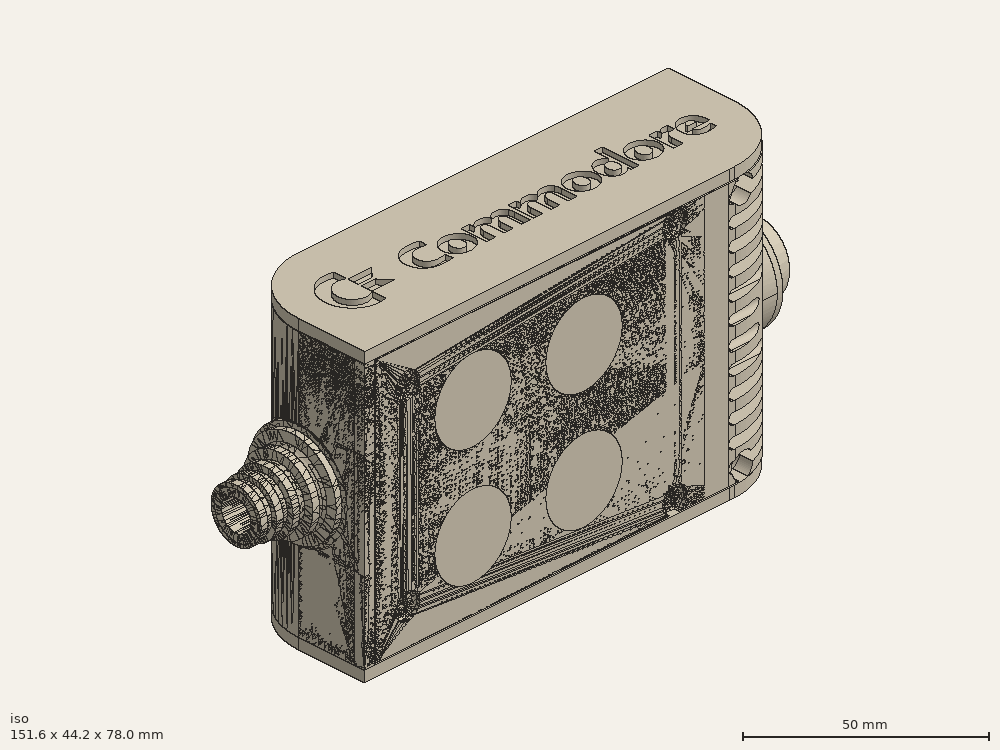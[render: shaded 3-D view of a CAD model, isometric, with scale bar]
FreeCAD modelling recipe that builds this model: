
FCSTD DOCUMENT  (FreeCAD 0.19R0.19.2)
Label: enclosure_221FCStd
License: All rights reserved
LicenseURL: http://en.wikipedia.org/wiki/All_rights_reserved
objects: Part::Revolution×152, Part::MultiFuse×146, Part::Feature×146, Sketcher::SketchObject×89, Part::Extrusion×74, Part::Cut×72, Part::Cylinder×70, Part::Fillet×58, Part::Box×38, App::MeasureDistance×4, Part::Chamfer×4, Part::FeaturePython×2, Image::ImagePlane×1, PartDesign::Body×1, Part::Mirroring×1
note: 853 computed .brp shape members not serialized (recipe doc carries the construction recipe); baked Part::Feature solids carry a one-line shape summary decoded from their .brp

FEATURE [Sketcher::SketchObject] Sketch  label="topSketch"
  FullyConstrained = true
  sketch-geometry (20):
    g0: LineSegment StartX=5.21097e-06 StartY=3 StartZ=0 EndX=5.21097e-06 EndY=19 EndZ=0
    g1: ArcOfCircle CenterX=19 CenterY=19 CenterZ=0 NormalX=0 NormalY=0 NormalZ=1 AngleXU=0 Radius=19 StartAngle=1.5708 EndAngle=3.14159
    g2: ArcOfCircle CenterX=19 CenterY=19 CenterZ=0 NormalX=0 NormalY=0 NormalZ=1 AngleXU=0 Radius=16 StartAngle=1.5708 EndAngle=3.14159
    g3: LineSegment StartX=114 StartY=35 StartZ=0 EndX=19 EndY=35 EndZ=0
    g4: LineSegment StartX=5.21097e-06 StartY=3 StartZ=0 EndX=5.21097e-06 EndY=0 EndZ=0
    g5: LineSegment StartX=3 StartY=0 StartZ=0 EndX=5.21097e-06 EndY=0 EndZ=0
    g6: LineSegment StartX=3 StartY=19 StartZ=0 EndX=3 EndY=0 EndZ=0
    g7: LineSegment StartX=19 StartY=38 StartZ=0 EndX=124 EndY=38 EndZ=0
    g8: Circle CenterX=119 CenterY=35 CenterZ=0 NormalX=0 NormalY=0 NormalZ=1 AngleXU=0 Radius=1
    g9: Circle CenterX=121 CenterY=35 CenterZ=0 NormalX=0 NormalY=0 NormalZ=1 AngleXU=0 Radius=1
    g10: Circle CenterX=121 CenterY=33 CenterZ=0 NormalX=0 NormalY=0 NormalZ=1 AngleXU=0 Radius=1
    g11: BSplineCurve PolesCount=3 KnotsCount=2 Degree=2 IsPeriodic=0
    g12: GeomPoint X=119 Y=35 Z=0
    g13: GeomPoint X=121 Y=33 Z=0
    g14: LineSegment StartX=119 StartY=35 StartZ=0 EndX=114 EndY=35 EndZ=0
    g15: ArcOfCircle CenterX=105 CenterY=19 CenterZ=0 NormalX=0 NormalY=0 NormalZ=1 AngleXU=0 Radius=19 StartAngle=5.7297 EndAngle=6.28319
    g16: ArcOfCircle CenterX=105 CenterY=19 CenterZ=0 NormalX=0 NormalY=0 NormalZ=1 AngleXU=0 Radius=16 StartAngle=5.60905 EndAngle=6.28319
    g17: LineSegment StartX=121 StartY=33 StartZ=0 EndX=121 EndY=19 EndZ=0
    g18: LineSegment StartX=124 StartY=38 StartZ=0 EndX=124 EndY=19 EndZ=0
    g19: LineSegment StartX=117.5 StartY=9.01251 StartZ=0 EndX=121.163 EndY=9.0125 EndZ=0
  constraints (46):
    c: Vertical(g0)
    c: Block(g0)
    c: Coincident(g1,g0)
    c: Block(g1)
    c: Coincident(g2,g1)
    c: Block(g2)
    c: Coincident(g3,g2)
    c: Horizontal(g3)
    c: Tangent(g3,g2)
    c: Coincident(g4,g0)
    c: Distance(g4) = 3
    c: Vertical(g4)
    c: Coincident(g5,g4)
    c: Horizontal(g5)
    c: Coincident(g6,g2)
    c: Coincident(g6,g5)
    c: Vertical(g6)
    c: Horizontal(g7)
    c: Distance(g7) = 105
    c: Coincident(g7,g1)
    c: Block(g3)
    c: Weight(g8) = 1
    c: Equal(g8,g9)
    c: Equal(g8,g10)
    c: InternalAlignment(g8,g11)
    c: InternalAlignment(g9,g11)
    c: InternalAlignment(g10,g11)
    c: InternalAlignment(g12,g11)
    c: InternalAlignment(g13,g11)
    c: Block(g11)
    c: Coincident(g14,g11)
    c: Coincident(g14,g3)
    c: Horizontal(g14)
    c: Block(g15)
    c: Coincident(g16,g15)
    c: Block(g16)
    c: Coincident(g17,g11)
    c: Coincident(g17,g16)
    c: Vertical(g17)
    c: Distance(g17) = 14
    c: Coincident(g18,g7)
    c: Coincident(g18,g15)
    c: Vertical(g18)
    c: Distance(g18) = 19
    c: Coincident(g19,g16)
    c: Coincident(g19,g15)
FEATURE [Sketcher::SketchObject] Sketch001  label="bottomSketch"
  FullyConstrained = true
  sketch-geometry (32):
    g0: LineSegment StartX=3.3 StartY=-6.03275e-07 StartZ=0 EndX=98 EndY=-6.03275e-07 EndZ=0
    g1: ArcOfCircle CenterX=98 CenterY=19 CenterZ=0 NormalX=0 NormalY=0 NormalZ=1 AngleXU=0 Radius=19 StartAngle=4.71239 EndAngle=5.71103
    g2: LineSegment StartX=6.3 StartY=8 StartZ=0 EndX=3.3 EndY=8 EndZ=0
    g3: LineSegment StartX=3.3 StartY=8 StartZ=0 EndX=3.3 EndY=-6.03275e-07 EndZ=0
    g4: ArcOfCircle CenterX=8.3 CenterY=5 CenterZ=0 NormalX=0 NormalY=0 NormalZ=1 AngleXU=0 Radius=2 StartAngle=3.14159 EndAngle=4.71239
    g5: LineSegment StartX=6.3 StartY=8 StartZ=0 EndX=6.3 EndY=5 EndZ=0
    g6: ArcOfCircle CenterX=98 CenterY=19 CenterZ=0 NormalX=0 NormalY=0 NormalZ=1 AngleXU=0 Radius=12.7 StartAngle=4.71239 EndAngle=6.28319
    g7: LineSegment StartX=94.7 StartY=3 StartZ=0 EndX=8.3 EndY=3 EndZ=0
    g8-g12: Circle x5 (B-spline internal-alignment scaffolding for g13; pole/knot coordinates omitted)
    g13: BSplineCurve PolesCount=5 KnotsCount=3 Degree=3 IsPeriodic=0
    g14: GeomPoint X=98 Y=6.3 Z=0
    g15: GeomPoint X=96.3938 Y=4.71946 Z=0
    g16: GeomPoint X=94.7 Y=3 Z=0
    g17-g23: Circle x7 (B-spline internal-alignment scaffolding for g24; pole/knot coordinates omitted)
    g24: BSplineCurve PolesCount=7 KnotsCount=5 Degree=3 IsPeriodic=0
    g25-g29: GeomPoint x5 (B-spline internal-alignment scaffolding for g24; pole/knot coordinates omitted)
    g30: ArcOfCircle CenterX=98 CenterY=19 CenterZ=0 NormalX=0 NormalY=0 NormalZ=1 AngleXU=0 Radius=15.7 StartAngle=5.81226 EndAngle=6.28319
    g31: LineSegment StartX=110.7 StartY=19 StartZ=0 EndX=113.7 EndY=19 EndZ=0
  constraints (41):
    c: Horizontal(g0)
    c: Coincident(g1,g0)
    c: Block(g1)
    c: Horizontal(g2)
    c: Distance(g2) = 3
    c: Coincident(g3,g2)
    c: Vertical(g3)
    c: Coincident(g3,g0)
    c: Block(g4)
    c: Block(g2)
    c: Coincident(g5,g2)
    c: Coincident(g5,g4)
    c: Vertical(g5)
    c: Coincident(g6,g1)
    c: Block(g6)
    c: Coincident(g7,g4)
    c: Horizontal(g7)
    c: Block(g0)
    c: Block(g7)
    c: Block(g3)
    c: Coincident(g13,g6)
    c: Weight(g8) = 1
    c: Equal(g8, g9-g12) x4
    c: Coincident(g13,g7)
    c: InternalAlignment(g8-g12 -> g13) x5
    c: InternalAlignment(g14,g13)
    c: InternalAlignment(g15,g13)
    c: InternalAlignment(g16,g13)
    c: Block(g13)
    c: Weight(g17) = 1
    c: Equal(g17, g18-g23) x6
    c: Coincident(g24,g1)
    c: InternalAlignment(g17-g23 -> g24) x7
    c: InternalAlignment(g25-g29 -> g24) x5
    c: Block(g24)
    c: Coincident(g30,g24)
    c: Coincident(g31,g6)
    c: Coincident(g31,g30)
    c: Horizontal(g31)
    c: Block(g31)
    c: Block(g30)
FEATURE [Part::Extrusion] Extrude  label="top"
  Base = -> Sketch
  Dir = (0,0,1)
  DirMode = 2
  FaceMakerClass = Part::FaceMakerBullseye
  LengthFwd = 72
  LengthRev = 0
  Solid = true
  Symmetric = false
FEATURE [Part::Extrusion] Extrude001  label="bottom"
  Base = -> Sketch001
  Dir = (0,0,1)
  DirMode = 2
  FaceMakerClass = Part::FaceMakerBullseye
  LengthFwd = 71.4
  LengthRev = 0
  Placement = pos=(0,0,0.3) rot=(0,0,1;0rad)
  Solid = true
  Symmetric = false
FEATURE [Sketcher::SketchObject] Sketch002  label="topSketch001"
  FullyConstrained = true
  sketch-geometry (8):
    g0: ArcOfCircle CenterX=19 CenterY=19.0975 CenterZ=0 NormalX=0 NormalY=0 NormalZ=1 AngleXU=0 Radius=18.9025 StartAngle=1.5708 EndAngle=3.14674
    g1: LineSegment StartX=0.0977805 StartY=19.0003 StartZ=0 EndX=0.0977805 EndY=0.000251602 EndZ=0
    g2: LineSegment StartX=19 StartY=38 StartZ=0 EndX=124 EndY=38 EndZ=0
    g3: LineSegment StartX=0.0977805 StartY=0.000251602 StartZ=0 EndX=105.098 EndY=0.000251602 EndZ=0
    g4: LineSegment StartX=124 StartY=38 StartZ=0 EndX=125.616 EndY=38 EndZ=0
    g5: LineSegment StartX=105.098 StartY=0.000251602 StartZ=0 EndX=106.713 EndY=0.000251602 EndZ=0
    g6: ArcOfCircle CenterX=106.616 CenterY=19 CenterZ=0 NormalX=0 NormalY=0 NormalZ=1 AngleXU=0 Radius=19 StartAngle=4.71754 EndAngle=6.28319
    g7: LineSegment StartX=125.616 StartY=38 StartZ=0 EndX=125.616 EndY=19 EndZ=0
  constraints (21):
    c: Block(g0)
    c: Coincident(g1,g0)
    c: Vertical(g1)
    c: Horizontal(g2)
    c: Distance(g2) = 105
    c: Coincident(g2,g0)
    c: Distance(g1) = 19
    c: Coincident(g3,g1)
    c: Horizontal(g3)
    c: Distance(g3) = 105
    c: Coincident(g4,g2)
    c: Horizontal(g4)
    c: Distance(g4) = 1.61553
    c: Horizontal(g5)
    c: Equal(g4,g5) = 1.61553
    c: Coincident(g5,g3)
    c: Block(g6)
    c: Coincident(g6,g5)
    c: Coincident(g7,g4)
    c: Coincident(g7,g6)
    c: Vertical(g7)
FEATURE [Part::Extrusion] Extrude002  label="sideA"
  Base = -> Sketch002
  Dir = (0,0,1)
  DirMode = 2
  FaceMakerClass = Part::FaceMakerBullseye
  LengthFwd = 3
  LengthRev = 0
  Placement = pos=(0,0,-3) rot=(0,0,1;0rad)
  Solid = true
  Symmetric = false
FEATURE [Sketcher::SketchObject] Sketch003  label="topSketch002"
  FullyConstrained = true
  sketch-geometry (6):
    g0: LineSegment StartX=19 StartY=38 StartZ=0 EndX=117 EndY=38 EndZ=0
    g1: ArcOfCircle CenterX=19 CenterY=19 CenterZ=0 NormalX=0 NormalY=0 NormalZ=1 AngleXU=0 Radius=19 StartAngle=1.5708 EndAngle=3.14159
    g2: LineSegment StartX=117 StartY=38 StartZ=0 EndX=117 EndY=19 EndZ=0
    g3: LineSegment StartX=98 StartY=1.0161e-12 StartZ=0 EndX=5.22862e-06 EndY=1.0161e-12 EndZ=0
    g4: LineSegment StartX=5.22862e-06 StartY=19 StartZ=0 EndX=5.22862e-06 EndY=1.0161e-12 EndZ=0
    g5: ArcOfCircle CenterX=98 CenterY=19 CenterZ=0 NormalX=0 NormalY=0 NormalZ=1 AngleXU=0 Radius=19 StartAngle=4.71239 EndAngle=6.28319
  constraints (16):
    c: Horizontal(g0)
    c: Distance(g0) = 98
    c: Coincident(g1,g0)
    c: Block(g1)
    c: Coincident(g2,g0)
    c: Vertical(g2)
    c: Distance(g2) = 19
    c: Horizontal(g3)
    c: Coincident(g4,g1)
    c: Vertical(g4)
    c: Coincident(g3,g4)
    c: Block(g3)
    c: Coincident(g5,g2)
    c: Coincident(g5,g3)
    c: Block(g0)
    c: Block(g5)
FEATURE [Sketcher::SketchObject] Sketch004
  FullyConstrained = true
  MapMode = 3
  Placement = pos=(0,0,0) rot=(1,0,0;1.5708rad)
  Support = -> [Extrude]
  sketch-geometry (8):
    g0: Circle CenterX=80.351 CenterY=-67.6202 CenterZ=0 NormalX=0 NormalY=0 NormalZ=1 AngleXU=0 Radius=2
    g1: Circle CenterX=80.351 CenterY=-67.6202 CenterZ=0 NormalX=0 NormalY=0 NormalZ=1 AngleXU=0 Radius=3
    g2: Circle CenterX=80.351 CenterY=-4.92017 CenterZ=0 NormalX=0 NormalY=0 NormalZ=1 AngleXU=0 Radius=2
    g3: Circle CenterX=80.351 CenterY=-4.92017 CenterZ=0 NormalX=0 NormalY=0 NormalZ=1 AngleXU=0 Radius=3
    g4: Circle CenterX=23.851 CenterY=-4.92017 CenterZ=0 NormalX=0 NormalY=0 NormalZ=1 AngleXU=0 Radius=2
    g5: Circle CenterX=23.851 CenterY=-4.92017 CenterZ=0 NormalX=0 NormalY=0 NormalZ=1 AngleXU=0 Radius=3
    g6: Circle CenterX=23.851 CenterY=-67.6202 CenterZ=0 NormalX=0 NormalY=0 NormalZ=1 AngleXU=0 Radius=2
    g7: Circle CenterX=23.851 CenterY=-67.6202 CenterZ=0 NormalX=0 NormalY=0 NormalZ=1 AngleXU=0 Radius=3
  constraints (8):
    c: Block(g3)
    c: Block(g2)
    c: Block(g1)
    c: Block(g0)
    c: Block(g6)
    c: Block(g7)
    c: Block(g4)
    c: Block(g5)
FEATURE [Part::Extrusion] Extrude004
  Base = -> Sketch004
  Dir = (0,-1,2e-16)
  DirMode = 2
  FaceMakerClass = Part::FaceMakerBullseye
  LengthFwd = 6
  LengthRev = 0
  Placement = pos=(0,9,0) rot=(0,0,1;0rad)
  Solid = true
  Symmetric = false
FEATURE [Sketcher::SketchObject] Sketch005
  FullyConstrained = true
  MapMode = 3
  Placement = pos=(0,0,0) rot=(1,0,0;1.5708rad)
  Support = -> [Extrude]
  sketch-geometry (8):
    g0: Circle CenterX=80.351 CenterY=-67.6202 CenterZ=0 NormalX=0 NormalY=0 NormalZ=1 AngleXU=0 Radius=3
    g1: Circle CenterX=80.351 CenterY=-4.92017 CenterZ=0 NormalX=0 NormalY=0 NormalZ=1 AngleXU=0 Radius=3
    g2: Circle CenterX=23.851 CenterY=-4.92017 CenterZ=0 NormalX=0 NormalY=0 NormalZ=1 AngleXU=0 Radius=3
    g3: Circle CenterX=23.851 CenterY=-67.6202 CenterZ=0 NormalX=0 NormalY=0 NormalZ=1 AngleXU=0 Radius=3
    g4: Circle CenterX=23.851 CenterY=-67.6202 CenterZ=0 NormalX=0 NormalY=0 NormalZ=1 AngleXU=0 Radius=5
    g5: Circle CenterX=80.351 CenterY=-67.6202 CenterZ=0 NormalX=0 NormalY=0 NormalZ=1 AngleXU=0 Radius=5
    g6: Circle CenterX=23.851 CenterY=-4.92017 CenterZ=0 NormalX=0 NormalY=0 NormalZ=1 AngleXU=0 Radius=5
    g7: Circle CenterX=80.351 CenterY=-4.92017 CenterZ=0 NormalX=0 NormalY=0 NormalZ=1 AngleXU=0 Radius=5
  constraints (8):
    c: Block(g1)
    c: Block(g0)
    c: Block(g3)
    c: Block(g2)
    c: Block(g5)
    c: Block(g4)
    c: Block(g6)
    c: Block(g7)
FEATURE [Part::Extrusion] Extrude005
  Base = -> Sketch005
  Dir = (0,-1,2e-16)
  DirMode = 2
  FaceMakerClass = Part::FaceMakerBullseye
  LengthFwd = 2
  LengthRev = 0
  Solid = true
  Symmetric = false
FEATURE [Sketcher::SketchObject] Sketch006
  FullyConstrained = true
  MapMode = 3
  Placement = pos=(0,0,0) rot=(1,0,0;1.5708rad)
  sketch-geometry (8):
    g0: Circle CenterX=80.351 CenterY=-67.6202 CenterZ=0 NormalX=0 NormalY=0 NormalZ=1 AngleXU=0 Radius=3
    g1: Circle CenterX=80.351 CenterY=-4.92017 CenterZ=0 NormalX=0 NormalY=0 NormalZ=1 AngleXU=0 Radius=3
    g2: Circle CenterX=23.851 CenterY=-4.92017 CenterZ=0 NormalX=0 NormalY=0 NormalZ=1 AngleXU=0 Radius=3
    g3: Circle CenterX=23.851 CenterY=-67.6202 CenterZ=0 NormalX=0 NormalY=0 NormalZ=1 AngleXU=0 Radius=3
    g4: Circle CenterX=23.851 CenterY=-67.6202 CenterZ=0 NormalX=0 NormalY=0 NormalZ=1 AngleXU=0 Radius=5
    g5: Circle CenterX=80.351 CenterY=-67.6202 CenterZ=0 NormalX=0 NormalY=0 NormalZ=1 AngleXU=0 Radius=5
    g6: Circle CenterX=23.851 CenterY=-4.92017 CenterZ=0 NormalX=0 NormalY=0 NormalZ=1 AngleXU=0 Radius=5
    g7: Circle CenterX=80.351 CenterY=-4.92017 CenterZ=0 NormalX=0 NormalY=0 NormalZ=1 AngleXU=0 Radius=5
  constraints (8):
    c: Block(g1)
    c: Block(g0)
    c: Block(g3)
    c: Block(g2)
    c: Block(g5)
    c: Block(g4)
    c: Block(g6)
    c: Block(g7)
FEATURE [Part::Extrusion] Extrude007
  Base = -> Sketch006
  Dir = (0,-1,2e-16)
  DirMode = 2
  FaceMakerClass = Part::FaceMakerBullseye
  LengthFwd = 2
  LengthRev = 0
  Solid = true
  Symmetric = false
FEATURE [Part::Fillet] Fillet
  Base = -> Extrude007
  Edges = 4 edges r=1.99: [Edge6,Edge12,Edge18,Edge24]
FEATURE [Part::Cut] Cut
  Base = -> Extrude005
  Placement = pos=(0,5,0) rot=(0,0,1;0rad)
  Tool = -> Fillet
FEATURE [Part::MultiFuse] Fusion  label="pCBScrews"
  Placement = pos=(-2.5,0,72.3) rot=(0,0,1;0rad)
  Shapes = -> [Extrude004,Cut]
FEATURE [App::MeasureDistance] Distance  label="Distance: 0.69 mm"
  Distance = 0.685967
  P1 = (24.0138,2.9647,0.3)
  P2 = (23.8901,3,-0.373787)
FEATURE [App::MeasureDistance] Distance001  label="Distance: 0.53 mm"
  Distance = 0.533607
  P1 = (80.2939,3,72.2334)
  P2 = (80.281,2.99661,71.7)
FEATURE [Part::Fillet] Fillet001
  Base = -> Extrude001
  Edges = 1 edges r=2.4: [Edge17]
FEATURE [Part::Fillet] Fillet002  label="bottom001"
  Base = -> Fillet001
  Edges = 1 edges r=2.4: [Edge36]
FEATURE [Part::Fillet] Fillet003  label="top001"
  Base = -> Extrude
  Edges = 1 edges r=2: [Edge1]
FEATURE [Sketcher::SketchObject] Sketch007
  FullyConstrained = true
  sketch-geometry (16):
    g0: LineSegment StartX=4 StartY=0 StartZ=0 EndX=4 EndY=2.4 EndZ=0
    g1: LineSegment StartX=4 StartY=2.4 StartZ=0 EndX=7 EndY=2.4 EndZ=0
    g2: LineSegment StartX=4 StartY=0 StartZ=0 EndX=5.7 EndY=0 EndZ=0
    g3: LineSegment StartX=5.7 StartY=0 StartZ=0 EndX=5.7 EndY=-5.6 EndZ=0
    g4-g8: Circle x5 (B-spline internal-alignment scaffolding for g9; pole/knot coordinates omitted)
    g9: BSplineCurve PolesCount=5 KnotsCount=3 Degree=3 IsPeriodic=0
    g10: GeomPoint X=7 Y=2.4 Z=0
    g11: GeomPoint X=10.4582 Y=-1.55472 Z=0
    g12: GeomPoint X=14 Y=-5.6 Z=0
    g13: LineSegment StartX=14 StartY=-5.6 StartZ=0 EndX=14 EndY=-14.1 EndZ=0
    g14: LineSegment StartX=14 StartY=-14.1 StartZ=0 EndX=6.5 EndY=-14.1 EndZ=0
    g15: LineSegment StartX=5.7 StartY=-5.6 StartZ=0 EndX=6.5 EndY=-14.1 EndZ=0
  constraints (28):
    c: Distance(g0) = 2.4
    c: Vertical(g0)
    c: Block(g0)
    c: Coincident(g1,g0)
    c: Horizontal(g1)
    c: Distance(g1) = 3
    c: Coincident(g2,g0)
    c: Horizontal(g2)
    c: Distance(g2) = 1.7
    c: Coincident(g3,g2)
    c: Vertical(g3)
    c: Distance(g3) = 5.6
    c: Coincident(g9,g1)
    c: Weight(g4) = 1
    c: Equal(g4, g5-g8) x4
    c: InternalAlignment(g4-g8 -> g9) x5
    c: InternalAlignment(g10,g9)
    c: InternalAlignment(g11,g9)
    c: InternalAlignment(g12,g9)
    c: Block(g9)
    c: Coincident(g13,g9)
    c: Vertical(g13)
    c: Distance(g13) = 8.5
    c: Coincident(g14,g13)
    c: Horizontal(g14)
    c: Distance(g14) = 7.5
    c: Coincident(g15,g3)
    c: Coincident(g15,g14)
FEATURE [Part::Feature] Face
  shape: bbox 10 x 16.5 x 2e-07 mm, 1 faces, 0 solids (baked)
FEATURE [Part::Revolution] Revolve  label="plugHousing"
  Angle = 360
  Axis = (0,1,0)
  Base = (0,0,0)
  FaceMakerClass = Part::FaceMakerBullseye
  Placement = pos=(0,0,36.15) rot=(0,0,1;0rad)
  Solid = false
  Source = -> Face
  Symmetric = false
FEATURE [Part::Feature] Face001
  shape: bbox 10 x 16.5 x 2e-07 mm, 1 faces, 0 solids (baked)
FEATURE [Part::Revolution] Revolve001  label="plugHousing001"
  Angle = 360
  Axis = (0,1,0)
  Base = (0,0,0)
  FaceMakerClass = Part::FaceMakerBullseye
  Placement = pos=(0,0,36.15) rot=(0,0,1;0rad)
  Solid = false
  Source = -> Face001
  Symmetric = false
FEATURE [Part::MultiFuse] Fusion001  label="plugHousing002"
  Placement = pos=(0,0,0) rot=(0,0,1;1.5708rad)
  Shapes = -> [Revolve001,Revolve]
FEATURE [Part::Feature] Face002
  shape: bbox 10 x 16.5 x 2e-07 mm, 1 faces, 0 solids (baked)
FEATURE [Part::Revolution] Revolve003  label="plugHousing005"
  Angle = 360
  Axis = (0,1,0)
  Base = (0,0,0)
  FaceMakerClass = Part::FaceMakerBullseye
  Placement = pos=(0,0,36.15) rot=(0,0,1;0rad)
  Solid = false
  Source = -> Face002
  Symmetric = false
FEATURE [Part::Feature] Face003
  shape: bbox 10 x 16.5 x 2e-07 mm, 1 faces, 0 solids (baked)
FEATURE [Part::Revolution] Revolve002  label="plugHousing003"
  Angle = 360
  Axis = (0,1,0)
  Base = (0,0,0)
  FaceMakerClass = Part::FaceMakerBullseye
  Placement = pos=(0,0,36.15) rot=(0,0,1;0rad)
  Solid = false
  Source = -> Face003
  Symmetric = false
FEATURE [Part::MultiFuse] Fusion002  label="plugHousing004"
  Placement = pos=(0,0,0) rot=(0,0,1;1.5708rad)
  Shapes = -> [Revolve002,Revolve003]
FEATURE [Part::MultiFuse] Fusion003  label="plugHousing006"
  Placement = pos=(0,19,0) rot=(0,0,1;3.14159rad)
  Shapes = -> [Fusion002,Fusion001]
FEATURE [Part::Feature] Face004
  shape: bbox 10 x 16.5 x 2e-07 mm, 1 faces, 0 solids (baked)
FEATURE [Part::Revolution] Revolve006  label="plugHousing010"
  Angle = 360
  Axis = (0,1,0)
  Base = (0,0,0)
  FaceMakerClass = Part::FaceMakerBullseye
  Placement = pos=(0,0,36.15) rot=(0,0,1;0rad)
  Solid = false
  Source = -> Face004
  Symmetric = false
FEATURE [Part::Feature] Face005
  shape: bbox 10 x 16.5 x 2e-07 mm, 1 faces, 0 solids (baked)
FEATURE [Part::Revolution] Revolve007  label="plugHousing011"
  Angle = 360
  Axis = (0,1,0)
  Base = (0,0,0)
  FaceMakerClass = Part::FaceMakerBullseye
  Placement = pos=(0,0,36.15) rot=(0,0,1;0rad)
  Solid = false
  Source = -> Face005
  Symmetric = false
FEATURE [Part::Feature] Face006
  shape: bbox 10 x 16.5 x 2e-07 mm, 1 faces, 0 solids (baked)
FEATURE [Part::Revolution] Revolve004  label="plugHousing007"
  Angle = 360
  Axis = (0,1,0)
  Base = (0,0,0)
  FaceMakerClass = Part::FaceMakerBullseye
  Placement = pos=(0,0,36.15) rot=(0,0,1;0rad)
  Solid = false
  Source = -> Face006
  Symmetric = false
FEATURE [Part::MultiFuse] Fusion004  label="plugHousing009"
  Placement = pos=(0,0,0) rot=(0,0,1;1.5708rad)
  Shapes = -> [Revolve004,Revolve007]
FEATURE [Part::Feature] Face007
  shape: bbox 10 x 16.5 x 2e-07 mm, 1 faces, 0 solids (baked)
FEATURE [Part::Revolution] Revolve005  label="plugHousing008"
  Angle = 360
  Axis = (0,1,0)
  Base = (0,0,0)
  FaceMakerClass = Part::FaceMakerBullseye
  Placement = pos=(0,0,36.15) rot=(0,0,1;0rad)
  Solid = false
  Source = -> Face007
  Symmetric = false
FEATURE [Part::MultiFuse] Fusion005  label="plugHousing012"
  Placement = pos=(0,0,0) rot=(0,0,1;1.5708rad)
  Shapes = -> [Revolve006,Revolve005]
FEATURE [Part::MultiFuse] Fusion006  label="plugHousing013"
  Placement = pos=(0,19,0) rot=(0,0,1;3.14159rad)
  Shapes = -> [Fusion005,Fusion004]
FEATURE [Part::MultiFuse] Fusion007  label="plugHousing014"
  Placement = pos=(122.621,0,-0.15) rot=(0,0,1;0rad)
  Shapes = -> [Fusion003,Fusion006]
FEATURE [Part::Cylinder] Cylinder002
  Angle = 360
  AttacherType = Attacher::AttachEngine3D
  Height = 20
  Placement = pos=(0,0,36.15) rot=(0,0,1;0rad)
  Radius = 4
FEATURE [Part::Cylinder] Cylinder003
  Angle = 360
  AttacherType = Attacher::AttachEngine3D
  Height = 10
  Placement = pos=(0,0,36.15) rot=(0,0,1;0rad)
  Radius = 4
FEATURE [Part::MultiFuse] Fusion009  label="removeToCreateHoleForPlugHousing"
  Placement = pos=(70,19,36.15) rot=(0,1,0;1.5708rad)
  Shapes = -> [Cylinder002,Cylinder003]
FEATURE [Part::Cylinder] Cylinder004
  Angle = 360
  AttacherType = Attacher::AttachEngine3D
  Height = 20
  Placement = pos=(0,0,36.15) rot=(0,0,1;0rad)
  Radius = 4
FEATURE [Part::Cylinder] Cylinder005
  Angle = 360
  AttacherType = Attacher::AttachEngine3D
  Height = 10
  Placement = pos=(0,0,36.15) rot=(0,0,1;0rad)
  Radius = 4
FEATURE [Part::MultiFuse] Fusion010  label="removeToCreateHoleForPlugHousing001"
  Placement = pos=(70,19,36.15) rot=(0,1,0;1.5708rad)
  Shapes = -> [Cylinder004,Cylinder005]
FEATURE [Part::Cut] Cut001
  Base = -> Fillet003
  Tool = -> Fusion010
FEATURE [Part::Cut] Cut002  label="Bottom"
  Base = -> Fillet002
  Tool = -> Fusion009
FEATURE [Part::Feature] Face008
  shape: bbox 10 x 16.5 x 2e-07 mm, 1 faces, 0 solids (baked)
FEATURE [Part::Revolution] Revolve011  label="plugHousing021"
  Angle = 360
  Axis = (0,1,0)
  Base = (0,0,0)
  FaceMakerClass = Part::FaceMakerBullseye
  Placement = pos=(0,0,36.15) rot=(0,0,1;0rad)
  Solid = false
  Source = -> Face008
  Symmetric = false
FEATURE [Part::Feature] Face009
  shape: bbox 10 x 16.5 x 2e-07 mm, 1 faces, 0 solids (baked)
FEATURE [Part::Revolution] Revolve012  label="plugHousing022"
  Angle = 360
  Axis = (0,1,0)
  Base = (0,0,0)
  FaceMakerClass = Part::FaceMakerBullseye
  Placement = pos=(0,0,36.15) rot=(0,0,1;0rad)
  Solid = false
  Source = -> Face009
  Symmetric = false
FEATURE [Part::Feature] Face010 .. Face013  x4 (patterned run collapsed; names and placements below)
  shape: bbox 10 x 16.5 x 2e-07 mm, 1 faces, 0 solids (baked)
FEATURE [Part::Revolution] Revolve015  label="plugHousing027"
  Angle = 360
  Axis = (0,1,0)
  Base = (0,0,0)
  FaceMakerClass = Part::FaceMakerBullseye
  Placement = pos=(0,0,36.15) rot=(0,0,1;0rad)
  Solid = false
  Source = -> Face013
  Symmetric = false
FEATURE [Part::Feature] Face014
  shape: bbox 10 x 16.5 x 2e-07 mm, 1 faces, 0 solids (baked)
FEATURE [Part::Feature] Face015
  shape: bbox 10 x 16.5 x 2e-07 mm, 1 faces, 0 solids (baked)
FEATURE [Part::Feature] Face016
  shape: bbox 10 x 16.5 x 2e-07 mm, 1 faces, 0 solids (baked)
FEATURE [Part::Revolution] Revolve019  label="plugHousing033"
  Angle = 360
  Axis = (0,1,0)
  Base = (0,0,0)
  FaceMakerClass = Part::FaceMakerBullseye
  Placement = pos=(0,0,36.15) rot=(0,0,1;0rad)
  Solid = false
  Source = -> Face016
  Symmetric = false
FEATURE [Part::Feature] Face017
  shape: bbox 10 x 16.5 x 2e-07 mm, 1 faces, 0 solids (baked)
FEATURE [Part::Revolution] Revolve020  label="plugHousing034"
  Angle = 360
  Axis = (0,1,0)
  Base = (0,0,0)
  FaceMakerClass = Part::FaceMakerBullseye
  Placement = pos=(0,0,36.15) rot=(0,0,1;0rad)
  Solid = false
  Source = -> Face017
  Symmetric = false
FEATURE [Part::Feature] Face018
  shape: bbox 10 x 16.5 x 2e-07 mm, 1 faces, 0 solids (baked)
FEATURE [Part::Revolution] Revolve016  label="plugHousing030"
  Angle = 360
  Axis = (0,1,0)
  Base = (0,0,0)
  FaceMakerClass = Part::FaceMakerBullseye
  Placement = pos=(0,0,36.15) rot=(0,0,1;0rad)
  Solid = false
  Source = -> Face018
  Symmetric = false
FEATURE [Part::MultiFuse] Fusion020  label="plugHousing038"
  Placement = pos=(0,0,0) rot=(0,0,1;1.5708rad)
  Shapes = -> [Revolve016,Revolve020]
FEATURE [Part::Feature] Face019
  shape: bbox 10 x 16.5 x 2e-07 mm, 1 faces, 0 solids (baked)
FEATURE [Part::Feature] Face020
  shape: bbox 10 x 16.5 x 2e-07 mm, 1 faces, 0 solids (baked)
FEATURE [Part::Revolution] Revolve017  label="plugHousing031"
  Angle = 360
  Axis = (0,1,0)
  Base = (0,0,0)
  FaceMakerClass = Part::FaceMakerBullseye
  Placement = pos=(0,0,36.15) rot=(0,0,1;0rad)
  Solid = false
  Source = -> Face020
  Symmetric = false
FEATURE [Part::MultiFuse] Fusion021  label="plugHousing039"
  Placement = pos=(0,0,0) rot=(0,0,1;1.5708rad)
  Shapes = -> [Revolve019,Revolve017]
FEATURE [Part::MultiFuse] Fusion023  label="plugHousing041"
  Placement = pos=(0,19,0) rot=(0,0,1;3.14159rad)
  Shapes = -> [Fusion021,Fusion020]
FEATURE [Part::Revolution] Revolve022  label="plugHousing043"
  Angle = 360
  Axis = (0,1,0)
  Base = (0,0,0)
  FaceMakerClass = Part::FaceMakerBullseye
  Placement = pos=(0,0,36.15) rot=(0,0,1;0rad)
  Solid = false
  Source = -> Face019
  Symmetric = false
FEATURE [Part::Feature] Face021
  shape: bbox 10 x 16.5 x 2e-07 mm, 1 faces, 0 solids (baked)
FEATURE [Part::Revolution] Revolve023  label="plugHousing044"
  Angle = 360
  Axis = (0,1,0)
  Base = (0,0,0)
  FaceMakerClass = Part::FaceMakerBullseye
  Placement = pos=(0,0,36.15) rot=(0,0,1;0rad)
  Solid = false
  Source = -> Face021
  Symmetric = false
FEATURE [Part::Feature] Face022
  shape: bbox 10 x 16.5 x 2e-07 mm, 1 faces, 0 solids (baked)
FEATURE [Part::Revolution] Revolve018  label="plugHousing032"
  Angle = 360
  Axis = (0,1,0)
  Base = (0,0,0)
  FaceMakerClass = Part::FaceMakerBullseye
  Placement = pos=(0,0,36.15) rot=(0,0,1;0rad)
  Solid = false
  Source = -> Face022
  Symmetric = false
FEATURE [Part::MultiFuse] Fusion022  label="plugHousing040"
  Placement = pos=(0,0,0) rot=(0,0,1;1.5708rad)
  Shapes = -> [Revolve018,Revolve023]
FEATURE [Part::Feature] Face023
  shape: bbox 10 x 16.5 x 2e-07 mm, 1 faces, 0 solids (baked)
FEATURE [Part::Revolution] Revolve021  label="plugHousing035"
  Angle = 360
  Axis = (0,1,0)
  Base = (0,0,0)
  FaceMakerClass = Part::FaceMakerBullseye
  Placement = pos=(0,0,36.15) rot=(0,0,1;0rad)
  Solid = false
  Source = -> Face023
  Symmetric = false
FEATURE [Part::MultiFuse] Fusion018  label="plugHousing036"
  Placement = pos=(0,0,0) rot=(0,0,1;1.5708rad)
  Shapes = -> [Revolve022,Revolve021]
FEATURE [Part::MultiFuse] Fusion019  label="plugHousing037"
  Placement = pos=(0,19,0) rot=(0,0,1;3.14159rad)
  Shapes = -> [Fusion018,Fusion022]
FEATURE [Part::MultiFuse] Fusion024  label="plugHousing042"
  Placement = pos=(122.621,0,-0.15) rot=(0,0,1;0rad)
  Shapes = -> [Fusion023,Fusion019]
FEATURE [Part::Cylinder] Cylinder006
  Angle = 360
  AttacherType = Attacher::AttachEngine3D
  Height = 20
  Placement = pos=(0,0,36.15) rot=(0,0,1;0rad)
  Radius = 14.3
FEATURE [Part::Cylinder] Cylinder007
  Angle = 360
  AttacherType = Attacher::AttachEngine3D
  Height = 10
  Placement = pos=(0,0,36.15) rot=(0,0,1;0rad)
  Radius = 4
FEATURE [Part::MultiFuse] Fusion026  label="removeToCreteHoleForPlugHousing"
  Placement = pos=(70,19,36) rot=(0,1,0;1.5708rad)
  Shapes = -> [Cylinder006,Cylinder007]
FEATURE [Part::Box] Box001  label="Cube001"
  AttacherType = Attacher::AttachEngine3D
  Height = 28
  Length = 3
  Placement = pos=(110.7,19,22) rot=(0,0,1;0rad)
  Width = 15.7
FEATURE [Part::Cut] Cut003  label="top002"
  Base = -> Cut001
  Tool = -> Fusion007
FEATURE [Part::Revolution] Revolve008  label="plugHousing015"
  Angle = 360
  Axis = (0,1,0)
  Base = (0,0,0)
  FaceMakerClass = Part::FaceMakerBullseye
  Placement = pos=(0,0,36.15) rot=(0,0,1;0rad)
  Solid = false
  Source = -> Face010
  Symmetric = false
FEATURE [Part::MultiFuse] Fusion013  label="plugHousing020"
  Placement = pos=(0,0,0) rot=(0,0,1;1.5708rad)
  Shapes = -> [Revolve008,Revolve012]
FEATURE [Part::Cut] Cut004  label="top003"
  Base = -> Cut003
  Placement = pos=(1,0,0) rot=(0,0,1;0rad)
  Tool = -> Fusion026
FEATURE [Part::Cylinder] Cylinder008
  Angle = 360
  AttacherType = Attacher::AttachEngine3D
  Height = 20
  Placement = pos=(0,0,36.15) rot=(0,0,1;0rad)
  Radius = 10.3
FEATURE [Part::Cylinder] Cylinder009
  Angle = 360
  AttacherType = Attacher::AttachEngine3D
  Height = 10
  Placement = pos=(0,0,36.15) rot=(0,0,1;0rad)
  Radius = 4
FEATURE [Part::MultiFuse] Fusion027  label="removeToCreteHoleForPlugHousing001"
  Placement = pos=(70,19,36) rot=(0,1,0;1.5708rad)
  Shapes = -> [Cylinder008,Cylinder009]
FEATURE [Part::Cut] Cut005  label="plugHousingTab"
  Base = -> Box001
  Tool = -> Fusion027
FEATURE [Part::MultiFuse] Fusion028  label="plugHousing045"
  Shapes = -> [Fusion024,Cut005]
FEATURE [Part::Box] Box002  label="Cube002"
  AttacherType = Attacher::AttachEngine3D
  Height = 28.8
  Length = 3
  Placement = pos=(107.3,28,21.6) rot=(0,0,1;0rad)
  Width = 7
FEATURE [Part::Box] Box003  label="Cube003"
  AttacherType = Attacher::AttachEngine3D
  Height = 3
  Length = 6.4
  Placement = pos=(107.3,28,18.6) rot=(0,0,1;0rad)
  Width = 7
FEATURE [Part::Box] Box004  label="Cube004"
  AttacherType = Attacher::AttachEngine3D
  Height = 3
  Length = 6.4
  Placement = pos=(107.3,28,50.4) rot=(0,0,1;0rad)
  Width = 7
FEATURE [Part::MultiFuse] Fusion029  label="plugHousingBracketHolder"
  Shapes = -> [Box004,Box002,Box003]
FEATURE [Part::Cylinder] Cylinder010
  Angle = 360
  AttacherType = Attacher::AttachEngine3D
  Height = 20
  Placement = pos=(0,0,36.15) rot=(0,0,1;0rad)
  Radius = 14.3
FEATURE [Part::Cylinder] Cylinder011
  Angle = 360
  AttacherType = Attacher::AttachEngine3D
  Height = 10
  Placement = pos=(0,0,36.15) rot=(0,0,1;0rad)
  Radius = 4
FEATURE [Part::MultiFuse] Fusion030  label="removeToCreteHoleForPlugHousing002"
  Placement = pos=(70,19,36) rot=(0,1,0;1.5708rad)
  Shapes = -> [Cylinder010,Cylinder011]
FEATURE [Part::Cut] Cut006  label="plugHousingBracketHolder001"
  Base = -> Fusion029
  Tool = -> Fusion030
FEATURE [Part::Cylinder] Cylinder012
  Angle = 360
  AttacherType = Attacher::AttachEngine3D
  Height = 20
  Placement = pos=(0,0,36.15) rot=(0,0,1;0rad)
  Radius = 7
FEATURE [Part::Cylinder] Cylinder013
  Angle = 360
  AttacherType = Attacher::AttachEngine3D
  Height = 10
  Placement = pos=(0,0,36.15) rot=(0,0,1;0rad)
  Radius = 4
FEATURE [Part::MultiFuse] Fusion032  label="removeToCreteHoleForPlugHousing003"
  Placement = pos=(70,19,36) rot=(0,1,0;1.5708rad)
  Shapes = -> [Cylinder012,Cylinder013]
FEATURE [Part::Cut] Cut007  label="bottom002"
  Base = -> Cut002
  Tool = -> Fusion032
FEATURE [Sketcher::SketchObject] Sketch008
  FullyConstrained = true
  sketch-geometry (54):
    g0: LineSegment StartX=-4.2 StartY=0 StartZ=0 EndX=-6.2 EndY=0 EndZ=0
    g1: LineSegment StartX=-14 StartY=-18 StartZ=0 EndX=-14 EndY=-26.5 EndZ=0
    g2: LineSegment StartX=-4.2 StartY=0 StartZ=0 EndX=-4.2 EndY=-13.4877 EndZ=0
    g3: Circle CenterX=-4.2 CenterY=-13.4877 CenterZ=0 NormalX=0 NormalY=0 NormalZ=1 AngleXU=0 Radius=1
    g4: Circle CenterX=-4.2 CenterY=-26.5 CenterZ=0 NormalX=0 NormalY=0 NormalZ=1 AngleXU=0 Radius=1
    g5: Circle CenterX=-8.2 CenterY=-26.5 CenterZ=0 NormalX=0 NormalY=0 NormalZ=1 AngleXU=0 Radius=1
    g6: BSplineCurve PolesCount=3 KnotsCount=2 Degree=2 IsPeriodic=0
    g7: GeomPoint X=-4.2 Y=-13.4877 Z=0
    g8: GeomPoint X=-8.2 Y=-26.5 Z=0
    g9: LineSegment StartX=-14 StartY=-26.5 StartZ=0 EndX=-8.2 EndY=-26.5 EndZ=0
    g10: LineSegment StartX=-10.15 StartY=-12 StartZ=0 EndX=-10.15 EndY=-14 EndZ=0
    g11: LineSegment StartX=-12.8401 StartY=-16 StartZ=0 EndX=-10.1571 EndY=-16 EndZ=0
    g12: LineSegment StartX=-10.15 StartY=-14 StartZ=0 EndX=-8.70761 EndY=-14 EndZ=0
    g13: LineSegment StartX=-12.8401 StartY=-16 StartZ=0 EndX=-12.8401 EndY=-17.6958 EndZ=0
    g14: LineSegment StartX=-10.15 StartY=-12 StartZ=0 EndX=-7.79258 EndY=-12 EndZ=0
    g15: Circle CenterX=-6.2215 CenterY=-2 CenterZ=0 NormalX=0 NormalY=0 NormalZ=1 AngleXU=0 Radius=1
    g16: Circle CenterX=-6.22762 CenterY=-2.58724 CenterZ=0 NormalX=0 NormalY=0 NormalZ=1 AngleXU=0 Radius=1
    g17: Circle CenterX=-6.32538 CenterY=-4 CenterZ=0 NormalX=0 NormalY=0 NormalZ=1 AngleXU=0 Radius=1
    g18: BSplineCurve PolesCount=3 KnotsCount=2 Degree=2 IsPeriodic=0
    g19: GeomPoint X=-6.2215 Y=-2 Z=0
    g20: GeomPoint X=-6.32538 Y=-4 Z=0
    g21: Circle CenterX=-6.48644 CenterY=-5.99526 CenterZ=0 NormalX=0 NormalY=0 NormalZ=1 AngleXU=0 Radius=1
    g22: Circle CenterX=-6.58486 CenterY=-6.99526 CenterZ=0 NormalX=0 NormalY=0 NormalZ=1 AngleXU=0 Radius=1
    g23: Circle CenterX=-6.77343 CenterY=-8 CenterZ=0 NormalX=0 NormalY=0 NormalZ=1 AngleXU=0 Radius=1
    g24: BSplineCurve PolesCount=3 KnotsCount=2 Degree=2 IsPeriodic=0
    g25: GeomPoint X=-6.48644 Y=-5.99526 Z=0
    g26: GeomPoint X=-6.77343 Y=-8 Z=0
    g27: Circle CenterX=-7.19003 CenterY=-10 CenterZ=0 NormalX=0 NormalY=0 NormalZ=1 AngleXU=0 Radius=1
    g28: Circle CenterX=-7.44407 CenterY=-11.0915 CenterZ=0 NormalX=0 NormalY=0 NormalZ=1 AngleXU=0 Radius=1
    g29: Circle CenterX=-7.79258 CenterY=-12 CenterZ=0 NormalX=0 NormalY=0 NormalZ=1 AngleXU=0 Radius=1
    g30: BSplineCurve PolesCount=3 KnotsCount=2 Degree=2 IsPeriodic=0
    g31: GeomPoint X=-7.19003 Y=-10 Z=0
    g32: GeomPoint X=-7.79258 Y=-12 Z=0
    g33: Circle CenterX=-8.70761 CenterY=-14 CenterZ=0 NormalX=0 NormalY=0 NormalZ=1 AngleXU=0 Radius=1
    g34: Circle CenterX=-9.33087 CenterY=-15.1837 CenterZ=0 NormalX=0 NormalY=0 NormalZ=1 AngleXU=0 Radius=1
    g35: Circle CenterX=-10.1571 CenterY=-16 CenterZ=0 NormalX=0 NormalY=0 NormalZ=1 AngleXU=0 Radius=1
    g36: BSplineCurve PolesCount=3 KnotsCount=2 Degree=2 IsPeriodic=0
    g37: GeomPoint X=-8.70761 Y=-14 Z=0
    g38: GeomPoint X=-10.1571 Y=-16 Z=0
    g39: Circle CenterX=-12.8401 CenterY=-17.6958 CenterZ=0 NormalX=0 NormalY=0 NormalZ=1 AngleXU=0 Radius=1
    g40: Circle CenterX=-13.3521 CenterY=-17.9027 CenterZ=0 NormalX=0 NormalY=0 NormalZ=1 AngleXU=0 Radius=1
    g41: Circle CenterX=-14 CenterY=-18 CenterZ=0 NormalX=0 NormalY=0 NormalZ=1 AngleXU=0 Radius=1
    g42: BSplineCurve PolesCount=3 KnotsCount=2 Degree=2 IsPeriodic=0
    g43: GeomPoint X=-12.8401 Y=-17.6958 Z=0
    g44: GeomPoint X=-14 Y=-18 Z=0
    g45: LineSegment StartX=-6.2 StartY=0 StartZ=0 EndX=-7.2 EndY=0 EndZ=0
    g46: LineSegment StartX=-7.2 StartY=0 StartZ=0 EndX=-7.2 EndY=-2 EndZ=0
    g47: LineSegment StartX=-7.2 StartY=-2 StartZ=0 EndX=-6.2215 EndY=-2 EndZ=0
    g48: LineSegment StartX=-6.32538 StartY=-4 StartZ=0 EndX=-7.65538 EndY=-4 EndZ=0
    g49: LineSegment StartX=-7.65538 StartY=-4 StartZ=0 EndX=-7.65538 EndY=-5.99526 EndZ=0
    g50: LineSegment StartX=-7.65538 StartY=-5.99526 StartZ=0 EndX=-6.48644 EndY=-5.99526 EndZ=0
    g51: LineSegment StartX=-6.77343 StartY=-8 StartZ=0 EndX=-8.43343 EndY=-8 EndZ=0
    g52: LineSegment StartX=-8.43343 StartY=-8 StartZ=0 EndX=-8.43343 EndY=-10 EndZ=0
    g53: LineSegment StartX=-8.43343 StartY=-10 StartZ=0 EndX=-7.19003 EndY=-10 EndZ=0
  constraints (112):
    c: Horizontal(g0)
    c: Distance(g0) = 2
    c: Block(g0)
    c: Vertical(g1)
    c: Coincident(g2,g0)
    c: Vertical(g2)
    c: Block(g2)
    c: Coincident(g6,g2)
    c: Weight(g3) = 1
    c: Equal(g3,g4)
    c: Equal(g3,g5)
    c: InternalAlignment(g3,g6)
    c: InternalAlignment(g4,g6)
    c: InternalAlignment(g5,g6)
    c: InternalAlignment(g7,g6)
    c: InternalAlignment(g8,g6)
    c: Block(g6)
    c: Coincident(g9,g1)
    c: Coincident(g9,g6)
    c: Horizontal(g9)
    c: Vertical(g10)
    c: Block(g10)
    c: Horizontal(g11)
    c: Block(g11)
    c: Coincident(g12,g10)
    c: Horizontal(g12)
    c: Block(g12)
    c: Coincident(g13,g11)
    c: Vertical(g13)
    c: Block(g13)
    c: Coincident(g14,g10)
    c: Horizontal(g14)
    c: Block(g14)
    c: Block(g9)
    c: Block(g1)
    c: Weight(g15) = 1
    c: Equal(g15,g16)
    c: Equal(g15,g17)
    c: InternalAlignment(g15,g18)
    c: InternalAlignment(g16,g18)
    c: InternalAlignment(g17,g18)
    c: InternalAlignment(g19,g18)
    c: InternalAlignment(g20,g18)
    c: Weight(g21) = 1
    c: Equal(g21,g22)
    c: Equal(g21,g23)
    c: InternalAlignment(g21,g24)
    c: InternalAlignment(g22,g24)
    c: InternalAlignment(g23,g24)
    c: InternalAlignment(g25,g24)
    c: InternalAlignment(g26,g24)
    c: Weight(g27) = 1
    c: Equal(g27,g28)
    c: Equal(g27,g29)
    c: Coincident(g30,g14)
    c: InternalAlignment(g27,g30)
    c: InternalAlignment(g28,g30)
    c: InternalAlignment(g29,g30)
    c: InternalAlignment(g31,g30)
    c: InternalAlignment(g32,g30)
    c: Coincident(g36,g12)
    c: Weight(g33) = 1
    c: Equal(g33,g34)
    c: Equal(g33,g35)
    c: Coincident(g36,g11)
    c: InternalAlignment(g33,g36)
    c: InternalAlignment(g34,g36)
    c: InternalAlignment(g35,g36)
    c: InternalAlignment(g37,g36)
    c: InternalAlignment(g38,g36)
    c: Coincident(g42,g13)
    c: Weight(g39) = 1
    c: Equal(g39,g40)
    c: Equal(g39,g41)
    c: Coincident(g42,g1)
    c: InternalAlignment(g39,g42)
    c: InternalAlignment(g40,g42)
    c: InternalAlignment(g41,g42)
    c: InternalAlignment(g43,g42)
    c: InternalAlignment(g44,g42)
    c: Block(g18)
    c: Block(g24)
    c: Block(g30)
    c: Block(g36)
    c: Block(g42)
    c: Horizontal(g45)
    c: Coincident(g45,g0)
    c: Vertical(g46)
    c: Coincident(g46,g45)
    c: Coincident(g47,g46)
    c: Coincident(g47,g18)
    c: Horizontal(g47)
    c: Block(g46)
    c: Coincident(g48,g18)
    c: Horizontal(g48)
    c: Distance(g48) = 1.33
    c: Vertical(g49)
    c: Coincident(g49,g48)
    c: Coincident(g50,g49)
    c: Coincident(g50,g24)
    c: Horizontal(g50)
    c: Tangent(g50,g22)
    c: Horizontal(g51)
    c: Coincident(g51,g24)
    c: Block(g51)
    c: Vertical(g52)
    c: Block(g52)
    c: Coincident(g52,g51)
    c: Coincident(g53,g52)
    c: Coincident(g53,g30)
    c: Horizontal(g53)
    c: Distance(g1) = 8.5
FEATURE [Part::Feature] Face024
  shape: bbox 9.8 x 26.5 x 2e-07 mm, 1 faces, 0 solids (baked)
FEATURE [Part::Revolution] Revolve024
  Angle = 360
  Axis = (0,1,0)
  Base = (0,0,0)
  FaceMakerClass = Part::FaceMakerBullseye
  Placement = pos=(0,0,0) rot=(0,0,1;1.5708rad)
  Solid = false
  Source = -> Face024
  Symmetric = false
FEATURE [Part::Feature] Face025
  shape: bbox 9.8 x 26.5 x 2e-07 mm, 1 faces, 0 solids (baked)
FEATURE [Part::Revolution] Revolve025
  Angle = 360
  Axis = (0,1,0)
  Base = (0,0,0)
  FaceMakerClass = Part::FaceMakerBullseye
  Placement = pos=(0,0,0) rot=(0,0,1;1.5708rad)
  Solid = false
  Source = -> Face025
  Symmetric = false
FEATURE [Part::MultiFuse] Fusion033
  Placement = pos=(-18,19,36) rot=(0,0,1;0rad)
  Shapes = -> [Revolve025,Revolve024]
FEATURE [Part::Cylinder] Cylinder014
  Angle = 360
  AttacherType = Attacher::AttachEngine3D
  Height = 20
  Placement = pos=(0,0,36.15) rot=(0,0,1;0rad)
  Radius = 14.3
FEATURE [Part::Cylinder] Cylinder015
  Angle = 360
  AttacherType = Attacher::AttachEngine3D
  Height = 10
  Placement = pos=(0,0,36.15) rot=(0,0,1;0rad)
  Radius = 4
FEATURE [Part::MultiFuse] Fusion034  label="removeToCreteHoleForPlugHousing004"
  Placement = pos=(-42,19,36) rot=(0,1,0;1.5708rad)
  Shapes = -> [Cylinder014,Cylinder015]
FEATURE [Part::Cut] Cut008  label="top004"
  Base = -> Cut004
  Placement = pos=(-1,0,0) rot=(0,0,1;0rad)
  Tool = -> Fusion034
FEATURE [Part::Box] Box005  label="Cube005"
  AttacherType = Attacher::AttachEngine3D
  Height = 28
  Length = 3
  Placement = pos=(110.7,19,22) rot=(0,0,1;0rad)
  Width = 15.7
FEATURE [Part::Cylinder] Cylinder016
  Angle = 360
  AttacherType = Attacher::AttachEngine3D
  Height = 10
  Placement = pos=(0,0,36.15) rot=(0,0,1;0rad)
  Radius = 4
FEATURE [Part::Cylinder] Cylinder017
  Angle = 360
  AttacherType = Attacher::AttachEngine3D
  Height = 20
  Placement = pos=(0,0,36.15) rot=(0,0,1;0rad)
  Radius = 10.3
FEATURE [Part::MultiFuse] Fusion035  label="removeToCreteHoleForPlugHousing005"
  Placement = pos=(70,19,36) rot=(0,1,0;1.5708rad)
  Shapes = -> [Cylinder017,Cylinder016]
FEATURE [Part::Cut] Cut009  label="plugHousingTab001"
  Base = -> Box005
  Placement = pos=(-107.4,-14,0) rot=(0,0,1;0rad)
  Tool = -> Fusion035
FEATURE [Part::Box] Box006  label="Cube006"
  AttacherType = Attacher::AttachEngine3D
  Height = 28
  Length = 3
  Placement = pos=(110.7,19,22) rot=(0,0,1;0rad)
  Width = 15.7
FEATURE [Part::Cylinder] Cylinder018
  Angle = 360
  AttacherType = Attacher::AttachEngine3D
  Height = 10
  Placement = pos=(0,0,36.15) rot=(0,0,1;0rad)
  Radius = 4
FEATURE [Part::Cylinder] Cylinder019
  Angle = 360
  AttacherType = Attacher::AttachEngine3D
  Height = 20
  Placement = pos=(0,0,36.15) rot=(0,0,1;0rad)
  Radius = 10.3
FEATURE [Part::MultiFuse] Fusion036  label="removeToCreteHoleForPlugHousing006"
  Placement = pos=(70,19,36) rot=(0,1,0;1.5708rad)
  Shapes = -> [Cylinder019,Cylinder018]
FEATURE [Part::Cut] Cut010  label="plugHousingTab002"
  Base = -> Box006
  Placement = pos=(-107.4,-14,0) rot=(0,0,1;0rad)
  Tool = -> Fusion036
FEATURE [Part::MultiFuse] Fusion037
  Placement = pos=(9.6,23,0) rot=(0,0,1;3.14159rad)
  Shapes = -> [Cut009,Cut010]
FEATURE [Part::Box] Box  label="Cube"
  AttacherType = Attacher::AttachEngine3D
  Height = 10
  Length = 3
  Placement = pos=(3.3,4,12) rot=(0,0,1;0rad)
  Width = 10
FEATURE [Part::Fillet] Fillet004
  Base = -> Fusion028
  Edges = 1 edges r=2: [Edge25]
FEATURE [Part::Fillet] Fillet005  label="plugHousing046"
  Base = -> Fillet004
  Edges = 1 edges r=2: [Edge8]
FEATURE [Part::Fillet] Fillet006
  Base = -> Box
  Edges = 1 edges r=2: [Edge11]
FEATURE [Part::Box] Box007  label="Cube007"
  AttacherType = Attacher::AttachEngine3D
  Height = 10
  Length = 3
  Placement = pos=(3.3,4,50) rot=(0,0,1;0rad)
  Width = 10
FEATURE [Part::Fillet] Fillet007
  Base = -> Box007
  Edges = 1 edges r=2: [Edge12]
FEATURE [Part::Box] Box008  label="Cube008"
  AttacherType = Attacher::AttachEngine3D
  Height = 28
  Length = 4
  Placement = pos=(5,0,22) rot=(0,0,1;0rad)
  Width = 10
FEATURE [Part::Fillet] Fillet008
  Base = -> Box008
  Edges = 1 edges r=1: [Edge7]
FEATURE [Part::Fillet] Fillet009
  Base = -> Fillet008
  Edges = 1 edges r=2: [Edge5]
FEATURE [Part::Fillet] Fillet010
  Base = -> Fillet009
  Edges = 1 edges r=2: [Edge2]
FEATURE [Sketcher::SketchObject] Sketch009  label="topSketch003"
  FullyConstrained = true
  sketch-geometry (4):
    g0: LineSegment StartX=16.8446 StartY=31.512 StartZ=0 EndX=16.3251 EndY=34.4666 EndZ=0
    g1: ArcOfCircle CenterX=19 CenterY=19.2524 CenterZ=0 NormalX=0 NormalY=0 NormalZ=1 AngleXU=0 Radius=15.4476 StartAngle=1.74483 EndAngle=2.72717
    g2: ArcOfCircle CenterX=19 CenterY=19.2524 CenterZ=0 NormalX=0 NormalY=0 NormalZ=1 AngleXU=0 Radius=12.4476 StartAngle=1.74483 EndAngle=2.73189
    g3: LineSegment StartX=4.86004 StartY=25.4725 StartZ=0 EndX=7.58253 EndY=24.2107 EndZ=0
  constraints (7):
    c: Block(g0)
    c: Coincident(g1,g0)
    c: Coincident(g2,g0)
    c: Coincident(g3,g1)
    c: Coincident(g3,g2)
    c: Block(g1)
    c: Block(g2)
FEATURE [Part::Extrusion] Extrude008
  Base = -> Sketch009
  Dir = (0,0,1)
  DirMode = 2
  FaceMakerClass = Part::FaceMakerBullseye
  LengthFwd = 10
  LengthRev = 0
  Placement = pos=(0,0,31) rot=(0,0,1;0rad)
  Solid = true
  Symmetric = false
FEATURE [Part::Cylinder] Cylinder020
  Angle = 360
  AttacherType = Attacher::AttachEngine3D
  Height = 20
  Placement = pos=(0,0,36.15) rot=(0,0,1;0rad)
  Radius = 8.2
FEATURE [Part::Cylinder] Cylinder021
  Angle = 360
  AttacherType = Attacher::AttachEngine3D
  Height = 10
  Placement = pos=(0,0,36.15) rot=(0,0,1;0rad)
  Radius = 4
FEATURE [Part::MultiFuse] Fusion038  label="removeToCreteHoleForPlugHousing007"
  Placement = pos=(-42,19,36) rot=(0,1,0;1.5708rad)
  Shapes = -> [Cylinder020,Cylinder021]
FEATURE [Part::Cut] Cut011
  Base = -> Extrude008
  Tool = -> Fusion038
FEATURE [Part::Fillet] Fillet011
  Base = -> Cut011
  Edges = 1 edges r=2: [Edge1]
FEATURE [Part::Fillet] Fillet012
  Base = -> Fillet011
  Edges = 1 edges r=2.5: [Edge1]
FEATURE [Part::Fillet] Fillet013
  Base = -> Fillet012
  Edges = 1 edges r=2.5: [Edge2]
FEATURE [Part::Box] Box010  label="Cube010"
  AttacherType = Attacher::AttachEngine3D
  Height = 16
  Length = 8
  Placement = pos=(12.7,31.52,28) rot=(0,0,1;0rad)
  Width = 4
FEATURE [Sketcher::SketchObject] Sketch010  label="topSketch004"
  FullyConstrained = true
  sketch-geometry (4):
    g0: LineSegment StartX=16.8446 StartY=31.512 StartZ=0 EndX=16.3251 EndY=34.4666 EndZ=0
    g1: ArcOfCircle CenterX=19 CenterY=19.2524 CenterZ=0 NormalX=0 NormalY=0 NormalZ=1 AngleXU=0 Radius=15.4476 StartAngle=1.74483 EndAngle=2.72717
    g2: ArcOfCircle CenterX=19 CenterY=19.2524 CenterZ=0 NormalX=0 NormalY=0 NormalZ=1 AngleXU=0 Radius=12.4476 StartAngle=1.74483 EndAngle=2.73189
    g3: LineSegment StartX=4.86004 StartY=25.4725 StartZ=0 EndX=7.58253 EndY=24.2107 EndZ=0
  constraints (7):
    c: Block(g0)
    c: Coincident(g1,g0)
    c: Coincident(g2,g0)
    c: Coincident(g3,g1)
    c: Coincident(g3,g2)
    c: Block(g1)
    c: Block(g2)
FEATURE [Part::Cylinder] Cylinder022
  Angle = 360
  AttacherType = Attacher::AttachEngine3D
  Height = 10
  Placement = pos=(0,0,36.15) rot=(0,0,1;0rad)
  Radius = 4
FEATURE [Sketcher::SketchObject] Sketch011  label="topSketch005"
  FullyConstrained = true
  sketch-geometry (4):
    g0: LineSegment StartX=16.8446 StartY=31.512 StartZ=0 EndX=16.3251 EndY=34.4666 EndZ=0
    g1: ArcOfCircle CenterX=19 CenterY=19.2524 CenterZ=0 NormalX=0 NormalY=0 NormalZ=1 AngleXU=0 Radius=15.4476 StartAngle=1.74483 EndAngle=2.72717
    g2: ArcOfCircle CenterX=19 CenterY=19.2524 CenterZ=0 NormalX=0 NormalY=0 NormalZ=1 AngleXU=0 Radius=12.4476 StartAngle=1.74483 EndAngle=2.73189
    g3: LineSegment StartX=4.86004 StartY=25.4725 StartZ=0 EndX=7.58253 EndY=24.2107 EndZ=0
  constraints (7):
    c: Block(g0)
    c: Coincident(g1,g0)
    c: Coincident(g2,g0)
    c: Coincident(g3,g1)
    c: Coincident(g3,g2)
    c: Block(g1)
    c: Block(g2)
FEATURE [Part::Extrusion] Extrude010
  Base = -> Sketch011
  Dir = (0,0,1)
  DirMode = 2
  FaceMakerClass = Part::FaceMakerBullseye
  LengthFwd = 10.6
  LengthRev = 0
  Placement = pos=(0,0,31) rot=(0,0,1;0rad)
  Solid = true
  Symmetric = false
FEATURE [Part::Cylinder] Cylinder023
  Angle = 360
  AttacherType = Attacher::AttachEngine3D
  Height = 20
  Placement = pos=(0,0,36.15) rot=(0,0,1;0rad)
  Radius = 8.2
FEATURE [Part::MultiFuse] Fusion039  label="removeToCreteHoleForPlugHousing008"
  Placement = pos=(-42,19,36) rot=(0,1,0;1.5708rad)
  Shapes = -> [Cylinder023,Cylinder022]
FEATURE [Part::Cut] Cut012
  Base = -> Extrude010
  Placement = pos=(0,0,-0.3) rot=(0,0,1;0rad)
  Tool = -> Fusion039
FEATURE [Part::Cut] Cut013
  Base = -> Box010
  Tool = -> Cut012
FEATURE [Part::Fillet] Fillet014
  Base = -> Cut013
  Edges = 1 edges r=0.7: [Edge13]
FEATURE [Part::Fillet] Fillet015
  Base = -> Fillet014
  Edges = 1 edges r=0.7: [Edge13]
FEATURE [Part::Fillet] Fillet016
  Base = -> Fillet015
  Edges = 1 edges r=0.7: [Edge16]
FEATURE [Part::Fillet] Fillet017
  Base = -> Fillet016
  Edges = 1 edges r=0.7: [Edge11]
FEATURE [Part::Fillet] Fillet018
  Base = -> Fillet017
  Edges = 1 edges r=0.7: [Edge10]
FEATURE [Part::Fillet] Fillet019
  Base = -> Fillet018
  Edges = 1 edges r=1.2: [Edge5]
FEATURE [Part::Fillet] Fillet020
  Base = -> Fillet019
  Edges = 1 edges r=1.2: [Edge12]
FEATURE [Part::Fillet] Fillet021
  Base = -> Fillet020
  Edges = 1 edges r=2: [Edge1]
  Placement = pos=(0.3,0,0) rot=(0,0,1;0rad)
FEATURE [Part::MultiFuse] Fusion040  label="top005"
  Shapes = -> [Cut008,Fillet021]
FEATURE [Part::MultiFuse] Fusion041  label="wireHolder"
  Shapes = -> [Fusion033,Fillet013]
FEATURE [Part::MultiFuse] Fusion042
  Shapes = -> [Fillet007,Fusion041]
FEATURE [Part::MultiFuse] Fusion043  label="wireHolder001"
  Shapes = -> [Fusion042,Fillet010]
FEATURE [Part::MultiFuse] Fusion044  label="wireHolder002"
  Shapes = -> [Fillet006,Fusion037,Fusion043]
FEATURE [Part::Feature] Face026
  shape: bbox 11 x 6 x 2e-07 mm, 1 faces, 0 solids (baked)
FEATURE [Part::Revolution] Revolve026
  Angle = 360
  Axis = (0,1,0)
  Base = (0,0,0)
  FaceMakerClass = Part::FaceMakerBullseye
  Placement = pos=(30.3,-1,19.7) rot=(0,0,1;0rad)
  Solid = false
  Source = -> Face026
  Symmetric = false
FEATURE [Sketcher::SketchObject] Sketch013  label="topSketch006"
  FullyConstrained = true
  sketch-geometry (13):
    g0: LineSegment StartX=117 StartY=19 StartZ=0 EndX=117 EndY=38 EndZ=0
    g1: ArcOfCircle CenterX=98 CenterY=19 CenterZ=0 NormalX=0 NormalY=0 NormalZ=1 AngleXU=0 Radius=19 StartAngle=5.7297 EndAngle=6.28319
    g2: LineSegment StartX=0 StartY=3 StartZ=0 EndX=0 EndY=19 EndZ=0
    g3: LineSegment StartX=19 StartY=38 StartZ=0 EndX=117 EndY=38 EndZ=0
    g4: ArcOfCircle CenterX=19 CenterY=19 CenterZ=0 NormalX=0 NormalY=0 NormalZ=1 AngleXU=0 Radius=19 StartAngle=1.5708 EndAngle=3.14159
    g5: ArcOfCircle CenterX=19 CenterY=19 CenterZ=0 NormalX=0 NormalY=0 NormalZ=1 AngleXU=0 Radius=16 StartAngle=1.5708 EndAngle=3.14159
    g6: ArcOfCircle CenterX=98 CenterY=19 CenterZ=0 NormalX=0 NormalY=0 NormalZ=1 AngleXU=0 Radius=16 StartAngle=5.60905 EndAngle=6.28319
    g7: LineSegment StartX=114 StartY=19 StartZ=0 EndX=114 EndY=35 EndZ=0
    g8: LineSegment StartX=110.5 StartY=9.01251 StartZ=0 EndX=114.163 EndY=9.01251 EndZ=0
    g9: LineSegment StartX=114 StartY=35 StartZ=0 EndX=19 EndY=35 EndZ=0
    g10: LineSegment StartX=0 StartY=3 StartZ=0 EndX=0 EndY=0 EndZ=0
    g11: LineSegment StartX=3 StartY=0 StartZ=0 EndX=0 EndY=0 EndZ=0
    g12: LineSegment StartX=3 StartY=19 StartZ=0 EndX=3 EndY=0 EndZ=0
  constraints (33):
    c: Vertical(g0)
    c: Distance(g0) = 19
    c: Block(g0)
    c: Coincident(g1,g0)
    c: Block(g1)
    c: Vertical(g2)
    c: Block(g2)
    c: Coincident(g3,g0)
    c: Horizontal(g3)
    c: Distance(g3) = 98
    c: Coincident(g4,g3)
    c: Coincident(g4,g2)
    c: Block(g4)
    c: Coincident(g5,g4)
    c: Coincident(g6,g1)
    c: Block(g6)
    c: Block(g5)
    c: Coincident(g7,g6)
    c: Vertical(g7)
    c: Coincident(g8,g6)
    c: Coincident(g8,g1)
    c: Coincident(g9,g7)
    c: Coincident(g9,g5)
    c: Horizontal(g9)
    c: Tangent(g9,g5)
    c: Coincident(g10,g2)
    c: Distance(g10) = 3
    c: Vertical(g10)
    c: Coincident(g11,g10)
    c: Horizontal(g11)
    c: Coincident(g12,g5)
    c: Coincident(g12,g11)
    c: Vertical(g12)
FEATURE [Part::Extrusion] Extrude011  label="top006"
  Base = -> Sketch013
  Dir = (0,0,1)
  DirMode = 2
  FaceMakerClass = Part::FaceMakerBullseye
  LengthFwd = 72
  LengthRev = 0
  Solid = true
  Symmetric = false
FEATURE [Sketcher::SketchObject] Sketch014
  FullyConstrained = true
  MapMode = 3
  Placement = pos=(0,0,0) rot=(1,0,0;1.5708rad)
  Support = -> [Extrude011]
  sketch-geometry (8):
    g0: Circle CenterX=80.351 CenterY=-67.6202 CenterZ=0 NormalX=0 NormalY=0 NormalZ=1 AngleXU=0 Radius=2
    g1: Circle CenterX=80.351 CenterY=-67.6202 CenterZ=0 NormalX=0 NormalY=0 NormalZ=1 AngleXU=0 Radius=3
    g2: Circle CenterX=80.351 CenterY=-4.92017 CenterZ=0 NormalX=0 NormalY=0 NormalZ=1 AngleXU=0 Radius=2
    g3: Circle CenterX=80.351 CenterY=-4.92017 CenterZ=0 NormalX=0 NormalY=0 NormalZ=1 AngleXU=0 Radius=3
    g4: Circle CenterX=23.851 CenterY=-4.92017 CenterZ=0 NormalX=0 NormalY=0 NormalZ=1 AngleXU=0 Radius=2
    g5: Circle CenterX=23.851 CenterY=-4.92017 CenterZ=0 NormalX=0 NormalY=0 NormalZ=1 AngleXU=0 Radius=3
    g6: Circle CenterX=23.851 CenterY=-67.6202 CenterZ=0 NormalX=0 NormalY=0 NormalZ=1 AngleXU=0 Radius=2
    g7: Circle CenterX=23.851 CenterY=-67.6202 CenterZ=0 NormalX=0 NormalY=0 NormalZ=1 AngleXU=0 Radius=3
  constraints (8):
    c: Block(g3)
    c: Block(g2)
    c: Block(g1)
    c: Block(g0)
    c: Block(g6)
    c: Block(g7)
    c: Block(g4)
    c: Block(g5)
FEATURE [Part::Feature] Face027
  shape: bbox 11 x 6 x 2e-07 mm, 1 faces, 0 solids (baked)
FEATURE [Part::Revolution] Revolve027
  Angle = 360
  Axis = (0,1,0)
  Base = (0,0,0)
  FaceMakerClass = Part::FaceMakerBullseye
  Placement = pos=(30.3,-1,51.7) rot=(0,0,1;0rad)
  Solid = false
  Source = -> Face027
  Symmetric = false
FEATURE [Part::Feature] Face028
  shape: bbox 11 x 6 x 2e-07 mm, 1 faces, 0 solids (baked)
FEATURE [Part::Revolution] Revolve028
  Angle = 360
  Axis = (0,1,0)
  Base = (0,0,0)
  FaceMakerClass = Part::FaceMakerBullseye
  Placement = pos=(62.3,-1,19.7) rot=(0,0,1;0rad)
  Solid = false
  Source = -> Face028
  Symmetric = false
FEATURE [Part::Feature] Face029
  shape: bbox 11 x 6 x 2e-07 mm, 1 faces, 0 solids (baked)
FEATURE [Part::Revolution] Revolve029
  Angle = 360
  Axis = (0,1,0)
  Base = (0,0,0)
  FaceMakerClass = Part::FaceMakerBullseye
  Placement = pos=(62.3,-1,51.7) rot=(0,0,1;0rad)
  Solid = false
  Source = -> Face029
  Symmetric = false
FEATURE [Part::Feature] Wire
  shape: bbox 11 x 5.2 x 2e-07 mm, 0 faces, 0 solids (baked)
FEATURE [Part::Revolution] Revolve030
  Angle = 360
  Axis = (0,1,0)
  Base = (0,0,0)
  FaceMakerClass = Part::FaceMakerBullseye
  Placement = pos=(30.3,38,19.7) rot=(0,0,1;0rad)
  Solid = true
  Source = -> Wire
  Symmetric = false
FEATURE [Part::Feature] Wire001
  shape: bbox 11 x 5.2 x 2e-07 mm, 0 faces, 0 solids (baked)
FEATURE [Part::Revolution] Revolve031
  Angle = 360
  Axis = (0,1,0)
  Base = (0,0,0)
  FaceMakerClass = Part::FaceMakerBullseye
  Placement = pos=(30.3,38,51.7) rot=(0,0,1;0rad)
  Solid = true
  Source = -> Wire001
  Symmetric = false
FEATURE [Part::Feature] Wire002
  shape: bbox 11 x 5.2 x 2e-07 mm, 0 faces, 0 solids (baked)
FEATURE [Part::Revolution] Revolve032
  Angle = 360
  Axis = (0,1,0)
  Base = (0,0,0)
  FaceMakerClass = Part::FaceMakerBullseye
  Placement = pos=(62.3,38,51.7) rot=(0,0,1;0rad)
  Solid = true
  Source = -> Wire002
  Symmetric = false
FEATURE [Part::Feature] Wire003
  shape: bbox 11 x 5.2 x 2e-07 mm, 0 faces, 0 solids (baked)
FEATURE [Part::Revolution] Revolve033
  Angle = 360
  Axis = (0,1,0)
  Base = (0,0,0)
  FaceMakerClass = Part::FaceMakerBullseye
  Placement = pos=(62.3,38,19.7) rot=(0,0,1;0rad)
  Solid = true
  Source = -> Wire003
  Symmetric = false
FEATURE [Part::MultiFuse] Fusion045  label="altRandScrewHousing"
  Shapes = -> [Revolve029,Revolve027,Revolve028,Revolve026]
FEATURE [Part::MultiFuse] Fusion046  label="fanScrewHousing"
  Shapes = -> [Revolve033,Revolve032,Revolve031,Revolve030]
FEATURE [Sketcher::SketchObject] Sketch015
  FullyConstrained = true
  sketch-geometry (17):
    g0: Circle CenterX=-3.5 CenterY=23.5 CenterZ=0 NormalX=0 NormalY=0 NormalZ=1 AngleXU=0 Radius=1
    g1: Circle CenterX=-1 CenterY=15.25 CenterZ=0 NormalX=0 NormalY=0 NormalZ=1 AngleXU=0 Radius=1
    g2: Circle CenterX=-3.5 CenterY=7 CenterZ=0 NormalX=0 NormalY=0 NormalZ=1 AngleXU=0 Radius=1
    g3: BSplineCurve PolesCount=3 KnotsCount=2 Degree=2 IsPeriodic=0
    g4: GeomPoint X=-3.5 Y=23.5 Z=0
    g5: GeomPoint X=-3.5 Y=7 Z=0
    g6: Circle CenterX=-4.8 CenterY=30.5 CenterZ=0 NormalX=0 NormalY=0 NormalZ=1 AngleXU=0 Radius=1
    g7: Circle CenterX=-3.5 CenterY=30.5 CenterZ=0 NormalX=0 NormalY=0 NormalZ=1 AngleXU=0 Radius=1
    g8: Circle CenterX=-3.5 CenterY=29.2 CenterZ=0 NormalX=0 NormalY=0 NormalZ=1 AngleXU=0 Radius=1
    g9: BSplineCurve PolesCount=3 KnotsCount=2 Degree=2 IsPeriodic=0
    g10: GeomPoint X=-4.8 Y=30.5 Z=0
    g11: GeomPoint X=-3.5 Y=29.2 Z=0
    g12: LineSegment StartX=-3.5 StartY=29.2 StartZ=0 EndX=-3.5 EndY=23.5 EndZ=0
    g13: LineSegment StartX=-4.8 StartY=30.5 StartZ=0 EndX=0 EndY=30.5 EndZ=0
    g14: LineSegment StartX=-3.5 StartY=0.3 StartZ=0 EndX=0 EndY=0.3 EndZ=0
    g15: LineSegment StartX=-3.5 StartY=0.3 StartZ=0 EndX=-3.5 EndY=7 EndZ=0
    g16: LineSegment StartX=0 StartY=0.3 StartZ=0 EndX=0 EndY=30.5 EndZ=0
  constraints (34):
    c: Weight(g0) = 1
    c: Equal(g0,g1)
    c: Equal(g0,g2)
    c: InternalAlignment(g0,g3)
    c: InternalAlignment(g1,g3)
    c: InternalAlignment(g2,g3)
    c: InternalAlignment(g4,g3)
    c: InternalAlignment(g5,g3)
    c: Block(g3)
    c: Weight(g6) = 1
    c: Equal(g6,g7)
    c: Equal(g6,g8)
    c: InternalAlignment(g6,g9)
    c: InternalAlignment(g7,g9)
    c: InternalAlignment(g8,g9)
    c: InternalAlignment(g10,g9)
    c: InternalAlignment(g11,g9)
    c: Block(g9)
    c: Coincident(g12,g9)
    c: Coincident(g12,g3)
    c: Vertical(g12)
    c: Coincident(g13,g9)
    c: Horizontal(g13)
    c: Distance(g13) = 4.8
    c: Horizontal(g14)
    c: Block(g14)
    c: Coincident(g15,g14)
    c: Coincident(g15,g3)
    c: Vertical(g15)
    c: Coincident(g16,g14)
    c: Coincident(g16,g13)
    c: Vertical(g16)
    c: Tangent(g16,g1)
    c: Distance(g14) = 3.5
FEATURE [Sketcher::SketchObject] Sketch016
  FullyConstrained = true
  sketch-geometry (16):
    g0: Circle CenterX=-3.5 CenterY=23.5 CenterZ=0 NormalX=0 NormalY=0 NormalZ=1 AngleXU=0 Radius=1
    g1: Circle CenterX=-1 CenterY=15.25 CenterZ=0 NormalX=0 NormalY=0 NormalZ=1 AngleXU=0 Radius=1
    g2: Circle CenterX=-3.5 CenterY=7 CenterZ=0 NormalX=0 NormalY=0 NormalZ=1 AngleXU=0 Radius=1
    g3: BSplineCurve PolesCount=3 KnotsCount=2 Degree=2 IsPeriodic=0
    g4: GeomPoint X=-3.5 Y=23.5 Z=0
    g5: GeomPoint X=-3.5 Y=7 Z=0
    g6: LineSegment StartX=-3.5 StartY=28.2 StartZ=0 EndX=-3.5 EndY=23.5 EndZ=0
    g7: LineSegment StartX=0 StartY=29.5 StartZ=0 EndX=0 EndY=30 EndZ=0
    g8: LineSegment StartX=-3.5 StartY=28.2 StartZ=0 EndX=-3.5 EndY=30 EndZ=0
    g9: LineSegment StartX=0 StartY=30 StartZ=0 EndX=0 EndY=30.5 EndZ=0
    g10: LineSegment StartX=0 StartY=30.5 StartZ=0 EndX=-3.5 EndY=30.5 EndZ=0
    g11: LineSegment StartX=-3.5 StartY=30.5 StartZ=0 EndX=-3.5 EndY=30 EndZ=0
    g12: LineSegment StartX=0 StartY=29.5 StartZ=0 EndX=0 EndY=5 EndZ=0
    g13: LineSegment StartX=-3.5 StartY=0.3 StartZ=0 EndX=-3.5 EndY=7 EndZ=0
    g14: LineSegment StartX=-3.5 StartY=0.3 StartZ=0 EndX=0 EndY=0.3 EndZ=0
    g15: LineSegment StartX=0 StartY=5 StartZ=0 EndX=0 EndY=0.3 EndZ=0
  constraints (39):
    c: Weight(g0) = 1
    c: Equal(g0,g1)
    c: Equal(g0,g2)
    c: InternalAlignment(g0,g3)
    c: InternalAlignment(g1,g3)
    c: InternalAlignment(g2,g3)
    c: InternalAlignment(g4,g3)
    c: InternalAlignment(g5,g3)
    c: Block(g3)
    c: Coincident(g6,g3)
    c: Vertical(g6)
    c: Vertical(g7)
    c: Distance(g7) = 0.5
    c: Coincident(g8,g6)
    c: Vertical(g8)
    c: Block(g6)
    c: Block(g7)
    c: Vertical(g9)
    c: Equal(g7,g9) = 0.5
    c: Block(g9)
    c: Coincident(g9,g7)
    c: Horizontal(g10)
    c: Coincident(g10,g9)
    c: Coincident(g11,g10)
    c: Coincident(g11,g8)
    c: Vertical(g11)
    c: Block(g11)
    c: Coincident(g12,g7)
    c: Vertical(g12)
    c: Coincident(g13,g3)
    c: Vertical(g13)
    c: Distance(g13) = 6.7
    c: Coincident(g14,g13)
    c: Horizontal(g14)
    c: Block(g14)
    c: Coincident(g15,g12)
    c: Coincident(g15,g14)
    c: Vertical(g15)
    c: Block(g15)
FEATURE [Sketcher::SketchObject] Sketch017
  FullyConstrained = true
  sketch-geometry (11):
    g0: LineSegment StartX=-3.5 StartY=1e-16 StartZ=0 EndX=-1.6 EndY=1e-16 EndZ=0
    g1: LineSegment StartX=-1.6 StartY=1e-16 StartZ=0 EndX=-1.6 EndY=1.5 EndZ=0
    g2: LineSegment StartX=-3.5 StartY=1.5 StartZ=0 EndX=-1.6 EndY=1.5 EndZ=0
    g3: LineSegment StartX=-3.5 StartY=1e-16 StartZ=0 EndX=-4.8 EndY=1e-16 EndZ=0
    g4: Circle CenterX=-3.5 CenterY=1.3 CenterZ=0 NormalX=0 NormalY=0 NormalZ=1 AngleXU=0 Radius=1
    g5: Circle CenterX=-3.5 CenterY=1e-16 CenterZ=0 NormalX=0 NormalY=0 NormalZ=1 AngleXU=0 Radius=1
    g6: Circle CenterX=-4.8 CenterY=1e-16 CenterZ=0 NormalX=0 NormalY=0 NormalZ=1 AngleXU=0 Radius=1
    g7: BSplineCurve PolesCount=3 KnotsCount=2 Degree=2 IsPeriodic=0
    g8: GeomPoint X=-3.5 Y=1.3 Z=0
    g9: GeomPoint X=-4.8 Y=1e-16 Z=0
    g10: LineSegment StartX=-3.5 StartY=1.3 StartZ=0 EndX=-3.5 EndY=1.5 EndZ=0
  constraints (24):
    c: Horizontal(g0)
    c: Distance(g0) = 1.9
    c: Block(g0)
    c: Coincident(g1,g0)
    c: Vertical(g1)
    c: Coincident(g2,g1)
    c: Horizontal(g2)
    c: Coincident(g3,g0)
    c: Horizontal(g3)
    c: Distance(g3) = 1.3
    c: Weight(g4) = 1
    c: Equal(g4,g5)
    c: Coincident(g5,g0)
    c: Equal(g4,g6)
    c: Coincident(g7,g3)
    c: InternalAlignment(g4,g7)
    c: InternalAlignment(g5,g7)
    c: InternalAlignment(g6,g7)
    c: InternalAlignment(g8,g7)
    c: InternalAlignment(g9,g7)
    c: Coincident(g10,g7)
    c: Coincident(g10,g2)
    c: Vertical(g10)
    c: Block(g10)
FEATURE [Part::Feature] Face035
  shape: bbox 3.2 x 1.5 x 2e-07 mm, 1 faces, 0 solids (baked)
FEATURE [Part::Revolution] Revolve039  label="backCaseScrewRetainer"
  Angle = 360
  Axis = (0,1,0)
  Base = (0,0,0)
  FaceMakerClass = Part::FaceMakerBullseye
  Placement = pos=(12.5,3,62) rot=(0,0,1;0rad)
  Solid = false
  Source = -> Face035
  Symmetric = false
FEATURE [Part::Feature] Face036
  shape: bbox 3.2 x 1.5 x 2e-07 mm, 1 faces, 0 solids (baked)
FEATURE [Part::Feature] Face039
  shape: bbox 4.8 x 30.2 x 2e-07 mm, 1 faces, 0 solids (baked)
FEATURE [Part::Revolution] Revolve043  label="frontCaseScrewPost002"
  Angle = 360
  Axis = (0,1,0)
  Base = (0,0,0)
  FaceMakerClass = Part::FaceMakerBullseye
  Placement = pos=(89.5,4.5,3.5) rot=(0,0,1;0rad)
  Solid = false
  Source = -> Face039
  Symmetric = false
FEATURE [Part::Feature] Face042
  shape: bbox 4.8 x 30.2 x 2e-07 mm, 1 faces, 0 solids (baked)
FEATURE [Part::Revolution] Revolve046  label="frontCaseScrewPost003"
  Angle = 360
  Axis = (0,1,0)
  Base = (0,0,0)
  FaceMakerClass = Part::FaceMakerBullseye
  Placement = pos=(89.5,4.5,68.5) rot=(0,0,1;0rad)
  Solid = false
  Source = -> Face042
  Symmetric = false
FEATURE [Part::Feature] Face043
  shape: bbox 3.2 x 1.5 x 2e-07 mm, 1 faces, 0 solids (baked)
FEATURE [Part::Revolution] Revolve047  label="frontCaseScrewRetainer002"
  Angle = 360
  Axis = (0,1,0)
  Base = (0,0,0)
  FaceMakerClass = Part::FaceMakerBullseye
  Placement = pos=(89.5,3,68.5) rot=(0,0,1;0rad)
  Solid = false
  Source = -> Face043
  Symmetric = false
FEATURE [Part::Feature] Face044
  shape: bbox 3.2 x 1.5 x 2e-07 mm, 1 faces, 0 solids (baked)
FEATURE [Part::Revolution] Revolve048  label="frontCaseScrewRetainer003"
  Angle = 360
  Axis = (0,1,0)
  Base = (0,0,0)
  FaceMakerClass = Part::FaceMakerBullseye
  Placement = pos=(89.5,3,3.5) rot=(0,0,1;0rad)
  Solid = false
  Source = -> Face044
  Symmetric = false
FEATURE [App::MeasureDistance] Distance002  label="Distance: 1.67 mm"
  Distance = 1.66921
  P1 = (99.2361,4.7524,71.7)
  P2 = (99.2347,6.42161,71.7)
FEATURE [Sketcher::SketchObject] Sketch018
  FullyConstrained = true
  sketch-geometry (7):
    g0: LineSegment StartX=0 StartY=0 StartZ=0 EndX=0 EndY=6 EndZ=0
    g1: Circle CenterX=0 CenterY=0 CenterZ=0 NormalX=0 NormalY=0 NormalZ=1 AngleXU=0 Radius=1
    g2: Circle CenterX=8 CenterY=6 CenterZ=0 NormalX=0 NormalY=0 NormalZ=1 AngleXU=0 Radius=1
    g3: BSplineCurve PolesCount=3 KnotsCount=2 Degree=2 IsPeriodic=0
    g4: GeomPoint X=0 Y=0 Z=0
    g5: GeomPoint X=8 Y=6 Z=0
    g6: LineSegment StartX=0 StartY=6 StartZ=0 EndX=8 EndY=6 EndZ=0
  constraints (14):
    c: Coincident(g0,g-1)
    c: Distance(g0) = 6
    c: Vertical(g0)
    c: Coincident(g3,g0)
    c: Weight(g1) = 1
    c: Equal(g1,g2)
    c: InternalAlignment(g1,g3)
    c: InternalAlignment(g2,g3)
    c: InternalAlignment(g4,g3)
    c: InternalAlignment(g5,g3)
    c: Block(g3)
    c: Coincident(g6,g0)
    c: Coincident(g6,g3)
    c: Horizontal(g6)
FEATURE [Part::Extrusion] Extrude012  label="caseScrewPillarBracket"
  Base = -> Sketch018
  Dir = (0,0,1)
  DirMode = 2
  FaceMakerClass = Part::FaceMakerBullseye
  LengthFwd = 2.4
  LengthRev = 0
  Placement = pos=(15.76,29,8.8) rot=(0,1,0;0rad)
  Solid = true
  Symmetric = false
FEATURE [Sketcher::SketchObject] Sketch019
  FullyConstrained = true
  sketch-geometry (7):
    g0: LineSegment StartX=0 StartY=0 StartZ=0 EndX=0 EndY=6 EndZ=0
    g1: Circle CenterX=0 CenterY=0 CenterZ=0 NormalX=0 NormalY=0 NormalZ=1 AngleXU=0 Radius=1
    g2: Circle CenterX=8 CenterY=6 CenterZ=0 NormalX=0 NormalY=0 NormalZ=1 AngleXU=0 Radius=1
    g3: BSplineCurve PolesCount=3 KnotsCount=2 Degree=2 IsPeriodic=0
    g4: GeomPoint X=0 Y=0 Z=0
    g5: GeomPoint X=8 Y=6 Z=0
    g6: LineSegment StartX=0 StartY=6 StartZ=0 EndX=8 EndY=6 EndZ=0
  constraints (14):
    c: Coincident(g0,g-1)
    c: Distance(g0) = 6
    c: Vertical(g0)
    c: Coincident(g3,g0)
    c: Weight(g1) = 1
    c: Equal(g1,g2)
    c: InternalAlignment(g1,g3)
    c: InternalAlignment(g2,g3)
    c: InternalAlignment(g4,g3)
    c: InternalAlignment(g5,g3)
    c: Block(g3)
    c: Coincident(g6,g0)
    c: Coincident(g6,g3)
    c: Horizontal(g6)
FEATURE [Part::Extrusion] Extrude013  label="caseScrewPillarBracket001"
  Base = -> Sketch019
  Dir = (0,0,1)
  DirMode = 2
  FaceMakerClass = Part::FaceMakerBullseye
  LengthFwd = 2.4
  LengthRev = 0
  Placement = pos=(15.76,29,60.8) rot=(0,0,1;0rad)
  Solid = true
  Symmetric = false
FEATURE [Sketcher::SketchObject] Sketch020
  FullyConstrained = true
  sketch-geometry (7):
    g0: LineSegment StartX=0 StartY=0 StartZ=0 EndX=0 EndY=6 EndZ=0
    g1: Circle CenterX=0 CenterY=0 CenterZ=0 NormalX=0 NormalY=0 NormalZ=1 AngleXU=0 Radius=1
    g2: Circle CenterX=8 CenterY=6 CenterZ=0 NormalX=0 NormalY=0 NormalZ=1 AngleXU=0 Radius=1
    g3: BSplineCurve PolesCount=3 KnotsCount=2 Degree=2 IsPeriodic=0
    g4: GeomPoint X=0 Y=0 Z=0
    g5: GeomPoint X=8 Y=6 Z=0
    g6: LineSegment StartX=0 StartY=6 StartZ=0 EndX=8 EndY=6 EndZ=0
  constraints (14):
    c: Coincident(g0,g-1)
    c: Distance(g0) = 6
    c: Vertical(g0)
    c: Coincident(g3,g0)
    c: Weight(g1) = 1
    c: Equal(g1,g2)
    c: InternalAlignment(g1,g3)
    c: InternalAlignment(g2,g3)
    c: InternalAlignment(g4,g3)
    c: InternalAlignment(g5,g3)
    c: Block(g3)
    c: Coincident(g6,g0)
    c: Coincident(g6,g3)
    c: Horizontal(g6)
FEATURE [Part::Extrusion] Extrude014  label="caseScrewPillarBracket002"
  Base = -> Sketch020
  Dir = (0,0,1)
  DirMode = 2
  FaceMakerClass = Part::FaceMakerBullseye
  LengthFwd = 2.4
  LengthRev = 0
  Placement = pos=(13.7,29,13.26) rot=(0,-1,0;1.5708rad)
  Solid = true
  Symmetric = false
FEATURE [Sketcher::SketchObject] Sketch021
  FullyConstrained = true
  sketch-geometry (7):
    g0: LineSegment StartX=0 StartY=0 StartZ=0 EndX=0 EndY=6 EndZ=0
    g1: Circle CenterX=0 CenterY=0 CenterZ=0 NormalX=0 NormalY=0 NormalZ=1 AngleXU=0 Radius=1
    g2: Circle CenterX=8 CenterY=6 CenterZ=0 NormalX=0 NormalY=0 NormalZ=1 AngleXU=0 Radius=1
    g3: BSplineCurve PolesCount=3 KnotsCount=2 Degree=2 IsPeriodic=0
    g4: GeomPoint X=0 Y=0 Z=0
    g5: GeomPoint X=8 Y=6 Z=0
    g6: LineSegment StartX=0 StartY=6 StartZ=0 EndX=8 EndY=6 EndZ=0
  constraints (14):
    c: Coincident(g0,g-1)
    c: Distance(g0) = 6
    c: Vertical(g0)
    c: Coincident(g3,g0)
    c: Weight(g1) = 1
    c: Equal(g1,g2)
    c: InternalAlignment(g1,g3)
    c: InternalAlignment(g2,g3)
    c: InternalAlignment(g4,g3)
    c: InternalAlignment(g5,g3)
    c: Block(g3)
    c: Coincident(g6,g0)
    c: Coincident(g6,g3)
    c: Horizontal(g6)
FEATURE [Part::Extrusion] Extrude015  label="caseScrewPillarBracket003"
  Base = -> Sketch021
  Dir = (0,0,1)
  DirMode = 2
  FaceMakerClass = Part::FaceMakerBullseye
  LengthFwd = 2.4
  LengthRev = 0
  Placement = pos=(11.3,29,58.74) rot=(0,1,0;1.5708rad)
  Solid = true
  Symmetric = false
FEATURE [Sketcher::SketchObject] Sketch022
  FullyConstrained = true
  sketch-geometry (7):
    g0: LineSegment StartX=0 StartY=0 StartZ=0 EndX=0 EndY=6 EndZ=0
    g1: Circle CenterX=0 CenterY=0 CenterZ=0 NormalX=0 NormalY=0 NormalZ=1 AngleXU=0 Radius=1
    g2: Circle CenterX=8 CenterY=6 CenterZ=0 NormalX=0 NormalY=0 NormalZ=1 AngleXU=0 Radius=1
    g3: BSplineCurve PolesCount=3 KnotsCount=2 Degree=2 IsPeriodic=0
    g4: GeomPoint X=0 Y=0 Z=0
    g5: GeomPoint X=8 Y=6 Z=0
    g6: LineSegment StartX=0 StartY=6 StartZ=0 EndX=8 EndY=6 EndZ=0
  constraints (14):
    c: Coincident(g0,g-1)
    c: Distance(g0) = 6
    c: Vertical(g0)
    c: Coincident(g3,g0)
    c: Weight(g1) = 1
    c: Equal(g1,g2)
    c: InternalAlignment(g1,g3)
    c: InternalAlignment(g2,g3)
    c: InternalAlignment(g4,g3)
    c: InternalAlignment(g5,g3)
    c: Block(g3)
    c: Coincident(g6,g0)
    c: Coincident(g6,g3)
    c: Horizontal(g6)
FEATURE [Part::Extrusion] Extrude016  label="caseScrewPillarBracket004"
  Base = -> Sketch022
  Dir = (0,0,1)
  DirMode = 2
  FaceMakerClass = Part::FaceMakerBullseye
  LengthFwd = 2.4
  LengthRev = 0
  Placement = pos=(88.3,29,65.23) rot=(0,1,0;1.5708rad)
  Solid = true
  Symmetric = false
FEATURE [Sketcher::SketchObject] Sketch023
  FullyConstrained = true
  sketch-geometry (7):
    g0: LineSegment StartX=0 StartY=0 StartZ=0 EndX=0 EndY=6 EndZ=0
    g1: Circle CenterX=0 CenterY=0 CenterZ=0 NormalX=0 NormalY=0 NormalZ=1 AngleXU=0 Radius=1
    g2: Circle CenterX=8 CenterY=6 CenterZ=0 NormalX=0 NormalY=0 NormalZ=1 AngleXU=0 Radius=1
    g3: BSplineCurve PolesCount=3 KnotsCount=2 Degree=2 IsPeriodic=0
    g4: GeomPoint X=0 Y=0 Z=0
    g5: GeomPoint X=8 Y=6 Z=0
    g6: LineSegment StartX=0 StartY=6 StartZ=0 EndX=8 EndY=6 EndZ=0
  constraints (14):
    c: Coincident(g0,g-1)
    c: Distance(g0) = 6
    c: Vertical(g0)
    c: Coincident(g3,g0)
    c: Weight(g1) = 1
    c: Equal(g1,g2)
    c: InternalAlignment(g1,g3)
    c: InternalAlignment(g2,g3)
    c: InternalAlignment(g4,g3)
    c: InternalAlignment(g5,g3)
    c: Block(g3)
    c: Coincident(g6,g0)
    c: Coincident(g6,g3)
    c: Horizontal(g6)
FEATURE [Part::Extrusion] Extrude017  label="caseScrewPillarBracket005"
  Base = -> Sketch023
  Dir = (0,0,1)
  DirMode = 2
  FaceMakerClass = Part::FaceMakerBullseye
  LengthFwd = 2.4
  LengthRev = 0
  Placement = pos=(90.7,29,6.77) rot=(0,-1,0;1.5708rad)
  Solid = true
  Symmetric = false
FEATURE [Sketcher::SketchObject] Sketch024
  FullyConstrained = true
  sketch-geometry (7):
    g0: LineSegment StartX=0 StartY=0 StartZ=0 EndX=0 EndY=6 EndZ=0
    g1: Circle CenterX=0 CenterY=0 CenterZ=0 NormalX=0 NormalY=0 NormalZ=1 AngleXU=0 Radius=1
    g2: Circle CenterX=8 CenterY=6 CenterZ=0 NormalX=0 NormalY=0 NormalZ=1 AngleXU=0 Radius=1
    g3: BSplineCurve PolesCount=3 KnotsCount=2 Degree=2 IsPeriodic=0
    g4: GeomPoint X=0 Y=0 Z=0
    g5: GeomPoint X=8 Y=6 Z=0
    g6: LineSegment StartX=0 StartY=6 StartZ=0 EndX=8 EndY=6 EndZ=0
  constraints (14):
    c: Coincident(g0,g-1)
    c: Distance(g0) = 6
    c: Vertical(g0)
    c: Coincident(g3,g0)
    c: Weight(g1) = 1
    c: Equal(g1,g2)
    c: InternalAlignment(g1,g3)
    c: InternalAlignment(g2,g3)
    c: InternalAlignment(g4,g3)
    c: InternalAlignment(g5,g3)
    c: Block(g3)
    c: Coincident(g6,g0)
    c: Coincident(g6,g3)
    c: Horizontal(g6)
FEATURE [Part::Extrusion] Extrude018  label="caseScrewPillarBracket006"
  Base = -> Sketch024
  Dir = (0,0,1)
  DirMode = 2
  FaceMakerClass = Part::FaceMakerBullseye
  LengthFwd = 2.4
  LengthRev = 0
  Placement = pos=(103.7,29,6.77) rot=(0,-1,0;1.5708rad)
  Solid = true
  Symmetric = false
FEATURE [Sketcher::SketchObject] Sketch025
  FullyConstrained = true
  sketch-geometry (7):
    g0: LineSegment StartX=0 StartY=0 StartZ=0 EndX=0 EndY=6 EndZ=0
    g1: Circle CenterX=0 CenterY=0 CenterZ=0 NormalX=0 NormalY=0 NormalZ=1 AngleXU=0 Radius=1
    g2: Circle CenterX=8 CenterY=6 CenterZ=0 NormalX=0 NormalY=0 NormalZ=1 AngleXU=0 Radius=1
    g3: BSplineCurve PolesCount=3 KnotsCount=2 Degree=2 IsPeriodic=0
    g4: GeomPoint X=0 Y=0 Z=0
    g5: GeomPoint X=8 Y=6 Z=0
    g6: LineSegment StartX=0 StartY=6 StartZ=0 EndX=8 EndY=6 EndZ=0
  constraints (14):
    c: Coincident(g0,g-1)
    c: Distance(g0) = 6
    c: Vertical(g0)
    c: Coincident(g3,g0)
    c: Weight(g1) = 1
    c: Equal(g1,g2)
    c: InternalAlignment(g1,g3)
    c: InternalAlignment(g2,g3)
    c: InternalAlignment(g4,g3)
    c: InternalAlignment(g5,g3)
    c: Block(g3)
    c: Coincident(g6,g0)
    c: Coincident(g6,g3)
    c: Horizontal(g6)
FEATURE [Part::Extrusion] Extrude019  label="caseScrewPillarBracket007"
  Base = -> Sketch025
  Dir = (0,0,1)
  DirMode = 2
  FaceMakerClass = Part::FaceMakerBullseye
  LengthFwd = 2.4
  LengthRev = 0
  Placement = pos=(101.3,29,65.23) rot=(0,1,0;1.5708rad)
  Solid = true
  Symmetric = false
FEATURE [Part::Box] Box011  label="frontCaseScrewPillarBracket"
  AttacherType = Attacher::AttachEngine3D
  Height = 2.4
  Length = 16
  Placement = pos=(87,28,2.3) rot=(0,0,1;0rad)
  Width = 7
FEATURE [Part::Box] Box012  label="frontCaseScrewPillarBracket001"
  AttacherType = Attacher::AttachEngine3D
  Height = 2.4
  Length = 16
  Placement = pos=(87,28,67.3) rot=(0,0,1;0rad)
  Width = 7
FEATURE [Sketcher::SketchObject] Sketch026
  FullyConstrained = true
  sketch-geometry (17):
    g0: Circle CenterX=-3.5 CenterY=23.5 CenterZ=0 NormalX=0 NormalY=0 NormalZ=1 AngleXU=0 Radius=1
    g1: Circle CenterX=-1 CenterY=15.25 CenterZ=0 NormalX=0 NormalY=0 NormalZ=1 AngleXU=0 Radius=1
    g2: Circle CenterX=-3.5 CenterY=7 CenterZ=0 NormalX=0 NormalY=0 NormalZ=1 AngleXU=0 Radius=1
    g3: BSplineCurve PolesCount=3 KnotsCount=2 Degree=2 IsPeriodic=0
    g4: GeomPoint X=-3.5 Y=23.5 Z=0
    g5: GeomPoint X=-3.5 Y=7 Z=0
    g6: Circle CenterX=-4.8 CenterY=30.5 CenterZ=0 NormalX=0 NormalY=0 NormalZ=1 AngleXU=0 Radius=1
    g7: Circle CenterX=-3.5 CenterY=30.5 CenterZ=0 NormalX=0 NormalY=0 NormalZ=1 AngleXU=0 Radius=1
    g8: Circle CenterX=-3.5 CenterY=29.2 CenterZ=0 NormalX=0 NormalY=0 NormalZ=1 AngleXU=0 Radius=1
    g9: BSplineCurve PolesCount=3 KnotsCount=2 Degree=2 IsPeriodic=0
    g10: GeomPoint X=-4.8 Y=30.5 Z=0
    g11: GeomPoint X=-3.5 Y=29.2 Z=0
    g12: LineSegment StartX=-3.5 StartY=29.2 StartZ=0 EndX=-3.5 EndY=23.5 EndZ=0
    g13: LineSegment StartX=-4.8 StartY=30.5 StartZ=0 EndX=0 EndY=30.5 EndZ=0
    g14: LineSegment StartX=-3.5 StartY=5 StartZ=0 EndX=-3.5 EndY=7 EndZ=0
    g15: LineSegment StartX=0 StartY=5 StartZ=0 EndX=0 EndY=30.5 EndZ=0
    g16: LineSegment StartX=-3.5 StartY=5 StartZ=0 EndX=0 EndY=5 EndZ=0
  constraints (33):
    c: Weight(g0) = 1
    c: Equal(g0,g1)
    c: Equal(g0,g2)
    c: InternalAlignment(g0,g3)
    c: InternalAlignment(g1,g3)
    c: InternalAlignment(g2,g3)
    c: InternalAlignment(g4,g3)
    c: InternalAlignment(g5,g3)
    c: Block(g3)
    c: Weight(g6) = 1
    c: Equal(g6,g7)
    c: Equal(g6,g8)
    c: InternalAlignment(g6,g9)
    c: InternalAlignment(g7,g9)
    c: InternalAlignment(g8,g9)
    c: InternalAlignment(g10,g9)
    c: InternalAlignment(g11,g9)
    c: Block(g9)
    c: Coincident(g12,g9)
    c: Coincident(g12,g3)
    c: Vertical(g12)
    c: Coincident(g13,g9)
    c: Horizontal(g13)
    c: Distance(g13) = 4.8
    c: Coincident(g14,g3)
    c: Vertical(g14)
    c: Coincident(g15,g13)
    c: Vertical(g15)
    c: Tangent(g15,g1)
    c: Distance(g14) = 2
    c: Coincident(g16,g14)
    c: Horizontal(g16)
    c: Coincident(g15,g16)
FEATURE [Part::Feature] Face050
  shape: bbox 4.8 x 25.5 x 2e-07 mm, 1 faces, 0 solids (baked)
FEATURE [Part::Revolution] Revolve054  label="moreFrontCaseScrewPost001"
  Angle = 360
  Axis = (0,1,0)
  Base = (0,0,0)
  FaceMakerClass = Part::FaceMakerBullseye
  Placement = pos=(102.5,4.5,3.5) rot=(0,0,1;0rad)
  Solid = false
  Source = -> Face050
  Symmetric = false
FEATURE [Part::Feature] Face051
  shape: bbox 4.8 x 25.5 x 2e-07 mm, 1 faces, 0 solids (baked)
FEATURE [Part::Revolution] Revolve055  label="moreFrontCaseScrewPost002"
  Angle = 360
  Axis = (0,1,0)
  Base = (0,0,0)
  FaceMakerClass = Part::FaceMakerBullseye
  Placement = pos=(102.5,4.5,68.5) rot=(0,0,1;0rad)
  Solid = false
  Source = -> Face051
  Symmetric = false
FEATURE [Sketcher::SketchObject] Sketch027
  FullyConstrained = true
  sketch-geometry (10):
    g0: LineSegment StartX=-1.6 StartY=4.7 StartZ=0 EndX=-1.6 EndY=1.7 EndZ=0
    g1: LineSegment StartX=-3.5 StartY=4.7 StartZ=0 EndX=-1.6 EndY=4.7 EndZ=0
    g2: LineSegment StartX=-1.6 StartY=1.7 StartZ=0 EndX=-1.6 EndY=1.5 EndZ=0
    g3: LineSegment StartX=-1.6 StartY=1.5 StartZ=0 EndX=-5.2 EndY=1.5 EndZ=0
    g4: Circle CenterX=-3.5 CenterY=4.7 CenterZ=0 NormalX=0 NormalY=0 NormalZ=1 AngleXU=0 Radius=1
    g5: Circle CenterX=-3.59627 CenterY=2.99743 CenterZ=0 NormalX=0 NormalY=0 NormalZ=1 AngleXU=0 Radius=1
    g6: Circle CenterX=-5.2 CenterY=1.5 CenterZ=0 NormalX=0 NormalY=0 NormalZ=1 AngleXU=0 Radius=1
    g7: BSplineCurve PolesCount=3 KnotsCount=2 Degree=2 IsPeriodic=0
    g8: GeomPoint X=-3.5 Y=4.7 Z=0
    g9: GeomPoint X=-5.2 Y=1.5 Z=0
  constraints (23):
    c: Vertical(g0)
    c: Distance(g0) = 3
    c: Coincident(g1,g0)
    c: Horizontal(g1)
    c: Block(g0)
    c: Block(g1)
    c: Coincident(g2,g0)
    c: Vertical(g2)
    c: Distance(g2) = 0.2
    c: Coincident(g3,g2)
    c: Horizontal(g3)
    c: Block(g3)
    c: Coincident(g7,g1)
    c: Weight(g4) = 1
    c: Equal(g4,g5)
    c: Equal(g4,g6)
    c: Coincident(g7,g3)
    c: InternalAlignment(g4,g7)
    c: InternalAlignment(g5,g7)
    c: InternalAlignment(g6,g7)
    c: InternalAlignment(g8,g7)
    c: InternalAlignment(g9,g7)
    c: Block(g7)
FEATURE [Sketcher::SketchObject] Sketch028
  FullyConstrained = true
  sketch-geometry (18):
    g0: LineSegment StartX=0 StartY=3e-16 StartZ=0 EndX=0 EndY=1.7 EndZ=0
    g1: LineSegment StartX=-3.5 StartY=0 StartZ=0 EndX=-3.5 EndY=0.9 EndZ=0
    g2: Circle CenterX=-2.7 CenterY=1.7 CenterZ=0 NormalX=0 NormalY=0 NormalZ=1 AngleXU=0 Radius=1
    g3: Circle CenterX=-3.5 CenterY=1.7 CenterZ=0 NormalX=0 NormalY=0 NormalZ=1 AngleXU=0 Radius=1
    g4: Circle CenterX=-3.5 CenterY=0.9 CenterZ=0 NormalX=0 NormalY=0 NormalZ=1 AngleXU=0 Radius=1
    g5: BSplineCurve PolesCount=3 KnotsCount=2 Degree=2 IsPeriodic=0
    g6: GeomPoint X=-2.7 Y=1.7 Z=0
    g7: GeomPoint X=-3.5 Y=0.9 Z=0
    g8: LineSegment StartX=-3.5 StartY=0 StartZ=0 EndX=-3.5 EndY=-7 EndZ=0
    g9: LineSegment StartX=0 StartY=3e-16 StartZ=0 EndX=0 EndY=-7 EndZ=0
    g10: LineSegment StartX=-3.5 StartY=-7 StartZ=0 EndX=0 EndY=-7 EndZ=0
    g11: LineSegment StartX=-2.7 StartY=1.7 StartZ=0 EndX=-1.6 EndY=1.7 EndZ=0
    g12: LineSegment StartX=0 StartY=1.7 StartZ=0 EndX=0 EndY=4.5 EndZ=0
    g13: LineSegment StartX=0 StartY=4.5 StartZ=0 EndX=0 EndY=10.8 EndZ=0
    g14: LineSegment StartX=0 StartY=10.8 StartZ=0 EndX=-2 EndY=10.8 EndZ=0
    g15: LineSegment StartX=-1.6 StartY=4.7 StartZ=0 EndX=-1.6 EndY=1.7 EndZ=0
    g16: LineSegment StartX=-1.6 StartY=4.7 StartZ=0 EndX=-2 EndY=4.7 EndZ=0
    g17: LineSegment StartX=-2 StartY=4.7 StartZ=0 EndX=-2 EndY=10.8 EndZ=0
  constraints (44):
    c: Vertical(g0)
    c: Vertical(g1)
    c: Distance(g1) = 0.9
    c: Block(g0)
    c: Distance(g0) = 1.7
    c: Weight(g2) = 1
    c: Equal(g2,g3)
    c: Equal(g2,g4)
    c: Coincident(g5,g1)
    c: InternalAlignment(g2,g5)
    c: InternalAlignment(g3,g5)
    c: InternalAlignment(g4,g5)
    c: InternalAlignment(g6,g5)
    c: InternalAlignment(g7,g5)
    c: Block(g5)
    c: Coincident(g8,g1)
    c: Vertical(g8)
    c: Distance(g8) = 7
    c: Vertical(g9)
    c: Equal(g8,g9) = 7
    c: Coincident(g9,g0)
    c: Coincident(g10,g8)
    c: Coincident(g10,g9)
    c: Horizontal(g10)
    c: Coincident(g11,g5)
    c: Horizontal(g11)
    c: Coincident(g12,g0)
    c: Vertical(g12)
    c: Distance(g12) = 2.8
    c: Coincident(g13,g12)
    c: Vertical(g13)
    c: Distance(g13) = 6.3
    c: Coincident(g14,g13)
    c: Horizontal(g14)
    c: Distance(g14) = 2
    c: Vertical(g15)
    c: Distance(g15) = 3
    c: Block(g11)
    c: Coincident(g15,g11)
    c: Coincident(g16,g15)
    c: Horizontal(g16)
    c: Coincident(g17,g16)
    c: Coincident(g17,g14)
    c: Vertical(g17)
FEATURE [Part::Revolution] Revolve040  label="backCaseScrewRetainer001"
  Angle = 360
  Axis = (0,1,0)
  Base = (0,0,0)
  FaceMakerClass = Part::FaceMakerBullseye
  Placement = pos=(12.5,3,10) rot=(0,0,1;0rad)
  Solid = false
  Source = -> Face036
  Symmetric = false
FEATURE [Part::Feature] Face055
  shape: bbox 3.5 x 30.2 x 2e-07 mm, 1 faces, 0 solids (baked)
FEATURE [Part::Revolution] Revolve059  label="backCaseScrewPost"
  Angle = 360
  Axis = (0,1,0)
  Base = (0,0,0)
  FaceMakerClass = Part::FaceMakerBullseye
  Placement = pos=(12.5,4.5,10) rot=(0,0,1;0rad)
  Solid = false
  Source = -> Face055
  Symmetric = false
FEATURE [Part::Feature] Face056
  shape: bbox 3.5 x 30.2 x 2e-07 mm, 1 faces, 0 solids (baked)
FEATURE [Part::Revolution] Revolve060  label="backCaseScrewPost001"
  Angle = 360
  Axis = (0,1,0)
  Base = (0,0,0)
  FaceMakerClass = Part::FaceMakerBullseye
  Placement = pos=(12.5,4.5,62) rot=(0,0,1;0rad)
  Solid = false
  Source = -> Face056
  Symmetric = false
FEATURE [Part::Feature] Face057
  shape: bbox 3.5 x 17.8 x 2e-07 mm, 1 faces, 0 solids (baked)
FEATURE [Part::Revolution] Revolve061  label="removeToCreateScrewAndThreadedInsertHole"
  Angle = 360
  Axis = (0,1,0)
  Base = (0,0,0)
  FaceMakerClass = Part::FaceMakerBullseye
  Placement = pos=(12.5,0,10) rot=(0,0,1;0rad)
  Solid = false
  Source = -> Face057
  Symmetric = false
FEATURE [Part::Feature] Face058
  shape: bbox 3.5 x 17.8 x 2e-07 mm, 1 faces, 0 solids (baked)
FEATURE [Part::Revolution] Revolve062  label="removeToCreateScrewAndThreadedInsertHole001"
  Angle = 360
  Axis = (0,1,0)
  Base = (0,0,0)
  FaceMakerClass = Part::FaceMakerBullseye
  Placement = pos=(12.5,0,62) rot=(0,0,1;0rad)
  Solid = false
  Source = -> Face058
  Symmetric = false
FEATURE [Part::Feature] Face059
  shape: bbox 3.5 x 17.8 x 2e-07 mm, 1 faces, 0 solids (baked)
FEATURE [Part::Revolution] Revolve063  label="removeToCreateScrewAndThreadedInsertHole002"
  Angle = 360
  Axis = (0,1,0)
  Base = (0,0,0)
  FaceMakerClass = Part::FaceMakerBullseye
  Placement = pos=(89.5,0,68.5) rot=(0,0,1;0rad)
  Solid = false
  Source = -> Face059
  Symmetric = false
FEATURE [Part::Feature] Face060
  shape: bbox 3.5 x 17.8 x 2e-07 mm, 1 faces, 0 solids (baked)
FEATURE [Part::Revolution] Revolve064  label="removeToCreateScrewAndThreadedInsertHole003"
  Angle = 360
  Axis = (0,1,0)
  Base = (0,0,0)
  FaceMakerClass = Part::FaceMakerBullseye
  Placement = pos=(89.5,0,3.5) rot=(0,0,1;0rad)
  Solid = false
  Source = -> Face060
  Symmetric = false
FEATURE [Part::Feature] Face061
  shape: bbox 3.5 x 17.8 x 2e-07 mm, 1 faces, 0 solids (baked)
FEATURE [Part::Revolution] Revolve065  label="removeToCreateScrewAndThreadedInsertHole004"
  Angle = 360
  Axis = (0,1,0)
  Base = (0,0,0)
  FaceMakerClass = Part::FaceMakerBullseye
  Placement = pos=(102.5,4.7,3.5) rot=(0,0,1;0rad)
  Solid = false
  Source = -> Face061
  Symmetric = false
FEATURE [Part::Feature] Face062
  shape: bbox 3.5 x 17.8 x 2e-07 mm, 1 faces, 0 solids (baked)
FEATURE [Part::Revolution] Revolve066  label="removeToCreateScrewAndThreadedInsertHole005"
  Angle = 360
  Axis = (0,1,0)
  Base = (0,0,0)
  FaceMakerClass = Part::FaceMakerBullseye
  Placement = pos=(102.5,4.7,68.5) rot=(0,0,1;0rad)
  Solid = false
  Source = -> Face062
  Symmetric = false
FEATURE [Part::MultiFuse] Fusion047  label="makeHoles"
  Shapes = -> [Revolve066,Revolve065,Revolve064,Revolve063,Revolve062,Revolve061]
FEATURE [Part::Feature] Face063
  shape: bbox 3.6 x 3.2 x 2e-07 mm, 1 faces, 0 solids (baked)
FEATURE [Part::Revolution] Revolve067  label="moreFrontCaseScrewRetainer002"
  Angle = 360
  Axis = (0,1,0)
  Base = (0,0,0)
  FaceMakerClass = Part::FaceMakerBullseye
  Placement = pos=(102.5,4.5,68.5) rot=(0,0,1;0rad)
  Solid = false
  Source = -> Face063
  Symmetric = false
FEATURE [Part::Feature] Face064
  shape: bbox 3.6 x 3.2 x 2e-07 mm, 1 faces, 0 solids (baked)
FEATURE [Part::Revolution] Revolve068  label="moreFrontCaseScrewRetainer003"
  Angle = 360
  Axis = (0,1,0)
  Base = (0,0,0)
  FaceMakerClass = Part::FaceMakerBullseye
  Placement = pos=(102.5,4.5,3.5) rot=(0,0,1;0rad)
  Solid = false
  Source = -> Face064
  Symmetric = false
FEATURE [Part::Feature] Face065
  shape: bbox 3.5 x 17.8 x 2e-07 mm, 1 faces, 0 solids (baked)
FEATURE [Part::Revolution] Revolve069  label="removeToCreateScrewAndThreadedInsertHole006"
  Angle = 360
  Axis = (0,1,0)
  Base = (0,0,0)
  FaceMakerClass = Part::FaceMakerBullseye
  Placement = pos=(12.5,0,10) rot=(0,0,1;0rad)
  Solid = false
  Source = -> Face065
  Symmetric = false
FEATURE [Part::Feature] Face066
  shape: bbox 3.5 x 17.8 x 2e-07 mm, 1 faces, 0 solids (baked)
FEATURE [Part::Revolution] Revolve070  label="removeToCreateScrewAndThreadedInsertHole007"
  Angle = 360
  Axis = (0,1,0)
  Base = (0,0,0)
  FaceMakerClass = Part::FaceMakerBullseye
  Placement = pos=(12.5,0,62) rot=(0,0,1;0rad)
  Solid = false
  Source = -> Face066
  Symmetric = false
FEATURE [Part::Feature] Face067
  shape: bbox 3.5 x 17.8 x 2e-07 mm, 1 faces, 0 solids (baked)
FEATURE [Part::Revolution] Revolve071  label="removeToCreateScrewAndThreadedInsertHole008"
  Angle = 360
  Axis = (0,1,0)
  Base = (0,0,0)
  FaceMakerClass = Part::FaceMakerBullseye
  Placement = pos=(89.5,0,68.5) rot=(0,0,1;0rad)
  Solid = false
  Source = -> Face067
  Symmetric = false
FEATURE [Part::Feature] Face068
  shape: bbox 3.5 x 17.8 x 2e-07 mm, 1 faces, 0 solids (baked)
FEATURE [Part::Revolution] Revolve072  label="removeToCreateScrewAndThreadedInsertHole009"
  Angle = 360
  Axis = (0,1,0)
  Base = (0,0,0)
  FaceMakerClass = Part::FaceMakerBullseye
  Placement = pos=(89.5,0,3.5) rot=(0,0,1;0rad)
  Solid = false
  Source = -> Face068
  Symmetric = false
FEATURE [Part::Feature] Face069
  shape: bbox 3.5 x 17.8 x 2e-07 mm, 1 faces, 0 solids (baked)
FEATURE [Part::Feature] Face070
  shape: bbox 3.5 x 17.8 x 2e-07 mm, 1 faces, 0 solids (baked)
FEATURE [Part::Revolution] Revolve073  label="removeToCreateScrewAndThreadedInsertHole010"
  Angle = 360
  Axis = (0,1,0)
  Base = (0,0,0)
  FaceMakerClass = Part::FaceMakerBullseye
  Placement = pos=(102.5,4.7,3.5) rot=(0,0,1;0rad)
  Solid = false
  Source = -> Face069
  Symmetric = false
FEATURE [Part::Revolution] Revolve074  label="removeToCreateScrewAndThreadedInsertHole011"
  Angle = 360
  Axis = (0,1,0)
  Base = (0,0,0)
  FaceMakerClass = Part::FaceMakerBullseye
  Placement = pos=(102.5,4.7,68.5) rot=(0,0,1;0rad)
  Solid = false
  Source = -> Face070
  Symmetric = false
FEATURE [Part::MultiFuse] Fusion048  label="makeHoles001"
  Shapes = -> [Revolve074,Revolve073,Revolve072,Revolve071,Revolve070,Revolve069]
FEATURE [Part::MultiFuse] Fusion049  label="caseScrewRetainers"
  Shapes = -> [Revolve067,Revolve068,Revolve048,Revolve047,Revolve039,Revolve040]
FEATURE [Part::Cut] Cut015  label="caseScrewRetainers001"
  Base = -> Fusion049
  Tool = -> Fusion048
FEATURE [Part::MultiFuse] Fusion050  label="casePillars"
  Shapes = -> [Revolve055,Revolve054,Revolve043,Revolve046,Revolve059,Revolve060]
FEATURE [Part::Feature] Face071 .. Face076  x6 (patterned run collapsed; names and placements below)
  shape: bbox 3.5 x 17.8 x 2e-07 mm, 1 faces, 0 solids (baked)
FEATURE [Part::Revolution] Revolve075  label="removeToCreateScrewAndThreadedInsertHole012"
  Angle = 360
  Axis = (0,1,0)
  Base = (0,0,0)
  FaceMakerClass = Part::FaceMakerBullseye
  Placement = pos=(12.5,0,10) rot=(0,0,1;0rad)
  Solid = false
  Source = -> Face071
  Symmetric = false
FEATURE [Part::Revolution] Revolve076  label="removeToCreateScrewAndThreadedInsertHole013"
  Angle = 360
  Axis = (0,1,0)
  Base = (0,0,0)
  FaceMakerClass = Part::FaceMakerBullseye
  Placement = pos=(12.5,0,62) rot=(0,0,1;0rad)
  Solid = false
  Source = -> Face072
  Symmetric = false
FEATURE [Part::Revolution] Revolve077  label="removeToCreateScrewAndThreadedInsertHole014"
  Angle = 360
  Axis = (0,1,0)
  Base = (0,0,0)
  FaceMakerClass = Part::FaceMakerBullseye
  Placement = pos=(89.5,0,68.5) rot=(0,0,1;0rad)
  Solid = false
  Source = -> Face073
  Symmetric = false
FEATURE [Part::Revolution] Revolve078  label="removeToCreateScrewAndThreadedInsertHole015"
  Angle = 360
  Axis = (0,1,0)
  Base = (0,0,0)
  FaceMakerClass = Part::FaceMakerBullseye
  Placement = pos=(89.5,0,3.5) rot=(0,0,1;0rad)
  Solid = false
  Source = -> Face074
  Symmetric = false
FEATURE [Part::Revolution] Revolve079  label="removeToCreateScrewAndThreadedInsertHole016"
  Angle = 360
  Axis = (0,1,0)
  Base = (0,0,0)
  FaceMakerClass = Part::FaceMakerBullseye
  Placement = pos=(102.5,4.7,3.5) rot=(0,0,1;0rad)
  Solid = false
  Source = -> Face075
  Symmetric = false
FEATURE [Part::Revolution] Revolve080  label="removeToCreateScrewAndThreadedInsertHole017"
  Angle = 360
  Axis = (0,1,0)
  Base = (0,0,0)
  FaceMakerClass = Part::FaceMakerBullseye
  Placement = pos=(102.5,4.7,68.5) rot=(0,0,1;0rad)
  Solid = false
  Source = -> Face076
  Symmetric = false
FEATURE [Part::MultiFuse] Fusion051  label="makeHoles002"
  Shapes = -> [Revolve080,Revolve079,Revolve078,Revolve077,Revolve076,Revolve075]
FEATURE [Part::Cut] Cut016  label="caesPillars"
  Base = -> Fusion050
  Tool = -> Fusion051
FEATURE [Part::Revolution] Revolve009  label="plugHousing016"
  Angle = 360
  Axis = (0,1,0)
  Base = (0,0,0)
  FaceMakerClass = Part::FaceMakerBullseye
  Placement = pos=(0,0,36.15) rot=(0,0,1;0rad)
  Solid = false
  Source = -> Face012
  Symmetric = false
FEATURE [Part::MultiFuse] Fusion014  label="plugHousing023"
  Placement = pos=(0,0,0) rot=(0,0,1;1.5708rad)
  Shapes = -> [Revolve011,Revolve009]
FEATURE [Part::Revolution] Revolve010  label="plugHousing017"
  Angle = 360
  Axis = (0,1,0)
  Base = (0,0,0)
  FaceMakerClass = Part::FaceMakerBullseye
  Placement = pos=(0,0,36.15) rot=(0,0,1;0rad)
  Solid = false
  Source = -> Face014
  Symmetric = false
FEATURE [Part::MultiFuse] Fusion015  label="plugHousing024"
  Placement = pos=(0,0,0) rot=(0,0,1;1.5708rad)
  Shapes = -> [Revolve010,Revolve015]
FEATURE [Part::Revolution] Revolve014  label="plugHousing026"
  Angle = 360
  Axis = (0,1,0)
  Base = (0,0,0)
  FaceMakerClass = Part::FaceMakerBullseye
  Placement = pos=(0,0,36.15) rot=(0,0,1;0rad)
  Solid = false
  Source = -> Face011
  Symmetric = false
FEATURE [Part::Revolution] Revolve013  label="plugHousing025"
  Angle = 360
  Axis = (0,1,0)
  Base = (0,0,0)
  FaceMakerClass = Part::FaceMakerBullseye
  Placement = pos=(0,0,36.15) rot=(0,0,1;0rad)
  Solid = false
  Source = -> Face015
  Symmetric = false
FEATURE [Part::MultiFuse] Fusion016  label="plugHousing028"
  Placement = pos=(0,19,0) rot=(0,0,1;3.14159rad)
  Shapes = -> [Fusion014,Fusion013]
FEATURE [Part::MultiFuse] Fusion011  label="plugHousing018"
  Placement = pos=(0,0,0) rot=(0,0,1;1.5708rad)
  Shapes = -> [Revolve014,Revolve013]
FEATURE [Part::MultiFuse] Fusion012  label="plugHousing019"
  Placement = pos=(0,19,0) rot=(0,0,1;3.14159rad)
  Shapes = -> [Fusion011,Fusion015]
FEATURE [Part::MultiFuse] Fusion017  label="plugHousing029"
  Placement = pos=(122.621,0,-0.15) rot=(0,0,1;0rad)
  Shapes = -> [Fusion016,Fusion012]
FEATURE [Part::MultiFuse] Fusion052  label="casePillarRetainers"
  Shapes = -> [Extrude012,Extrude013,Extrude014,Extrude015,Extrude016,Extrude017,Extrude018,Extrude019,Box011,Box012]
FEATURE [Part::Feature] Face077
  shape: bbox 3.5 x 17.8 x 2e-07 mm, 1 faces, 0 solids (baked)
FEATURE [Part::Revolution] Revolve081  label="removeToCreateScrewAndThreadedInsertHole018"
  Angle = 360
  Axis = (0,1,0)
  Base = (0,0,0)
  FaceMakerClass = Part::FaceMakerBullseye
  Placement = pos=(62.3,30.3,19.7) rot=(0,0,1;0rad)
  Solid = false
  Source = -> Face077
  Symmetric = false
FEATURE [Part::Feature] Face078
  shape: bbox 3.5 x 17.8 x 2e-07 mm, 1 faces, 0 solids (baked)
FEATURE [Part::Revolution] Revolve082  label="removeToCreateScrewAndThreadedInsertHole019"
  Angle = 360
  Axis = (0,1,0)
  Base = (0,0,0)
  FaceMakerClass = Part::FaceMakerBullseye
  Placement = pos=(62.3,30.3,51.7) rot=(0,0,1;0rad)
  Solid = false
  Source = -> Face078
  Symmetric = false
FEATURE [Part::Feature] Face079
  shape: bbox 3.5 x 17.8 x 2e-07 mm, 1 faces, 0 solids (baked)
FEATURE [Part::Revolution] Revolve083  label="removeToCreateScrewAndThreadedInsertHole020"
  Angle = 360
  Axis = (0,1,0)
  Base = (0,0,0)
  FaceMakerClass = Part::FaceMakerBullseye
  Placement = pos=(30.3,30.3,19.7) rot=(0,0,1;0rad)
  Solid = false
  Source = -> Face079
  Symmetric = false
FEATURE [Part::Feature] Face080
  shape: bbox 3.5 x 17.8 x 2e-07 mm, 1 faces, 0 solids (baked)
FEATURE [Part::Revolution] Revolve084  label="removeToCreateScrewAndThreadedInsertHole021"
  Angle = 360
  Axis = (0,1,0)
  Base = (0,0,0)
  FaceMakerClass = Part::FaceMakerBullseye
  Placement = pos=(30.3,30.3,51.7) rot=(0,0,1;0rad)
  Solid = false
  Source = -> Face080
  Symmetric = false
FEATURE [Part::MultiFuse] Fusion053  label="createThreadedInsertHolesForFan"
  Shapes = -> [Revolve081,Revolve082,Revolve083,Revolve084]
FEATURE [Part::Cut] Cut017  label="fanScrewHousing001"
  Base = -> Fusion046
  Tool = -> Fusion053
FEATURE [Part::Feature] Face081
  shape: bbox 3.5 x 17.8 x 2e-07 mm, 1 faces, 0 solids (baked)
FEATURE [Part::Revolution] Revolve085  label="removeToCreateScrewAndThreadedInsertHole022"
  Angle = 360
  Axis = (0,1,0)
  Base = (0,0,0)
  FaceMakerClass = Part::FaceMakerBullseye
  Placement = pos=(62.3,30.3,19.7) rot=(0,0,1;0rad)
  Solid = false
  Source = -> Face081
  Symmetric = false
FEATURE [Part::Feature] Face082
  shape: bbox 3.5 x 17.8 x 2e-07 mm, 1 faces, 0 solids (baked)
FEATURE [Part::Revolution] Revolve086  label="removeToCreateScrewAndThreadedInsertHole023"
  Angle = 360
  Axis = (0,1,0)
  Base = (0,0,0)
  FaceMakerClass = Part::FaceMakerBullseye
  Placement = pos=(62.3,30.3,51.7) rot=(0,0,1;0rad)
  Solid = false
  Source = -> Face082
  Symmetric = false
FEATURE [Part::Feature] Face083
  shape: bbox 3.5 x 17.8 x 2e-07 mm, 1 faces, 0 solids (baked)
FEATURE [Part::Revolution] Revolve087  label="removeToCreateScrewAndThreadedInsertHole024"
  Angle = 360
  Axis = (0,1,0)
  Base = (0,0,0)
  FaceMakerClass = Part::FaceMakerBullseye
  Placement = pos=(30.3,30.3,19.7) rot=(0,0,1;0rad)
  Solid = false
  Source = -> Face083
  Symmetric = false
FEATURE [Part::Feature] Face084
  shape: bbox 3.5 x 17.8 x 2e-07 mm, 1 faces, 0 solids (baked)
FEATURE [Part::Revolution] Revolve088  label="removeToCreateScrewAndThreadedInsertHole025"
  Angle = 360
  Axis = (0,1,0)
  Base = (0,0,0)
  FaceMakerClass = Part::FaceMakerBullseye
  Placement = pos=(30.3,30.3,51.7) rot=(0,0,1;0rad)
  Solid = false
  Source = -> Face084
  Symmetric = false
FEATURE [Part::MultiFuse] Fusion054  label="createThreadedInsertHolesForFan001"
  Shapes = -> [Revolve085,Revolve086,Revolve087,Revolve088]
FEATURE [Part::Cut] Cut018  label="top007"
  Base = -> Fusion040
  Tool = -> Fusion054
FEATURE [Sketcher::SketchObject] Sketch029
  FullyConstrained = false
  Placement = pos=(0,0,0) rot=(1,0,0;1.5708rad)
  sketch-geometry (24):
    g0: ArcOfCircle CenterX=-4 CenterY=-10.5 CenterZ=0 NormalX=0 NormalY=0 NormalZ=1 AngleXU=0 Radius=1.5 StartAngle=6e-16 EndAngle=3.14159
    g1: ArcOfCircle CenterX=-34.2 CenterY=-10.5 CenterZ=0 NormalX=0 NormalY=0 NormalZ=1 AngleXU=0 Radius=1.5 StartAngle=0 EndAngle=3.14159
    g2: ArcOfCircle CenterX=-34.2 CenterY=-27.7 CenterZ=0 NormalX=0 NormalY=0 NormalZ=1 AngleXU=0 Radius=1.5 StartAngle=3.14159 EndAngle=6.28319
    g3: ArcOfCircle CenterX=-4 CenterY=-27.7 CenterZ=0 NormalX=0 NormalY=0 NormalZ=1 AngleXU=0 Radius=1.5 StartAngle=3.1416 EndAngle=6.28319
    g4: ArcOfCircle CenterX=-10 CenterY=-4.3 CenterZ=0 NormalX=0 NormalY=0 NormalZ=1 AngleXU=0 Radius=1.5 StartAngle=2e-16 EndAngle=3.14159
    g5: ArcOfCircle CenterX=-16.1 CenterY=-1.8 CenterZ=0 NormalX=0 NormalY=0 NormalZ=1 AngleXU=0 Radius=1.5 StartAngle=5e-16 EndAngle=3.14159
    g6: ArcOfCircle CenterX=-22.1 CenterY=-1.8 CenterZ=0 NormalX=0 NormalY=0 NormalZ=1 AngleXU=0 Radius=1.5 StartAngle=5e-16 EndAngle=3.14159
    g7: ArcOfCircle CenterX=-28.2 CenterY=-4.3 CenterZ=0 NormalX=0 NormalY=0 NormalZ=1 AngleXU=0 Radius=1.5 StartAngle=2e-16 EndAngle=3.14159
    g8: ArcOfCircle CenterX=-10 CenterY=-33.9 CenterZ=0 NormalX=0 NormalY=0 NormalZ=1 AngleXU=0 Radius=1.5 StartAngle=3.14159 EndAngle=6.28319
    g9: ArcOfCircle CenterX=-16.1 CenterY=-36.4 CenterZ=0 NormalX=0 NormalY=0 NormalZ=1 AngleXU=0 Radius=1.5 StartAngle=3.14159 EndAngle=6.28319
    g10: ArcOfCircle CenterX=-22.1 CenterY=-36.4 CenterZ=0 NormalX=0 NormalY=0 NormalZ=1 AngleXU=0 Radius=1.5 StartAngle=3.14159 EndAngle=6.28319
    g11: ArcOfCircle CenterX=-28.2 CenterY=-33.9 CenterZ=0 NormalX=0 NormalY=0 NormalZ=1 AngleXU=0 Radius=1.5 StartAngle=3.14159 EndAngle=6.28319
    g12: LineSegment StartX=-35.7 StartY=-10.5 StartZ=0 EndX=-35.7 EndY=-27.7 EndZ=0
    g13: LineSegment StartX=-32.7 StartY=-10.5 StartZ=0 EndX=-32.7 EndY=-27.7 EndZ=0
    g14: LineSegment StartX=-29.7 StartY=-33.9 StartZ=0 EndX=-29.7 EndY=-4.3 EndZ=0
    g15: LineSegment StartX=-26.7 StartY=-33.9 StartZ=0 EndX=-26.7 EndY=-4.3 EndZ=0
    g16: LineSegment StartX=-2.5 StartY=-10.5 StartZ=0 EndX=-2.5 EndY=-27.7 EndZ=0
    g17: LineSegment StartX=-8.5 StartY=-4.3 StartZ=0 EndX=-8.5 EndY=-33.9 EndZ=0
    g18: LineSegment StartX=-5.5 StartY=-10.5 StartZ=0 EndX=-5.5 EndY=-27.7 EndZ=0
    g19: LineSegment StartX=-11.5 StartY=-4.3 StartZ=0 EndX=-11.5 EndY=-33.9 EndZ=0
    g20: LineSegment StartX=-14.6 StartY=-1.8 StartZ=0 EndX=-14.6 EndY=-36.4 EndZ=0
    g21: LineSegment StartX=-17.6 StartY=-1.8 StartZ=0 EndX=-17.6 EndY=-36.4 EndZ=0
    g22: LineSegment StartX=-20.6 StartY=-36.4 StartZ=0 EndX=-20.6 EndY=-1.8 EndZ=0
    g23: LineSegment StartX=-23.6 StartY=-1.8 StartZ=0 EndX=-23.6 EndY=-36.4 EndZ=0
  constraints (48):
    c: Block(g0)
    c: Block(g1)
    c: Block(g2)
    c: Block(g3)
    c: Block(g4)
    c: Block(g5)
    c: Block(g6)
    c: Block(g7)
    c: Block(g8)
    c: Block(g9)
    c: Block(g10)
    c: Block(g11)
    c: Coincident(g12,g1)
    c: Coincident(g12,g2)
    c: Vertical(g12)
    c: Coincident(g13,g1)
    c: Coincident(g13,g2)
    c: Vertical(g13)
    c: Coincident(g14,g11)
    c: Coincident(g14,g7)
    c: Vertical(g14)
    c: Coincident(g15,g11)
    c: Coincident(g15,g7)
    c: Vertical(g15)
    c: Coincident(g16,g0)
    c: Coincident(g16,g3)
    c: Vertical(g16)
    c: Coincident(g17,g4)
    c: Coincident(g17,g8)
    c: Vertical(g17)
    c: Coincident(g18,g0)
    c: Coincident(g18,g3)
    c: Vertical(g18)
    c: Coincident(g19,g4)
    c: Coincident(g19,g8)
    c: Vertical(g19)
    c: Coincident(g20,g5)
    c: Coincident(g20,g9)
    c: Vertical(g20)
    c: Coincident(g21,g5)
    c: Coincident(g21,g9)
    c: Vertical(g21)
    c: Coincident(g22,g10)
    c: Coincident(g22,g6)
    c: Vertical(g22)
    c: Coincident(g23,g6)
    c: Coincident(g23,g10)
    c: Vertical(g23)
FEATURE [Part::Extrusion] Extrude020  label="removeToCreateFanGrillHoles"
  Base = -> Sketch029
  Dir = (0,-1,6e-16)
  DirMode = 2
  FaceMakerClass = Part::FaceMakerBullseye
  LengthFwd = 10
  LengthRev = 0
  Placement = pos=(65.4,44,54.82) rot=(0,0,1;0rad)
  Solid = true
  Symmetric = false
FEATURE [Part::MultiFuse] Fusion055  label="top008"
  Shapes = -> [Cut017,Cut018]
FEATURE [Part::Cut] Cut019  label="top009"
  Base = -> Fusion055
  Tool = -> Extrude020
FEATURE [App::MeasureDistance] Distance003  label="Distance: 71.95 mm"
  Distance = 71.9513
  P1 = (117,38,72)
  P2 = (117,38,0.0487319)
FEATURE [Sketcher::SketchObject] Sketch030
  FullyConstrained = true
  Placement = pos=(117,19,0) rot=(0.57735,0.57735,0.57735;2.0944rad)
  sketch-geometry (48):
    g0: LineSegment StartX=-49.19 StartY=69.25 StartZ=0 EndX=-49.19 EndY=66.25 EndZ=0
    g1: LineSegment StartX=-49.19 StartY=63.5 StartZ=0 EndX=-49.19 EndY=60.5 EndZ=0
    g2: LineSegment StartX=-49.19 StartY=57.75 StartZ=0 EndX=-49.19 EndY=54.75 EndZ=0
    g3: LineSegment StartX=-49.19 StartY=52 StartZ=0 EndX=-49.19 EndY=49 EndZ=0
    g4: LineSegment StartX=-49.19 StartY=46.25 StartZ=0 EndX=-49.19 EndY=43.25 EndZ=0
    g5: LineSegment StartX=-49.19 StartY=40.5 StartZ=0 EndX=-49.19 EndY=37.5 EndZ=0
    g6: LineSegment StartX=-49.19 StartY=34.5 StartZ=0 EndX=-49.19 EndY=31.5 EndZ=0
    g7: LineSegment StartX=-49.19 StartY=28.75 StartZ=0 EndX=-49.19 EndY=25.75 EndZ=0
    g8: LineSegment StartX=-49.19 StartY=23 StartZ=0 EndX=-49.19 EndY=20 EndZ=0
    g9: LineSegment StartX=-49.19 StartY=17.25 StartZ=0 EndX=-49.19 EndY=14.25 EndZ=0
    g10: LineSegment StartX=-49.19 StartY=11.5 StartZ=0 EndX=-49.19 EndY=8.5 EndZ=0
    g11: LineSegment StartX=-49.19 StartY=5.75 StartZ=0 EndX=-49.19 EndY=2.75 EndZ=0
    g12: ArcOfCircle CenterX=-1.5 CenterY=67.75 CenterZ=0 NormalX=0 NormalY=0 NormalZ=1 AngleXU=0 Radius=1.5 StartAngle=4.71239 EndAngle=7.85398
    g13: ArcOfCircle CenterX=-1.5 CenterY=62 CenterZ=0 NormalX=0 NormalY=0 NormalZ=1 AngleXU=0 Radius=1.5 StartAngle=4.71239 EndAngle=7.85398
    g14: ArcOfCircle CenterX=-1.5 CenterY=56.25 CenterZ=0 NormalX=0 NormalY=0 NormalZ=1 AngleXU=0 Radius=1.5 StartAngle=4.71239 EndAngle=7.85398
    g15: ArcOfCircle CenterX=-11.49 CenterY=50.5 CenterZ=0 NormalX=0 NormalY=0 NormalZ=1 AngleXU=0 Radius=1.5 StartAngle=4.71239 EndAngle=7.85398
    g16: ArcOfCircle CenterX=-16.28 CenterY=44.75 CenterZ=0 NormalX=0 NormalY=0 NormalZ=1 AngleXU=0 Radius=1.5 StartAngle=4.71239 EndAngle=7.85398
    g17: ArcOfCircle CenterX=-18.2337 CenterY=39 CenterZ=0 NormalX=0 NormalY=0 NormalZ=1 AngleXU=0 Radius=1.5 StartAngle=4.71485 EndAngle=7.85398
    g18: ArcOfCircle CenterX=-16.2837 CenterY=27.25 CenterZ=0 NormalX=0 NormalY=0 NormalZ=1 AngleXU=0 Radius=1.5 StartAngle=4.71485 EndAngle=7.85398
    g19: ArcOfCircle CenterX=-18.2337 CenterY=33 CenterZ=0 NormalX=0 NormalY=0 NormalZ=1 AngleXU=0 Radius=1.5 StartAngle=4.71485 EndAngle=7.85398
    g20: ArcOfCircle CenterX=-11.49 CenterY=21.5 CenterZ=0 NormalX=0 NormalY=0 NormalZ=1 AngleXU=0 Radius=1.5 StartAngle=4.71239 EndAngle=7.85398
    g21: ArcOfCircle CenterX=-1.5 CenterY=4.25 CenterZ=0 NormalX=0 NormalY=0 NormalZ=1 AngleXU=0 Radius=1.5 StartAngle=4.71239 EndAngle=7.85398
    g22: ArcOfCircle CenterX=-1.5 CenterY=10 CenterZ=0 NormalX=0 NormalY=0 NormalZ=1 AngleXU=0 Radius=1.5 StartAngle=4.71239 EndAngle=7.85398
    g23: ArcOfCircle CenterX=-1.5 CenterY=15.75 CenterZ=0 NormalX=0 NormalY=0 NormalZ=1 AngleXU=0 Radius=1.5 StartAngle=4.71239 EndAngle=7.85398
    g24: LineSegment StartX=-49.19 StartY=69.25 StartZ=0 EndX=-1.5 EndY=69.25 EndZ=0
    g25: LineSegment StartX=-49.19 StartY=66.25 StartZ=0 EndX=-1.5 EndY=66.25 EndZ=0
    g26: LineSegment StartX=-49.19 StartY=63.5 StartZ=0 EndX=-1.5 EndY=63.5 EndZ=0
    g27: LineSegment StartX=-49.19 StartY=60.5 StartZ=0 EndX=-1.5 EndY=60.5 EndZ=0
    g28: LineSegment StartX=-49.19 StartY=57.75 StartZ=0 EndX=-1.5 EndY=57.75 EndZ=0
    g29: LineSegment StartX=-49.19 StartY=54.75 StartZ=0 EndX=-1.5 EndY=54.75 EndZ=0
    g30: LineSegment StartX=-49.19 StartY=52 StartZ=0 EndX=-11.49 EndY=52 EndZ=0
    g31: LineSegment StartX=-49.19 StartY=49 StartZ=0 EndX=-11.49 EndY=49 EndZ=0
    g32: LineSegment StartX=-49.19 StartY=46.25 StartZ=0 EndX=-16.28 EndY=46.25 EndZ=0
    g33: LineSegment StartX=-49.19 StartY=43.25 StartZ=0 EndX=-16.28 EndY=43.25 EndZ=0
    g34: LineSegment StartX=-49.19 StartY=40.5 StartZ=0 EndX=-18.2337 EndY=40.5 EndZ=0
    g35: LineSegment StartX=-49.19 StartY=37.5 StartZ=0 EndX=-18.23 EndY=37.5 EndZ=0
    g36: LineSegment StartX=-49.19 StartY=34.5 StartZ=0 EndX=-18.2337 EndY=34.5 EndZ=0
    g37: LineSegment StartX=-49.19 StartY=31.5 StartZ=0 EndX=-18.23 EndY=31.5 EndZ=0
    g38: LineSegment StartX=-49.19 StartY=28.75 StartZ=0 EndX=-16.2837 EndY=28.75 EndZ=0
    g39: LineSegment StartX=-49.19 StartY=25.75 StartZ=0 EndX=-16.28 EndY=25.75 EndZ=0
    g40: LineSegment StartX=-49.19 StartY=23 StartZ=0 EndX=-11.49 EndY=23 EndZ=0
    g41: LineSegment StartX=-49.19 StartY=20 StartZ=0 EndX=-11.49 EndY=20 EndZ=0
    g42: LineSegment StartX=-49.19 StartY=17.25 StartZ=0 EndX=-1.5 EndY=17.25 EndZ=0
    g43: LineSegment StartX=-49.19 StartY=14.25 StartZ=0 EndX=-1.5 EndY=14.25 EndZ=0
    g44: LineSegment StartX=-49.19 StartY=11.5 StartZ=0 EndX=-1.5 EndY=11.5 EndZ=0
    g45: LineSegment StartX=-49.19 StartY=8.5 StartZ=0 EndX=-1.5 EndY=8.5 EndZ=0
    g46: LineSegment StartX=-49.19 StartY=5.75 StartZ=0 EndX=-1.5 EndY=5.75 EndZ=0
    g47: LineSegment StartX=-49.19 StartY=2.75 StartZ=0 EndX=-1.5 EndY=2.75 EndZ=0
  constraints (120):
    c: Vertical(g0)
    c: Distance(g0) = 3
    c: Block(g0)
    c: Vertical(g1)
    c: Distance(g1) = 3
    c: Vertical(g2)
    c: Equal(g0,g2) = 3
    c: Block(g2)
    c: Vertical(g3)
    c: Equal(g1,g3) = 3
    c: Vertical(g4)
    c: Equal(g0,g4) = 3
    c: Block(g4)
    c: Vertical(g5)
    c: Equal(g1,g5) = 3
    c: Vertical(g6)
    c: Equal(g0,g6) = 3
    c: Block(g6)
    c: Vertical(g7)
    c: Equal(g1,g7) = 3
    c: Vertical(g8)
    c: Equal(g0,g8) = 3
    c: Block(g8)
    c: Vertical(g9)
    c: Equal(g1,g9) = 3
    c: Vertical(g10)
    c: Equal(g0,g10) = 3
    c: Block(g10)
    c: Vertical(g11)
    c: Equal(g1,g11) = 3
    c: Block(g12)
    c: Block(g13)
    c: Block(g14)
    c: Block(g15)
    c: Block(g16)
    c: Block(g17)
    c: Block(g18)
    c: Block(g19)
    c: Block(g20)
    c: Block(g21)
    c: Block(g22)
    c: Block(g23)
    c: Block(g11)
    c: Block(g9)
    c: Block(g7)
    c: Block(g5)
    c: Block(g3)
    c: Block(g1)
    c: Coincident(g24,g0)
    c: Coincident(g24,g12)
    c: Horizontal(g24)
    c: Coincident(g25,g0)
    c: Coincident(g25,g12)
    c: Horizontal(g25)
    c: Coincident(g26,g1)
    c: Coincident(g26,g13)
    c: Horizontal(g26)
    c: Coincident(g27,g1)
    c: Coincident(g27,g13)
    c: Horizontal(g27)
    c: Coincident(g28,g2)
    c: Coincident(g28,g14)
    c: Horizontal(g28)
    c: Coincident(g29,g2)
    c: Coincident(g29,g14)
    c: Horizontal(g29)
    c: Coincident(g30,g3)
    c: Coincident(g30,g15)
    c: Horizontal(g30)
    c: Coincident(g31,g3)
    c: Coincident(g31,g15)
    c: Horizontal(g31)
    c: Coincident(g32,g4)
    c: Coincident(g32,g16)
    c: Horizontal(g32)
    c: Coincident(g33,g4)
    c: Coincident(g33,g16)
    c: Horizontal(g33)
    c: Coincident(g34,g5)
    c: Coincident(g34,g17)
    c: Horizontal(g34)
    c: Coincident(g35,g5)
    c: Coincident(g35,g17)
    c: Horizontal(g35)
    c: Coincident(g36,g6)
    c: Coincident(g36,g19)
    c: Horizontal(g36)
    c: Coincident(g37,g6)
    c: Coincident(g37,g19)
    c: Horizontal(g37)
    c: Coincident(g38,g7)
    c: Coincident(g38,g18)
    c: Horizontal(g38)
    c: Coincident(g39,g7)
    c: Coincident(g39,g18)
    c: Horizontal(g39)
    c: Coincident(g40,g8)
    c: Coincident(g40,g20)
    c: Horizontal(g40)
    c: Coincident(g41,g8)
    c: Coincident(g41,g20)
    c: Horizontal(g41)
    c: Coincident(g42,g9)
    c: Coincident(g42,g23)
    c: Horizontal(g42)
    c: Coincident(g43,g9)
    c: Coincident(g43,g23)
    c: Horizontal(g43)
    c: Coincident(g44,g10)
    c: Coincident(g44,g22)
    c: Horizontal(g44)
    c: Coincident(g45,g10)
    c: Coincident(g45,g22)
    c: Horizontal(g45)
    c: Coincident(g46,g11)
    c: Coincident(g46,g21)
    c: Horizontal(g46)
    c: Coincident(g47,g11)
    c: Coincident(g47,g21)
    c: Horizontal(g47)
FEATURE [Sketcher::SketchObject] Sketch031
  FullyConstrained = true
  Placement = pos=(117,19,0) rot=(0.57735,0.57735,0.57735;2.0944rad)
  sketch-geometry (24):
    g0: ArcOfCircle CenterX=-49.19 CenterY=67.75 CenterZ=0 NormalX=0 NormalY=0 NormalZ=1 AngleXU=0 Radius=1.5 StartAngle=1.5708 EndAngle=4.71239
    g1: ArcOfCircle CenterX=-49.19 CenterY=62 CenterZ=0 NormalX=0 NormalY=0 NormalZ=1 AngleXU=0 Radius=1.5 StartAngle=1.5708 EndAngle=4.71239
    g2: ArcOfCircle CenterX=-49.19 CenterY=56.25 CenterZ=0 NormalX=0 NormalY=0 NormalZ=1 AngleXU=0 Radius=1.5 StartAngle=1.5708 EndAngle=4.71239
    g3: ArcOfCircle CenterX=-49.19 CenterY=50.5 CenterZ=0 NormalX=0 NormalY=0 NormalZ=1 AngleXU=0 Radius=1.5 StartAngle=1.5708 EndAngle=4.71239
    g4: ArcOfCircle CenterX=-49.19 CenterY=44.75 CenterZ=0 NormalX=0 NormalY=0 NormalZ=1 AngleXU=0 Radius=1.5 StartAngle=1.5708 EndAngle=4.71239
    g5: ArcOfCircle CenterX=-49.19 CenterY=39 CenterZ=0 NormalX=0 NormalY=0 NormalZ=1 AngleXU=0 Radius=1.5 StartAngle=1.5708 EndAngle=4.71239
    g6: ArcOfCircle CenterX=-49.19 CenterY=33 CenterZ=0 NormalX=0 NormalY=0 NormalZ=1 AngleXU=0 Radius=1.5 StartAngle=1.5708 EndAngle=4.71239
    g7: ArcOfCircle CenterX=-49.19 CenterY=27.25 CenterZ=0 NormalX=0 NormalY=0 NormalZ=1 AngleXU=0 Radius=1.5 StartAngle=1.5708 EndAngle=4.71239
    g8: ArcOfCircle CenterX=-49.19 CenterY=21.5 CenterZ=0 NormalX=0 NormalY=0 NormalZ=1 AngleXU=0 Radius=1.5 StartAngle=1.5708 EndAngle=4.71239
    g9: ArcOfCircle CenterX=-49.19 CenterY=15.75 CenterZ=0 NormalX=0 NormalY=0 NormalZ=1 AngleXU=0 Radius=1.5 StartAngle=1.5708 EndAngle=4.71239
    g10: ArcOfCircle CenterX=-49.19 CenterY=10 CenterZ=0 NormalX=0 NormalY=0 NormalZ=1 AngleXU=0 Radius=1.5 StartAngle=1.5708 EndAngle=4.71239
    g11: ArcOfCircle CenterX=-49.19 CenterY=4.25 CenterZ=0 NormalX=0 NormalY=0 NormalZ=1 AngleXU=0 Radius=1.5 StartAngle=1.5708 EndAngle=4.71239
    g12: LineSegment StartX=-49.19 StartY=69.25 StartZ=0 EndX=-49.19 EndY=66.25 EndZ=0
    g13: LineSegment StartX=-49.19 StartY=63.5 StartZ=0 EndX=-49.19 EndY=60.5 EndZ=0
    g14: LineSegment StartX=-49.19 StartY=57.75 StartZ=0 EndX=-49.19 EndY=54.75 EndZ=0
    g15: LineSegment StartX=-49.19 StartY=52 StartZ=0 EndX=-49.19 EndY=49 EndZ=0
    g16: LineSegment StartX=-49.19 StartY=46.25 StartZ=0 EndX=-49.19 EndY=43.25 EndZ=0
    g17: LineSegment StartX=-49.19 StartY=40.5 StartZ=0 EndX=-49.19 EndY=37.5 EndZ=0
    g18: LineSegment StartX=-49.19 StartY=34.5 StartZ=0 EndX=-49.19 EndY=31.5 EndZ=0
    g19: LineSegment StartX=-49.19 StartY=28.75 StartZ=0 EndX=-49.19 EndY=25.75 EndZ=0
    g20: LineSegment StartX=-49.19 StartY=23 StartZ=0 EndX=-49.19 EndY=20 EndZ=0
    g21: LineSegment StartX=-49.19 StartY=17.25 StartZ=0 EndX=-49.19 EndY=14.25 EndZ=0
    g22: LineSegment StartX=-49.19 StartY=11.5 StartZ=0 EndX=-49.19 EndY=8.5 EndZ=0
    g23: LineSegment StartX=-49.19 StartY=5.75 StartZ=0 EndX=-49.19 EndY=2.75 EndZ=0
  constraints (48):
    c: Block(g0)
    c: Block(g1)
    c: Block(g2)
    c: Block(g3)
    c: Block(g4)
    c: Block(g5)
    c: Block(g6)
    c: Block(g7)
    c: Block(g8)
    c: Block(g9)
    c: Block(g10)
    c: Block(g11)
    c: Coincident(g12,g0)
    c: Coincident(g12,g0)
    c: Vertical(g12)
    c: Vertical(g13)
    c: Coincident(g13,g1)
    c: Vertical(g14)
    c: Coincident(g14,g2)
    c: Vertical(g15)
    c: Coincident(g15,g3)
    c: Vertical(g16)
    c: Coincident(g16,g4)
    c: Vertical(g17)
    c: Coincident(g17,g5)
    c: Vertical(g18)
    c: Coincident(g18,g6)
    c: Vertical(g19)
    c: Coincident(g19,g7)
    c: Vertical(g20)
    c: Coincident(g20,g8)
    c: Vertical(g21)
    c: Coincident(g21,g9)
    c: Vertical(g22)
    c: Coincident(g22,g10)
    c: Vertical(g23)
    c: Coincident(g23,g11)
    c: Block(g23)
    c: Block(g22)
    c: Block(g21)
    c: Block(g20)
    c: Block(g13)
    c: Block(g14)
    c: Block(g15)
    c: Block(g16)
    c: Block(g17)
    c: Block(g18)
    c: Block(g19)
FEATURE [Part::Extrusion] Extrude022
  Base = -> Sketch030
  Dir = (1,-2e-16,2e-16)
  DirMode = 2
  FaceMakerClass = Part::FaceMakerBullseye
  LengthFwd = 19
  LengthRev = 0
  Placement = pos=(-19,0,0) rot=(0,0,1;0rad)
  Solid = true
  Symmetric = false
FEATURE [Part::Fillet] Fillet022
  Base = -> Extrude022
  Edges = 24 edges r=1.49: [Edge6,Edge11,Edge18,Edge23,Edge30,Edge35,Edge42,Edge47,Edge54,Edge59,Edge66,Edge71,Edge78,Edge83,Edge90,Edge95,Edge102,Edge107,Edge114,Edge119,Edge126,Edge131,Edge138,Edge143]
FEATURE [Part::Cut] Cut020  label="top010"
  Base = -> Cut019
  Tool = -> Fillet022
FEATURE [Sketcher::SketchObject] Sketch032
  FullyConstrained = true
  Placement = pos=(117,19,0) rot=(0.57735,0.57735,0.57735;2.0944rad)
  sketch-geometry (48):
    g0: LineSegment StartX=-49.19 StartY=69.25 StartZ=0 EndX=-49.19 EndY=66.25 EndZ=0
    g1: LineSegment StartX=-49.19 StartY=63.5 StartZ=0 EndX=-49.19 EndY=60.5 EndZ=0
    g2: LineSegment StartX=-49.19 StartY=57.75 StartZ=0 EndX=-49.19 EndY=54.75 EndZ=0
    g3: LineSegment StartX=-49.19 StartY=52 StartZ=0 EndX=-49.19 EndY=49 EndZ=0
    g4: LineSegment StartX=-49.19 StartY=46.25 StartZ=0 EndX=-49.19 EndY=43.25 EndZ=0
    g5: LineSegment StartX=-49.19 StartY=40.5 StartZ=0 EndX=-49.19 EndY=37.5 EndZ=0
    g6: LineSegment StartX=-49.19 StartY=34.5 StartZ=0 EndX=-49.19 EndY=31.5 EndZ=0
    g7: LineSegment StartX=-49.19 StartY=28.75 StartZ=0 EndX=-49.19 EndY=25.75 EndZ=0
    g8: LineSegment StartX=-49.19 StartY=23 StartZ=0 EndX=-49.19 EndY=20 EndZ=0
    g9: LineSegment StartX=-49.19 StartY=17.25 StartZ=0 EndX=-49.19 EndY=14.25 EndZ=0
    g10: LineSegment StartX=-49.19 StartY=11.5 StartZ=0 EndX=-49.19 EndY=8.5 EndZ=0
    g11: LineSegment StartX=-49.19 StartY=5.75 StartZ=0 EndX=-49.19 EndY=2.75 EndZ=0
    g12: ArcOfCircle CenterX=-1.5 CenterY=67.75 CenterZ=0 NormalX=0 NormalY=0 NormalZ=1 AngleXU=0 Radius=1.5 StartAngle=4.71239 EndAngle=7.85398
    g13: ArcOfCircle CenterX=-1.5 CenterY=62 CenterZ=0 NormalX=0 NormalY=0 NormalZ=1 AngleXU=0 Radius=1.5 StartAngle=4.71239 EndAngle=7.85398
    g14: ArcOfCircle CenterX=-1.5 CenterY=56.25 CenterZ=0 NormalX=0 NormalY=0 NormalZ=1 AngleXU=0 Radius=1.5 StartAngle=4.71239 EndAngle=7.85398
    g15: ArcOfCircle CenterX=-11.49 CenterY=50.5 CenterZ=0 NormalX=0 NormalY=0 NormalZ=1 AngleXU=0 Radius=1.5 StartAngle=4.71239 EndAngle=7.85398
    g16: ArcOfCircle CenterX=-16.28 CenterY=44.75 CenterZ=0 NormalX=0 NormalY=0 NormalZ=1 AngleXU=0 Radius=1.5 StartAngle=4.71239 EndAngle=7.85398
    g17: ArcOfCircle CenterX=-18.2337 CenterY=39 CenterZ=0 NormalX=0 NormalY=0 NormalZ=1 AngleXU=0 Radius=1.5 StartAngle=4.71485 EndAngle=7.85398
    g18: ArcOfCircle CenterX=-16.2837 CenterY=27.25 CenterZ=0 NormalX=0 NormalY=0 NormalZ=1 AngleXU=0 Radius=1.5 StartAngle=4.71485 EndAngle=7.85398
    g19: ArcOfCircle CenterX=-18.2337 CenterY=33 CenterZ=0 NormalX=0 NormalY=0 NormalZ=1 AngleXU=0 Radius=1.5 StartAngle=4.71485 EndAngle=7.85398
    g20: ArcOfCircle CenterX=-11.49 CenterY=21.5 CenterZ=0 NormalX=0 NormalY=0 NormalZ=1 AngleXU=0 Radius=1.5 StartAngle=4.71239 EndAngle=7.85398
    g21: ArcOfCircle CenterX=-1.5 CenterY=4.25 CenterZ=0 NormalX=0 NormalY=0 NormalZ=1 AngleXU=0 Radius=1.5 StartAngle=4.71239 EndAngle=7.85398
    g22: ArcOfCircle CenterX=-1.5 CenterY=10 CenterZ=0 NormalX=0 NormalY=0 NormalZ=1 AngleXU=0 Radius=1.5 StartAngle=4.71239 EndAngle=7.85398
    g23: ArcOfCircle CenterX=-1.5 CenterY=15.75 CenterZ=0 NormalX=0 NormalY=0 NormalZ=1 AngleXU=0 Radius=1.5 StartAngle=4.71239 EndAngle=7.85398
    g24: LineSegment StartX=-49.19 StartY=69.25 StartZ=0 EndX=-1.5 EndY=69.25 EndZ=0
    g25: LineSegment StartX=-49.19 StartY=66.25 StartZ=0 EndX=-1.5 EndY=66.25 EndZ=0
    g26: LineSegment StartX=-49.19 StartY=63.5 StartZ=0 EndX=-1.5 EndY=63.5 EndZ=0
    g27: LineSegment StartX=-49.19 StartY=60.5 StartZ=0 EndX=-1.5 EndY=60.5 EndZ=0
    g28: LineSegment StartX=-49.19 StartY=57.75 StartZ=0 EndX=-1.5 EndY=57.75 EndZ=0
    g29: LineSegment StartX=-49.19 StartY=54.75 StartZ=0 EndX=-1.5 EndY=54.75 EndZ=0
    g30: LineSegment StartX=-49.19 StartY=52 StartZ=0 EndX=-11.49 EndY=52 EndZ=0
    g31: LineSegment StartX=-49.19 StartY=49 StartZ=0 EndX=-11.49 EndY=49 EndZ=0
    g32: LineSegment StartX=-49.19 StartY=46.25 StartZ=0 EndX=-16.28 EndY=46.25 EndZ=0
    g33: LineSegment StartX=-49.19 StartY=43.25 StartZ=0 EndX=-16.28 EndY=43.25 EndZ=0
    g34: LineSegment StartX=-49.19 StartY=40.5 StartZ=0 EndX=-18.2337 EndY=40.5 EndZ=0
    g35: LineSegment StartX=-49.19 StartY=37.5 StartZ=0 EndX=-18.23 EndY=37.5 EndZ=0
    g36: LineSegment StartX=-49.19 StartY=34.5 StartZ=0 EndX=-18.2337 EndY=34.5 EndZ=0
    g37: LineSegment StartX=-49.19 StartY=31.5 StartZ=0 EndX=-18.23 EndY=31.5 EndZ=0
    g38: LineSegment StartX=-49.19 StartY=28.75 StartZ=0 EndX=-16.2837 EndY=28.75 EndZ=0
    g39: LineSegment StartX=-49.19 StartY=25.75 StartZ=0 EndX=-16.28 EndY=25.75 EndZ=0
    g40: LineSegment StartX=-49.19 StartY=23 StartZ=0 EndX=-11.49 EndY=23 EndZ=0
    g41: LineSegment StartX=-49.19 StartY=20 StartZ=0 EndX=-11.49 EndY=20 EndZ=0
    g42: LineSegment StartX=-49.19 StartY=17.25 StartZ=0 EndX=-1.5 EndY=17.25 EndZ=0
    g43: LineSegment StartX=-49.19 StartY=14.25 StartZ=0 EndX=-1.5 EndY=14.25 EndZ=0
    g44: LineSegment StartX=-49.19 StartY=11.5 StartZ=0 EndX=-1.5 EndY=11.5 EndZ=0
    g45: LineSegment StartX=-49.19 StartY=8.5 StartZ=0 EndX=-1.5 EndY=8.5 EndZ=0
    g46: LineSegment StartX=-49.19 StartY=5.75 StartZ=0 EndX=-1.5 EndY=5.75 EndZ=0
    g47: LineSegment StartX=-49.19 StartY=2.75 StartZ=0 EndX=-1.5 EndY=2.75 EndZ=0
  constraints (120):
    c: Vertical(g0)
    c: Distance(g0) = 3
    c: Block(g0)
    c: Vertical(g1)
    c: Distance(g1) = 3
    c: Vertical(g2)
    c: Equal(g0,g2) = 3
    c: Block(g2)
    c: Vertical(g3)
    c: Equal(g1,g3) = 3
    c: Vertical(g4)
    c: Equal(g0,g4) = 3
    c: Block(g4)
    c: Vertical(g5)
    c: Equal(g1,g5) = 3
    c: Vertical(g6)
    c: Equal(g0,g6) = 3
    c: Block(g6)
    c: Vertical(g7)
    c: Equal(g1,g7) = 3
    c: Vertical(g8)
    c: Equal(g0,g8) = 3
    c: Block(g8)
    c: Vertical(g9)
    c: Equal(g1,g9) = 3
    c: Vertical(g10)
    c: Equal(g0,g10) = 3
    c: Block(g10)
    c: Vertical(g11)
    c: Equal(g1,g11) = 3
    c: Block(g12)
    c: Block(g13)
    c: Block(g14)
    c: Block(g15)
    c: Block(g16)
    c: Block(g17)
    c: Block(g18)
    c: Block(g19)
    c: Block(g20)
    c: Block(g21)
    c: Block(g22)
    c: Block(g23)
    c: Block(g11)
    c: Block(g9)
    c: Block(g7)
    c: Block(g5)
    c: Block(g3)
    c: Block(g1)
    c: Coincident(g24,g0)
    c: Coincident(g24,g12)
    c: Horizontal(g24)
    c: Coincident(g25,g0)
    c: Coincident(g25,g12)
    c: Horizontal(g25)
    c: Coincident(g26,g1)
    c: Coincident(g26,g13)
    c: Horizontal(g26)
    c: Coincident(g27,g1)
    c: Coincident(g27,g13)
    c: Horizontal(g27)
    c: Coincident(g28,g2)
    c: Coincident(g28,g14)
    c: Horizontal(g28)
    c: Coincident(g29,g2)
    c: Coincident(g29,g14)
    c: Horizontal(g29)
    c: Coincident(g30,g3)
    c: Coincident(g30,g15)
    c: Horizontal(g30)
    c: Coincident(g31,g3)
    c: Coincident(g31,g15)
    c: Horizontal(g31)
    c: Coincident(g32,g4)
    c: Coincident(g32,g16)
    c: Horizontal(g32)
    c: Coincident(g33,g4)
    c: Coincident(g33,g16)
    c: Horizontal(g33)
    c: Coincident(g34,g5)
    c: Coincident(g34,g17)
    c: Horizontal(g34)
    c: Coincident(g35,g5)
    c: Coincident(g35,g17)
    c: Horizontal(g35)
    c: Coincident(g36,g6)
    c: Coincident(g36,g19)
    c: Horizontal(g36)
    c: Coincident(g37,g6)
    c: Coincident(g37,g19)
    c: Horizontal(g37)
    c: Coincident(g38,g7)
    c: Coincident(g38,g18)
    c: Horizontal(g38)
    c: Coincident(g39,g7)
    c: Coincident(g39,g18)
    c: Horizontal(g39)
    c: Coincident(g40,g8)
    c: Coincident(g40,g20)
    c: Horizontal(g40)
    c: Coincident(g41,g8)
    c: Coincident(g41,g20)
    c: Horizontal(g41)
    c: Coincident(g42,g9)
    c: Coincident(g42,g23)
    c: Horizontal(g42)
    c: Coincident(g43,g9)
    c: Coincident(g43,g23)
    c: Horizontal(g43)
    c: Coincident(g44,g10)
    c: Coincident(g44,g22)
    c: Horizontal(g44)
    c: Coincident(g45,g10)
    c: Coincident(g45,g22)
    c: Horizontal(g45)
    c: Coincident(g46,g11)
    c: Coincident(g46,g21)
    c: Horizontal(g46)
    c: Coincident(g47,g11)
    c: Coincident(g47,g21)
    c: Horizontal(g47)
FEATURE [Part::Extrusion] Extrude023
  Base = -> Sketch032
  Dir = (1,-2e-16,2e-16)
  DirMode = 2
  FaceMakerClass = Part::FaceMakerBullseye
  LengthFwd = 19
  LengthRev = 0
  Placement = pos=(-19,0,0) rot=(0,0,1;0rad)
  Solid = true
  Symmetric = false
FEATURE [Part::Fillet] Fillet023
  Base = -> Extrude023
  Edges = <same value as first occurrence — deduplicated (x6 in doc)>
  Placement = pos=(0,0.05,0) rot=(0,0,1;0rad)
FEATURE [Part::Cut] Cut014  label="bottom003"
  Base = -> Cut007
  Tool = -> Fusion047
FEATURE [Part::Cut] Cut021  label="bottom004"
  Base = -> Cut014
  Tool = -> Fillet023
FEATURE [Sketcher::SketchObject] Sketch033
  FullyConstrained = true
  Placement = pos=(117,19,0) rot=(0.57735,0.57735,0.57735;2.0944rad)
  sketch-geometry (8):
    g0: LineSegment StartX=-49.19 StartY=69.25 StartZ=0 EndX=-49.19 EndY=66.25 EndZ=0
    g1: LineSegment StartX=-49.19 StartY=5.75 StartZ=0 EndX=-49.19 EndY=2.75 EndZ=0
    g2: ArcOfCircle CenterX=-1.5 CenterY=67.75 CenterZ=0 NormalX=0 NormalY=0 NormalZ=1 AngleXU=0 Radius=1.5 StartAngle=4.71239 EndAngle=7.85398
    g3: ArcOfCircle CenterX=-1.5 CenterY=4.25 CenterZ=0 NormalX=0 NormalY=0 NormalZ=1 AngleXU=0 Radius=1.5 StartAngle=4.71239 EndAngle=7.85398
    g4: LineSegment StartX=-49.19 StartY=69.25 StartZ=0 EndX=-1.5 EndY=69.25 EndZ=0
    g5: LineSegment StartX=-49.19 StartY=66.25 StartZ=0 EndX=-1.5 EndY=66.25 EndZ=0
    g6: LineSegment StartX=-49.19 StartY=5.75 StartZ=0 EndX=-1.5 EndY=5.75 EndZ=0
    g7: LineSegment StartX=-49.19 StartY=2.75 StartZ=0 EndX=-1.5 EndY=2.75 EndZ=0
  constraints (19):
    c: Vertical(g0)
    c: Distance(g0) = 3
    c: Block(g0)
    c: Vertical(g1)
    c: Block(g2)
    c: Block(g3)
    c: Block(g1)
    c: Coincident(g4,g0)
    c: Coincident(g4,g2)
    c: Horizontal(g4)
    c: Coincident(g5,g0)
    c: Coincident(g5,g2)
    c: Horizontal(g5)
    c: Coincident(g6,g1)
    c: Coincident(g6,g3)
    c: Horizontal(g6)
    c: Coincident(g7,g1)
    c: Coincident(g7,g3)
    c: Horizontal(g7)
FEATURE [Sketcher::SketchObject] Sketch034
  FullyConstrained = true
  Placement = pos=(117,19,0) rot=(0.57735,0.57735,0.57735;2.0944rad)
  sketch-geometry (8):
    g0: LineSegment StartX=-49.19 StartY=63.5 StartZ=0 EndX=-49.19 EndY=60.5 EndZ=0
    g1: LineSegment StartX=-49.19 StartY=11.5 StartZ=0 EndX=-49.19 EndY=8.5 EndZ=0
    g2: ArcOfCircle CenterX=-1.5 CenterY=62 CenterZ=0 NormalX=0 NormalY=0 NormalZ=1 AngleXU=0 Radius=1.5 StartAngle=4.71239 EndAngle=7.85398
    g3: ArcOfCircle CenterX=-1.5 CenterY=10 CenterZ=0 NormalX=0 NormalY=0 NormalZ=1 AngleXU=0 Radius=1.5 StartAngle=4.71239 EndAngle=7.85398
    g4: LineSegment StartX=-49.19 StartY=63.5 StartZ=0 EndX=-1.5 EndY=63.5 EndZ=0
    g5: LineSegment StartX=-49.19 StartY=60.5 StartZ=0 EndX=-1.5 EndY=60.5 EndZ=0
    g6: LineSegment StartX=-49.19 StartY=11.5 StartZ=0 EndX=-1.5 EndY=11.5 EndZ=0
    g7: LineSegment StartX=-49.19 StartY=8.5 StartZ=0 EndX=-1.5 EndY=8.5 EndZ=0
  constraints (19):
    c: Vertical(g0)
    c: Distance(g0) = 3
    c: Vertical(g1)
    c: Block(g1)
    c: Block(g2)
    c: Block(g3)
    c: Block(g0)
    c: Coincident(g4,g0)
    c: Coincident(g4,g2)
    c: Horizontal(g4)
    c: Coincident(g5,g0)
    c: Coincident(g5,g2)
    c: Horizontal(g5)
    c: Coincident(g6,g1)
    c: Coincident(g6,g3)
    c: Horizontal(g6)
    c: Coincident(g7,g1)
    c: Coincident(g7,g3)
    c: Horizontal(g7)
FEATURE [Part::Extrusion] Extrude024
  Base = -> Sketch033
  Dir = (1,0,0)
  DirMode = 2
  FaceMakerClass = Part::FaceMakerBullseye
  LengthFwd = 10
  LengthRev = 0
  Solid = true
  Symmetric = false
FEATURE [Part::Extrusion] Extrude025
  Base = -> Sketch034
  Dir = (1,0,0)
  DirMode = 2
  FaceMakerClass = Part::FaceMakerBullseye
  LengthFwd = 10
  LengthRev = 0
  Solid = true
  Symmetric = false
FEATURE [Part::Fillet] Fillet024  label="removeFromtMoreFrontCaseScrewRetainers"
  Base = -> Extrude024
  Edges = 4 edges r=1.49: [Edge6,Edge11,Edge18,Edge23]
  Placement = pos=(-11,0,0) rot=(0,0,1;0rad)
FEATURE [Part::Fillet] Fillet025  label="removeFromtMoreFrontCaseScrewRetainers001"
  Base = -> Extrude025
  Edges = 4 edges r=1.49: [Edge6,Edge11,Edge18,Edge23]
  Placement = pos=(-19,0,0) rot=(0,0,1;0rad)
FEATURE [Part::Cut] Cut022
  Base = -> Cut015
  Tool = -> Fillet025
FEATURE [Part::Cut] Cut023  label="screwRetainers"
  Base = -> Cut022
  Tool = -> Fillet024
FEATURE [Part::MultiFuse] Fusion056  label="bottom005"
  Shapes = -> [Fusion044,Cut021]
FEATURE [Part::MultiFuse] Fusion057  label="casePillars001"
  Shapes = -> [Cut016,Fusion052]
FEATURE [Part::MultiFuse] Fusion058  label="bottom006"
  Shapes = -> [Fusion056,Cut023]
FEATURE [Part::MultiFuse] Fusion059  label="bottom007"
  Shapes = -> [Fusion058,Fillet005]
FEATURE [Part::MultiFuse] Fusion060  label="bottom008"
  Shapes = -> [Fusion059,Fusion]
FEATURE [Part::MultiFuse] Fusion061  label="top011"
  Shapes = -> [Cut006,Cut020]
FEATURE [Part::MultiFuse] Fusion062  label="top012"
  Shapes = -> [Fusion057,Fusion061]
FEATURE [Sketcher::SketchObject] Sketch035  label="topSketch007"
  FullyConstrained = true
  sketch-geometry (6):
    g0: LineSegment StartX=19 StartY=38 StartZ=0 EndX=117 EndY=38 EndZ=0
    g1: ArcOfCircle CenterX=19 CenterY=19 CenterZ=0 NormalX=0 NormalY=0 NormalZ=1 AngleXU=0 Radius=19 StartAngle=1.5708 EndAngle=3.14159
    g2: LineSegment StartX=117 StartY=38 StartZ=0 EndX=117 EndY=19 EndZ=0
    g3: LineSegment StartX=98 StartY=1.0161e-12 StartZ=0 EndX=5.22862e-06 EndY=1.0161e-12 EndZ=0
    g4: LineSegment StartX=5.22862e-06 StartY=19 StartZ=0 EndX=5.22862e-06 EndY=1.0161e-12 EndZ=0
    g5: ArcOfCircle CenterX=98 CenterY=19 CenterZ=0 NormalX=0 NormalY=0 NormalZ=1 AngleXU=0 Radius=19 StartAngle=4.71239 EndAngle=6.28319
  constraints (16):
    c: Horizontal(g0)
    c: Distance(g0) = 98
    c: Coincident(g1,g0)
    c: Block(g1)
    c: Coincident(g2,g0)
    c: Vertical(g2)
    c: Distance(g2) = 19
    c: Horizontal(g3)
    c: Coincident(g4,g1)
    c: Vertical(g4)
    c: Coincident(g3,g4)
    c: Block(g3)
    c: Coincident(g5,g2)
    c: Coincident(g5,g3)
    c: Block(g0)
    c: Block(g5)
FEATURE [Part::Extrusion] Extrude026  label="sideA001"
  Base = -> Sketch035
  Dir = (0,0,1)
  DirMode = 2
  FaceMakerClass = Part::FaceMakerBullseye
  LengthFwd = 3
  LengthRev = 0
  Placement = pos=(0,0,-2.7) rot=(0,0,1;0rad)
  Solid = true
  Symmetric = false
FEATURE [Sketcher::SketchObject] Sketch036  label="topSketch008"
  FullyConstrained = true
  sketch-geometry (6):
    g0: LineSegment StartX=19 StartY=38 StartZ=0 EndX=117 EndY=38 EndZ=0
    g1: ArcOfCircle CenterX=19 CenterY=19 CenterZ=0 NormalX=0 NormalY=0 NormalZ=1 AngleXU=0 Radius=19 StartAngle=1.5708 EndAngle=3.14159
    g2: LineSegment StartX=117 StartY=38 StartZ=0 EndX=117 EndY=19 EndZ=0
    g3: LineSegment StartX=98 StartY=1.0161e-12 StartZ=0 EndX=5.22862e-06 EndY=1.0161e-12 EndZ=0
    g4: LineSegment StartX=5.22862e-06 StartY=19 StartZ=0 EndX=5.22862e-06 EndY=1.0161e-12 EndZ=0
    g5: ArcOfCircle CenterX=98 CenterY=19 CenterZ=0 NormalX=0 NormalY=0 NormalZ=1 AngleXU=0 Radius=19 StartAngle=4.71239 EndAngle=6.28319
  constraints (16):
    c: Horizontal(g0)
    c: Distance(g0) = 98
    c: Coincident(g1,g0)
    c: Block(g1)
    c: Coincident(g2,g0)
    c: Vertical(g2)
    c: Distance(g2) = 19
    c: Horizontal(g3)
    c: Coincident(g4,g1)
    c: Vertical(g4)
    c: Coincident(g3,g4)
    c: Block(g3)
    c: Coincident(g5,g2)
    c: Coincident(g5,g3)
    c: Block(g0)
    c: Block(g5)
FEATURE [Part::Extrusion] Extrude027  label="sideB001"
  Base = -> Sketch036
  Dir = (0,0,1)
  DirMode = 2
  FaceMakerClass = Part::FaceMakerBullseye
  LengthFwd = 3
  LengthRev = 0
  Placement = pos=(0,0,71.7) rot=(0,0,1;0rad)
  Solid = true
  Symmetric = false
FEATURE [Part::MultiFuse] Fusion064  label="removeFromBottom"
  Shapes = -> [Extrude026,Extrude027]
FEATURE [Part::Cut] Cut024  label="bottom009"
  Base = -> Fusion060
  Tool = -> Fusion064
FEATURE [Sketcher::SketchObject] Sketch037  label="topSketch009"
  FullyConstrained = true
  sketch-geometry (8):
    g0: ArcOfCircle CenterX=19 CenterY=19.1201 CenterZ=0 NormalX=0 NormalY=0 NormalZ=1 AngleXU=0 Radius=18.8799 StartAngle=1.5708 EndAngle=3.14793
    g1: LineSegment StartX=0.120501 StartY=19.0004 StartZ=0 EndX=0.120501 EndY=0.000382114 EndZ=0
    g2: LineSegment StartX=19 StartY=38 StartZ=0 EndX=124 EndY=38 EndZ=0
    g3: LineSegment StartX=0.120501 StartY=0.000382114 StartZ=0 EndX=105.121 EndY=0.000382114 EndZ=0
    g4: LineSegment StartX=124 StartY=38 StartZ=0 EndX=125.616 EndY=38 EndZ=0
    g5: LineSegment StartX=105.121 StartY=0.000382114 StartZ=0 EndX=106.736 EndY=0.000382114 EndZ=0
    g6: ArcOfCircle CenterX=106.616 CenterY=19 CenterZ=0 NormalX=0 NormalY=0 NormalZ=1 AngleXU=0 Radius=19 StartAngle=4.71873 EndAngle=6.28319
    g7: LineSegment StartX=125.616 StartY=38 StartZ=0 EndX=125.616 EndY=19 EndZ=0
  constraints (21):
    c: Block(g0)
    c: Coincident(g1,g0)
    c: Vertical(g1)
    c: Horizontal(g2)
    c: Distance(g2) = 105
    c: Coincident(g2,g0)
    c: Distance(g1) = 19
    c: Coincident(g3,g1)
    c: Horizontal(g3)
    c: Distance(g3) = 105
    c: Coincident(g4,g2)
    c: Horizontal(g4)
    c: Distance(g4) = 1.61553
    c: Horizontal(g5)
    c: Equal(g4,g5) = 1.61553
    c: Coincident(g5,g3)
    c: Block(g6)
    c: Coincident(g6,g5)
    c: Coincident(g7,g4)
    c: Coincident(g7,g6)
    c: Vertical(g7)
FEATURE [Part::Extrusion] Extrude028  label="sideB"
  Base = -> Sketch037
  Dir = (0,0,1)
  DirMode = 2
  FaceMakerClass = Part::FaceMakerBullseye
  LengthFwd = 3
  LengthRev = 0
  Placement = pos=(0,0,72) rot=(0,0,1;0rad)
  Solid = true
  Symmetric = false
FEATURE [Sketcher::SketchObject] Sketch038  label="topSketch010"
  FullyConstrained = true
  sketch-geometry (22):
    g0: LineSegment StartX=5.21097e-06 StartY=3 StartZ=0 EndX=5.21097e-06 EndY=19 EndZ=0
    g1: ArcOfCircle CenterX=19 CenterY=19 CenterZ=0 NormalX=0 NormalY=0 NormalZ=1 AngleXU=0 Radius=19 StartAngle=1.5708 EndAngle=3.14159
    g2: ArcOfCircle CenterX=19 CenterY=19 CenterZ=0 NormalX=0 NormalY=0 NormalZ=1 AngleXU=0 Radius=16 StartAngle=1.5708 EndAngle=3.14159
    g3: LineSegment StartX=114 StartY=35 StartZ=0 EndX=19 EndY=35 EndZ=0
    g4: LineSegment StartX=5.21097e-06 StartY=3 StartZ=0 EndX=5.21097e-06 EndY=0 EndZ=0
    g5: LineSegment StartX=3 StartY=0 StartZ=0 EndX=5.21097e-06 EndY=0 EndZ=0
    g6: LineSegment StartX=3 StartY=19 StartZ=0 EndX=3 EndY=0 EndZ=0
    g7: LineSegment StartX=19 StartY=38 StartZ=0 EndX=124 EndY=38 EndZ=0
    g8: Circle CenterX=119 CenterY=35 CenterZ=0 NormalX=0 NormalY=0 NormalZ=1 AngleXU=0 Radius=1
    g9: Circle CenterX=121 CenterY=35 CenterZ=0 NormalX=0 NormalY=0 NormalZ=1 AngleXU=0 Radius=1
    g10: Circle CenterX=121 CenterY=33 CenterZ=0 NormalX=0 NormalY=0 NormalZ=1 AngleXU=0 Radius=1
    g11: BSplineCurve PolesCount=3 KnotsCount=2 Degree=2 IsPeriodic=0
    g12: GeomPoint X=119 Y=35 Z=0
    g13: GeomPoint X=121 Y=33 Z=0
    g14: LineSegment StartX=119 StartY=35 StartZ=0 EndX=114 EndY=35 EndZ=0
    g15: ArcOfCircle CenterX=105 CenterY=19 CenterZ=0 NormalX=0 NormalY=0 NormalZ=1 AngleXU=0 Radius=16 StartAngle=5.60905 EndAngle=6.28319
    g16: LineSegment StartX=121 StartY=33 StartZ=0 EndX=121 EndY=19 EndZ=0
    g17: LineSegment StartX=117.5 StartY=9.01251 StartZ=0 EndX=121.163 EndY=9.0125 EndZ=0
    g18: ArcOfCircle CenterX=105 CenterY=19 CenterZ=0 NormalX=0 NormalY=0 NormalZ=1 AngleXU=0 Radius=20.6155 StartAngle=5.7297 EndAngle=6.28319
    g19: LineSegment StartX=121.163 StartY=9.0125 StartZ=0 EndX=122.538 EndY=8.16329 EndZ=0
    g20: LineSegment StartX=124 StartY=38 StartZ=0 EndX=125.616 EndY=38 EndZ=0
    g21: LineSegment StartX=125.616 StartY=19 StartZ=0 EndX=125.616 EndY=38 EndZ=0
  constraints (49):
    c: Vertical(g0)
    c: Block(g0)
    c: Coincident(g1,g0)
    c: Block(g1)
    c: Coincident(g2,g1)
    c: Block(g2)
    c: Coincident(g3,g2)
    c: Horizontal(g3)
    c: Tangent(g3,g2)
    c: Coincident(g4,g0)
    c: Distance(g4) = 3
    c: Vertical(g4)
    c: Coincident(g5,g4)
    c: Horizontal(g5)
    c: Coincident(g6,g2)
    c: Coincident(g6,g5)
    c: Vertical(g6)
    c: Horizontal(g7)
    c: Distance(g7) = 105
    c: Coincident(g7,g1)
    c: Block(g3)
    c: Weight(g8) = 1
    c: Equal(g8,g9)
    c: Equal(g8,g10)
    c: InternalAlignment(g8,g11)
    c: InternalAlignment(g9,g11)
    c: InternalAlignment(g10,g11)
    c: InternalAlignment(g12,g11)
    c: InternalAlignment(g13,g11)
    c: Block(g11)
    c: Coincident(g14,g11)
    c: Coincident(g14,g3)
    c: Horizontal(g14)
    c: Block(g15)
    c: Coincident(g16,g11)
    c: Coincident(g16,g15)
    c: Vertical(g16)
    c: Distance(g16) = 14
    c: Coincident(g17,g15)
    c: Block(g18)
    c: Coincident(g19,g18)
    c: Coincident(g20,g7)
    c: Horizontal(g20)
    c: Vertical(g21)
    c: Coincident(g20,g21)
    c: Block(g20)
    c: Block(g21)
    c: Block(g19)
    c: Block(g17)
FEATURE [Part::Extrusion] Extrude029
  Base = -> Sketch038
  Dir = (0,0,1)
  DirMode = 2
  FaceMakerClass = Part::FaceMakerBullseye
  LengthFwd = 72
  LengthRev = 0
  Solid = true
  Symmetric = false
FEATURE [Part::Feature] Face085
  shape: bbox 4.8 x 25.5 x 2e-07 mm, 1 faces, 0 solids (baked)
FEATURE [Part::Revolution] Revolve089  label="moreFrontCaseScrewPost003"
  Angle = 360
  Axis = (0,1,0)
  Base = (0,0,0)
  FaceMakerClass = Part::FaceMakerBullseye
  Placement = pos=(109.5,4.5,3.5) rot=(0,0,1;0rad)
  Solid = false
  Source = -> Face085
  Symmetric = false
FEATURE [Part::Feature] Face086
  shape: bbox 4.8 x 25.5 x 2e-07 mm, 1 faces, 0 solids (baked)
FEATURE [Part::Revolution] Revolve090  label="moreFrontCaseScrewPost004"
  Angle = 360
  Axis = (0,1,0)
  Base = (0,0,0)
  FaceMakerClass = Part::FaceMakerBullseye
  Placement = pos=(109.5,4.5,68.5) rot=(0,0,1;0rad)
  Solid = false
  Source = -> Face086
  Symmetric = false
FEATURE [Part::Fillet] Fillet026  label="top013"
  Base = -> Extrude029
  Edges = 1 edges r=2: [Edge35]
FEATURE [Sketcher::SketchObject] Sketch039
  FullyConstrained = true
  sketch-geometry (7):
    g0: LineSegment StartX=0 StartY=0 StartZ=0 EndX=0 EndY=6 EndZ=0
    g1: Circle CenterX=0 CenterY=0 CenterZ=0 NormalX=0 NormalY=0 NormalZ=1 AngleXU=0 Radius=1
    g2: Circle CenterX=8 CenterY=6 CenterZ=0 NormalX=0 NormalY=0 NormalZ=1 AngleXU=0 Radius=1
    g3: BSplineCurve PolesCount=3 KnotsCount=2 Degree=2 IsPeriodic=0
    g4: GeomPoint X=0 Y=0 Z=0
    g5: GeomPoint X=8 Y=6 Z=0
    g6: LineSegment StartX=0 StartY=6 StartZ=0 EndX=8 EndY=6 EndZ=0
  constraints (14):
    c: Coincident(g0,g-1)
    c: Distance(g0) = 6
    c: Vertical(g0)
    c: Coincident(g3,g0)
    c: Weight(g1) = 1
    c: Equal(g1,g2)
    c: InternalAlignment(g1,g3)
    c: InternalAlignment(g2,g3)
    c: InternalAlignment(g4,g3)
    c: InternalAlignment(g5,g3)
    c: Block(g3)
    c: Coincident(g6,g0)
    c: Coincident(g6,g3)
    c: Horizontal(g6)
FEATURE [Sketcher::SketchObject] Sketch040
  FullyConstrained = true
  sketch-geometry (7):
    g0: LineSegment StartX=0 StartY=0 StartZ=0 EndX=0 EndY=6 EndZ=0
    g1: Circle CenterX=0 CenterY=0 CenterZ=0 NormalX=0 NormalY=0 NormalZ=1 AngleXU=0 Radius=1
    g2: Circle CenterX=8 CenterY=6 CenterZ=0 NormalX=0 NormalY=0 NormalZ=1 AngleXU=0 Radius=1
    g3: BSplineCurve PolesCount=3 KnotsCount=2 Degree=2 IsPeriodic=0
    g4: GeomPoint X=0 Y=0 Z=0
    g5: GeomPoint X=8 Y=6 Z=0
    g6: LineSegment StartX=0 StartY=6 StartZ=0 EndX=8 EndY=6 EndZ=0
  constraints (14):
    c: Coincident(g0,g-1)
    c: Distance(g0) = 6
    c: Vertical(g0)
    c: Coincident(g3,g0)
    c: Weight(g1) = 1
    c: Equal(g1,g2)
    c: InternalAlignment(g1,g3)
    c: InternalAlignment(g2,g3)
    c: InternalAlignment(g4,g3)
    c: InternalAlignment(g5,g3)
    c: Block(g3)
    c: Coincident(g6,g0)
    c: Coincident(g6,g3)
    c: Horizontal(g6)
FEATURE [Sketcher::SketchObject] Sketch041
  FullyConstrained = true
  sketch-geometry (7):
    g0: LineSegment StartX=0 StartY=0 StartZ=0 EndX=0 EndY=6 EndZ=0
    g1: Circle CenterX=0 CenterY=0 CenterZ=0 NormalX=0 NormalY=0 NormalZ=1 AngleXU=0 Radius=1
    g2: Circle CenterX=8 CenterY=6 CenterZ=0 NormalX=0 NormalY=0 NormalZ=1 AngleXU=0 Radius=1
    g3: BSplineCurve PolesCount=3 KnotsCount=2 Degree=2 IsPeriodic=0
    g4: GeomPoint X=0 Y=0 Z=0
    g5: GeomPoint X=8 Y=6 Z=0
    g6: LineSegment StartX=0 StartY=6 StartZ=0 EndX=8 EndY=6 EndZ=0
  constraints (14):
    c: Coincident(g0,g-1)
    c: Distance(g0) = 6
    c: Vertical(g0)
    c: Coincident(g3,g0)
    c: Weight(g1) = 1
    c: Equal(g1,g2)
    c: InternalAlignment(g1,g3)
    c: InternalAlignment(g2,g3)
    c: InternalAlignment(g4,g3)
    c: InternalAlignment(g5,g3)
    c: Block(g3)
    c: Coincident(g6,g0)
    c: Coincident(g6,g3)
    c: Horizontal(g6)
FEATURE [Sketcher::SketchObject] Sketch042
  FullyConstrained = true
  sketch-geometry (7):
    g0: LineSegment StartX=0 StartY=0 StartZ=0 EndX=0 EndY=6 EndZ=0
    g1: Circle CenterX=0 CenterY=0 CenterZ=0 NormalX=0 NormalY=0 NormalZ=1 AngleXU=0 Radius=1
    g2: Circle CenterX=8 CenterY=6 CenterZ=0 NormalX=0 NormalY=0 NormalZ=1 AngleXU=0 Radius=1
    g3: BSplineCurve PolesCount=3 KnotsCount=2 Degree=2 IsPeriodic=0
    g4: GeomPoint X=0 Y=0 Z=0
    g5: GeomPoint X=8 Y=6 Z=0
    g6: LineSegment StartX=0 StartY=6 StartZ=0 EndX=8 EndY=6 EndZ=0
  constraints (14):
    c: Coincident(g0,g-1)
    c: Distance(g0) = 6
    c: Vertical(g0)
    c: Coincident(g3,g0)
    c: Weight(g1) = 1
    c: Equal(g1,g2)
    c: InternalAlignment(g1,g3)
    c: InternalAlignment(g2,g3)
    c: InternalAlignment(g4,g3)
    c: InternalAlignment(g5,g3)
    c: Block(g3)
    c: Coincident(g6,g0)
    c: Coincident(g6,g3)
    c: Horizontal(g6)
FEATURE [Part::Extrusion] Extrude030  label="caseScrewPillarBracket008"
  Base = -> Sketch039
  Dir = (0,0,1)
  DirMode = 2
  FaceMakerClass = Part::FaceMakerBullseye
  LengthFwd = 2.4
  LengthRev = 0
  Placement = pos=(15.76,29,8.8) rot=(0,1,0;0rad)
  Solid = true
  Symmetric = false
FEATURE [Part::Extrusion] Extrude031  label="caseScrewPillarBracket009"
  Base = -> Sketch040
  Dir = (0,0,1)
  DirMode = 2
  FaceMakerClass = Part::FaceMakerBullseye
  LengthFwd = 2.4
  LengthRev = 0
  Placement = pos=(15.76,29,60.8) rot=(0,0,1;0rad)
  Solid = true
  Symmetric = false
FEATURE [Part::Extrusion] Extrude032  label="caseScrewPillarBracket010"
  Base = -> Sketch041
  Dir = (0,0,1)
  DirMode = 2
  FaceMakerClass = Part::FaceMakerBullseye
  LengthFwd = 2.4
  LengthRev = 0
  Placement = pos=(13.7,29,13.26) rot=(0,-1,0;1.5708rad)
  Solid = true
  Symmetric = false
FEATURE [Part::Extrusion] Extrude033  label="caseScrewPillarBracket011"
  Base = -> Sketch042
  Dir = (0,0,1)
  DirMode = 2
  FaceMakerClass = Part::FaceMakerBullseye
  LengthFwd = 2.4
  LengthRev = 0
  Placement = pos=(11.3,29,58.74) rot=(0,1,0;1.5708rad)
  Solid = true
  Symmetric = false
FEATURE [Sketcher::SketchObject] Sketch043
  FullyConstrained = true
  sketch-geometry (7):
    g0: LineSegment StartX=0 StartY=0 StartZ=0 EndX=0 EndY=6 EndZ=0
    g1: Circle CenterX=0 CenterY=0 CenterZ=0 NormalX=0 NormalY=0 NormalZ=1 AngleXU=0 Radius=1
    g2: Circle CenterX=8 CenterY=6 CenterZ=0 NormalX=0 NormalY=0 NormalZ=1 AngleXU=0 Radius=1
    g3: BSplineCurve PolesCount=3 KnotsCount=2 Degree=2 IsPeriodic=0
    g4: GeomPoint X=0 Y=0 Z=0
    g5: GeomPoint X=8 Y=6 Z=0
    g6: LineSegment StartX=0 StartY=6 StartZ=0 EndX=8 EndY=6 EndZ=0
  constraints (14):
    c: Coincident(g0,g-1)
    c: Distance(g0) = 6
    c: Vertical(g0)
    c: Coincident(g3,g0)
    c: Weight(g1) = 1
    c: Equal(g1,g2)
    c: InternalAlignment(g1,g3)
    c: InternalAlignment(g2,g3)
    c: InternalAlignment(g4,g3)
    c: InternalAlignment(g5,g3)
    c: Block(g3)
    c: Coincident(g6,g0)
    c: Coincident(g6,g3)
    c: Horizontal(g6)
FEATURE [Part::Extrusion] Extrude034  label="caseScrewPillarBracket012"
  Base = -> Sketch043
  Dir = (0,0,1)
  DirMode = 2
  FaceMakerClass = Part::FaceMakerBullseye
  LengthFwd = 2.4
  LengthRev = 0
  Placement = pos=(88.3,29,65.23) rot=(0,1,0;1.5708rad)
  Solid = true
  Symmetric = false
FEATURE [Sketcher::SketchObject] Sketch044
  FullyConstrained = true
  sketch-geometry (7):
    g0: LineSegment StartX=0 StartY=0 StartZ=0 EndX=0 EndY=6 EndZ=0
    g1: Circle CenterX=0 CenterY=0 CenterZ=0 NormalX=0 NormalY=0 NormalZ=1 AngleXU=0 Radius=1
    g2: Circle CenterX=8 CenterY=6 CenterZ=0 NormalX=0 NormalY=0 NormalZ=1 AngleXU=0 Radius=1
    g3: BSplineCurve PolesCount=3 KnotsCount=2 Degree=2 IsPeriodic=0
    g4: GeomPoint X=0 Y=0 Z=0
    g5: GeomPoint X=8 Y=6 Z=0
    g6: LineSegment StartX=0 StartY=6 StartZ=0 EndX=8 EndY=6 EndZ=0
  constraints (14):
    c: Coincident(g0,g-1)
    c: Distance(g0) = 6
    c: Vertical(g0)
    c: Coincident(g3,g0)
    c: Weight(g1) = 1
    c: Equal(g1,g2)
    c: InternalAlignment(g1,g3)
    c: InternalAlignment(g2,g3)
    c: InternalAlignment(g4,g3)
    c: InternalAlignment(g5,g3)
    c: Block(g3)
    c: Coincident(g6,g0)
    c: Coincident(g6,g3)
    c: Horizontal(g6)
FEATURE [Part::Extrusion] Extrude035  label="caseScrewPillarBracket013"
  Base = -> Sketch044
  Dir = (0,0,1)
  DirMode = 2
  FaceMakerClass = Part::FaceMakerBullseye
  LengthFwd = 2.4
  LengthRev = 0
  Placement = pos=(90.7,29,6.77) rot=(0,-1,0;1.5708rad)
  Solid = true
  Symmetric = false
FEATURE [Sketcher::SketchObject] Sketch045
  FullyConstrained = true
  sketch-geometry (7):
    g0: LineSegment StartX=0 StartY=0 StartZ=0 EndX=0 EndY=6 EndZ=0
    g1: Circle CenterX=0 CenterY=0 CenterZ=0 NormalX=0 NormalY=0 NormalZ=1 AngleXU=0 Radius=1
    g2: Circle CenterX=8 CenterY=6 CenterZ=0 NormalX=0 NormalY=0 NormalZ=1 AngleXU=0 Radius=1
    g3: BSplineCurve PolesCount=3 KnotsCount=2 Degree=2 IsPeriodic=0
    g4: GeomPoint X=0 Y=0 Z=0
    g5: GeomPoint X=8 Y=6 Z=0
    g6: LineSegment StartX=0 StartY=6 StartZ=0 EndX=8 EndY=6 EndZ=0
  constraints (14):
    c: Coincident(g0,g-1)
    c: Distance(g0) = 6
    c: Vertical(g0)
    c: Coincident(g3,g0)
    c: Weight(g1) = 1
    c: Equal(g1,g2)
    c: InternalAlignment(g1,g3)
    c: InternalAlignment(g2,g3)
    c: InternalAlignment(g4,g3)
    c: InternalAlignment(g5,g3)
    c: Block(g3)
    c: Coincident(g6,g0)
    c: Coincident(g6,g3)
    c: Horizontal(g6)
FEATURE [Sketcher::SketchObject] Sketch046
  FullyConstrained = true
  sketch-geometry (7):
    g0: LineSegment StartX=0 StartY=0 StartZ=0 EndX=0 EndY=6 EndZ=0
    g1: Circle CenterX=0 CenterY=0 CenterZ=0 NormalX=0 NormalY=0 NormalZ=1 AngleXU=0 Radius=1
    g2: Circle CenterX=8 CenterY=6 CenterZ=0 NormalX=0 NormalY=0 NormalZ=1 AngleXU=0 Radius=1
    g3: BSplineCurve PolesCount=3 KnotsCount=2 Degree=2 IsPeriodic=0
    g4: GeomPoint X=0 Y=0 Z=0
    g5: GeomPoint X=8 Y=6 Z=0
    g6: LineSegment StartX=0 StartY=6 StartZ=0 EndX=8 EndY=6 EndZ=0
  constraints (14):
    c: Coincident(g0,g-1)
    c: Distance(g0) = 6
    c: Vertical(g0)
    c: Coincident(g3,g0)
    c: Weight(g1) = 1
    c: Equal(g1,g2)
    c: InternalAlignment(g1,g3)
    c: InternalAlignment(g2,g3)
    c: InternalAlignment(g4,g3)
    c: InternalAlignment(g5,g3)
    c: Block(g3)
    c: Coincident(g6,g0)
    c: Coincident(g6,g3)
    c: Horizontal(g6)
FEATURE [Part::Extrusion] Extrude036  label="caseScrewPillarBracket014"
  Base = -> Sketch045
  Dir = (0,0,1)
  DirMode = 2
  FaceMakerClass = Part::FaceMakerBullseye
  LengthFwd = 2.4
  LengthRev = 0
  Placement = pos=(110.7,29,6.77) rot=(0,-1,0;1.5708rad)
  Solid = true
  Symmetric = false
FEATURE [Part::Extrusion] Extrude037  label="caseScrewPillarBracket015"
  Base = -> Sketch046
  Dir = (0,0,1)
  DirMode = 2
  FaceMakerClass = Part::FaceMakerBullseye
  LengthFwd = 2.4
  LengthRev = 0
  Placement = pos=(108.3,29,65.23) rot=(0,1,0;1.5708rad)
  Solid = true
  Symmetric = false
FEATURE [Part::Box] Box013  label="frontCaseScrewPillarBracket002"
  AttacherType = Attacher::AttachEngine3D
  Height = 2.4
  Length = 22
  Placement = pos=(87,28,2.3) rot=(0,0,1;0rad)
  Width = 7
FEATURE [Part::Box] Box014  label="frontCaseScrewPillarBracket003"
  AttacherType = Attacher::AttachEngine3D
  Height = 2.4
  Length = 22
  Placement = pos=(87,28,67.3) rot=(0,0,1;0rad)
  Width = 7
FEATURE [Part::Feature] Face087
  shape: bbox 4.8 x 30.2 x 2e-07 mm, 1 faces, 0 solids (baked)
FEATURE [Part::Revolution] Revolve091  label="frontCaseScrewPost004"
  Angle = 360
  Axis = (0,1,0)
  Base = (0,0,0)
  FaceMakerClass = Part::FaceMakerBullseye
  Placement = pos=(89.5,4.5,3.5) rot=(0,0,1;0rad)
  Solid = false
  Source = -> Face087
  Symmetric = false
FEATURE [Part::Feature] Face088
  shape: bbox 4.8 x 30.2 x 2e-07 mm, 1 faces, 0 solids (baked)
FEATURE [Part::Revolution] Revolve092  label="frontCaseScrewPost005"
  Angle = 360
  Axis = (0,1,0)
  Base = (0,0,0)
  FaceMakerClass = Part::FaceMakerBullseye
  Placement = pos=(89.5,4.5,68.5) rot=(0,0,1;0rad)
  Solid = false
  Source = -> Face088
  Symmetric = false
FEATURE [Part::Feature] Face089
  shape: bbox 3.5 x 30.2 x 2e-07 mm, 1 faces, 0 solids (baked)
FEATURE [Part::Revolution] Revolve093  label="backCaseScrewPost002"
  Angle = 360
  Axis = (0,1,0)
  Base = (0,0,0)
  FaceMakerClass = Part::FaceMakerBullseye
  Placement = pos=(12.5,4.5,10) rot=(0,0,1;0rad)
  Solid = false
  Source = -> Face089
  Symmetric = false
FEATURE [Part::Feature] Face090
  shape: bbox 3.5 x 30.2 x 2e-07 mm, 1 faces, 0 solids (baked)
FEATURE [Part::Revolution] Revolve094  label="backCaseScrewPost003"
  Angle = 360
  Axis = (0,1,0)
  Base = (0,0,0)
  FaceMakerClass = Part::FaceMakerBullseye
  Placement = pos=(12.5,4.5,62) rot=(0,0,1;0rad)
  Solid = false
  Source = -> Face090
  Symmetric = false
FEATURE [Part::Box] Box015  label="Cube011"
  AttacherType = Attacher::AttachEngine3D
  Height = 28.8
  Length = 3
  Placement = pos=(107.3,28,21.6) rot=(0,0,1;0rad)
  Width = 7
FEATURE [Part::Box] Box016  label="Cube012"
  AttacherType = Attacher::AttachEngine3D
  Height = 3
  Length = 7.4
  Placement = pos=(107.3,28,18.6) rot=(0,0,1;0rad)
  Width = 7
FEATURE [Part::Box] Box017  label="Cube013"
  AttacherType = Attacher::AttachEngine3D
  Height = 3
  Length = 7.4
  Placement = pos=(107.3,28,50.4) rot=(0,0,1;0rad)
  Width = 7
FEATURE [Part::Cylinder] Cylinder024
  Angle = 360
  AttacherType = Attacher::AttachEngine3D
  Height = 20
  Placement = pos=(0,0,36.15) rot=(0,0,1;0rad)
  Radius = 14.3
FEATURE [Part::Cylinder] Cylinder025
  Angle = 360
  AttacherType = Attacher::AttachEngine3D
  Height = 10
  Placement = pos=(0,0,36.15) rot=(0,0,1;0rad)
  Radius = 4
FEATURE [Part::MultiFuse] Fusion066  label="removeToCreteHoleForPlugHousing009"
  Placement = pos=(70,19,36) rot=(0,1,0;1.5708rad)
  Shapes = -> [Cylinder024,Cylinder025]
FEATURE [Part::MultiFuse] Fusion065  label="plugHousingBracketHolder002"
  Shapes = -> [Box017,Box015,Box016]
FEATURE [Part::Cut] Cut025  label="plugHousingBracketHolder003"
  Base = -> Fusion065
  Placement = pos=(7,0,0) rot=(0,0,1;0rad)
  Tool = -> Fusion066
FEATURE [Sketcher::SketchObject] Sketch047
  FullyConstrained = false
  Placement = pos=(0,0,0) rot=(1,0,0;1.5708rad)
  sketch-geometry (24):
    g0: ArcOfCircle CenterX=-4 CenterY=-10.5 CenterZ=0 NormalX=0 NormalY=0 NormalZ=1 AngleXU=0 Radius=1.5 StartAngle=6e-16 EndAngle=3.14159
    g1: ArcOfCircle CenterX=-34.2 CenterY=-10.5 CenterZ=0 NormalX=0 NormalY=0 NormalZ=1 AngleXU=0 Radius=1.5 StartAngle=0 EndAngle=3.14159
    g2: ArcOfCircle CenterX=-34.2 CenterY=-27.7 CenterZ=0 NormalX=0 NormalY=0 NormalZ=1 AngleXU=0 Radius=1.5 StartAngle=3.14159 EndAngle=6.28319
    g3: ArcOfCircle CenterX=-4 CenterY=-27.7 CenterZ=0 NormalX=0 NormalY=0 NormalZ=1 AngleXU=0 Radius=1.5 StartAngle=3.1416 EndAngle=6.28319
    g4: ArcOfCircle CenterX=-10 CenterY=-4.3 CenterZ=0 NormalX=0 NormalY=0 NormalZ=1 AngleXU=0 Radius=1.5 StartAngle=2e-16 EndAngle=3.14159
    g5: ArcOfCircle CenterX=-16.1 CenterY=-1.8 CenterZ=0 NormalX=0 NormalY=0 NormalZ=1 AngleXU=0 Radius=1.5 StartAngle=5e-16 EndAngle=3.14159
    g6: ArcOfCircle CenterX=-22.1 CenterY=-1.8 CenterZ=0 NormalX=0 NormalY=0 NormalZ=1 AngleXU=0 Radius=1.5 StartAngle=5e-16 EndAngle=3.14159
    g7: ArcOfCircle CenterX=-28.2 CenterY=-4.3 CenterZ=0 NormalX=0 NormalY=0 NormalZ=1 AngleXU=0 Radius=1.5 StartAngle=2e-16 EndAngle=3.14159
    g8: ArcOfCircle CenterX=-10 CenterY=-33.9 CenterZ=0 NormalX=0 NormalY=0 NormalZ=1 AngleXU=0 Radius=1.5 StartAngle=3.14159 EndAngle=6.28319
    g9: ArcOfCircle CenterX=-16.1 CenterY=-36.4 CenterZ=0 NormalX=0 NormalY=0 NormalZ=1 AngleXU=0 Radius=1.5 StartAngle=3.14159 EndAngle=6.28319
    g10: ArcOfCircle CenterX=-22.1 CenterY=-36.4 CenterZ=0 NormalX=0 NormalY=0 NormalZ=1 AngleXU=0 Radius=1.5 StartAngle=3.14159 EndAngle=6.28319
    g11: ArcOfCircle CenterX=-28.2 CenterY=-33.9 CenterZ=0 NormalX=0 NormalY=0 NormalZ=1 AngleXU=0 Radius=1.5 StartAngle=3.14159 EndAngle=6.28319
    g12: LineSegment StartX=-35.7 StartY=-10.5 StartZ=0 EndX=-35.7 EndY=-27.7 EndZ=0
    g13: LineSegment StartX=-32.7 StartY=-10.5 StartZ=0 EndX=-32.7 EndY=-27.7 EndZ=0
    g14: LineSegment StartX=-29.7 StartY=-33.9 StartZ=0 EndX=-29.7 EndY=-4.3 EndZ=0
    g15: LineSegment StartX=-26.7 StartY=-33.9 StartZ=0 EndX=-26.7 EndY=-4.3 EndZ=0
    g16: LineSegment StartX=-2.5 StartY=-10.5 StartZ=0 EndX=-2.5 EndY=-27.7 EndZ=0
    g17: LineSegment StartX=-8.5 StartY=-4.3 StartZ=0 EndX=-8.5 EndY=-33.9 EndZ=0
    g18: LineSegment StartX=-5.5 StartY=-10.5 StartZ=0 EndX=-5.5 EndY=-27.7 EndZ=0
    g19: LineSegment StartX=-11.5 StartY=-4.3 StartZ=0 EndX=-11.5 EndY=-33.9 EndZ=0
    g20: LineSegment StartX=-14.6 StartY=-1.8 StartZ=0 EndX=-14.6 EndY=-36.4 EndZ=0
    g21: LineSegment StartX=-17.6 StartY=-1.8 StartZ=0 EndX=-17.6 EndY=-36.4 EndZ=0
    g22: LineSegment StartX=-20.6 StartY=-36.4 StartZ=0 EndX=-20.6 EndY=-1.8 EndZ=0
    g23: LineSegment StartX=-23.6 StartY=-1.8 StartZ=0 EndX=-23.6 EndY=-36.4 EndZ=0
  constraints (48):
    c: Block(g0)
    c: Block(g1)
    c: Block(g2)
    c: Block(g3)
    c: Block(g4)
    c: Block(g5)
    c: Block(g6)
    c: Block(g7)
    c: Block(g8)
    c: Block(g9)
    c: Block(g10)
    c: Block(g11)
    c: Coincident(g12,g1)
    c: Coincident(g12,g2)
    c: Vertical(g12)
    c: Coincident(g13,g1)
    c: Coincident(g13,g2)
    c: Vertical(g13)
    c: Coincident(g14,g11)
    c: Coincident(g14,g7)
    c: Vertical(g14)
    c: Coincident(g15,g11)
    c: Coincident(g15,g7)
    c: Vertical(g15)
    c: Coincident(g16,g0)
    c: Coincident(g16,g3)
    c: Vertical(g16)
    c: Coincident(g17,g4)
    c: Coincident(g17,g8)
    c: Vertical(g17)
    c: Coincident(g18,g0)
    c: Coincident(g18,g3)
    c: Vertical(g18)
    c: Coincident(g19,g4)
    c: Coincident(g19,g8)
    c: Vertical(g19)
    c: Coincident(g20,g5)
    c: Coincident(g20,g9)
    c: Vertical(g20)
    c: Coincident(g21,g5)
    c: Coincident(g21,g9)
    c: Vertical(g21)
    c: Coincident(g22,g10)
    c: Coincident(g22,g6)
    c: Vertical(g22)
    c: Coincident(g23,g6)
    c: Coincident(g23,g10)
    c: Vertical(g23)
FEATURE [Part::Extrusion] Extrude038  label="removeToCreateFanGrillHoles001"
  Base = -> Sketch047
  Dir = (0,-1,6e-16)
  DirMode = 2
  FaceMakerClass = Part::FaceMakerBullseye
  LengthFwd = 10
  LengthRev = 0
  Placement = pos=(65.4,44,54.82) rot=(0,0,1;0rad)
  Solid = true
  Symmetric = false
FEATURE [Part::Feature] Wire004
  shape: bbox 11 x 5.2 x 2e-07 mm, 0 faces, 0 solids (baked)
FEATURE [Part::Revolution] Revolve095
  Angle = 360
  Axis = (0,1,0)
  Base = (0,0,0)
  FaceMakerClass = Part::FaceMakerBullseye
  Placement = pos=(30.3,38,19.7) rot=(0,0,1;0rad)
  Solid = true
  Source = -> Wire004
  Symmetric = false
FEATURE [Part::Feature] Wire005
  shape: bbox 11 x 5.2 x 2e-07 mm, 0 faces, 0 solids (baked)
FEATURE [Part::Revolution] Revolve096
  Angle = 360
  Axis = (0,1,0)
  Base = (0,0,0)
  FaceMakerClass = Part::FaceMakerBullseye
  Placement = pos=(30.3,38,51.7) rot=(0,0,1;0rad)
  Solid = true
  Source = -> Wire005
  Symmetric = false
FEATURE [Part::Feature] Wire006
  shape: bbox 11 x 5.2 x 2e-07 mm, 0 faces, 0 solids (baked)
FEATURE [Part::Revolution] Revolve097
  Angle = 360
  Axis = (0,1,0)
  Base = (0,0,0)
  FaceMakerClass = Part::FaceMakerBullseye
  Placement = pos=(62.3,38,51.7) rot=(0,0,1;0rad)
  Solid = true
  Source = -> Wire006
  Symmetric = false
FEATURE [Part::Feature] Wire007
  shape: bbox 11 x 5.2 x 2e-07 mm, 0 faces, 0 solids (baked)
FEATURE [Part::Revolution] Revolve098
  Angle = 360
  Axis = (0,1,0)
  Base = (0,0,0)
  FaceMakerClass = Part::FaceMakerBullseye
  Placement = pos=(62.3,38,19.7) rot=(0,0,1;0rad)
  Solid = true
  Source = -> Wire007
  Symmetric = false
FEATURE [Part::MultiFuse] Fusion067  label="fanScrewHousing002"
  Shapes = -> [Revolve098,Revolve097,Revolve096,Revolve095]
FEATURE [Part::Feature] Face091 .. Face094  x4 (patterned run collapsed; names and placements below)
  shape: bbox 3.5 x 17.8 x 2e-07 mm, 1 faces, 0 solids (baked)
FEATURE [Part::Revolution] Revolve099  label="removeToCreateScrewAndThreadedInsertHole026"
  Angle = 360
  Axis = (0,1,0)
  Base = (0,0,0)
  FaceMakerClass = Part::FaceMakerBullseye
  Placement = pos=(62.3,30.3,19.7) rot=(0,0,1;0rad)
  Solid = false
  Source = -> Face091
  Symmetric = false
FEATURE [Part::Revolution] Revolve100  label="removeToCreateScrewAndThreadedInsertHole027"
  Angle = 360
  Axis = (0,1,0)
  Base = (0,0,0)
  FaceMakerClass = Part::FaceMakerBullseye
  Placement = pos=(62.3,30.3,51.7) rot=(0,0,1;0rad)
  Solid = false
  Source = -> Face092
  Symmetric = false
FEATURE [Part::Revolution] Revolve101  label="removeToCreateScrewAndThreadedInsertHole028"
  Angle = 360
  Axis = (0,1,0)
  Base = (0,0,0)
  FaceMakerClass = Part::FaceMakerBullseye
  Placement = pos=(30.3,30.3,19.7) rot=(0,0,1;0rad)
  Solid = false
  Source = -> Face093
  Symmetric = false
FEATURE [Part::Revolution] Revolve102  label="removeToCreateScrewAndThreadedInsertHole029"
  Angle = 360
  Axis = (0,1,0)
  Base = (0,0,0)
  FaceMakerClass = Part::FaceMakerBullseye
  Placement = pos=(30.3,30.3,51.7) rot=(0,0,1;0rad)
  Solid = false
  Source = -> Face094
  Symmetric = false
FEATURE [Part::MultiFuse] Fusion068  label="createThreadedInsertHolesForFan002"
  Shapes = -> [Revolve099,Revolve100,Revolve101,Revolve102]
FEATURE [Part::Cut] Cut026  label="fanScrewHousing003"
  Base = -> Fusion067
  Tool = -> Fusion068
FEATURE [Sketcher::SketchObject] Sketch048
  FullyConstrained = false
  Placement = pos=(0,0,0) rot=(1,0,0;1.5708rad)
  sketch-geometry (24):
    g0: ArcOfCircle CenterX=-4 CenterY=-10.5 CenterZ=0 NormalX=0 NormalY=0 NormalZ=1 AngleXU=0 Radius=1.5 StartAngle=6e-16 EndAngle=3.14159
    g1: ArcOfCircle CenterX=-34.2 CenterY=-10.5 CenterZ=0 NormalX=0 NormalY=0 NormalZ=1 AngleXU=0 Radius=1.5 StartAngle=0 EndAngle=3.14159
    g2: ArcOfCircle CenterX=-34.2 CenterY=-27.7 CenterZ=0 NormalX=0 NormalY=0 NormalZ=1 AngleXU=0 Radius=1.5 StartAngle=3.14159 EndAngle=6.28319
    g3: ArcOfCircle CenterX=-4 CenterY=-27.7 CenterZ=0 NormalX=0 NormalY=0 NormalZ=1 AngleXU=0 Radius=1.5 StartAngle=3.1416 EndAngle=6.28319
    g4: ArcOfCircle CenterX=-10 CenterY=-4.3 CenterZ=0 NormalX=0 NormalY=0 NormalZ=1 AngleXU=0 Radius=1.5 StartAngle=2e-16 EndAngle=3.14159
    g5: ArcOfCircle CenterX=-16.1 CenterY=-1.8 CenterZ=0 NormalX=0 NormalY=0 NormalZ=1 AngleXU=0 Radius=1.5 StartAngle=5e-16 EndAngle=3.14159
    g6: ArcOfCircle CenterX=-22.1 CenterY=-1.8 CenterZ=0 NormalX=0 NormalY=0 NormalZ=1 AngleXU=0 Radius=1.5 StartAngle=5e-16 EndAngle=3.14159
    g7: ArcOfCircle CenterX=-28.2 CenterY=-4.3 CenterZ=0 NormalX=0 NormalY=0 NormalZ=1 AngleXU=0 Radius=1.5 StartAngle=2e-16 EndAngle=3.14159
    g8: ArcOfCircle CenterX=-10 CenterY=-33.9 CenterZ=0 NormalX=0 NormalY=0 NormalZ=1 AngleXU=0 Radius=1.5 StartAngle=3.14159 EndAngle=6.28319
    g9: ArcOfCircle CenterX=-16.1 CenterY=-36.4 CenterZ=0 NormalX=0 NormalY=0 NormalZ=1 AngleXU=0 Radius=1.5 StartAngle=3.14159 EndAngle=6.28319
    g10: ArcOfCircle CenterX=-22.1 CenterY=-36.4 CenterZ=0 NormalX=0 NormalY=0 NormalZ=1 AngleXU=0 Radius=1.5 StartAngle=3.14159 EndAngle=6.28319
    g11: ArcOfCircle CenterX=-28.2 CenterY=-33.9 CenterZ=0 NormalX=0 NormalY=0 NormalZ=1 AngleXU=0 Radius=1.5 StartAngle=3.14159 EndAngle=6.28319
    g12: LineSegment StartX=-35.7 StartY=-10.5 StartZ=0 EndX=-35.7 EndY=-27.7 EndZ=0
    g13: LineSegment StartX=-32.7 StartY=-10.5 StartZ=0 EndX=-32.7 EndY=-27.7 EndZ=0
    g14: LineSegment StartX=-29.7 StartY=-33.9 StartZ=0 EndX=-29.7 EndY=-4.3 EndZ=0
    g15: LineSegment StartX=-26.7 StartY=-33.9 StartZ=0 EndX=-26.7 EndY=-4.3 EndZ=0
    g16: LineSegment StartX=-2.5 StartY=-10.5 StartZ=0 EndX=-2.5 EndY=-27.7 EndZ=0
    g17: LineSegment StartX=-8.5 StartY=-4.3 StartZ=0 EndX=-8.5 EndY=-33.9 EndZ=0
    g18: LineSegment StartX=-5.5 StartY=-10.5 StartZ=0 EndX=-5.5 EndY=-27.7 EndZ=0
    g19: LineSegment StartX=-11.5 StartY=-4.3 StartZ=0 EndX=-11.5 EndY=-33.9 EndZ=0
    g20: LineSegment StartX=-14.6 StartY=-1.8 StartZ=0 EndX=-14.6 EndY=-36.4 EndZ=0
    g21: LineSegment StartX=-17.6 StartY=-1.8 StartZ=0 EndX=-17.6 EndY=-36.4 EndZ=0
    g22: LineSegment StartX=-20.6 StartY=-36.4 StartZ=0 EndX=-20.6 EndY=-1.8 EndZ=0
    g23: LineSegment StartX=-23.6 StartY=-1.8 StartZ=0 EndX=-23.6 EndY=-36.4 EndZ=0
  constraints (48):
    c: Block(g0)
    c: Block(g1)
    c: Block(g2)
    c: Block(g3)
    c: Block(g4)
    c: Block(g5)
    c: Block(g6)
    c: Block(g7)
    c: Block(g8)
    c: Block(g9)
    c: Block(g10)
    c: Block(g11)
    c: Coincident(g12,g1)
    c: Coincident(g12,g2)
    c: Vertical(g12)
    c: Coincident(g13,g1)
    c: Coincident(g13,g2)
    c: Vertical(g13)
    c: Coincident(g14,g11)
    c: Coincident(g14,g7)
    c: Vertical(g14)
    c: Coincident(g15,g11)
    c: Coincident(g15,g7)
    c: Vertical(g15)
    c: Coincident(g16,g0)
    c: Coincident(g16,g3)
    c: Vertical(g16)
    c: Coincident(g17,g4)
    c: Coincident(g17,g8)
    c: Vertical(g17)
    c: Coincident(g18,g0)
    c: Coincident(g18,g3)
    c: Vertical(g18)
    c: Coincident(g19,g4)
    c: Coincident(g19,g8)
    c: Vertical(g19)
    c: Coincident(g20,g5)
    c: Coincident(g20,g9)
    c: Vertical(g20)
    c: Coincident(g21,g5)
    c: Coincident(g21,g9)
    c: Vertical(g21)
    c: Coincident(g22,g10)
    c: Coincident(g22,g6)
    c: Vertical(g22)
    c: Coincident(g23,g6)
    c: Coincident(g23,g10)
    c: Vertical(g23)
FEATURE [Part::Extrusion] Extrude039  label="removeToCreateFanGrillHoles002"
  Base = -> Sketch048
  Dir = (0,-1,6e-16)
  DirMode = 2
  FaceMakerClass = Part::FaceMakerBullseye
  LengthFwd = 10
  LengthRev = 0
  Placement = pos=(65.4,44,54.82) rot=(0,0,1;0rad)
  Solid = true
  Symmetric = false
FEATURE [Part::Cut] Cut027  label="fanScrewHousing004"
  Base = -> Cut026
  Tool = -> Extrude038
FEATURE [Part::Cut] Cut028  label="top014"
  Base = -> Fillet026
  Tool = -> Extrude039
FEATURE [Part::Feature] Face095 .. Face098  x4 (patterned run collapsed; names and placements below)
  shape: bbox 3.5 x 17.8 x 2e-07 mm, 1 faces, 0 solids (baked)
FEATURE [Part::Revolution] Revolve103  label="removeToCreateScrewAndThreadedInsertHole030"
  Angle = 360
  Axis = (0,1,0)
  Base = (0,0,0)
  FaceMakerClass = Part::FaceMakerBullseye
  Placement = pos=(62.3,30.3,19.7) rot=(0,0,1;0rad)
  Solid = false
  Source = -> Face095
  Symmetric = false
FEATURE [Part::Revolution] Revolve104  label="removeToCreateScrewAndThreadedInsertHole031"
  Angle = 360
  Axis = (0,1,0)
  Base = (0,0,0)
  FaceMakerClass = Part::FaceMakerBullseye
  Placement = pos=(62.3,30.3,51.7) rot=(0,0,1;0rad)
  Solid = false
  Source = -> Face096
  Symmetric = false
FEATURE [Part::Revolution] Revolve105  label="removeToCreateScrewAndThreadedInsertHole032"
  Angle = 360
  Axis = (0,1,0)
  Base = (0,0,0)
  FaceMakerClass = Part::FaceMakerBullseye
  Placement = pos=(30.3,30.3,19.7) rot=(0,0,1;0rad)
  Solid = false
  Source = -> Face097
  Symmetric = false
FEATURE [Part::Revolution] Revolve106  label="removeToCreateScrewAndThreadedInsertHole033"
  Angle = 360
  Axis = (0,1,0)
  Base = (0,0,0)
  FaceMakerClass = Part::FaceMakerBullseye
  Placement = pos=(30.3,30.3,51.7) rot=(0,0,1;0rad)
  Solid = false
  Source = -> Face098
  Symmetric = false
FEATURE [Part::MultiFuse] Fusion069  label="createThreadedInsertHolesForFan003"
  Shapes = -> [Revolve103,Revolve104,Revolve105,Revolve106]
FEATURE [Part::Cut] Cut029  label="top015"
  Base = -> Cut028
  Tool = -> Fusion054
FEATURE [Part::Cut] Cut030  label="fanScrewHousing005"
  Base = -> Cut027
  Tool = -> Fusion069
FEATURE [Part::Cylinder] Cylinder026  label="removeToCreteHoleForPlugHousing010"
  Angle = 360
  AttacherType = Attacher::AttachEngine3D
  Height = 20
  Placement = pos=(-2,19,36) rot=(0,1,0;1.5708rad)
  Radius = 14.3
FEATURE [Part::Box] Box018  label="removeToCreteHoleForPlugHousing011"
  AttacherType = Attacher::AttachEngine3D
  Height = 28.6
  Length = 10
  Placement = pos=(-2,0,21.7) rot=(0,0,1;0rad)
  Width = 19
FEATURE [Part::Box] Box019  label="wireHolderBottomCaseBit"
  AttacherType = Attacher::AttachEngine3D
  Height = 28
  Length = 3
  Placement = pos=(0,0,22) rot=(0,0,1;0rad)
  Width = 21
FEATURE [Part::Cylinder] Cylinder027  label="removeToCreteHoleForPlugHousing012"
  Angle = 360
  AttacherType = Attacher::AttachEngine3D
  Height = 20
  Placement = pos=(-2,19,36) rot=(0,1,0;1.5708rad)
  Radius = 14.3
FEATURE [Part::Cut] Cut031  label="wireHolderBottomCaseBit001"
  Base = -> Box019
  Tool = -> Cylinder027
FEATURE [Part::MultiFuse] Fusion070  label="removeToCreteHoleForPlugHousing013"
  Shapes = -> [Box018,Cylinder026]
FEATURE [Part::Cut] Cut032  label="top016"
  Base = -> Cut029
  Tool = -> Fusion070
FEATURE [Part::Cylinder] Cylinder028
  Angle = 360
  AttacherType = Attacher::AttachEngine3D
  Height = 20
  Placement = pos=(0,0,36.15) rot=(0,0,1;0rad)
  Radius = 14.3
FEATURE [Part::Cylinder] Cylinder029
  Angle = 360
  AttacherType = Attacher::AttachEngine3D
  Height = 10
  Placement = pos=(0,0,36.15) rot=(0,0,1;0rad)
  Radius = 4
FEATURE [Part::MultiFuse] Fusion071  label="removeToCreteHoleForPlugHousing014"
  Placement = pos=(70,19,36) rot=(0,1,0;1.5708rad)
  Shapes = -> [Cylinder028,Cylinder029]
FEATURE [Sketcher::SketchObject] Sketch049  label="topSketch011"
  FullyConstrained = true
  sketch-geometry (4):
    g0: ArcOfCircle CenterX=105 CenterY=19 CenterZ=0 NormalX=0 NormalY=0 NormalZ=1 AngleXU=0 Radius=20.6155 StartAngle=5.54125 EndAngle=6.28319
    g1: ArcOfCircle CenterX=105 CenterY=19 CenterZ=0 NormalX=0 NormalY=0 NormalZ=1 AngleXU=0 Radius=13 StartAngle=5.54125 EndAngle=6.28319
    g2: LineSegment StartX=118 StartY=19 StartZ=0 EndX=125.616 EndY=19 EndZ=0
    g3: LineSegment StartX=114.583 StartY=10.2157 StartZ=0 EndX=120.197 EndY=5.06982 EndZ=0
  constraints (7):
    c: Block(g0)
    c: Block(g1)
    c: Coincident(g2,g1)
    c: Coincident(g2,g0)
    c: Horizontal(g2)
    c: Coincident(g3,g1)
    c: Coincident(g3,g0)
FEATURE [Part::Box] Box020  label="removeToCreteHoleForPlugHousing015"
  AttacherType = Attacher::AttachEngine3D
  Height = 28.6
  Length = 20
  Placement = pos=(106.15,0,21.7) rot=(0,0,1;0rad)
  Width = 19
FEATURE [Part::MultiFuse] Fusion072  label="removeToCreteHoleForPlugHousing016"
  Shapes = -> [Box020,Fusion071]
FEATURE [Part::Cut] Cut033  label="removeToCreteHoleForPlugHousing017"
  Base = -> Cut032
  Tool = -> Fusion072
FEATURE [Part::Cylinder] Cylinder030
  Angle = 360
  AttacherType = Attacher::AttachEngine3D
  Height = 20
  Placement = pos=(0,0,36.15) rot=(0,0,1;0rad)
  Radius = 14.3
FEATURE [Part::Cylinder] Cylinder031
  Angle = 360
  AttacherType = Attacher::AttachEngine3D
  Height = 10
  Placement = pos=(0,0,36.15) rot=(0,0,1;0rad)
  Radius = 4
FEATURE [Part::Box] Box021  label="removeToCreteHoleForPlugHousing019"
  AttacherType = Attacher::AttachEngine3D
  Height = 28.6
  Length = 20
  Placement = pos=(106.15,0,21.7) rot=(0,0,1;0rad)
  Width = 19
FEATURE [Part::MultiFuse] Fusion074  label="removeToCreteHoleForPlugHousing020"
  Placement = pos=(70,19,36) rot=(0,1,0;1.5708rad)
  Shapes = -> [Cylinder030,Cylinder031]
FEATURE [Part::MultiFuse] Fusion073  label="removeToCreteHoleForPlugHousing018"
  Placement = pos=(0,0,28.3) rot=(0,0,1;0rad)
  Shapes = -> [Box021,Fusion074]
FEATURE [Part::Cylinder] Cylinder032
  Angle = 360
  AttacherType = Attacher::AttachEngine3D
  Height = 20
  Placement = pos=(0,0,36.15) rot=(0,0,1;0rad)
  Radius = 14.3
FEATURE [Part::Cylinder] Cylinder033
  Angle = 360
  AttacherType = Attacher::AttachEngine3D
  Height = 10
  Placement = pos=(0,0,36.15) rot=(0,0,1;0rad)
  Radius = 4
FEATURE [Part::Box] Box022  label="removeToCreteHoleForPlugHousing021"
  AttacherType = Attacher::AttachEngine3D
  Height = 28.6
  Length = 20
  Placement = pos=(106.15,0,21.7) rot=(0,0,1;0rad)
  Width = 19
FEATURE [Part::MultiFuse] Fusion076  label="removeToCreteHoleForPlugHousing023"
  Placement = pos=(70,19,36) rot=(0,1,0;1.5708rad)
  Shapes = -> [Cylinder032,Cylinder033]
FEATURE [Part::MultiFuse] Fusion075  label="removeToCreteHoleForPlugHousing022"
  Placement = pos=(0,0,-28.3) rot=(0,0,1;0rad)
  Shapes = -> [Box022,Fusion076]
FEATURE [Part::MultiFuse] Fusion077  label="removeToCreatePlugHousingBottomBit"
  Shapes = -> [Fusion075,Fusion073]
FEATURE [Part::Cylinder] Cylinder034
  Angle = 360
  AttacherType = Attacher::AttachEngine3D
  Height = 20
  Placement = pos=(0,0,36.15) rot=(0,0,1;0rad)
  Radius = 14
FEATURE [Part::Cylinder] Cylinder035
  Angle = 360
  AttacherType = Attacher::AttachEngine3D
  Height = 10
  Placement = pos=(0,0,36.15) rot=(0,0,1;0rad)
  Radius = 4
FEATURE [Part::MultiFuse] Fusion078  label="removeToCreteHoleForPlugHousing024"
  Placement = pos=(70,19,36) rot=(0,1,0;1.5708rad)
  Shapes = -> [Cylinder034,Cylinder035]
FEATURE [Part::MultiFuse] Fusion079  label="removeToCreatePlugHousingBottomBit001"
  Shapes = -> [Fusion078,Fusion077]
FEATURE [Part::Extrusion] Extrude040  label="bottomPlugHousingBit"
  Base = -> Sketch049
  Dir = (0,0,1)
  DirMode = 2
  FaceMakerClass = Part::FaceMakerBullseye
  LengthFwd = 72
  LengthRev = 0
  Solid = true
  Symmetric = false
FEATURE [Part::Cut] Cut034  label="bottomPlugHousingBit001"
  Base = -> Extrude040
  Placement = pos=(-0.09,0,0) rot=(0,0,1;0rad)
  Tool = -> Fusion079
FEATURE [Part::Box] Box023  label="Cube014"
  AttacherType = Attacher::AttachEngine3D
  Height = 16
  Length = 8
  Placement = pos=(12.7,31.52,28) rot=(0,0,1;0rad)
  Width = 4
FEATURE [Part::Cylinder] Cylinder036
  Angle = 360
  AttacherType = Attacher::AttachEngine3D
  Height = 10
  Placement = pos=(0,0,36.15) rot=(0,0,1;0rad)
  Radius = 4
FEATURE [Part::Cylinder] Cylinder037
  Angle = 360
  AttacherType = Attacher::AttachEngine3D
  Height = 20
  Placement = pos=(0,0,36.15) rot=(0,0,1;0rad)
  Radius = 8.2
FEATURE [Part::MultiFuse] Fusion080  label="removeToCreteHoleForPlugHousing025"
  Placement = pos=(-42,19,36) rot=(0,1,0;1.5708rad)
  Shapes = -> [Cylinder037,Cylinder036]
FEATURE [Sketcher::SketchObject] Sketch050  label="topSketch012"
  FullyConstrained = true
  sketch-geometry (4):
    g0: LineSegment StartX=16.8446 StartY=31.512 StartZ=0 EndX=16.3251 EndY=34.4666 EndZ=0
    g1: ArcOfCircle CenterX=19 CenterY=19.2524 CenterZ=0 NormalX=0 NormalY=0 NormalZ=1 AngleXU=0 Radius=15.4476 StartAngle=1.74483 EndAngle=2.72717
    g2: ArcOfCircle CenterX=19 CenterY=19.2524 CenterZ=0 NormalX=0 NormalY=0 NormalZ=1 AngleXU=0 Radius=12.4476 StartAngle=1.74483 EndAngle=2.73189
    g3: LineSegment StartX=4.86004 StartY=25.4725 StartZ=0 EndX=7.58253 EndY=24.2107 EndZ=0
  constraints (7):
    c: Block(g0)
    c: Coincident(g1,g0)
    c: Coincident(g2,g0)
    c: Coincident(g3,g1)
    c: Coincident(g3,g2)
    c: Block(g1)
    c: Block(g2)
FEATURE [Part::Extrusion] Extrude041
  Base = -> Sketch050
  Dir = (0,0,1)
  DirMode = 2
  FaceMakerClass = Part::FaceMakerBullseye
  LengthFwd = 10.6
  LengthRev = 0
  Placement = pos=(0,0,31) rot=(0,0,1;0rad)
  Solid = true
  Symmetric = false
FEATURE [Part::Cut] Cut035
  Base = -> Extrude041
  Placement = pos=(0,0,-0.3) rot=(0,0,1;0rad)
  Tool = -> Fusion080
FEATURE [Part::Cut] Cut036
  Base = -> Box023
  Tool = -> Cut035
FEATURE [Part::Fillet] Fillet027
  Base = -> Cut036
  Edges = 1 edges r=0.7: [Edge13]
FEATURE [Part::Fillet] Fillet028
  Base = -> Fillet027
  Edges = 1 edges r=0.7: [Edge13]
FEATURE [Part::Fillet] Fillet029
  Base = -> Fillet028
  Edges = 1 edges r=0.7: [Edge16]
FEATURE [Part::Fillet] Fillet030
  Base = -> Fillet029
  Edges = 1 edges r=0.7: [Edge11]
FEATURE [Part::Fillet] Fillet031
  Base = -> Fillet030
  Edges = 1 edges r=0.7: [Edge10]
FEATURE [Part::Fillet] Fillet032
  Base = -> Fillet031
  Edges = 1 edges r=1.2: [Edge5]
FEATURE [Part::Fillet] Fillet033
  Base = -> Fillet032
  Edges = 1 edges r=1.2: [Edge12]
FEATURE [Part::Fillet] Fillet034  label="wireHousingRetainer"
  Base = -> Fillet033
  Edges = 1 edges r=2: [Edge1]
  Placement = pos=(0.3,0,0) rot=(0,0,1;0rad)
FEATURE [Part::Feature] Face099
  shape: bbox 3.5 x 17.8 x 2e-07 mm, 1 faces, 0 solids (baked)
FEATURE [Part::Revolution] Revolve107  label="removeToCreateScrewAndThreadedInsertHole034"
  Angle = 360
  Axis = (0,1,0)
  Base = (0,0,0)
  FaceMakerClass = Part::FaceMakerBullseye
  Placement = pos=(12.5,0,10) rot=(0,0,1;0rad)
  Solid = false
  Source = -> Face099
  Symmetric = false
FEATURE [Part::Feature] Face100
  shape: bbox 3.5 x 17.8 x 2e-07 mm, 1 faces, 0 solids (baked)
FEATURE [Part::Revolution] Revolve108  label="removeToCreateScrewAndThreadedInsertHole035"
  Angle = 360
  Axis = (0,1,0)
  Base = (0,0,0)
  FaceMakerClass = Part::FaceMakerBullseye
  Placement = pos=(12.5,0,62) rot=(0,0,1;0rad)
  Solid = false
  Source = -> Face100
  Symmetric = false
FEATURE [Part::Feature] Face101
  shape: bbox 3.5 x 17.8 x 2e-07 mm, 1 faces, 0 solids (baked)
FEATURE [Part::Revolution] Revolve109  label="removeToCreateScrewAndThreadedInsertHole036"
  Angle = 360
  Axis = (0,1,0)
  Base = (0,0,0)
  FaceMakerClass = Part::FaceMakerBullseye
  Placement = pos=(89.5,0,68.5) rot=(0,0,1;0rad)
  Solid = false
  Source = -> Face101
  Symmetric = false
FEATURE [Part::Feature] Face102
  shape: bbox 3.5 x 17.8 x 2e-07 mm, 1 faces, 0 solids (baked)
FEATURE [Part::Revolution] Revolve110  label="removeToCreateScrewAndThreadedInsertHole037"
  Angle = 360
  Axis = (0,1,0)
  Base = (0,0,0)
  FaceMakerClass = Part::FaceMakerBullseye
  Placement = pos=(89.5,0,3.5) rot=(0,0,1;0rad)
  Solid = false
  Source = -> Face102
  Symmetric = false
FEATURE [Part::Feature] Face103
  shape: bbox 3.5 x 17.8 x 2e-07 mm, 1 faces, 0 solids (baked)
FEATURE [Part::Revolution] Revolve111  label="removeToCreateScrewAndThreadedInsertHole038"
  Angle = 360
  Axis = (0,1,0)
  Base = (0,0,0)
  FaceMakerClass = Part::FaceMakerBullseye
  Placement = pos=(109.5,4.7,3.5) rot=(0,0,1;0rad)
  Solid = false
  Source = -> Face103
  Symmetric = false
FEATURE [Part::Feature] Face104
  shape: bbox 3.5 x 17.8 x 2e-07 mm, 1 faces, 0 solids (baked)
FEATURE [Part::Revolution] Revolve112  label="removeToCreateScrewAndThreadedInsertHole039"
  Angle = 360
  Axis = (0,1,0)
  Base = (0,0,0)
  FaceMakerClass = Part::FaceMakerBullseye
  Placement = pos=(109.5,4.7,68.5) rot=(0,0,1;0rad)
  Solid = false
  Source = -> Face104
  Symmetric = false
FEATURE [Part::MultiFuse] Fusion081  label="removeToCreateScrewAndThreadedInsertHole040"
  Shapes = -> [Revolve107,Revolve108,Revolve109,Revolve110,Revolve111,Revolve112]
FEATURE [Part::MultiFuse] Fusion082  label="casePillars002"
  Shapes = -> [Revolve094,Revolve092,Revolve090,Revolve089,Revolve091,Revolve093]
FEATURE [Part::Cut] Cut037  label="casePillars003"
  Base = -> Fusion082
  Tool = -> Fusion081
FEATURE [Sketcher::SketchObject] Sketch051
  FullyConstrained = true
  Placement = pos=(117,19,0) rot=(0.57735,0.57735,0.57735;2.0944rad)
  sketch-geometry (48):
    g0: LineSegment StartX=-49.19 StartY=69.25 StartZ=0 EndX=-49.19 EndY=66.25 EndZ=0
    g1: LineSegment StartX=-49.19 StartY=63.5 StartZ=0 EndX=-49.19 EndY=60.5 EndZ=0
    g2: LineSegment StartX=-49.19 StartY=57.75 StartZ=0 EndX=-49.19 EndY=54.75 EndZ=0
    g3: LineSegment StartX=-49.19 StartY=52 StartZ=0 EndX=-49.19 EndY=49 EndZ=0
    g4: LineSegment StartX=-49.19 StartY=46.25 StartZ=0 EndX=-49.19 EndY=43.25 EndZ=0
    g5: LineSegment StartX=-49.19 StartY=40.5 StartZ=0 EndX=-49.19 EndY=37.5 EndZ=0
    g6: LineSegment StartX=-49.19 StartY=34.5 StartZ=0 EndX=-49.19 EndY=31.5 EndZ=0
    g7: LineSegment StartX=-49.19 StartY=28.75 StartZ=0 EndX=-49.19 EndY=25.75 EndZ=0
    g8: LineSegment StartX=-49.19 StartY=23 StartZ=0 EndX=-49.19 EndY=20 EndZ=0
    g9: LineSegment StartX=-49.19 StartY=17.25 StartZ=0 EndX=-49.19 EndY=14.25 EndZ=0
    g10: LineSegment StartX=-49.19 StartY=11.5 StartZ=0 EndX=-49.19 EndY=8.5 EndZ=0
    g11: LineSegment StartX=-49.19 StartY=5.75 StartZ=0 EndX=-49.19 EndY=2.75 EndZ=0
    g12: ArcOfCircle CenterX=-1.5 CenterY=67.75 CenterZ=0 NormalX=0 NormalY=0 NormalZ=1 AngleXU=0 Radius=1.5 StartAngle=4.71239 EndAngle=7.85398
    g13: ArcOfCircle CenterX=-1.5 CenterY=62 CenterZ=0 NormalX=0 NormalY=0 NormalZ=1 AngleXU=0 Radius=1.5 StartAngle=4.71239 EndAngle=7.85398
    g14: ArcOfCircle CenterX=-1.5 CenterY=56.25 CenterZ=0 NormalX=0 NormalY=0 NormalZ=1 AngleXU=0 Radius=1.5 StartAngle=4.71239 EndAngle=7.85398
    g15: ArcOfCircle CenterX=-11.49 CenterY=50.5 CenterZ=0 NormalX=0 NormalY=0 NormalZ=1 AngleXU=0 Radius=1.5 StartAngle=4.71239 EndAngle=7.85398
    g16: ArcOfCircle CenterX=-16.28 CenterY=44.75 CenterZ=0 NormalX=0 NormalY=0 NormalZ=1 AngleXU=0 Radius=1.5 StartAngle=4.71239 EndAngle=7.85398
    g17: ArcOfCircle CenterX=-18.2337 CenterY=39 CenterZ=0 NormalX=0 NormalY=0 NormalZ=1 AngleXU=0 Radius=1.5 StartAngle=4.71485 EndAngle=7.85398
    g18: ArcOfCircle CenterX=-16.2837 CenterY=27.25 CenterZ=0 NormalX=0 NormalY=0 NormalZ=1 AngleXU=0 Radius=1.5 StartAngle=4.71485 EndAngle=7.85398
    g19: ArcOfCircle CenterX=-18.2337 CenterY=33 CenterZ=0 NormalX=0 NormalY=0 NormalZ=1 AngleXU=0 Radius=1.5 StartAngle=4.71485 EndAngle=7.85398
    g20: ArcOfCircle CenterX=-11.49 CenterY=21.5 CenterZ=0 NormalX=0 NormalY=0 NormalZ=1 AngleXU=0 Radius=1.5 StartAngle=4.71239 EndAngle=7.85398
    g21: ArcOfCircle CenterX=-1.5 CenterY=4.25 CenterZ=0 NormalX=0 NormalY=0 NormalZ=1 AngleXU=0 Radius=1.5 StartAngle=4.71239 EndAngle=7.85398
    g22: ArcOfCircle CenterX=-1.5 CenterY=10 CenterZ=0 NormalX=0 NormalY=0 NormalZ=1 AngleXU=0 Radius=1.5 StartAngle=4.71239 EndAngle=7.85398
    g23: ArcOfCircle CenterX=-1.5 CenterY=15.75 CenterZ=0 NormalX=0 NormalY=0 NormalZ=1 AngleXU=0 Radius=1.5 StartAngle=4.71239 EndAngle=7.85398
    g24: LineSegment StartX=-49.19 StartY=69.25 StartZ=0 EndX=-1.5 EndY=69.25 EndZ=0
    g25: LineSegment StartX=-49.19 StartY=66.25 StartZ=0 EndX=-1.5 EndY=66.25 EndZ=0
    g26: LineSegment StartX=-49.19 StartY=63.5 StartZ=0 EndX=-1.5 EndY=63.5 EndZ=0
    g27: LineSegment StartX=-49.19 StartY=60.5 StartZ=0 EndX=-1.5 EndY=60.5 EndZ=0
    g28: LineSegment StartX=-49.19 StartY=57.75 StartZ=0 EndX=-1.5 EndY=57.75 EndZ=0
    g29: LineSegment StartX=-49.19 StartY=54.75 StartZ=0 EndX=-1.5 EndY=54.75 EndZ=0
    g30: LineSegment StartX=-49.19 StartY=52 StartZ=0 EndX=-11.49 EndY=52 EndZ=0
    g31: LineSegment StartX=-49.19 StartY=49 StartZ=0 EndX=-11.49 EndY=49 EndZ=0
    g32: LineSegment StartX=-49.19 StartY=46.25 StartZ=0 EndX=-16.28 EndY=46.25 EndZ=0
    g33: LineSegment StartX=-49.19 StartY=43.25 StartZ=0 EndX=-16.28 EndY=43.25 EndZ=0
    g34: LineSegment StartX=-49.19 StartY=40.5 StartZ=0 EndX=-18.2337 EndY=40.5 EndZ=0
    g35: LineSegment StartX=-49.19 StartY=37.5 StartZ=0 EndX=-18.23 EndY=37.5 EndZ=0
    g36: LineSegment StartX=-49.19 StartY=34.5 StartZ=0 EndX=-18.2337 EndY=34.5 EndZ=0
    g37: LineSegment StartX=-49.19 StartY=31.5 StartZ=0 EndX=-18.23 EndY=31.5 EndZ=0
    g38: LineSegment StartX=-49.19 StartY=28.75 StartZ=0 EndX=-16.2837 EndY=28.75 EndZ=0
    g39: LineSegment StartX=-49.19 StartY=25.75 StartZ=0 EndX=-16.28 EndY=25.75 EndZ=0
    g40: LineSegment StartX=-49.19 StartY=23 StartZ=0 EndX=-11.49 EndY=23 EndZ=0
    g41: LineSegment StartX=-49.19 StartY=20 StartZ=0 EndX=-11.49 EndY=20 EndZ=0
    g42: LineSegment StartX=-49.19 StartY=17.25 StartZ=0 EndX=-1.5 EndY=17.25 EndZ=0
    g43: LineSegment StartX=-49.19 StartY=14.25 StartZ=0 EndX=-1.5 EndY=14.25 EndZ=0
    g44: LineSegment StartX=-49.19 StartY=11.5 StartZ=0 EndX=-1.5 EndY=11.5 EndZ=0
    g45: LineSegment StartX=-49.19 StartY=8.5 StartZ=0 EndX=-1.5 EndY=8.5 EndZ=0
    g46: LineSegment StartX=-49.19 StartY=5.75 StartZ=0 EndX=-1.5 EndY=5.75 EndZ=0
    g47: LineSegment StartX=-49.19 StartY=2.75 StartZ=0 EndX=-1.5 EndY=2.75 EndZ=0
  constraints (120):
    c: Vertical(g0)
    c: Distance(g0) = 3
    c: Block(g0)
    c: Vertical(g1)
    c: Distance(g1) = 3
    c: Vertical(g2)
    c: Equal(g0,g2) = 3
    c: Block(g2)
    c: Vertical(g3)
    c: Equal(g1,g3) = 3
    c: Vertical(g4)
    c: Equal(g0,g4) = 3
    c: Block(g4)
    c: Vertical(g5)
    c: Equal(g1,g5) = 3
    c: Vertical(g6)
    c: Equal(g0,g6) = 3
    c: Block(g6)
    c: Vertical(g7)
    c: Equal(g1,g7) = 3
    c: Vertical(g8)
    c: Equal(g0,g8) = 3
    c: Block(g8)
    c: Vertical(g9)
    c: Equal(g1,g9) = 3
    c: Vertical(g10)
    c: Equal(g0,g10) = 3
    c: Block(g10)
    c: Vertical(g11)
    c: Equal(g1,g11) = 3
    c: Block(g12)
    c: Block(g13)
    c: Block(g14)
    c: Block(g15)
    c: Block(g16)
    c: Block(g17)
    c: Block(g18)
    c: Block(g19)
    c: Block(g20)
    c: Block(g21)
    c: Block(g22)
    c: Block(g23)
    c: Block(g11)
    c: Block(g9)
    c: Block(g7)
    c: Block(g5)
    c: Block(g3)
    c: Block(g1)
    c: Coincident(g24,g0)
    c: Coincident(g24,g12)
    c: Horizontal(g24)
    c: Coincident(g25,g0)
    c: Coincident(g25,g12)
    c: Horizontal(g25)
    c: Coincident(g26,g1)
    c: Coincident(g26,g13)
    c: Horizontal(g26)
    c: Coincident(g27,g1)
    c: Coincident(g27,g13)
    c: Horizontal(g27)
    c: Coincident(g28,g2)
    c: Coincident(g28,g14)
    c: Horizontal(g28)
    c: Coincident(g29,g2)
    c: Coincident(g29,g14)
    c: Horizontal(g29)
    c: Coincident(g30,g3)
    c: Coincident(g30,g15)
    c: Horizontal(g30)
    c: Coincident(g31,g3)
    c: Coincident(g31,g15)
    c: Horizontal(g31)
    c: Coincident(g32,g4)
    c: Coincident(g32,g16)
    c: Horizontal(g32)
    c: Coincident(g33,g4)
    c: Coincident(g33,g16)
    c: Horizontal(g33)
    c: Coincident(g34,g5)
    c: Coincident(g34,g17)
    c: Horizontal(g34)
    c: Coincident(g35,g5)
    c: Coincident(g35,g17)
    c: Horizontal(g35)
    c: Coincident(g36,g6)
    c: Coincident(g36,g19)
    c: Horizontal(g36)
    c: Coincident(g37,g6)
    c: Coincident(g37,g19)
    c: Horizontal(g37)
    c: Coincident(g38,g7)
    c: Coincident(g38,g18)
    c: Horizontal(g38)
    c: Coincident(g39,g7)
    c: Coincident(g39,g18)
    c: Horizontal(g39)
    c: Coincident(g40,g8)
    c: Coincident(g40,g20)
    c: Horizontal(g40)
    c: Coincident(g41,g8)
    c: Coincident(g41,g20)
    c: Horizontal(g41)
    c: Coincident(g42,g9)
    c: Coincident(g42,g23)
    c: Horizontal(g42)
    c: Coincident(g43,g9)
    c: Coincident(g43,g23)
    c: Horizontal(g43)
    c: Coincident(g44,g10)
    c: Coincident(g44,g22)
    c: Horizontal(g44)
    c: Coincident(g45,g10)
    c: Coincident(g45,g22)
    c: Horizontal(g45)
    c: Coincident(g46,g11)
    c: Coincident(g46,g21)
    c: Horizontal(g46)
    c: Coincident(g47,g11)
    c: Coincident(g47,g21)
    c: Horizontal(g47)
FEATURE [Part::Extrusion] Extrude042
  Base = -> Sketch051
  Dir = (1,-2e-16,2e-16)
  DirMode = 2
  FaceMakerClass = Part::FaceMakerBullseye
  LengthFwd = 19
  LengthRev = 0
  Placement = pos=(-19,0,0) rot=(0,0,1;0rad)
  Solid = true
  Symmetric = false
FEATURE [Part::Fillet] Fillet035  label="removeToCreateVentalationHoles"
  Base = -> Extrude042
  Edges = <same value as first occurrence — deduplicated (x6 in doc)>
  Placement = pos=(7,0,0) rot=(0,0,1;0rad)
FEATURE [Part::Cut] Cut038  label="top017"
  Base = -> Cut033
  Tool = -> Fillet035
FEATURE [Sketcher::SketchObject] Sketch052  label="bottomSketch001"
  FullyConstrained = true
  sketch-geometry (45):
    g0: LineSegment StartX=6.29999 StartY=8 StartZ=0 EndX=3.29999 EndY=8 EndZ=0
    g1: LineSegment StartX=3.29999 StartY=8 StartZ=0 EndX=3.29999 EndY=-6.03275e-07 EndZ=0
    g2: ArcOfCircle CenterX=8.29999 CenterY=5 CenterZ=0 NormalX=0 NormalY=0 NormalZ=1 AngleXU=0 Radius=2 StartAngle=3.14159 EndAngle=4.71239
    g3: LineSegment StartX=6.29999 StartY=8 StartZ=0 EndX=6.29999 EndY=5 EndZ=0
    g4: ArcOfCircle CenterX=105 CenterY=19 CenterZ=0 NormalX=0 NormalY=0 NormalZ=1 AngleXU=0 Radius=12.7 StartAngle=4.71239 EndAngle=5.94289
    g5-g11: Circle x7 (B-spline internal-alignment scaffolding for g12; pole/knot coordinates omitted)
    g12: BSplineCurve PolesCount=7 KnotsCount=5 Degree=3 IsPeriodic=0
    g13-g17: GeomPoint x5 (B-spline internal-alignment scaffolding for g12; pole/knot coordinates omitted)
    g18: ArcOfCircle CenterX=105 CenterY=19 CenterZ=0 NormalX=0 NormalY=0 NormalZ=1 AngleXU=0 Radius=15.7 StartAngle=5.81226 EndAngle=6.28319
    g19: BSplineCurve PolesCount=5 KnotsCount=3 Degree=3 IsPeriodic=0
    g20: LineSegment StartX=8.29999 StartY=3 StartZ=0 EndX=101.7 EndY=3 EndZ=0
    g21: LineSegment StartX=3.29999 StartY=-6.03275e-07 StartZ=0 EndX=105 EndY=-6.03275e-07 EndZ=0
    g22: LineSegment StartX=120.974 StartY=8.71251 StartZ=0 EndX=122.332 EndY=7.83778 EndZ=0
    g23: LineSegment StartX=105 StartY=-6.03274e-07 StartZ=0 EndX=113 EndY=-6.03274e-07 EndZ=0
    g24: ArcOfCircle CenterX=105 CenterY=19 CenterZ=0 NormalX=0 NormalY=0 NormalZ=1 AngleXU=0 Radius=20.6155 StartAngle=5.11091 EndAngle=5.71103
    g25: ArcOfCircle CenterX=117.7 CenterY=19 CenterZ=0 NormalX=0 NormalY=0 NormalZ=1 AngleXU=0 Radius=3 StartAngle=1.2e-15 EndAngle=2.10468
    g26: Circle CenterX=116.345 CenterY=16.3232 CenterZ=0 NormalX=0 NormalY=0 NormalZ=1 AngleXU=0 Radius=1
    g27: Circle CenterX=117.24 CenterY=15.7584 CenterZ=0 NormalX=0 NormalY=0 NormalZ=1 AngleXU=0 Radius=1
    g28: Circle CenterX=116.972 CenterY=14.7612 CenterZ=0 NormalX=0 NormalY=0 NormalZ=1 AngleXU=0 Radius=1
    g29: BSplineCurve PolesCount=3 KnotsCount=2 Degree=2 IsPeriodic=0
    g30: GeomPoint X=116.345 Y=16.3232 Z=0
    g31: GeomPoint X=116.972 Y=14.7612 Z=0
    g32: Circle CenterX=115.828 CenterY=17.157 CenterZ=0 NormalX=0 NormalY=0 NormalZ=1 AngleXU=0 Radius=1
    g33: Circle CenterX=115.841 CenterY=16.639 CenterZ=0 NormalX=0 NormalY=0 NormalZ=1 AngleXU=0 Radius=1
    g34: Circle CenterX=116.345 CenterY=16.3232 CenterZ=0 NormalX=0 NormalY=0 NormalZ=1 AngleXU=0 Radius=1
    g35: BSplineCurve PolesCount=3 KnotsCount=2 Degree=2 IsPeriodic=0
    g36: GeomPoint X=115.828 Y=17.157 Z=0
    g37: GeomPoint X=116.345 Y=16.3232 Z=0
    g38: LineSegment StartX=115.828 StartY=17.157 StartZ=0 EndX=115.828 EndY=20.8307 EndZ=0
    g39: Circle CenterX=115.828 CenterY=20.8307 CenterZ=0 NormalX=0 NormalY=0 NormalZ=1 AngleXU=0 Radius=1
    g40: Circle CenterX=115.831 CenterY=21.3396 CenterZ=0 NormalX=0 NormalY=0 NormalZ=1 AngleXU=0 Radius=1
    g41: Circle CenterX=116.173 CenterY=21.5825 CenterZ=0 NormalX=0 NormalY=0 NormalZ=1 AngleXU=0 Radius=1
    g42: BSplineCurve PolesCount=3 KnotsCount=2 Degree=2 IsPeriodic=0
    g43: GeomPoint X=115.828 Y=20.8307 Z=0
    g44: GeomPoint X=116.173 Y=21.5825 Z=0
  constraints (70):
    c: Horizontal(g0)
    c: Distance(g0) = 3
    c: Coincident(g1,g0)
    c: Vertical(g1)
    c: Block(g2)
    c: Block(g0)
    c: Coincident(g3,g0)
    c: Coincident(g3,g2)
    c: Vertical(g3)
    c: Block(g1)
    c: Block(g4)
    c: Coincident(g19,g4)
    c: Block(g19)
    c: Equal(g5, g6-g11) x6
    c: InternalAlignment(g5-g11 -> g12) x7
    c: InternalAlignment(g13-g17 -> g12) x5
    c: Block(g12)
    c: Coincident(g18,g12)
    c: Block(g18)
    c: Coincident(g20,g2)
    c: Coincident(g20,g19)
    c: Horizontal(g20)
    c: Distance(g20) = 93.4
    c: Coincident(g21,g1)
    c: Horizontal(g21)
    c: Distance(g21) = 101.7
    c: Horizontal(g23)
    c: Distance(g23) = 8
    c: Coincident(g24,g23)
    c: Block(g23)
    c: Coincident(g22,g24)
    c: Block(g24)
    c: Block(g22)
    c: Distance(g22) = 1.61553
    c: Coincident(g25,g18)
    c: Block(g25)
    c: Weight(g26) = 1
    c: Equal(g26,g27)
    c: Equal(g26,g28)
    c: Coincident(g29,g4)
    c: InternalAlignment(g26,g29)
    c: InternalAlignment(g27,g29)
    c: InternalAlignment(g28,g29)
    c: InternalAlignment(g30,g29)
    c: InternalAlignment(g31,g29)
    c: Block(g29)
    c: Weight(g32) = 1
    c: Equal(g32,g33)
    c: Equal(g32,g34)
    c: Coincident(g35,g29)
    c: InternalAlignment(g32,g35)
    c: InternalAlignment(g33,g35)
    c: InternalAlignment(g34,g35)
    c: InternalAlignment(g36,g35)
    c: InternalAlignment(g37,g35)
    c: Block(g35)
    c: Coincident(g38,g35)
    c: Vertical(g38)
    c: Block(g38)
    c: Coincident(g42,g38)
    c: Weight(g39) = 1
    c: Equal(g39,g40)
    c: Equal(g39,g41)
    c: Coincident(g42,g25)
    c: InternalAlignment(g39,g42)
    c: InternalAlignment(g40,g42)
    c: InternalAlignment(g41,g42)
    c: InternalAlignment(g43,g42)
    c: InternalAlignment(g44,g42)
    c: Block(g42)
FEATURE [Part::Extrusion] Extrude043  label="bottom010"
  Base = -> Sketch052
  Dir = (0,0,1)
  DirMode = 2
  FaceMakerClass = Part::FaceMakerBullseye
  LengthFwd = 71.4
  LengthRev = 0
  Placement = pos=(0,0,0.3) rot=(0,0,1;0rad)
  Solid = true
  Symmetric = false
FEATURE [Sketcher::SketchObject] Sketch053  label="topSketch013"
  FullyConstrained = true
  sketch-geometry (22):
    g0: LineSegment StartX=5.21097e-06 StartY=3 StartZ=0 EndX=5.21097e-06 EndY=19 EndZ=0
    g1: ArcOfCircle CenterX=19 CenterY=19 CenterZ=0 NormalX=0 NormalY=0 NormalZ=1 AngleXU=0 Radius=19 StartAngle=1.5708 EndAngle=3.14159
    g2: ArcOfCircle CenterX=19 CenterY=19 CenterZ=0 NormalX=0 NormalY=0 NormalZ=1 AngleXU=0 Radius=16 StartAngle=1.5708 EndAngle=3.14159
    g3: LineSegment StartX=114 StartY=35 StartZ=0 EndX=19 EndY=35 EndZ=0
    g4: LineSegment StartX=5.21097e-06 StartY=3 StartZ=0 EndX=5.21097e-06 EndY=0 EndZ=0
    g5: LineSegment StartX=3 StartY=0 StartZ=0 EndX=5.21097e-06 EndY=0 EndZ=0
    g6: LineSegment StartX=3 StartY=19 StartZ=0 EndX=3 EndY=0 EndZ=0
    g7: LineSegment StartX=19 StartY=38 StartZ=0 EndX=124 EndY=38 EndZ=0
    g8: Circle CenterX=119 CenterY=35 CenterZ=0 NormalX=0 NormalY=0 NormalZ=1 AngleXU=0 Radius=1
    g9: Circle CenterX=121 CenterY=35 CenterZ=0 NormalX=0 NormalY=0 NormalZ=1 AngleXU=0 Radius=1
    g10: Circle CenterX=121 CenterY=33 CenterZ=0 NormalX=0 NormalY=0 NormalZ=1 AngleXU=0 Radius=1
    g11: BSplineCurve PolesCount=3 KnotsCount=2 Degree=2 IsPeriodic=0
    g12: GeomPoint X=119 Y=35 Z=0
    g13: GeomPoint X=121 Y=33 Z=0
    g14: LineSegment StartX=119 StartY=35 StartZ=0 EndX=114 EndY=35 EndZ=0
    g15: ArcOfCircle CenterX=105 CenterY=19 CenterZ=0 NormalX=0 NormalY=0 NormalZ=1 AngleXU=0 Radius=16 StartAngle=5.60905 EndAngle=6.28319
    g16: LineSegment StartX=121 StartY=33 StartZ=0 EndX=121 EndY=19 EndZ=0
    g17: LineSegment StartX=117.5 StartY=9.01251 StartZ=0 EndX=121.163 EndY=9.0125 EndZ=0
    g18: ArcOfCircle CenterX=105 CenterY=19 CenterZ=0 NormalX=0 NormalY=0 NormalZ=1 AngleXU=0 Radius=20.6155 StartAngle=5.7297 EndAngle=6.28319
    g19: LineSegment StartX=121.163 StartY=9.0125 StartZ=0 EndX=122.538 EndY=8.16329 EndZ=0
    g20: LineSegment StartX=124 StartY=38 StartZ=0 EndX=125.616 EndY=38 EndZ=0
    g21: LineSegment StartX=125.616 StartY=19 StartZ=0 EndX=125.616 EndY=38 EndZ=0
  constraints (50):
    c: Vertical(g0)
    c: Block(g0)
    c: Coincident(g1,g0)
    c: Block(g1)
    c: Coincident(g2,g1)
    c: Block(g2)
    c: Coincident(g3,g2)
    c: Horizontal(g3)
    c: Tangent(g3,g2)
    c: Coincident(g4,g0)
    c: Distance(g4) = 3
    c: Vertical(g4)
    c: Coincident(g5,g4)
    c: Horizontal(g5)
    c: Coincident(g6,g2)
    c: Coincident(g6,g5)
    c: Vertical(g6)
    c: Horizontal(g7)
    c: Distance(g7) = 105
    c: Coincident(g7,g1)
    c: Block(g3)
    c: Weight(g8) = 1
    c: Equal(g8,g9)
    c: Equal(g8,g10)
    c: InternalAlignment(g8,g11)
    c: InternalAlignment(g9,g11)
    c: InternalAlignment(g10,g11)
    c: InternalAlignment(g12,g11)
    c: InternalAlignment(g13,g11)
    c: Block(g11)
    c: Coincident(g14,g11)
    c: Coincident(g14,g3)
    c: Horizontal(g14)
    c: Block(g15)
    c: Coincident(g16,g11)
    c: Coincident(g16,g15)
    c: Vertical(g16)
    c: Distance(g16) = 14
    c: Coincident(g17,g15)
    c: Block(g18)
    c: Coincident(g19,g18)
    c: Coincident(g20,g7)
    c: Horizontal(g20)
    c: Vertical(g21)
    c: Coincident(g20,g21)
    c: Block(g20)
    c: Block(g21)
    c: Block(g19)
    c: Block(g17)
    c: Distance(g20) = 1.61553
FEATURE [Part::Extrusion] Extrude044
  Base = -> Sketch053
  Dir = (0,0,1)
  DirMode = 2
  FaceMakerClass = Part::FaceMakerBullseye
  LengthFwd = 72
  LengthRev = 0
  Solid = true
  Symmetric = false
FEATURE [Part::Fillet] Fillet036  label="top018"
  Base = -> Extrude044
  Edges = 1 edges r=2: [Edge41]
FEATURE [Sketcher::SketchObject] Sketch054
  FullyConstrained = false
  Placement = pos=(0,0,0) rot=(1,0,0;1.5708rad)
  sketch-geometry (24):
    g0: ArcOfCircle CenterX=-4 CenterY=-10.5 CenterZ=0 NormalX=0 NormalY=0 NormalZ=1 AngleXU=0 Radius=1.5 StartAngle=6e-16 EndAngle=3.14159
    g1: ArcOfCircle CenterX=-34.2 CenterY=-10.5 CenterZ=0 NormalX=0 NormalY=0 NormalZ=1 AngleXU=0 Radius=1.5 StartAngle=0 EndAngle=3.14159
    g2: ArcOfCircle CenterX=-34.2 CenterY=-27.7 CenterZ=0 NormalX=0 NormalY=0 NormalZ=1 AngleXU=0 Radius=1.5 StartAngle=3.14159 EndAngle=6.28319
    g3: ArcOfCircle CenterX=-4 CenterY=-27.7 CenterZ=0 NormalX=0 NormalY=0 NormalZ=1 AngleXU=0 Radius=1.5 StartAngle=3.1416 EndAngle=6.28319
    g4: ArcOfCircle CenterX=-10 CenterY=-4.3 CenterZ=0 NormalX=0 NormalY=0 NormalZ=1 AngleXU=0 Radius=1.5 StartAngle=2e-16 EndAngle=3.14159
    g5: ArcOfCircle CenterX=-16.1 CenterY=-1.8 CenterZ=0 NormalX=0 NormalY=0 NormalZ=1 AngleXU=0 Radius=1.5 StartAngle=5e-16 EndAngle=3.14159
    g6: ArcOfCircle CenterX=-22.1 CenterY=-1.8 CenterZ=0 NormalX=0 NormalY=0 NormalZ=1 AngleXU=0 Radius=1.5 StartAngle=5e-16 EndAngle=3.14159
    g7: ArcOfCircle CenterX=-28.2 CenterY=-4.3 CenterZ=0 NormalX=0 NormalY=0 NormalZ=1 AngleXU=0 Radius=1.5 StartAngle=2e-16 EndAngle=3.14159
    g8: ArcOfCircle CenterX=-10 CenterY=-33.9 CenterZ=0 NormalX=0 NormalY=0 NormalZ=1 AngleXU=0 Radius=1.5 StartAngle=3.14159 EndAngle=6.28319
    g9: ArcOfCircle CenterX=-16.1 CenterY=-36.4 CenterZ=0 NormalX=0 NormalY=0 NormalZ=1 AngleXU=0 Radius=1.5 StartAngle=3.14159 EndAngle=6.28319
    g10: ArcOfCircle CenterX=-22.1 CenterY=-36.4 CenterZ=0 NormalX=0 NormalY=0 NormalZ=1 AngleXU=0 Radius=1.5 StartAngle=3.14159 EndAngle=6.28319
    g11: ArcOfCircle CenterX=-28.2 CenterY=-33.9 CenterZ=0 NormalX=0 NormalY=0 NormalZ=1 AngleXU=0 Radius=1.5 StartAngle=3.14159 EndAngle=6.28319
    g12: LineSegment StartX=-35.7 StartY=-10.5 StartZ=0 EndX=-35.7 EndY=-27.7 EndZ=0
    g13: LineSegment StartX=-32.7 StartY=-10.5 StartZ=0 EndX=-32.7 EndY=-27.7 EndZ=0
    g14: LineSegment StartX=-29.7 StartY=-33.9 StartZ=0 EndX=-29.7 EndY=-4.3 EndZ=0
    g15: LineSegment StartX=-26.7 StartY=-33.9 StartZ=0 EndX=-26.7 EndY=-4.3 EndZ=0
    g16: LineSegment StartX=-2.5 StartY=-10.5 StartZ=0 EndX=-2.5 EndY=-27.7 EndZ=0
    g17: LineSegment StartX=-8.5 StartY=-4.3 StartZ=0 EndX=-8.5 EndY=-33.9 EndZ=0
    g18: LineSegment StartX=-5.5 StartY=-10.5 StartZ=0 EndX=-5.5 EndY=-27.7 EndZ=0
    g19: LineSegment StartX=-11.5 StartY=-4.3 StartZ=0 EndX=-11.5 EndY=-33.9 EndZ=0
    g20: LineSegment StartX=-14.6 StartY=-1.8 StartZ=0 EndX=-14.6 EndY=-36.4 EndZ=0
    g21: LineSegment StartX=-17.6 StartY=-1.8 StartZ=0 EndX=-17.6 EndY=-36.4 EndZ=0
    g22: LineSegment StartX=-20.6 StartY=-36.4 StartZ=0 EndX=-20.6 EndY=-1.8 EndZ=0
    g23: LineSegment StartX=-23.6 StartY=-1.8 StartZ=0 EndX=-23.6 EndY=-36.4 EndZ=0
  constraints (48):
    c: Block(g0)
    c: Block(g1)
    c: Block(g2)
    c: Block(g3)
    c: Block(g4)
    c: Block(g5)
    c: Block(g6)
    c: Block(g7)
    c: Block(g8)
    c: Block(g9)
    c: Block(g10)
    c: Block(g11)
    c: Coincident(g12,g1)
    c: Coincident(g12,g2)
    c: Vertical(g12)
    c: Coincident(g13,g1)
    c: Coincident(g13,g2)
    c: Vertical(g13)
    c: Coincident(g14,g11)
    c: Coincident(g14,g7)
    c: Vertical(g14)
    c: Coincident(g15,g11)
    c: Coincident(g15,g7)
    c: Vertical(g15)
    c: Coincident(g16,g0)
    c: Coincident(g16,g3)
    c: Vertical(g16)
    c: Coincident(g17,g4)
    c: Coincident(g17,g8)
    c: Vertical(g17)
    c: Coincident(g18,g0)
    c: Coincident(g18,g3)
    c: Vertical(g18)
    c: Coincident(g19,g4)
    c: Coincident(g19,g8)
    c: Vertical(g19)
    c: Coincident(g20,g5)
    c: Coincident(g20,g9)
    c: Vertical(g20)
    c: Coincident(g21,g5)
    c: Coincident(g21,g9)
    c: Vertical(g21)
    c: Coincident(g22,g10)
    c: Coincident(g22,g6)
    c: Vertical(g22)
    c: Coincident(g23,g6)
    c: Coincident(g23,g10)
    c: Vertical(g23)
FEATURE [Part::Extrusion] Extrude045  label="removeToCreateFanGrillHoles003"
  Base = -> Sketch054
  Dir = (0,-1,6e-16)
  DirMode = 2
  FaceMakerClass = Part::FaceMakerBullseye
  LengthFwd = 10
  LengthRev = 0
  Placement = pos=(65.4,44,54.82) rot=(0,0,1;0rad)
  Solid = true
  Symmetric = false
FEATURE [Part::Feature] Face105 .. Face108  x4 (patterned run collapsed; names and placements below)
  shape: bbox 3.5 x 17.8 x 2e-07 mm, 1 faces, 0 solids (baked)
FEATURE [Part::Revolution] Revolve113  label="removeToCreateScrewAndThreadedInsertHole041"
  Angle = 360
  Axis = (0,1,0)
  Base = (0,0,0)
  FaceMakerClass = Part::FaceMakerBullseye
  Placement = pos=(62.3,30.3,19.7) rot=(0,0,1;0rad)
  Solid = false
  Source = -> Face105
  Symmetric = false
FEATURE [Part::Revolution] Revolve114  label="removeToCreateScrewAndThreadedInsertHole042"
  Angle = 360
  Axis = (0,1,0)
  Base = (0,0,0)
  FaceMakerClass = Part::FaceMakerBullseye
  Placement = pos=(62.3,30.3,51.7) rot=(0,0,1;0rad)
  Solid = false
  Source = -> Face106
  Symmetric = false
FEATURE [Part::Revolution] Revolve115  label="removeToCreateScrewAndThreadedInsertHole043"
  Angle = 360
  Axis = (0,1,0)
  Base = (0,0,0)
  FaceMakerClass = Part::FaceMakerBullseye
  Placement = pos=(30.3,30.3,19.7) rot=(0,0,1;0rad)
  Solid = false
  Source = -> Face107
  Symmetric = false
FEATURE [Part::Revolution] Revolve116  label="removeToCreateScrewAndThreadedInsertHole044"
  Angle = 360
  Axis = (0,1,0)
  Base = (0,0,0)
  FaceMakerClass = Part::FaceMakerBullseye
  Placement = pos=(30.3,30.3,51.7) rot=(0,0,1;0rad)
  Solid = false
  Source = -> Face108
  Symmetric = false
FEATURE [Part::MultiFuse] Fusion083  label="createThreadedInsertHolesForFan004"
  Shapes = -> [Revolve113,Revolve114,Revolve115,Revolve116]
FEATURE [Part::Box] Box024  label="removeToCreteHoleForPlugHousing026"
  AttacherType = Attacher::AttachEngine3D
  Height = 28.6
  Length = 10
  Placement = pos=(-2,0,21.7) rot=(0,0,1;0rad)
  Width = 19
FEATURE [Part::Cylinder] Cylinder038  label="removeToCreteHoleForPlugHousing027"
  Angle = 360
  AttacherType = Attacher::AttachEngine3D
  Height = 20
  Placement = pos=(-2,19,36) rot=(0,1,0;1.5708rad)
  Radius = 14.3
FEATURE [Part::MultiFuse] Fusion084  label="removeToCreteHoleForPlugHousing028"
  Shapes = -> [Box024,Cylinder038]
FEATURE [Part::Cylinder] Cylinder039
  Angle = 360
  AttacherType = Attacher::AttachEngine3D
  Height = 20
  Placement = pos=(0,0,36.15) rot=(0,0,1;0rad)
  Radius = 14.3
FEATURE [Part::Cylinder] Cylinder040
  Angle = 360
  AttacherType = Attacher::AttachEngine3D
  Height = 10
  Placement = pos=(0,0,36.15) rot=(0,0,1;0rad)
  Radius = 4
FEATURE [Part::Box] Box025  label="removeToCreteHoleForPlugHousing030"
  AttacherType = Attacher::AttachEngine3D
  Height = 28.6
  Length = 20
  Placement = pos=(106.15,0,21.7) rot=(0,0,1;0rad)
  Width = 19
FEATURE [Part::MultiFuse] Fusion086  label="removeToCreteHoleForPlugHousing031"
  Placement = pos=(70,19,36) rot=(0,1,0;1.5708rad)
  Shapes = -> [Cylinder039,Cylinder040]
FEATURE [Part::MultiFuse] Fusion085  label="removeToCreteHoleForPlugHousing029"
  Shapes = -> [Box025,Fusion086]
FEATURE [Sketcher::SketchObject] Sketch055
  FullyConstrained = true
  Placement = pos=(117,19,0) rot=(0.57735,0.57735,0.57735;2.0944rad)
  sketch-geometry (48):
    g0: LineSegment StartX=-49.19 StartY=69.25 StartZ=0 EndX=-49.19 EndY=66.25 EndZ=0
    g1: LineSegment StartX=-49.19 StartY=63.5 StartZ=0 EndX=-49.19 EndY=60.5 EndZ=0
    g2: LineSegment StartX=-49.19 StartY=57.75 StartZ=0 EndX=-49.19 EndY=54.75 EndZ=0
    g3: LineSegment StartX=-49.19 StartY=52 StartZ=0 EndX=-49.19 EndY=49 EndZ=0
    g4: LineSegment StartX=-49.19 StartY=46.25 StartZ=0 EndX=-49.19 EndY=43.25 EndZ=0
    g5: LineSegment StartX=-49.19 StartY=40.5 StartZ=0 EndX=-49.19 EndY=37.5 EndZ=0
    g6: LineSegment StartX=-49.19 StartY=34.5 StartZ=0 EndX=-49.19 EndY=31.5 EndZ=0
    g7: LineSegment StartX=-49.19 StartY=28.75 StartZ=0 EndX=-49.19 EndY=25.75 EndZ=0
    g8: LineSegment StartX=-49.19 StartY=23 StartZ=0 EndX=-49.19 EndY=20 EndZ=0
    g9: LineSegment StartX=-49.19 StartY=17.25 StartZ=0 EndX=-49.19 EndY=14.25 EndZ=0
    g10: LineSegment StartX=-49.19 StartY=11.5 StartZ=0 EndX=-49.19 EndY=8.5 EndZ=0
    g11: LineSegment StartX=-49.19 StartY=5.75 StartZ=0 EndX=-49.19 EndY=2.75 EndZ=0
    g12: ArcOfCircle CenterX=-1.5 CenterY=67.75 CenterZ=0 NormalX=0 NormalY=0 NormalZ=1 AngleXU=0 Radius=1.5 StartAngle=4.71239 EndAngle=7.85398
    g13: ArcOfCircle CenterX=-1.5 CenterY=62 CenterZ=0 NormalX=0 NormalY=0 NormalZ=1 AngleXU=0 Radius=1.5 StartAngle=4.71239 EndAngle=7.85398
    g14: ArcOfCircle CenterX=-1.5 CenterY=56.25 CenterZ=0 NormalX=0 NormalY=0 NormalZ=1 AngleXU=0 Radius=1.5 StartAngle=4.71239 EndAngle=7.85398
    g15: ArcOfCircle CenterX=-11.49 CenterY=50.5 CenterZ=0 NormalX=0 NormalY=0 NormalZ=1 AngleXU=0 Radius=1.5 StartAngle=4.71239 EndAngle=7.85398
    g16: ArcOfCircle CenterX=-16.28 CenterY=44.75 CenterZ=0 NormalX=0 NormalY=0 NormalZ=1 AngleXU=0 Radius=1.5 StartAngle=4.71239 EndAngle=7.85398
    g17: ArcOfCircle CenterX=-18.2337 CenterY=39 CenterZ=0 NormalX=0 NormalY=0 NormalZ=1 AngleXU=0 Radius=1.5 StartAngle=4.71485 EndAngle=7.85398
    g18: ArcOfCircle CenterX=-16.2837 CenterY=27.25 CenterZ=0 NormalX=0 NormalY=0 NormalZ=1 AngleXU=0 Radius=1.5 StartAngle=4.71485 EndAngle=7.85398
    g19: ArcOfCircle CenterX=-18.2337 CenterY=33 CenterZ=0 NormalX=0 NormalY=0 NormalZ=1 AngleXU=0 Radius=1.5 StartAngle=4.71485 EndAngle=7.85398
    g20: ArcOfCircle CenterX=-11.49 CenterY=21.5 CenterZ=0 NormalX=0 NormalY=0 NormalZ=1 AngleXU=0 Radius=1.5 StartAngle=4.71239 EndAngle=7.85398
    g21: ArcOfCircle CenterX=-1.5 CenterY=4.25 CenterZ=0 NormalX=0 NormalY=0 NormalZ=1 AngleXU=0 Radius=1.5 StartAngle=4.71239 EndAngle=7.85398
    g22: ArcOfCircle CenterX=-1.5 CenterY=10 CenterZ=0 NormalX=0 NormalY=0 NormalZ=1 AngleXU=0 Radius=1.5 StartAngle=4.71239 EndAngle=7.85398
    g23: ArcOfCircle CenterX=-1.5 CenterY=15.75 CenterZ=0 NormalX=0 NormalY=0 NormalZ=1 AngleXU=0 Radius=1.5 StartAngle=4.71239 EndAngle=7.85398
    g24: LineSegment StartX=-49.19 StartY=69.25 StartZ=0 EndX=-1.5 EndY=69.25 EndZ=0
    g25: LineSegment StartX=-49.19 StartY=66.25 StartZ=0 EndX=-1.5 EndY=66.25 EndZ=0
    g26: LineSegment StartX=-49.19 StartY=63.5 StartZ=0 EndX=-1.5 EndY=63.5 EndZ=0
    g27: LineSegment StartX=-49.19 StartY=60.5 StartZ=0 EndX=-1.5 EndY=60.5 EndZ=0
    g28: LineSegment StartX=-49.19 StartY=57.75 StartZ=0 EndX=-1.5 EndY=57.75 EndZ=0
    g29: LineSegment StartX=-49.19 StartY=54.75 StartZ=0 EndX=-1.5 EndY=54.75 EndZ=0
    g30: LineSegment StartX=-49.19 StartY=52 StartZ=0 EndX=-11.49 EndY=52 EndZ=0
    g31: LineSegment StartX=-49.19 StartY=49 StartZ=0 EndX=-11.49 EndY=49 EndZ=0
    g32: LineSegment StartX=-49.19 StartY=46.25 StartZ=0 EndX=-16.28 EndY=46.25 EndZ=0
    g33: LineSegment StartX=-49.19 StartY=43.25 StartZ=0 EndX=-16.28 EndY=43.25 EndZ=0
    g34: LineSegment StartX=-49.19 StartY=40.5 StartZ=0 EndX=-18.2337 EndY=40.5 EndZ=0
    g35: LineSegment StartX=-49.19 StartY=37.5 StartZ=0 EndX=-18.23 EndY=37.5 EndZ=0
    g36: LineSegment StartX=-49.19 StartY=34.5 StartZ=0 EndX=-18.2337 EndY=34.5 EndZ=0
    g37: LineSegment StartX=-49.19 StartY=31.5 StartZ=0 EndX=-18.23 EndY=31.5 EndZ=0
    g38: LineSegment StartX=-49.19 StartY=28.75 StartZ=0 EndX=-16.2837 EndY=28.75 EndZ=0
    g39: LineSegment StartX=-49.19 StartY=25.75 StartZ=0 EndX=-16.28 EndY=25.75 EndZ=0
    g40: LineSegment StartX=-49.19 StartY=23 StartZ=0 EndX=-11.49 EndY=23 EndZ=0
    g41: LineSegment StartX=-49.19 StartY=20 StartZ=0 EndX=-11.49 EndY=20 EndZ=0
    g42: LineSegment StartX=-49.19 StartY=17.25 StartZ=0 EndX=-1.5 EndY=17.25 EndZ=0
    g43: LineSegment StartX=-49.19 StartY=14.25 StartZ=0 EndX=-1.5 EndY=14.25 EndZ=0
    g44: LineSegment StartX=-49.19 StartY=11.5 StartZ=0 EndX=-1.5 EndY=11.5 EndZ=0
    g45: LineSegment StartX=-49.19 StartY=8.5 StartZ=0 EndX=-1.5 EndY=8.5 EndZ=0
    g46: LineSegment StartX=-49.19 StartY=5.75 StartZ=0 EndX=-1.5 EndY=5.75 EndZ=0
    g47: LineSegment StartX=-49.19 StartY=2.75 StartZ=0 EndX=-1.5 EndY=2.75 EndZ=0
  constraints (120):
    c: Vertical(g0)
    c: Distance(g0) = 3
    c: Block(g0)
    c: Vertical(g1)
    c: Distance(g1) = 3
    c: Vertical(g2)
    c: Equal(g0,g2) = 3
    c: Block(g2)
    c: Vertical(g3)
    c: Equal(g1,g3) = 3
    c: Vertical(g4)
    c: Equal(g0,g4) = 3
    c: Block(g4)
    c: Vertical(g5)
    c: Equal(g1,g5) = 3
    c: Vertical(g6)
    c: Equal(g0,g6) = 3
    c: Block(g6)
    c: Vertical(g7)
    c: Equal(g1,g7) = 3
    c: Vertical(g8)
    c: Equal(g0,g8) = 3
    c: Block(g8)
    c: Vertical(g9)
    c: Equal(g1,g9) = 3
    c: Vertical(g10)
    c: Equal(g0,g10) = 3
    c: Block(g10)
    c: Vertical(g11)
    c: Equal(g1,g11) = 3
    c: Block(g12)
    c: Block(g13)
    c: Block(g14)
    c: Block(g15)
    c: Block(g16)
    c: Block(g17)
    c: Block(g18)
    c: Block(g19)
    c: Block(g20)
    c: Block(g21)
    c: Block(g22)
    c: Block(g23)
    c: Block(g11)
    c: Block(g9)
    c: Block(g7)
    c: Block(g5)
    c: Block(g3)
    c: Block(g1)
    c: Coincident(g24,g0)
    c: Coincident(g24,g12)
    c: Horizontal(g24)
    c: Coincident(g25,g0)
    c: Coincident(g25,g12)
    c: Horizontal(g25)
    c: Coincident(g26,g1)
    c: Coincident(g26,g13)
    c: Horizontal(g26)
    c: Coincident(g27,g1)
    c: Coincident(g27,g13)
    c: Horizontal(g27)
    c: Coincident(g28,g2)
    c: Coincident(g28,g14)
    c: Horizontal(g28)
    c: Coincident(g29,g2)
    c: Coincident(g29,g14)
    c: Horizontal(g29)
    c: Coincident(g30,g3)
    c: Coincident(g30,g15)
    c: Horizontal(g30)
    c: Coincident(g31,g3)
    c: Coincident(g31,g15)
    c: Horizontal(g31)
    c: Coincident(g32,g4)
    c: Coincident(g32,g16)
    c: Horizontal(g32)
    c: Coincident(g33,g4)
    c: Coincident(g33,g16)
    c: Horizontal(g33)
    c: Coincident(g34,g5)
    c: Coincident(g34,g17)
    c: Horizontal(g34)
    c: Coincident(g35,g5)
    c: Coincident(g35,g17)
    c: Horizontal(g35)
    c: Coincident(g36,g6)
    c: Coincident(g36,g19)
    c: Horizontal(g36)
    c: Coincident(g37,g6)
    c: Coincident(g37,g19)
    c: Horizontal(g37)
    c: Coincident(g38,g7)
    c: Coincident(g38,g18)
    c: Horizontal(g38)
    c: Coincident(g39,g7)
    c: Coincident(g39,g18)
    c: Horizontal(g39)
    c: Coincident(g40,g8)
    c: Coincident(g40,g20)
    c: Horizontal(g40)
    c: Coincident(g41,g8)
    c: Coincident(g41,g20)
    c: Horizontal(g41)
    c: Coincident(g42,g9)
    c: Coincident(g42,g23)
    c: Horizontal(g42)
    c: Coincident(g43,g9)
    c: Coincident(g43,g23)
    c: Horizontal(g43)
    c: Coincident(g44,g10)
    c: Coincident(g44,g22)
    c: Horizontal(g44)
    c: Coincident(g45,g10)
    c: Coincident(g45,g22)
    c: Horizontal(g45)
    c: Coincident(g46,g11)
    c: Coincident(g46,g21)
    c: Horizontal(g46)
    c: Coincident(g47,g11)
    c: Coincident(g47,g21)
    c: Horizontal(g47)
FEATURE [Part::Extrusion] Extrude046
  Base = -> Sketch055
  Dir = (1,0,0)
  DirMode = 2
  FaceMakerClass = Part::FaceMakerBullseye
  LengthFwd = 23
  LengthRev = 0
  Placement = pos=(-19,0,0) rot=(0,0,1;0rad)
  Solid = true
  Symmetric = false
FEATURE [Part::Fillet] Fillet038  label="removeToCreateVentalationHoles001"
  Base = -> Extrude046
  Edges = <same value as first occurrence — deduplicated (x6 in doc)>
  Placement = pos=(7,0,0) rot=(0,0,1;0rad)
FEATURE [Sketcher::SketchObject] Sketch056  label="topSketch014"
  FullyConstrained = true
  sketch-geometry (22):
    g0: LineSegment StartX=5.21097e-06 StartY=3 StartZ=0 EndX=5.21097e-06 EndY=19 EndZ=0
    g1: ArcOfCircle CenterX=19 CenterY=19 CenterZ=0 NormalX=0 NormalY=0 NormalZ=1 AngleXU=0 Radius=19 StartAngle=1.5708 EndAngle=3.14159
    g2: ArcOfCircle CenterX=19 CenterY=19 CenterZ=0 NormalX=0 NormalY=0 NormalZ=1 AngleXU=0 Radius=16 StartAngle=1.5708 EndAngle=3.14159
    g3: LineSegment StartX=114 StartY=35 StartZ=0 EndX=19 EndY=35 EndZ=0
    g4: LineSegment StartX=5.21097e-06 StartY=3 StartZ=0 EndX=5.21097e-06 EndY=0 EndZ=0
    g5: LineSegment StartX=3 StartY=0 StartZ=0 EndX=5.21097e-06 EndY=0 EndZ=0
    g6: LineSegment StartX=3 StartY=19 StartZ=0 EndX=3 EndY=0 EndZ=0
    g7: LineSegment StartX=19 StartY=38 StartZ=0 EndX=124 EndY=38 EndZ=0
    g8: Circle CenterX=119 CenterY=35 CenterZ=0 NormalX=0 NormalY=0 NormalZ=1 AngleXU=0 Radius=1
    g9: Circle CenterX=121 CenterY=35 CenterZ=0 NormalX=0 NormalY=0 NormalZ=1 AngleXU=0 Radius=1
    g10: Circle CenterX=121 CenterY=33 CenterZ=0 NormalX=0 NormalY=0 NormalZ=1 AngleXU=0 Radius=1
    g11: BSplineCurve PolesCount=3 KnotsCount=2 Degree=2 IsPeriodic=0
    g12: GeomPoint X=119 Y=35 Z=0
    g13: GeomPoint X=121 Y=33 Z=0
    g14: LineSegment StartX=119 StartY=35 StartZ=0 EndX=114 EndY=35 EndZ=0
    g15: ArcOfCircle CenterX=105 CenterY=19 CenterZ=0 NormalX=0 NormalY=0 NormalZ=1 AngleXU=0 Radius=16 StartAngle=5.60905 EndAngle=6.28319
    g16: LineSegment StartX=121 StartY=33 StartZ=0 EndX=121 EndY=19 EndZ=0
    g17: LineSegment StartX=117.5 StartY=9.01251 StartZ=0 EndX=121.163 EndY=9.0125 EndZ=0
    g18: ArcOfCircle CenterX=105 CenterY=19 CenterZ=0 NormalX=0 NormalY=0 NormalZ=1 AngleXU=0 Radius=20.6155 StartAngle=5.7297 EndAngle=6.28319
    g19: LineSegment StartX=121.163 StartY=9.0125 StartZ=0 EndX=122.538 EndY=8.16329 EndZ=0
    g20: LineSegment StartX=124 StartY=38 StartZ=0 EndX=125.616 EndY=38 EndZ=0
    g21: LineSegment StartX=125.616 StartY=19 StartZ=0 EndX=125.616 EndY=38 EndZ=0
  constraints (49):
    c: Vertical(g0)
    c: Block(g0)
    c: Coincident(g1,g0)
    c: Block(g1)
    c: Coincident(g2,g1)
    c: Block(g2)
    c: Coincident(g3,g2)
    c: Horizontal(g3)
    c: Tangent(g3,g2)
    c: Coincident(g4,g0)
    c: Distance(g4) = 3
    c: Vertical(g4)
    c: Coincident(g5,g4)
    c: Horizontal(g5)
    c: Coincident(g6,g2)
    c: Coincident(g6,g5)
    c: Vertical(g6)
    c: Horizontal(g7)
    c: Distance(g7) = 105
    c: Coincident(g7,g1)
    c: Block(g3)
    c: Weight(g8) = 1
    c: Equal(g8,g9)
    c: Equal(g8,g10)
    c: InternalAlignment(g8,g11)
    c: InternalAlignment(g9,g11)
    c: InternalAlignment(g10,g11)
    c: InternalAlignment(g12,g11)
    c: InternalAlignment(g13,g11)
    c: Block(g11)
    c: Coincident(g14,g11)
    c: Coincident(g14,g3)
    c: Horizontal(g14)
    c: Block(g15)
    c: Coincident(g16,g11)
    c: Coincident(g16,g15)
    c: Vertical(g16)
    c: Distance(g16) = 14
    c: Coincident(g17,g15)
    c: Block(g18)
    c: Coincident(g19,g18)
    c: Coincident(g20,g7)
    c: Horizontal(g20)
    c: Vertical(g21)
    c: Coincident(g20,g21)
    c: Block(g20)
    c: Block(g21)
    c: Block(g19)
    c: Block(g17)
FEATURE [Part::Box] Box026  label="removeToCreteHoleForPlugHousing032"
  AttacherType = Attacher::AttachEngine3D
  Height = 28.6
  Length = 10
  Placement = pos=(-2,0,21.7) rot=(0,0,1;0rad)
  Width = 19
FEATURE [Part::Feature] Face109 .. Face112  x4 (patterned run collapsed; names and placements below)
  shape: bbox 3.5 x 17.8 x 2e-07 mm, 1 faces, 0 solids (baked)
FEATURE [Part::Revolution] Revolve117  label="removeToCreateScrewAndThreadedInsertHole045"
  Angle = 360
  Axis = (0,1,0)
  Base = (0,0,0)
  FaceMakerClass = Part::FaceMakerBullseye
  Placement = pos=(62.3,30.3,19.7) rot=(0,0,1;0rad)
  Solid = false
  Source = -> Face109
  Symmetric = false
FEATURE [Part::Revolution] Revolve118  label="removeToCreateScrewAndThreadedInsertHole046"
  Angle = 360
  Axis = (0,1,0)
  Base = (0,0,0)
  FaceMakerClass = Part::FaceMakerBullseye
  Placement = pos=(62.3,30.3,51.7) rot=(0,0,1;0rad)
  Solid = false
  Source = -> Face110
  Symmetric = false
FEATURE [Part::Revolution] Revolve119  label="removeToCreateScrewAndThreadedInsertHole047"
  Angle = 360
  Axis = (0,1,0)
  Base = (0,0,0)
  FaceMakerClass = Part::FaceMakerBullseye
  Placement = pos=(30.3,30.3,19.7) rot=(0,0,1;0rad)
  Solid = false
  Source = -> Face111
  Symmetric = false
FEATURE [Part::Revolution] Revolve120  label="removeToCreateScrewAndThreadedInsertHole048"
  Angle = 360
  Axis = (0,1,0)
  Base = (0,0,0)
  FaceMakerClass = Part::FaceMakerBullseye
  Placement = pos=(30.3,30.3,51.7) rot=(0,0,1;0rad)
  Solid = false
  Source = -> Face112
  Symmetric = false
FEATURE [Part::MultiFuse] Fusion087  label="createThreadedInsertHolesForFan005"
  Shapes = -> [Revolve117,Revolve118,Revolve119,Revolve120]
FEATURE [Part::Extrusion] Extrude047
  Base = -> Sketch056
  Dir = (0,0,1)
  DirMode = 2
  FaceMakerClass = Part::FaceMakerBullseye
  LengthFwd = 72
  LengthRev = 0
  Solid = true
  Symmetric = false
FEATURE [Part::Fillet] Fillet039  label="top019"
  Base = -> Extrude047
  Edges = 1 edges r=2: [Edge35]
FEATURE [Sketcher::SketchObject] Sketch057
  FullyConstrained = false
  Placement = pos=(0,0,0) rot=(1,0,0;1.5708rad)
  sketch-geometry (24):
    g0: ArcOfCircle CenterX=-4 CenterY=-10.5 CenterZ=0 NormalX=0 NormalY=0 NormalZ=1 AngleXU=0 Radius=1.5 StartAngle=6e-16 EndAngle=3.14159
    g1: ArcOfCircle CenterX=-34.2 CenterY=-10.5 CenterZ=0 NormalX=0 NormalY=0 NormalZ=1 AngleXU=0 Radius=1.5 StartAngle=0 EndAngle=3.14159
    g2: ArcOfCircle CenterX=-34.2 CenterY=-27.7 CenterZ=0 NormalX=0 NormalY=0 NormalZ=1 AngleXU=0 Radius=1.5 StartAngle=3.14159 EndAngle=6.28319
    g3: ArcOfCircle CenterX=-4 CenterY=-27.7 CenterZ=0 NormalX=0 NormalY=0 NormalZ=1 AngleXU=0 Radius=1.5 StartAngle=3.1416 EndAngle=6.28319
    g4: ArcOfCircle CenterX=-10 CenterY=-4.3 CenterZ=0 NormalX=0 NormalY=0 NormalZ=1 AngleXU=0 Radius=1.5 StartAngle=2e-16 EndAngle=3.14159
    g5: ArcOfCircle CenterX=-16.1 CenterY=-1.8 CenterZ=0 NormalX=0 NormalY=0 NormalZ=1 AngleXU=0 Radius=1.5 StartAngle=5e-16 EndAngle=3.14159
    g6: ArcOfCircle CenterX=-22.1 CenterY=-1.8 CenterZ=0 NormalX=0 NormalY=0 NormalZ=1 AngleXU=0 Radius=1.5 StartAngle=5e-16 EndAngle=3.14159
    g7: ArcOfCircle CenterX=-28.2 CenterY=-4.3 CenterZ=0 NormalX=0 NormalY=0 NormalZ=1 AngleXU=0 Radius=1.5 StartAngle=2e-16 EndAngle=3.14159
    g8: ArcOfCircle CenterX=-10 CenterY=-33.9 CenterZ=0 NormalX=0 NormalY=0 NormalZ=1 AngleXU=0 Radius=1.5 StartAngle=3.14159 EndAngle=6.28319
    g9: ArcOfCircle CenterX=-16.1 CenterY=-36.4 CenterZ=0 NormalX=0 NormalY=0 NormalZ=1 AngleXU=0 Radius=1.5 StartAngle=3.14159 EndAngle=6.28319
    g10: ArcOfCircle CenterX=-22.1 CenterY=-36.4 CenterZ=0 NormalX=0 NormalY=0 NormalZ=1 AngleXU=0 Radius=1.5 StartAngle=3.14159 EndAngle=6.28319
    g11: ArcOfCircle CenterX=-28.2 CenterY=-33.9 CenterZ=0 NormalX=0 NormalY=0 NormalZ=1 AngleXU=0 Radius=1.5 StartAngle=3.14159 EndAngle=6.28319
    g12: LineSegment StartX=-35.7 StartY=-10.5 StartZ=0 EndX=-35.7 EndY=-27.7 EndZ=0
    g13: LineSegment StartX=-32.7 StartY=-10.5 StartZ=0 EndX=-32.7 EndY=-27.7 EndZ=0
    g14: LineSegment StartX=-29.7 StartY=-33.9 StartZ=0 EndX=-29.7 EndY=-4.3 EndZ=0
    g15: LineSegment StartX=-26.7 StartY=-33.9 StartZ=0 EndX=-26.7 EndY=-4.3 EndZ=0
    g16: LineSegment StartX=-2.5 StartY=-10.5 StartZ=0 EndX=-2.5 EndY=-27.7 EndZ=0
    g17: LineSegment StartX=-8.5 StartY=-4.3 StartZ=0 EndX=-8.5 EndY=-33.9 EndZ=0
    g18: LineSegment StartX=-5.5 StartY=-10.5 StartZ=0 EndX=-5.5 EndY=-27.7 EndZ=0
    g19: LineSegment StartX=-11.5 StartY=-4.3 StartZ=0 EndX=-11.5 EndY=-33.9 EndZ=0
    g20: LineSegment StartX=-14.6 StartY=-1.8 StartZ=0 EndX=-14.6 EndY=-36.4 EndZ=0
    g21: LineSegment StartX=-17.6 StartY=-1.8 StartZ=0 EndX=-17.6 EndY=-36.4 EndZ=0
    g22: LineSegment StartX=-20.6 StartY=-36.4 StartZ=0 EndX=-20.6 EndY=-1.8 EndZ=0
    g23: LineSegment StartX=-23.6 StartY=-1.8 StartZ=0 EndX=-23.6 EndY=-36.4 EndZ=0
  constraints (48):
    c: Block(g0)
    c: Block(g1)
    c: Block(g2)
    c: Block(g3)
    c: Block(g4)
    c: Block(g5)
    c: Block(g6)
    c: Block(g7)
    c: Block(g8)
    c: Block(g9)
    c: Block(g10)
    c: Block(g11)
    c: Coincident(g12,g1)
    c: Coincident(g12,g2)
    c: Vertical(g12)
    c: Coincident(g13,g1)
    c: Coincident(g13,g2)
    c: Vertical(g13)
    c: Coincident(g14,g11)
    c: Coincident(g14,g7)
    c: Vertical(g14)
    c: Coincident(g15,g11)
    c: Coincident(g15,g7)
    c: Vertical(g15)
    c: Coincident(g16,g0)
    c: Coincident(g16,g3)
    c: Vertical(g16)
    c: Coincident(g17,g4)
    c: Coincident(g17,g8)
    c: Vertical(g17)
    c: Coincident(g18,g0)
    c: Coincident(g18,g3)
    c: Vertical(g18)
    c: Coincident(g19,g4)
    c: Coincident(g19,g8)
    c: Vertical(g19)
    c: Coincident(g20,g5)
    c: Coincident(g20,g9)
    c: Vertical(g20)
    c: Coincident(g21,g5)
    c: Coincident(g21,g9)
    c: Vertical(g21)
    c: Coincident(g22,g10)
    c: Coincident(g22,g6)
    c: Vertical(g22)
    c: Coincident(g23,g6)
    c: Coincident(g23,g10)
    c: Vertical(g23)
FEATURE [Part::Extrusion] Extrude048  label="removeToCreateFanGrillHoles004"
  Base = -> Sketch057
  Dir = (0,-1,6e-16)
  DirMode = 2
  FaceMakerClass = Part::FaceMakerBullseye
  LengthFwd = 10
  LengthRev = 0
  Placement = pos=(65.4,44,54.82) rot=(0,0,1;0rad)
  Solid = true
  Symmetric = false
FEATURE [Part::Cut] Cut040  label="top021"
  Base = -> Fillet039
  Tool = -> Extrude048
FEATURE [Part::Cylinder] Cylinder041  label="removeToCreteHoleForPlugHousing034"
  Angle = 360
  AttacherType = Attacher::AttachEngine3D
  Height = 20
  Placement = pos=(-2,19,36) rot=(0,1,0;1.5708rad)
  Radius = 14.3
FEATURE [Part::MultiFuse] Fusion089  label="removeToCreteHoleForPlugHousing035"
  Shapes = -> [Box026,Cylinder041]
FEATURE [Part::Cylinder] Cylinder042
  Angle = 360
  AttacherType = Attacher::AttachEngine3D
  Height = 20
  Placement = pos=(0,0,36.15) rot=(0,0,1;0rad)
  Radius = 14.3
FEATURE [Part::Cylinder] Cylinder043
  Angle = 360
  AttacherType = Attacher::AttachEngine3D
  Height = 10
  Placement = pos=(0,0,36.15) rot=(0,0,1;0rad)
  Radius = 4
FEATURE [Part::Box] Box027  label="removeToCreteHoleForPlugHousing036"
  AttacherType = Attacher::AttachEngine3D
  Height = 28.6
  Length = 20
  Placement = pos=(106.15,0,21.7) rot=(0,0,1;0rad)
  Width = 19
FEATURE [Part::Cut] Cut041  label="top022"
  Base = -> Cut040
  Tool = -> Fusion087
FEATURE [Part::Cut] Cut039  label="top020"
  Base = -> Cut041
  Tool = -> Fusion089
FEATURE [Part::MultiFuse] Fusion090  label="removeToCreteHoleForPlugHousing037"
  Placement = pos=(70,19,36) rot=(0,1,0;1.5708rad)
  Shapes = -> [Cylinder042,Cylinder043]
FEATURE [Part::MultiFuse] Fusion088  label="removeToCreteHoleForPlugHousing033"
  Shapes = -> [Box027,Fusion090]
FEATURE [Part::Cut] Cut042  label="removeToCreteHoleForPlugHousing038"
  Base = -> Cut039
  Tool = -> Fusion088
FEATURE [Part::MultiFuse] Fusion091  label="removeFromTop"
  Shapes = -> [Fillet038,Fusion085,Fusion084,Fusion083,Extrude045]
FEATURE [Part::Cut] Cut043  label="REAL TOP ====="
  Base = -> Fillet036
  Tool = -> Fusion091
FEATURE [Part::MultiFuse] Fusion092  label="caseScrewPillarBracket016"
  Shapes = -> [Extrude030,Extrude031,Extrude032,Extrude033,Extrude034,Extrude035,Extrude036,Extrude037,Box013,Box014]
FEATURE [Sketcher::SketchObject] Sketch058  label="topSketch015"
  FullyConstrained = true
  sketch-geometry (20):
    g0: LineSegment StartX=5.21097e-06 StartY=3 StartZ=0 EndX=5.21097e-06 EndY=19 EndZ=0
    g1: ArcOfCircle CenterX=19 CenterY=19 CenterZ=0 NormalX=0 NormalY=0 NormalZ=1 AngleXU=0 Radius=19 StartAngle=1.5708 EndAngle=3.14159
    g2: ArcOfCircle CenterX=19 CenterY=19 CenterZ=0 NormalX=0 NormalY=0 NormalZ=1 AngleXU=0 Radius=16 StartAngle=1.5708 EndAngle=3.14159
    g3: LineSegment StartX=114 StartY=35 StartZ=0 EndX=19 EndY=35 EndZ=0
    g4: LineSegment StartX=5.21097e-06 StartY=3 StartZ=0 EndX=5.21097e-06 EndY=0 EndZ=0
    g5: LineSegment StartX=3 StartY=0 StartZ=0 EndX=5.21097e-06 EndY=0 EndZ=0
    g6: LineSegment StartX=3 StartY=19 StartZ=0 EndX=3 EndY=0 EndZ=0
    g7: LineSegment StartX=19 StartY=38 StartZ=0 EndX=124 EndY=38 EndZ=0
    g8: Circle CenterX=119 CenterY=35 CenterZ=0 NormalX=0 NormalY=0 NormalZ=1 AngleXU=0 Radius=1
    g9: Circle CenterX=121 CenterY=35 CenterZ=0 NormalX=0 NormalY=0 NormalZ=1 AngleXU=0 Radius=1
    g10: Circle CenterX=121 CenterY=33 CenterZ=0 NormalX=0 NormalY=0 NormalZ=1 AngleXU=0 Radius=1
    g11: BSplineCurve PolesCount=3 KnotsCount=2 Degree=2 IsPeriodic=0
    g12: GeomPoint X=119 Y=35 Z=0
    g13: GeomPoint X=121 Y=33 Z=0
    g14: LineSegment StartX=119 StartY=35 StartZ=0 EndX=114 EndY=35 EndZ=0
    g15: ArcOfCircle CenterX=105 CenterY=19 CenterZ=0 NormalX=0 NormalY=0 NormalZ=1 AngleXU=0 Radius=19 StartAngle=5.7297 EndAngle=6.28319
    g16: ArcOfCircle CenterX=105 CenterY=19 CenterZ=0 NormalX=0 NormalY=0 NormalZ=1 AngleXU=0 Radius=16 StartAngle=5.60905 EndAngle=6.28319
    g17: LineSegment StartX=121 StartY=33 StartZ=0 EndX=121 EndY=19 EndZ=0
    g18: LineSegment StartX=124 StartY=38 StartZ=0 EndX=124 EndY=19 EndZ=0
    g19: LineSegment StartX=117.5 StartY=9.01251 StartZ=0 EndX=121.163 EndY=9.0125 EndZ=0
  constraints (46):
    c: Vertical(g0)
    c: Block(g0)
    c: Coincident(g1,g0)
    c: Block(g1)
    c: Coincident(g2,g1)
    c: Block(g2)
    c: Coincident(g3,g2)
    c: Horizontal(g3)
    c: Tangent(g3,g2)
    c: Coincident(g4,g0)
    c: Distance(g4) = 3
    c: Vertical(g4)
    c: Coincident(g5,g4)
    c: Horizontal(g5)
    c: Coincident(g6,g2)
    c: Coincident(g6,g5)
    c: Vertical(g6)
    c: Horizontal(g7)
    c: Distance(g7) = 105
    c: Coincident(g7,g1)
    c: Block(g3)
    c: Weight(g8) = 1
    c: Equal(g8,g9)
    c: Equal(g8,g10)
    c: InternalAlignment(g8,g11)
    c: InternalAlignment(g9,g11)
    c: InternalAlignment(g10,g11)
    c: InternalAlignment(g12,g11)
    c: InternalAlignment(g13,g11)
    c: Block(g11)
    c: Coincident(g14,g11)
    c: Coincident(g14,g3)
    c: Horizontal(g14)
    c: Block(g15)
    c: Coincident(g16,g15)
    c: Block(g16)
    c: Coincident(g17,g11)
    c: Coincident(g17,g16)
    c: Vertical(g17)
    c: Distance(g17) = 14
    c: Coincident(g18,g7)
    c: Coincident(g18,g15)
    c: Vertical(g18)
    c: Distance(g18) = 19
    c: Coincident(g19,g16)
    c: Coincident(g19,g15)
FEATURE [Part::Extrusion] Extrude049  label="top023"
  Base = -> Sketch058
  Dir = (0,0,1)
  DirMode = 2
  FaceMakerClass = Part::FaceMakerBullseye
  LengthFwd = 72
  LengthRev = 0
  Solid = true
  Symmetric = false
FEATURE [Sketcher::SketchObject] Sketch059
  FullyConstrained = true
  MapMode = 3
  Placement = pos=(0,0,0) rot=(1,0,0;1.5708rad)
  Support = -> [Extrude049]
  sketch-geometry (8):
    g0: Circle CenterX=80.351 CenterY=-67.6202 CenterZ=0 NormalX=0 NormalY=0 NormalZ=1 AngleXU=0 Radius=2
    g1: Circle CenterX=80.351 CenterY=-67.6202 CenterZ=0 NormalX=0 NormalY=0 NormalZ=1 AngleXU=0 Radius=3
    g2: Circle CenterX=80.351 CenterY=-4.92017 CenterZ=0 NormalX=0 NormalY=0 NormalZ=1 AngleXU=0 Radius=2
    g3: Circle CenterX=80.351 CenterY=-4.92017 CenterZ=0 NormalX=0 NormalY=0 NormalZ=1 AngleXU=0 Radius=3
    g4: Circle CenterX=23.851 CenterY=-4.92017 CenterZ=0 NormalX=0 NormalY=0 NormalZ=1 AngleXU=0 Radius=2
    g5: Circle CenterX=23.851 CenterY=-4.92017 CenterZ=0 NormalX=0 NormalY=0 NormalZ=1 AngleXU=0 Radius=3
    g6: Circle CenterX=23.851 CenterY=-67.6202 CenterZ=0 NormalX=0 NormalY=0 NormalZ=1 AngleXU=0 Radius=2
    g7: Circle CenterX=23.851 CenterY=-67.6202 CenterZ=0 NormalX=0 NormalY=0 NormalZ=1 AngleXU=0 Radius=3
  constraints (8):
    c: Block(g3)
    c: Block(g2)
    c: Block(g1)
    c: Block(g0)
    c: Block(g6)
    c: Block(g7)
    c: Block(g4)
    c: Block(g5)
FEATURE [Sketcher::SketchObject] Sketch060
  FullyConstrained = true
  MapMode = 3
  Placement = pos=(0,0,0) rot=(1,0,0;1.5708rad)
  Support = -> [Extrude049]
  sketch-geometry (8):
    g0: Circle CenterX=80.351 CenterY=-67.6202 CenterZ=0 NormalX=0 NormalY=0 NormalZ=1 AngleXU=0 Radius=3
    g1: Circle CenterX=80.351 CenterY=-4.92017 CenterZ=0 NormalX=0 NormalY=0 NormalZ=1 AngleXU=0 Radius=3
    g2: Circle CenterX=23.851 CenterY=-4.92017 CenterZ=0 NormalX=0 NormalY=0 NormalZ=1 AngleXU=0 Radius=3
    g3: Circle CenterX=23.851 CenterY=-67.6202 CenterZ=0 NormalX=0 NormalY=0 NormalZ=1 AngleXU=0 Radius=3
    g4: Circle CenterX=23.851 CenterY=-67.6202 CenterZ=0 NormalX=0 NormalY=0 NormalZ=1 AngleXU=0 Radius=5
    g5: Circle CenterX=80.351 CenterY=-67.6202 CenterZ=0 NormalX=0 NormalY=0 NormalZ=1 AngleXU=0 Radius=5
    g6: Circle CenterX=23.851 CenterY=-4.92017 CenterZ=0 NormalX=0 NormalY=0 NormalZ=1 AngleXU=0 Radius=5
    g7: Circle CenterX=80.351 CenterY=-4.92017 CenterZ=0 NormalX=0 NormalY=0 NormalZ=1 AngleXU=0 Radius=5
  constraints (8):
    c: Block(g1)
    c: Block(g0)
    c: Block(g3)
    c: Block(g2)
    c: Block(g5)
    c: Block(g4)
    c: Block(g6)
    c: Block(g7)
FEATURE [Sketcher::SketchObject] Sketch061
  FullyConstrained = true
  MapMode = 3
  Placement = pos=(0,0,0) rot=(1,0,0;1.5708rad)
  sketch-geometry (8):
    g0: Circle CenterX=80.351 CenterY=-67.6202 CenterZ=0 NormalX=0 NormalY=0 NormalZ=1 AngleXU=0 Radius=3
    g1: Circle CenterX=80.351 CenterY=-4.92017 CenterZ=0 NormalX=0 NormalY=0 NormalZ=1 AngleXU=0 Radius=3
    g2: Circle CenterX=23.851 CenterY=-4.92017 CenterZ=0 NormalX=0 NormalY=0 NormalZ=1 AngleXU=0 Radius=3
    g3: Circle CenterX=23.851 CenterY=-67.6202 CenterZ=0 NormalX=0 NormalY=0 NormalZ=1 AngleXU=0 Radius=3
    g4: Circle CenterX=23.851 CenterY=-67.6202 CenterZ=0 NormalX=0 NormalY=0 NormalZ=1 AngleXU=0 Radius=5
    g5: Circle CenterX=80.351 CenterY=-67.6202 CenterZ=0 NormalX=0 NormalY=0 NormalZ=1 AngleXU=0 Radius=5
    g6: Circle CenterX=23.851 CenterY=-4.92017 CenterZ=0 NormalX=0 NormalY=0 NormalZ=1 AngleXU=0 Radius=5
    g7: Circle CenterX=80.351 CenterY=-4.92017 CenterZ=0 NormalX=0 NormalY=0 NormalZ=1 AngleXU=0 Radius=5
  constraints (8):
    c: Block(g1)
    c: Block(g0)
    c: Block(g3)
    c: Block(g2)
    c: Block(g5)
    c: Block(g4)
    c: Block(g6)
    c: Block(g7)
FEATURE [Sketcher::SketchObject] Sketch062  label="topSketch016"
  FullyConstrained = true
  sketch-geometry (20):
    g0: LineSegment StartX=5.21097e-06 StartY=3 StartZ=0 EndX=5.21097e-06 EndY=19 EndZ=0
    g1: ArcOfCircle CenterX=19 CenterY=19 CenterZ=0 NormalX=0 NormalY=0 NormalZ=1 AngleXU=0 Radius=19 StartAngle=1.5708 EndAngle=3.14159
    g2: ArcOfCircle CenterX=19 CenterY=19 CenterZ=0 NormalX=0 NormalY=0 NormalZ=1 AngleXU=0 Radius=16 StartAngle=1.5708 EndAngle=3.14159
    g3: LineSegment StartX=114 StartY=35 StartZ=0 EndX=19 EndY=35 EndZ=0
    g4: LineSegment StartX=5.21097e-06 StartY=3 StartZ=0 EndX=5.21097e-06 EndY=0 EndZ=0
    g5: LineSegment StartX=3 StartY=0 StartZ=0 EndX=5.21097e-06 EndY=0 EndZ=0
    g6: LineSegment StartX=3 StartY=19 StartZ=0 EndX=3 EndY=0 EndZ=0
    g7: LineSegment StartX=19 StartY=38 StartZ=0 EndX=124 EndY=38 EndZ=0
    g8: Circle CenterX=119 CenterY=35 CenterZ=0 NormalX=0 NormalY=0 NormalZ=1 AngleXU=0 Radius=1
    g9: Circle CenterX=121 CenterY=35 CenterZ=0 NormalX=0 NormalY=0 NormalZ=1 AngleXU=0 Radius=1
    g10: Circle CenterX=121 CenterY=33 CenterZ=0 NormalX=0 NormalY=0 NormalZ=1 AngleXU=0 Radius=1
    g11: BSplineCurve PolesCount=3 KnotsCount=2 Degree=2 IsPeriodic=0
    g12: GeomPoint X=119 Y=35 Z=0
    g13: GeomPoint X=121 Y=33 Z=0
    g14: LineSegment StartX=119 StartY=35 StartZ=0 EndX=114 EndY=35 EndZ=0
    g15: ArcOfCircle CenterX=105 CenterY=19 CenterZ=0 NormalX=0 NormalY=0 NormalZ=1 AngleXU=0 Radius=19 StartAngle=5.7297 EndAngle=6.28319
    g16: ArcOfCircle CenterX=105 CenterY=19 CenterZ=0 NormalX=0 NormalY=0 NormalZ=1 AngleXU=0 Radius=16 StartAngle=5.60905 EndAngle=6.28319
    g17: LineSegment StartX=121 StartY=33 StartZ=0 EndX=121 EndY=19 EndZ=0
    g18: LineSegment StartX=124 StartY=38 StartZ=0 EndX=124 EndY=19 EndZ=0
    g19: LineSegment StartX=117.5 StartY=9.01251 StartZ=0 EndX=121.163 EndY=9.0125 EndZ=0
  constraints (46):
    c: Vertical(g0)
    c: Block(g0)
    c: Coincident(g1,g0)
    c: Block(g1)
    c: Coincident(g2,g1)
    c: Block(g2)
    c: Coincident(g3,g2)
    c: Horizontal(g3)
    c: Tangent(g3,g2)
    c: Coincident(g4,g0)
    c: Distance(g4) = 3
    c: Vertical(g4)
    c: Coincident(g5,g4)
    c: Horizontal(g5)
    c: Coincident(g6,g2)
    c: Coincident(g6,g5)
    c: Vertical(g6)
    c: Horizontal(g7)
    c: Distance(g7) = 105
    c: Coincident(g7,g1)
    c: Block(g3)
    c: Weight(g8) = 1
    c: Equal(g8,g9)
    c: Equal(g8,g10)
    c: InternalAlignment(g8,g11)
    c: InternalAlignment(g9,g11)
    c: InternalAlignment(g10,g11)
    c: InternalAlignment(g12,g11)
    c: InternalAlignment(g13,g11)
    c: Block(g11)
    c: Coincident(g14,g11)
    c: Coincident(g14,g3)
    c: Horizontal(g14)
    c: Block(g15)
    c: Coincident(g16,g15)
    c: Block(g16)
    c: Coincident(g17,g11)
    c: Coincident(g17,g16)
    c: Vertical(g17)
    c: Distance(g17) = 14
    c: Coincident(g18,g7)
    c: Coincident(g18,g15)
    c: Vertical(g18)
    c: Distance(g18) = 19
    c: Coincident(g19,g16)
    c: Coincident(g19,g15)
FEATURE [Part::Extrusion] Extrude053  label="top024"
  Base = -> Sketch062
  Dir = (0,0,1)
  DirMode = 2
  FaceMakerClass = Part::FaceMakerBullseye
  LengthFwd = 72
  LengthRev = 0
  Solid = true
  Symmetric = false
FEATURE [Sketcher::SketchObject] Sketch063
  FullyConstrained = true
  MapMode = 3
  Placement = pos=(0,0,0) rot=(1,0,0;1.5708rad)
  Support = -> [Extrude053]
  sketch-geometry (8):
    g0: Circle CenterX=80.351 CenterY=-67.6202 CenterZ=0 NormalX=0 NormalY=0 NormalZ=1 AngleXU=0 Radius=2
    g1: Circle CenterX=80.351 CenterY=-67.6202 CenterZ=0 NormalX=0 NormalY=0 NormalZ=1 AngleXU=0 Radius=3
    g2: Circle CenterX=80.351 CenterY=-4.92017 CenterZ=0 NormalX=0 NormalY=0 NormalZ=1 AngleXU=0 Radius=2
    g3: Circle CenterX=80.351 CenterY=-4.92017 CenterZ=0 NormalX=0 NormalY=0 NormalZ=1 AngleXU=0 Radius=3
    g4: Circle CenterX=23.851 CenterY=-4.92017 CenterZ=0 NormalX=0 NormalY=0 NormalZ=1 AngleXU=0 Radius=2
    g5: Circle CenterX=23.851 CenterY=-4.92017 CenterZ=0 NormalX=0 NormalY=0 NormalZ=1 AngleXU=0 Radius=3
    g6: Circle CenterX=23.851 CenterY=-67.6202 CenterZ=0 NormalX=0 NormalY=0 NormalZ=1 AngleXU=0 Radius=2
    g7: Circle CenterX=23.851 CenterY=-67.6202 CenterZ=0 NormalX=0 NormalY=0 NormalZ=1 AngleXU=0 Radius=3
  constraints (8):
    c: Block(g3)
    c: Block(g2)
    c: Block(g1)
    c: Block(g0)
    c: Block(g6)
    c: Block(g7)
    c: Block(g4)
    c: Block(g5)
FEATURE [Part::Extrusion] Extrude054
  Base = -> Sketch063
  Dir = (0,-1,2e-16)
  DirMode = 2
  FaceMakerClass = Part::FaceMakerBullseye
  LengthFwd = 6
  LengthRev = 0
  Placement = pos=(0,9,0) rot=(0,0,1;0rad)
  Solid = true
  Symmetric = false
FEATURE [Sketcher::SketchObject] Sketch064  label="topSketch017"
  FullyConstrained = true
  sketch-geometry (20):
    g0: LineSegment StartX=5.21097e-06 StartY=3 StartZ=0 EndX=5.21097e-06 EndY=19 EndZ=0
    g1: ArcOfCircle CenterX=19 CenterY=19 CenterZ=0 NormalX=0 NormalY=0 NormalZ=1 AngleXU=0 Radius=19 StartAngle=1.5708 EndAngle=3.14159
    g2: ArcOfCircle CenterX=19 CenterY=19 CenterZ=0 NormalX=0 NormalY=0 NormalZ=1 AngleXU=0 Radius=16 StartAngle=1.5708 EndAngle=3.14159
    g3: LineSegment StartX=114 StartY=35 StartZ=0 EndX=19 EndY=35 EndZ=0
    g4: LineSegment StartX=5.21097e-06 StartY=3 StartZ=0 EndX=5.21097e-06 EndY=0 EndZ=0
    g5: LineSegment StartX=3 StartY=0 StartZ=0 EndX=5.21097e-06 EndY=0 EndZ=0
    g6: LineSegment StartX=3 StartY=19 StartZ=0 EndX=3 EndY=0 EndZ=0
    g7: LineSegment StartX=19 StartY=38 StartZ=0 EndX=124 EndY=38 EndZ=0
    g8: Circle CenterX=119 CenterY=35 CenterZ=0 NormalX=0 NormalY=0 NormalZ=1 AngleXU=0 Radius=1
    g9: Circle CenterX=121 CenterY=35 CenterZ=0 NormalX=0 NormalY=0 NormalZ=1 AngleXU=0 Radius=1
    g10: Circle CenterX=121 CenterY=33 CenterZ=0 NormalX=0 NormalY=0 NormalZ=1 AngleXU=0 Radius=1
    g11: BSplineCurve PolesCount=3 KnotsCount=2 Degree=2 IsPeriodic=0
    g12: GeomPoint X=119 Y=35 Z=0
    g13: GeomPoint X=121 Y=33 Z=0
    g14: LineSegment StartX=119 StartY=35 StartZ=0 EndX=114 EndY=35 EndZ=0
    g15: ArcOfCircle CenterX=105 CenterY=19 CenterZ=0 NormalX=0 NormalY=0 NormalZ=1 AngleXU=0 Radius=19 StartAngle=5.7297 EndAngle=6.28319
    g16: ArcOfCircle CenterX=105 CenterY=19 CenterZ=0 NormalX=0 NormalY=0 NormalZ=1 AngleXU=0 Radius=16 StartAngle=5.60905 EndAngle=6.28319
    g17: LineSegment StartX=121 StartY=33 StartZ=0 EndX=121 EndY=19 EndZ=0
    g18: LineSegment StartX=124 StartY=38 StartZ=0 EndX=124 EndY=19 EndZ=0
    g19: LineSegment StartX=117.5 StartY=9.01251 StartZ=0 EndX=121.163 EndY=9.0125 EndZ=0
  constraints (46):
    c: Vertical(g0)
    c: Block(g0)
    c: Coincident(g1,g0)
    c: Block(g1)
    c: Coincident(g2,g1)
    c: Block(g2)
    c: Coincident(g3,g2)
    c: Horizontal(g3)
    c: Tangent(g3,g2)
    c: Coincident(g4,g0)
    c: Distance(g4) = 3
    c: Vertical(g4)
    c: Coincident(g5,g4)
    c: Horizontal(g5)
    c: Coincident(g6,g2)
    c: Coincident(g6,g5)
    c: Vertical(g6)
    c: Horizontal(g7)
    c: Distance(g7) = 105
    c: Coincident(g7,g1)
    c: Block(g3)
    c: Weight(g8) = 1
    c: Equal(g8,g9)
    c: Equal(g8,g10)
    c: InternalAlignment(g8,g11)
    c: InternalAlignment(g9,g11)
    c: InternalAlignment(g10,g11)
    c: InternalAlignment(g12,g11)
    c: InternalAlignment(g13,g11)
    c: Block(g11)
    c: Coincident(g14,g11)
    c: Coincident(g14,g3)
    c: Horizontal(g14)
    c: Block(g15)
    c: Coincident(g16,g15)
    c: Block(g16)
    c: Coincident(g17,g11)
    c: Coincident(g17,g16)
    c: Vertical(g17)
    c: Distance(g17) = 14
    c: Coincident(g18,g7)
    c: Coincident(g18,g15)
    c: Vertical(g18)
    c: Distance(g18) = 19
    c: Coincident(g19,g16)
    c: Coincident(g19,g15)
FEATURE [Sketcher::SketchObject] Sketch065
  FullyConstrained = true
  MapMode = 3
  Placement = pos=(0,0,0) rot=(1,0,0;1.5708rad)
  sketch-geometry (8):
    g0: Circle CenterX=80.351 CenterY=-67.6202 CenterZ=0 NormalX=0 NormalY=0 NormalZ=1 AngleXU=0 Radius=3
    g1: Circle CenterX=80.351 CenterY=-4.92017 CenterZ=0 NormalX=0 NormalY=0 NormalZ=1 AngleXU=0 Radius=3
    g2: Circle CenterX=23.851 CenterY=-4.92017 CenterZ=0 NormalX=0 NormalY=0 NormalZ=1 AngleXU=0 Radius=3
    g3: Circle CenterX=23.851 CenterY=-67.6202 CenterZ=0 NormalX=0 NormalY=0 NormalZ=1 AngleXU=0 Radius=3
    g4: Circle CenterX=23.851 CenterY=-67.6202 CenterZ=0 NormalX=0 NormalY=0 NormalZ=1 AngleXU=0 Radius=5
    g5: Circle CenterX=80.351 CenterY=-67.6202 CenterZ=0 NormalX=0 NormalY=0 NormalZ=1 AngleXU=0 Radius=5
    g6: Circle CenterX=23.851 CenterY=-4.92017 CenterZ=0 NormalX=0 NormalY=0 NormalZ=1 AngleXU=0 Radius=5
    g7: Circle CenterX=80.351 CenterY=-4.92017 CenterZ=0 NormalX=0 NormalY=0 NormalZ=1 AngleXU=0 Radius=5
  constraints (8):
    c: Block(g1)
    c: Block(g0)
    c: Block(g3)
    c: Block(g2)
    c: Block(g5)
    c: Block(g4)
    c: Block(g6)
    c: Block(g7)
FEATURE [Part::Extrusion] Extrude056
  Base = -> Sketch065
  Dir = (0,-1,2e-16)
  DirMode = 2
  FaceMakerClass = Part::FaceMakerBullseye
  LengthFwd = 2
  LengthRev = 0
  Solid = true
  Symmetric = false
FEATURE [Part::Extrusion] Extrude057  label="top025"
  Base = -> Sketch064
  Dir = (0,0,1)
  DirMode = 2
  FaceMakerClass = Part::FaceMakerBullseye
  LengthFwd = 72
  LengthRev = 0
  Solid = true
  Symmetric = false
FEATURE [Sketcher::SketchObject] Sketch066
  FullyConstrained = true
  MapMode = 3
  Placement = pos=(0,0,0) rot=(1,0,0;1.5708rad)
  Support = -> [Extrude057]
  sketch-geometry (8):
    g0: Circle CenterX=80.351 CenterY=-67.6202 CenterZ=0 NormalX=0 NormalY=0 NormalZ=1 AngleXU=0 Radius=3
    g1: Circle CenterX=80.351 CenterY=-4.92017 CenterZ=0 NormalX=0 NormalY=0 NormalZ=1 AngleXU=0 Radius=3
    g2: Circle CenterX=23.851 CenterY=-4.92017 CenterZ=0 NormalX=0 NormalY=0 NormalZ=1 AngleXU=0 Radius=3
    g3: Circle CenterX=23.851 CenterY=-67.6202 CenterZ=0 NormalX=0 NormalY=0 NormalZ=1 AngleXU=0 Radius=3
    g4: Circle CenterX=23.851 CenterY=-67.6202 CenterZ=0 NormalX=0 NormalY=0 NormalZ=1 AngleXU=0 Radius=5
    g5: Circle CenterX=80.351 CenterY=-67.6202 CenterZ=0 NormalX=0 NormalY=0 NormalZ=1 AngleXU=0 Radius=5
    g6: Circle CenterX=23.851 CenterY=-4.92017 CenterZ=0 NormalX=0 NormalY=0 NormalZ=1 AngleXU=0 Radius=5
    g7: Circle CenterX=80.351 CenterY=-4.92017 CenterZ=0 NormalX=0 NormalY=0 NormalZ=1 AngleXU=0 Radius=5
  constraints (8):
    c: Block(g1)
    c: Block(g0)
    c: Block(g3)
    c: Block(g2)
    c: Block(g5)
    c: Block(g4)
    c: Block(g6)
    c: Block(g7)
FEATURE [Part::Extrusion] Extrude055
  Base = -> Sketch066
  Dir = (0,-1,2e-16)
  DirMode = 2
  FaceMakerClass = Part::FaceMakerBullseye
  LengthFwd = 2
  LengthRev = 0
  Solid = true
  Symmetric = false
FEATURE [Part::Fillet] Fillet041
  Base = -> Extrude056
  Edges = 4 edges r=1.99: [Edge6,Edge12,Edge18,Edge24]
FEATURE [Part::Cut] Cut045
  Base = -> Extrude055
  Placement = pos=(0,6,0) rot=(0,0,1;0rad)
  Tool = -> Fillet041
FEATURE [Part::MultiFuse] Fusion095  label="pcbScrewPillars"
  Placement = pos=(-3.2,-1,72.3) rot=(0,0,1;0rad)
  Shapes = -> [Cut045,Extrude054]
FEATURE [Part::Feature] Face113
  shape: bbox 3.2 x 1.5 x 2e-07 mm, 1 faces, 0 solids (baked)
FEATURE [Part::Revolution] Revolve121  label="backCaseScrewRetainer002"
  Angle = 360
  Axis = (0,1,0)
  Base = (0,0,0)
  FaceMakerClass = Part::FaceMakerBullseye
  Placement = pos=(12.5,3,62) rot=(0,0,1;0rad)
  Solid = false
  Source = -> Face113
  Symmetric = false
FEATURE [Part::Feature] Face114
  shape: bbox 3.2 x 1.5 x 2e-07 mm, 1 faces, 0 solids (baked)
FEATURE [Part::Feature] Face115
  shape: bbox 3.2 x 1.5 x 2e-07 mm, 1 faces, 0 solids (baked)
FEATURE [Part::Feature] Face116
  shape: bbox 3.2 x 1.5 x 2e-07 mm, 1 faces, 0 solids (baked)
FEATURE [Part::Revolution] Revolve122  label="frontCaseScrewRetainer004"
  Angle = 360
  Axis = (0,1,0)
  Base = (0,0,0)
  FaceMakerClass = Part::FaceMakerBullseye
  Placement = pos=(89.5,3,68.5) rot=(0,0,1;0rad)
  Solid = false
  Source = -> Face115
  Symmetric = false
FEATURE [Part::Revolution] Revolve123  label="frontCaseScrewRetainer005"
  Angle = 360
  Axis = (0,1,0)
  Base = (0,0,0)
  FaceMakerClass = Part::FaceMakerBullseye
  Placement = pos=(89.5,3,3.5) rot=(0,0,1;0rad)
  Solid = false
  Source = -> Face116
  Symmetric = false
FEATURE [Part::Revolution] Revolve124  label="backCaseScrewRetainer003"
  Angle = 360
  Axis = (0,1,0)
  Base = (0,0,0)
  FaceMakerClass = Part::FaceMakerBullseye
  Placement = pos=(12.5,3,10) rot=(0,0,1;0rad)
  Solid = false
  Source = -> Face114
  Symmetric = false
FEATURE [Part::Feature] Face117
  shape: bbox 3.6 x 3.2 x 2e-07 mm, 1 faces, 0 solids (baked)
FEATURE [Part::Revolution] Revolve125  label="moreFrontCaseScrewRetainer004"
  Angle = 360
  Axis = (0,1,0)
  Base = (0,0,0)
  FaceMakerClass = Part::FaceMakerBullseye
  Placement = pos=(109.5,4.5,68.5) rot=(0,0,1;0rad)
  Solid = false
  Source = -> Face117
  Symmetric = false
FEATURE [Part::Feature] Face118
  shape: bbox 3.6 x 3.2 x 2e-07 mm, 1 faces, 0 solids (baked)
FEATURE [Part::Revolution] Revolve126  label="moreFrontCaseScrewRetainer005"
  Angle = 360
  Axis = (0,1,0)
  Base = (0,0,0)
  FaceMakerClass = Part::FaceMakerBullseye
  Placement = pos=(109.5,4.5,3.5) rot=(0,0,1;0rad)
  Solid = false
  Source = -> Face118
  Symmetric = false
FEATURE [Part::MultiFuse] Fusion096  label="screwRetainers001"
  Shapes = -> [Revolve126,Revolve125,Revolve124,Revolve123,Revolve122,Revolve121]
FEATURE [Part::Feature] Face119
  shape: bbox 10 x 16.5 x 2e-07 mm, 1 faces, 0 solids (baked)
FEATURE [Part::Revolution] Revolve130  label="plugHousing050"
  Angle = 360
  Axis = (0,1,0)
  Base = (0,0,0)
  FaceMakerClass = Part::FaceMakerBullseye
  Placement = pos=(0,0,36.15) rot=(0,0,1;0rad)
  Solid = false
  Source = -> Face119
  Symmetric = false
FEATURE [Part::Feature] Face120
  shape: bbox 10 x 16.5 x 2e-07 mm, 1 faces, 0 solids (baked)
FEATURE [Part::Feature] Face121
  shape: bbox 10 x 16.5 x 2e-07 mm, 1 faces, 0 solids (baked)
FEATURE [Part::Revolution] Revolve127  label="plugHousing047"
  Angle = 360
  Axis = (0,1,0)
  Base = (0,0,0)
  FaceMakerClass = Part::FaceMakerBullseye
  Placement = pos=(0,0,36.15) rot=(0,0,1;0rad)
  Solid = false
  Source = -> Face121
  Symmetric = false
FEATURE [Part::Feature] Face122
  shape: bbox 10 x 16.5 x 2e-07 mm, 1 faces, 0 solids (baked)
FEATURE [Part::Feature] Face123
  shape: bbox 10 x 16.5 x 2e-07 mm, 1 faces, 0 solids (baked)
FEATURE [Part::Revolution] Revolve128  label="plugHousing048"
  Angle = 360
  Axis = (0,1,0)
  Base = (0,0,0)
  FaceMakerClass = Part::FaceMakerBullseye
  Placement = pos=(0,0,36.15) rot=(0,0,1;0rad)
  Solid = false
  Source = -> Face123
  Symmetric = false
FEATURE [Part::MultiFuse] Fusion100  label="plugHousing054"
  Placement = pos=(0,0,0) rot=(0,0,1;1.5708rad)
  Shapes = -> [Revolve130,Revolve128]
FEATURE [Part::Feature] Face124
  shape: bbox 10 x 16.5 x 2e-07 mm, 1 faces, 0 solids (baked)
FEATURE [Part::Feature] Face125
  shape: bbox 10 x 16.5 x 2e-07 mm, 1 faces, 0 solids (baked)
FEATURE [Part::Revolution] Revolve129  label="plugHousing049"
  Angle = 360
  Axis = (0,1,0)
  Base = (0,0,0)
  FaceMakerClass = Part::FaceMakerBullseye
  Placement = pos=(0,0,36.15) rot=(0,0,1;0rad)
  Solid = false
  Source = -> Face125
  Symmetric = false
FEATURE [Part::Feature] Face126
  shape: bbox 10 x 16.5 x 2e-07 mm, 1 faces, 0 solids (baked)
FEATURE [Part::Revolution] Revolve131  label="plugHousing058"
  Angle = 360
  Axis = (0,1,0)
  Base = (0,0,0)
  FaceMakerClass = Part::FaceMakerBullseye
  Placement = pos=(0,0,36.15) rot=(0,0,1;0rad)
  Solid = false
  Source = -> Face120
  Symmetric = false
FEATURE [Part::MultiFuse] Fusion099  label="plugHousing053"
  Placement = pos=(0,0,0) rot=(0,0,1;1.5708rad)
  Shapes = -> [Revolve127,Revolve131]
FEATURE [Part::MultiFuse] Fusion102  label="plugHousing056"
  Placement = pos=(0,19,0) rot=(0,0,1;3.14159rad)
  Shapes = -> [Fusion100,Fusion099]
FEATURE [Part::Revolution] Revolve132  label="plugHousing059"
  Angle = 360
  Axis = (0,1,0)
  Base = (0,0,0)
  FaceMakerClass = Part::FaceMakerBullseye
  Placement = pos=(0,0,36.15) rot=(0,0,1;0rad)
  Solid = false
  Source = -> Face126
  Symmetric = false
FEATURE [Part::Revolution] Revolve133  label="plugHousing060"
  Angle = 360
  Axis = (0,1,0)
  Base = (0,0,0)
  FaceMakerClass = Part::FaceMakerBullseye
  Placement = pos=(0,0,36.15) rot=(0,0,1;0rad)
  Solid = false
  Source = -> Face122
  Symmetric = false
FEATURE [Part::MultiFuse] Fusion097  label="plugHousing051"
  Placement = pos=(0,0,0) rot=(0,0,1;1.5708rad)
  Shapes = -> [Revolve133,Revolve132]
FEATURE [Part::Revolution] Revolve134  label="plugHousing061"
  Angle = 360
  Axis = (0,1,0)
  Base = (0,0,0)
  FaceMakerClass = Part::FaceMakerBullseye
  Placement = pos=(0,0,36.15) rot=(0,0,1;0rad)
  Solid = false
  Source = -> Face124
  Symmetric = false
FEATURE [Part::MultiFuse] Fusion101  label="plugHousing055"
  Placement = pos=(0,0,0) rot=(0,0,1;1.5708rad)
  Shapes = -> [Revolve129,Revolve134]
FEATURE [Part::MultiFuse] Fusion098  label="plugHousing052"
  Placement = pos=(0,19,0) rot=(0,0,1;3.14159rad)
  Shapes = -> [Fusion097,Fusion101]
FEATURE [Part::MultiFuse] Fusion103  label="plugHousing057"
  Placement = pos=(122.621,0,-0.15) rot=(0,0,1;0rad)
  Shapes = -> [Fusion102,Fusion098]
FEATURE [Part::Box] Box028  label="Cube015"
  AttacherType = Attacher::AttachEngine3D
  Height = 28
  Length = 3
  Placement = pos=(110.7,19,22) rot=(0,0,1;0rad)
  Width = 15.7
FEATURE [Part::Cylinder] Cylinder044
  Angle = 360
  AttacherType = Attacher::AttachEngine3D
  Height = 20
  Placement = pos=(0,0,36.15) rot=(0,0,1;0rad)
  Radius = 10.3
FEATURE [Part::Cylinder] Cylinder045
  Angle = 360
  AttacherType = Attacher::AttachEngine3D
  Height = 10
  Placement = pos=(0,0,36.15) rot=(0,0,1;0rad)
  Radius = 4
FEATURE [Part::MultiFuse] Fusion104  label="removeToCreteHoleForPlugHousing040"
  Placement = pos=(70,19,36) rot=(0,1,0;1.5708rad)
  Shapes = -> [Cylinder044,Cylinder045]
FEATURE [Part::Cut] Cut046  label="plugHousingTab003"
  Base = -> Box028
  Tool = -> Fusion104
FEATURE [Part::MultiFuse] Fusion105  label="plugHousing062"
  Shapes = -> [Fusion103,Cut046]
FEATURE [Part::Fillet] Fillet042
  Base = -> Fusion105
  Edges = 1 edges r=2: [Edge25]
FEATURE [Part::Fillet] Fillet043  label="plugHousing063"
  Base = -> Fillet042
  Edges = 1 edges r=2: [Edge8]
  Placement = pos=(7,0,0) rot=(0,0,1;0rad)
FEATURE [Part::Feature] Face127
  shape: bbox 10 x 16.5 x 2e-07 mm, 1 faces, 0 solids (baked)
FEATURE [Part::Feature] Face128
  shape: bbox 10 x 16.5 x 2e-07 mm, 1 faces, 0 solids (baked)
FEATURE [Part::Revolution] Revolve137  label="plugHousing070"
  Angle = 360
  Axis = (0,1,0)
  Base = (0,0,0)
  FaceMakerClass = Part::FaceMakerBullseye
  Placement = pos=(0,0,36.15) rot=(0,0,1;0rad)
  Solid = false
  Source = -> Face127
  Symmetric = false
FEATURE [Part::Revolution] Revolve140  label="plugHousing073"
  Angle = 360
  Axis = (0,1,0)
  Base = (0,0,0)
  FaceMakerClass = Part::FaceMakerBullseye
  Placement = pos=(0,0,36.15) rot=(0,0,1;0rad)
  Solid = false
  Source = -> Face128
  Symmetric = false
FEATURE [Part::Feature] Face129
  shape: bbox 10 x 16.5 x 2e-07 mm, 1 faces, 0 solids (baked)
FEATURE [Part::Revolution] Revolve138  label="plugHousing071"
  Angle = 360
  Axis = (0,1,0)
  Base = (0,0,0)
  FaceMakerClass = Part::FaceMakerBullseye
  Placement = pos=(0,0,36.15) rot=(0,0,1;0rad)
  Solid = false
  Source = -> Face129
  Symmetric = false
FEATURE [Part::Feature] Face130
  shape: bbox 10 x 16.5 x 2e-07 mm, 1 faces, 0 solids (baked)
FEATURE [Part::Revolution] Revolve139  label="plugHousing072"
  Angle = 360
  Axis = (0,1,0)
  Base = (0,0,0)
  FaceMakerClass = Part::FaceMakerBullseye
  Placement = pos=(0,0,36.15) rot=(0,0,1;0rad)
  Solid = false
  Source = -> Face130
  Symmetric = false
FEATURE [Part::Feature] Face131
  shape: bbox 10 x 16.5 x 2e-07 mm, 1 faces, 0 solids (baked)
FEATURE [Part::Revolution] Revolve135  label="plugHousing068"
  Angle = 360
  Axis = (0,1,0)
  Base = (0,0,0)
  FaceMakerClass = Part::FaceMakerBullseye
  Placement = pos=(0,0,36.15) rot=(0,0,1;0rad)
  Solid = false
  Source = -> Face131
  Symmetric = false
FEATURE [Part::MultiFuse] Fusion112  label="plugHousing078"
  Placement = pos=(0,0,0) rot=(0,0,1;1.5708rad)
  Shapes = -> [Revolve135,Revolve139]
FEATURE [Part::Feature] Face132
  shape: bbox 10 x 16.5 x 2e-07 mm, 1 faces, 0 solids (baked)
FEATURE [Part::Revolution] Revolve141  label="plugHousing074"
  Angle = 360
  Axis = (0,1,0)
  Base = (0,0,0)
  FaceMakerClass = Part::FaceMakerBullseye
  Placement = pos=(0,0,36.15) rot=(0,0,1;0rad)
  Solid = false
  Source = -> Face132
  Symmetric = false
FEATURE [Part::MultiFuse] Fusion110  label="plugHousing076"
  Placement = pos=(0,0,0) rot=(0,0,1;1.5708rad)
  Shapes = -> [Revolve141,Revolve140]
FEATURE [Part::Feature] Face133
  shape: bbox 10 x 16.5 x 2e-07 mm, 1 faces, 0 solids (baked)
FEATURE [Part::Revolution] Revolve136  label="plugHousing069"
  Angle = 360
  Axis = (0,1,0)
  Base = (0,0,0)
  FaceMakerClass = Part::FaceMakerBullseye
  Placement = pos=(0,0,36.15) rot=(0,0,1;0rad)
  Solid = false
  Source = -> Face133
  Symmetric = false
FEATURE [Part::MultiFuse] Fusion106  label="plugHousing064"
  Placement = pos=(0,0,0) rot=(0,0,1;1.5708rad)
  Shapes = -> [Revolve138,Revolve136]
FEATURE [Part::MultiFuse] Fusion108  label="plugHousing066"
  Placement = pos=(0,19,0) rot=(0,0,1;3.14159rad)
  Shapes = -> [Fusion106,Fusion112]
FEATURE [Part::Feature] Face134
  shape: bbox 10 x 16.5 x 2e-07 mm, 1 faces, 0 solids (baked)
FEATURE [Part::Revolution] Revolve142  label="plugHousing075"
  Angle = 360
  Axis = (0,1,0)
  Base = (0,0,0)
  FaceMakerClass = Part::FaceMakerBullseye
  Placement = pos=(0,0,36.15) rot=(0,0,1;0rad)
  Solid = false
  Source = -> Face134
  Symmetric = false
FEATURE [Part::MultiFuse] Fusion107  label="plugHousing065"
  Placement = pos=(0,0,0) rot=(0,0,1;1.5708rad)
  Shapes = -> [Revolve137,Revolve142]
FEATURE [Part::MultiFuse] Fusion111  label="plugHousing077"
  Placement = pos=(0,19,0) rot=(0,0,1;3.14159rad)
  Shapes = -> [Fusion110,Fusion107]
FEATURE [Part::MultiFuse] Fusion109  label="plugHousing067"
  Placement = pos=(131.236,0,-0.15) rot=(0,0,1;0rad)
  Shapes = -> [Fusion108,Fusion111]
FEATURE [Part::MultiFuse] Fusion113  label="plugHousing079"
  Shapes = -> [Fillet043,Fusion109]
FEATURE [Part::Feature] Face135
  shape: bbox 3.5 x 17.8 x 2e-07 mm, 1 faces, 0 solids (baked)
FEATURE [Part::Revolution] Revolve143  label="removeToCreateScrewAndThreadedInsertHole049"
  Angle = 360
  Axis = (0,1,0)
  Base = (0,0,0)
  FaceMakerClass = Part::FaceMakerBullseye
  Placement = pos=(12.5,0,10) rot=(0,0,1;0rad)
  Solid = false
  Source = -> Face135
  Symmetric = false
FEATURE [Part::Feature] Face136
  shape: bbox 3.5 x 17.8 x 2e-07 mm, 1 faces, 0 solids (baked)
FEATURE [Part::Revolution] Revolve144  label="removeToCreateScrewAndThreadedInsertHole050"
  Angle = 360
  Axis = (0,1,0)
  Base = (0,0,0)
  FaceMakerClass = Part::FaceMakerBullseye
  Placement = pos=(12.5,0,62) rot=(0,0,1;0rad)
  Solid = false
  Source = -> Face136
  Symmetric = false
FEATURE [Part::Feature] Face137
  shape: bbox 3.5 x 17.8 x 2e-07 mm, 1 faces, 0 solids (baked)
FEATURE [Part::Revolution] Revolve145  label="removeToCreateScrewAndThreadedInsertHole051"
  Angle = 360
  Axis = (0,1,0)
  Base = (0,0,0)
  FaceMakerClass = Part::FaceMakerBullseye
  Placement = pos=(89.5,0,68.5) rot=(0,0,1;0rad)
  Solid = false
  Source = -> Face137
  Symmetric = false
FEATURE [Part::Feature] Face138
  shape: bbox 3.5 x 17.8 x 2e-07 mm, 1 faces, 0 solids (baked)
FEATURE [Part::Revolution] Revolve146  label="removeToCreateScrewAndThreadedInsertHole052"
  Angle = 360
  Axis = (0,1,0)
  Base = (0,0,0)
  FaceMakerClass = Part::FaceMakerBullseye
  Placement = pos=(89.5,0,3.5) rot=(0,0,1;0rad)
  Solid = false
  Source = -> Face138
  Symmetric = false
FEATURE [Part::Feature] Face139
  shape: bbox 3.5 x 17.8 x 2e-07 mm, 1 faces, 0 solids (baked)
FEATURE [Part::Revolution] Revolve147  label="removeToCreateScrewAndThreadedInsertHole053"
  Angle = 360
  Axis = (0,1,0)
  Base = (0,0,0)
  FaceMakerClass = Part::FaceMakerBullseye
  Placement = pos=(109.5,4.7,3.5) rot=(0,0,1;0rad)
  Solid = false
  Source = -> Face139
  Symmetric = false
FEATURE [Part::Feature] Face140
  shape: bbox 3.5 x 17.8 x 2e-07 mm, 1 faces, 0 solids (baked)
FEATURE [Part::Revolution] Revolve148  label="removeToCreateScrewAndThreadedInsertHole054"
  Angle = 360
  Axis = (0,1,0)
  Base = (0,0,0)
  FaceMakerClass = Part::FaceMakerBullseye
  Placement = pos=(109.5,4.7,68.5) rot=(0,0,1;0rad)
  Solid = false
  Source = -> Face140
  Symmetric = false
FEATURE [Part::MultiFuse] Fusion114  label="removeToCreateScrewAndThreadedInsertHole055"
  Shapes = -> [Revolve148,Revolve147,Revolve146,Revolve145,Revolve144,Revolve143]
FEATURE [Part::Cut] Cut047  label="casePillars004"
  Base = -> Cut037
  Tool = -> Fusion114
FEATURE [Part::Feature] Face141
  shape: bbox 3.5 x 17.8 x 2e-07 mm, 1 faces, 0 solids (baked)
FEATURE [Part::Feature] Face142
  shape: bbox 3.5 x 17.8 x 2e-07 mm, 1 faces, 0 solids (baked)
FEATURE [Part::Feature] Face143
  shape: bbox 3.5 x 17.8 x 2e-07 mm, 1 faces, 0 solids (baked)
FEATURE [Part::Revolution] Revolve149  label="removeToCreateScrewAndThreadedInsertHole057"
  Angle = 360
  Axis = (0,1,0)
  Base = (0,0,0)
  FaceMakerClass = Part::FaceMakerBullseye
  Placement = pos=(12.5,0,10) rot=(0,0,1;0rad)
  Solid = false
  Source = -> Face141
  Symmetric = false
FEATURE [Part::Feature] Face144
  shape: bbox 3.5 x 17.8 x 2e-07 mm, 1 faces, 0 solids (baked)
FEATURE [Part::Feature] Face145
  shape: bbox 3.5 x 17.8 x 2e-07 mm, 1 faces, 0 solids (baked)
FEATURE [Part::Feature] Face146
  shape: bbox 3.5 x 17.8 x 2e-07 mm, 1 faces, 0 solids (baked)
FEATURE [Part::Revolution] Revolve150  label="removeToCreateScrewAndThreadedInsertHole058"
  Angle = 360
  Axis = (0,1,0)
  Base = (0,0,0)
  FaceMakerClass = Part::FaceMakerBullseye
  Placement = pos=(12.5,0,62) rot=(0,0,1;0rad)
  Solid = false
  Source = -> Face146
  Symmetric = false
FEATURE [Part::Revolution] Revolve151  label="removeToCreateScrewAndThreadedInsertHole059"
  Angle = 360
  Axis = (0,1,0)
  Base = (0,0,0)
  FaceMakerClass = Part::FaceMakerBullseye
  Placement = pos=(89.5,0,68.5) rot=(0,0,1;0rad)
  Solid = false
  Source = -> Face143
  Symmetric = false
FEATURE [Part::Revolution] Revolve152  label="removeToCreateScrewAndThreadedInsertHole060"
  Angle = 360
  Axis = (0,1,0)
  Base = (0,0,0)
  FaceMakerClass = Part::FaceMakerBullseye
  Placement = pos=(89.5,0,3.5) rot=(0,0,1;0rad)
  Solid = false
  Source = -> Face142
  Symmetric = false
FEATURE [Part::Revolution] Revolve153  label="removeToCreateScrewAndThreadedInsertHole061"
  Angle = 360
  Axis = (0,1,0)
  Base = (0,0,0)
  FaceMakerClass = Part::FaceMakerBullseye
  Placement = pos=(109.5,4.7,3.5) rot=(0,0,1;0rad)
  Solid = false
  Source = -> Face145
  Symmetric = false
FEATURE [Part::Revolution] Revolve154  label="removeToCreateScrewAndThreadedInsertHole062"
  Angle = 360
  Axis = (0,1,0)
  Base = (0,0,0)
  FaceMakerClass = Part::FaceMakerBullseye
  Placement = pos=(109.5,4.7,68.5) rot=(0,0,1;0rad)
  Solid = false
  Source = -> Face144
  Symmetric = false
FEATURE [Part::MultiFuse] Fusion115  label="removeToCreateScrewAndThreadedInsertHole056"
  Shapes = -> [Revolve154,Revolve153,Revolve152,Revolve151,Revolve150,Revolve149]
FEATURE [Part::Feature] Face147
  shape: bbox 9.8 x 26.5 x 2e-07 mm, 1 faces, 0 solids (baked)
FEATURE [Part::Revolution] Revolve155
  Angle = 360
  Axis = (0,1,0)
  Base = (0,0,0)
  FaceMakerClass = Part::FaceMakerBullseye
  Placement = pos=(0,0,0) rot=(0,0,1;1.5708rad)
  Solid = false
  Source = -> Face147
  Symmetric = false
FEATURE [Part::Feature] Face148
  shape: bbox 9.8 x 26.5 x 2e-07 mm, 1 faces, 0 solids (baked)
FEATURE [Part::Revolution] Revolve156
  Angle = 360
  Axis = (0,1,0)
  Base = (0,0,0)
  FaceMakerClass = Part::FaceMakerBullseye
  Placement = pos=(0,0,0) rot=(0,0,1;1.5708rad)
  Solid = false
  Source = -> Face148
  Symmetric = false
FEATURE [Part::MultiFuse] Fusion116
  Placement = pos=(-18,19,36) rot=(0,0,1;0rad)
  Shapes = -> [Revolve156,Revolve155]
FEATURE [Part::Box] Box029  label="Cube016"
  AttacherType = Attacher::AttachEngine3D
  Height = 28
  Length = 3
  Placement = pos=(110.7,19,22) rot=(0,0,1;0rad)
  Width = 15.7
FEATURE [Part::Cylinder] Cylinder046
  Angle = 360
  AttacherType = Attacher::AttachEngine3D
  Height = 10
  Placement = pos=(0,0,36.15) rot=(0,0,1;0rad)
  Radius = 4
FEATURE [Part::Cylinder] Cylinder047
  Angle = 360
  AttacherType = Attacher::AttachEngine3D
  Height = 20
  Placement = pos=(0,0,36.15) rot=(0,0,1;0rad)
  Radius = 10.3
FEATURE [Part::MultiFuse] Fusion117  label="removeToCreteHoleForPlugHousing041"
  Placement = pos=(70,19,36) rot=(0,1,0;1.5708rad)
  Shapes = -> [Cylinder047,Cylinder046]
FEATURE [Part::Cut] Cut049  label="plugHousingTab004"
  Base = -> Box029
  Placement = pos=(-107.4,-14,0) rot=(0,0,1;0rad)
  Tool = -> Fusion117
FEATURE [Part::Box] Box030  label="Cube017"
  AttacherType = Attacher::AttachEngine3D
  Height = 28
  Length = 3
  Placement = pos=(110.7,19,22) rot=(0,0,1;0rad)
  Width = 15.7
FEATURE [Part::Cylinder] Cylinder048
  Angle = 360
  AttacherType = Attacher::AttachEngine3D
  Height = 10
  Placement = pos=(0,0,36.15) rot=(0,0,1;0rad)
  Radius = 4
FEATURE [Part::Cylinder] Cylinder049
  Angle = 360
  AttacherType = Attacher::AttachEngine3D
  Height = 20
  Placement = pos=(0,0,36.15) rot=(0,0,1;0rad)
  Radius = 10.3
FEATURE [Part::MultiFuse] Fusion118  label="removeToCreteHoleForPlugHousing042"
  Placement = pos=(70,19,36) rot=(0,1,0;1.5708rad)
  Shapes = -> [Cylinder049,Cylinder048]
FEATURE [Part::Cut] Cut050  label="plugHousingTab005"
  Base = -> Box030
  Placement = pos=(-107.4,-14,0) rot=(0,0,1;0rad)
  Tool = -> Fusion118
FEATURE [Part::MultiFuse] Fusion119
  Placement = pos=(9.6,23,0) rot=(0,0,1;3.14159rad)
  Shapes = -> [Cut049,Cut050]
FEATURE [Part::Box] Box031  label="Cube018"
  AttacherType = Attacher::AttachEngine3D
  Height = 10
  Length = 3
  Placement = pos=(3.3,4,12) rot=(0,0,1;0rad)
  Width = 10
FEATURE [Part::Fillet] Fillet044
  Base = -> Box031
  Edges = 1 edges r=2: [Edge11]
FEATURE [Part::Box] Box032  label="Cube019"
  AttacherType = Attacher::AttachEngine3D
  Height = 10
  Length = 3
  Placement = pos=(3.3,4,50) rot=(0,0,1;0rad)
  Width = 10
FEATURE [Part::Fillet] Fillet045
  Base = -> Box032
  Edges = 1 edges r=2: [Edge12]
FEATURE [Part::Box] Box033  label="Cube020"
  AttacherType = Attacher::AttachEngine3D
  Height = 28
  Length = 4
  Placement = pos=(5,0,22) rot=(0,0,1;0rad)
  Width = 10
FEATURE [Part::Fillet] Fillet046
  Base = -> Box033
  Edges = 1 edges r=1: [Edge7]
FEATURE [Part::Fillet] Fillet047
  Base = -> Fillet046
  Edges = 1 edges r=2: [Edge5]
FEATURE [Part::Fillet] Fillet048
  Base = -> Fillet047
  Edges = 1 edges r=2: [Edge2]
FEATURE [Part::Cylinder] Cylinder050
  Angle = 360
  AttacherType = Attacher::AttachEngine3D
  Height = 20
  Placement = pos=(0,0,36.15) rot=(0,0,1;0rad)
  Radius = 8.2
FEATURE [Part::Cylinder] Cylinder051
  Angle = 360
  AttacherType = Attacher::AttachEngine3D
  Height = 10
  Placement = pos=(0,0,36.15) rot=(0,0,1;0rad)
  Radius = 4
FEATURE [Part::MultiFuse] Fusion120  label="removeToCreteHoleForPlugHousing043"
  Placement = pos=(-42,19,36) rot=(0,1,0;1.5708rad)
  Shapes = -> [Cylinder050,Cylinder051]
FEATURE [Sketcher::SketchObject] Sketch067  label="topSketch018"
  FullyConstrained = true
  sketch-geometry (4):
    g0: LineSegment StartX=16.8446 StartY=31.512 StartZ=0 EndX=16.3251 EndY=34.4666 EndZ=0
    g1: ArcOfCircle CenterX=19 CenterY=19.2524 CenterZ=0 NormalX=0 NormalY=0 NormalZ=1 AngleXU=0 Radius=15.4476 StartAngle=1.74483 EndAngle=2.72717
    g2: ArcOfCircle CenterX=19 CenterY=19.2524 CenterZ=0 NormalX=0 NormalY=0 NormalZ=1 AngleXU=0 Radius=12.4476 StartAngle=1.74483 EndAngle=2.73189
    g3: LineSegment StartX=4.86004 StartY=25.4725 StartZ=0 EndX=7.58253 EndY=24.2107 EndZ=0
  constraints (7):
    c: Block(g0)
    c: Coincident(g1,g0)
    c: Coincident(g2,g0)
    c: Coincident(g3,g1)
    c: Coincident(g3,g2)
    c: Block(g1)
    c: Block(g2)
FEATURE [Part::Extrusion] Extrude058
  Base = -> Sketch067
  Dir = (0,0,1)
  DirMode = 2
  FaceMakerClass = Part::FaceMakerBullseye
  LengthFwd = 10
  LengthRev = 0
  Placement = pos=(0,0,31) rot=(0,0,1;0rad)
  Solid = true
  Symmetric = false
FEATURE [Part::Cut] Cut051
  Base = -> Extrude058
  Tool = -> Fusion120
FEATURE [Part::Fillet] Fillet049
  Base = -> Cut051
  Edges = 1 edges r=2: [Edge1]
FEATURE [Part::Fillet] Fillet050
  Base = -> Fillet049
  Edges = 1 edges r=2.5: [Edge1]
FEATURE [Part::Fillet] Fillet051
  Base = -> Fillet050
  Edges = 1 edges r=2.5: [Edge2]
FEATURE [Part::MultiFuse] Fusion121  label="wireHolder003"
  Shapes = -> [Fusion116,Fillet051]
FEATURE [Part::MultiFuse] Fusion122
  Shapes = -> [Fillet045,Fusion121]
FEATURE [Part::MultiFuse] Fusion123  label="wireHolder004"
  Shapes = -> [Fusion122,Fillet048]
FEATURE [Part::MultiFuse] Fusion124  label="wireHolder005"
  Shapes = -> [Fillet044,Fusion119,Fusion123]
FEATURE [Sketcher::SketchObject] Sketch068  label="topSketch019"
  FullyConstrained = true
  sketch-geometry (6):
    g0: LineSegment StartX=19 StartY=38 StartZ=0 EndX=117 EndY=38 EndZ=0
    g1: ArcOfCircle CenterX=19 CenterY=19 CenterZ=0 NormalX=0 NormalY=0 NormalZ=1 AngleXU=0 Radius=19 StartAngle=1.5708 EndAngle=3.14159
    g2: LineSegment StartX=117 StartY=38 StartZ=0 EndX=117 EndY=19 EndZ=0
    g3: LineSegment StartX=98 StartY=1.0161e-12 StartZ=0 EndX=5.22862e-06 EndY=1.0161e-12 EndZ=0
    g4: LineSegment StartX=5.22862e-06 StartY=19 StartZ=0 EndX=5.22862e-06 EndY=1.0161e-12 EndZ=0
    g5: ArcOfCircle CenterX=98 CenterY=19 CenterZ=0 NormalX=0 NormalY=0 NormalZ=1 AngleXU=0 Radius=19 StartAngle=4.71239 EndAngle=6.28319
  constraints (16):
    c: Horizontal(g0)
    c: Distance(g0) = 98
    c: Coincident(g1,g0)
    c: Block(g1)
    c: Coincident(g2,g0)
    c: Vertical(g2)
    c: Distance(g2) = 19
    c: Horizontal(g3)
    c: Coincident(g4,g1)
    c: Vertical(g4)
    c: Coincident(g3,g4)
    c: Block(g3)
    c: Coincident(g5,g2)
    c: Coincident(g5,g3)
    c: Block(g0)
    c: Block(g5)
FEATURE [Part::Extrusion] Extrude059  label="sideA002"
  Base = -> Sketch068
  Dir = (0,0,1)
  DirMode = 2
  FaceMakerClass = Part::FaceMakerBullseye
  LengthFwd = 3
  LengthRev = 0
  Placement = pos=(0,0,-2.7) rot=(0,0,1;0rad)
  Solid = true
  Symmetric = false
FEATURE [Sketcher::SketchObject] Sketch069  label="topSketch020"
  FullyConstrained = true
  sketch-geometry (6):
    g0: LineSegment StartX=19 StartY=38 StartZ=0 EndX=117 EndY=38 EndZ=0
    g1: ArcOfCircle CenterX=19 CenterY=19 CenterZ=0 NormalX=0 NormalY=0 NormalZ=1 AngleXU=0 Radius=19 StartAngle=1.5708 EndAngle=3.14159
    g2: LineSegment StartX=117 StartY=38 StartZ=0 EndX=117 EndY=19 EndZ=0
    g3: LineSegment StartX=98 StartY=1.0161e-12 StartZ=0 EndX=5.22862e-06 EndY=1.0161e-12 EndZ=0
    g4: LineSegment StartX=5.22862e-06 StartY=19 StartZ=0 EndX=5.22862e-06 EndY=1.0161e-12 EndZ=0
    g5: ArcOfCircle CenterX=98 CenterY=19 CenterZ=0 NormalX=0 NormalY=0 NormalZ=1 AngleXU=0 Radius=19 StartAngle=4.71239 EndAngle=6.28319
  constraints (16):
    c: Horizontal(g0)
    c: Distance(g0) = 98
    c: Coincident(g1,g0)
    c: Block(g1)
    c: Coincident(g2,g0)
    c: Vertical(g2)
    c: Distance(g2) = 19
    c: Horizontal(g3)
    c: Coincident(g4,g1)
    c: Vertical(g4)
    c: Coincident(g3,g4)
    c: Block(g3)
    c: Coincident(g5,g2)
    c: Coincident(g5,g3)
    c: Block(g0)
    c: Block(g5)
FEATURE [Part::Extrusion] Extrude060  label="sideB002"
  Base = -> Sketch069
  Dir = (0,0,1)
  DirMode = 2
  FaceMakerClass = Part::FaceMakerBullseye
  LengthFwd = 3
  LengthRev = 0
  Placement = pos=(0,0,71.7) rot=(0,0,1;0rad)
  Solid = true
  Symmetric = false
FEATURE [Part::MultiFuse] Fusion127  label="removeFromBottom001"
  Placement = pos=(2,0,0) rot=(0,0,1;0rad)
  Shapes = -> [Extrude059,Extrude060]
FEATURE [Part::Cylinder] Cylinder052
  Angle = 360
  AttacherType = Attacher::AttachEngine3D
  Height = 20
  Placement = pos=(0,0,36.15) rot=(0,0,1;0rad)
  Radius = 14
FEATURE [Part::Cylinder] Cylinder053
  Angle = 360
  AttacherType = Attacher::AttachEngine3D
  Height = 10
  Placement = pos=(0,0,36.15) rot=(0,0,1;0rad)
  Radius = 4
FEATURE [Part::MultiFuse] Fusion128  label="removeToCreteHoleForPlugHousing044"
  Placement = pos=(70,19,36) rot=(0,1,0;1.5708rad)
  Shapes = -> [Cylinder052,Cylinder053]
FEATURE [Part::Cut] Cut052  label="bottom011"
  Base = -> Extrude043
  Tool = -> Fusion128
FEATURE [Part::Cut] Cut054  label="bottom012"
  Base = -> Cut052
  Tool = -> Fusion115
FEATURE [Sketcher::SketchObject] Sketch070
  FullyConstrained = true
  Placement = pos=(117,19,0) rot=(0.57735,0.57735,0.57735;2.0944rad)
  sketch-geometry (48):
    g0: LineSegment StartX=-49.19 StartY=69.25 StartZ=0 EndX=-49.19 EndY=66.25 EndZ=0
    g1: LineSegment StartX=-49.19 StartY=63.5 StartZ=0 EndX=-49.19 EndY=60.5 EndZ=0
    g2: LineSegment StartX=-49.19 StartY=57.75 StartZ=0 EndX=-49.19 EndY=54.75 EndZ=0
    g3: LineSegment StartX=-49.19 StartY=52 StartZ=0 EndX=-49.19 EndY=49 EndZ=0
    g4: LineSegment StartX=-49.19 StartY=46.25 StartZ=0 EndX=-49.19 EndY=43.25 EndZ=0
    g5: LineSegment StartX=-49.19 StartY=40.5 StartZ=0 EndX=-49.19 EndY=37.5 EndZ=0
    g6: LineSegment StartX=-49.19 StartY=34.5 StartZ=0 EndX=-49.19 EndY=31.5 EndZ=0
    g7: LineSegment StartX=-49.19 StartY=28.75 StartZ=0 EndX=-49.19 EndY=25.75 EndZ=0
    g8: LineSegment StartX=-49.19 StartY=23 StartZ=0 EndX=-49.19 EndY=20 EndZ=0
    g9: LineSegment StartX=-49.19 StartY=17.25 StartZ=0 EndX=-49.19 EndY=14.25 EndZ=0
    g10: LineSegment StartX=-49.19 StartY=11.5 StartZ=0 EndX=-49.19 EndY=8.5 EndZ=0
    g11: LineSegment StartX=-49.19 StartY=5.75 StartZ=0 EndX=-49.19 EndY=2.75 EndZ=0
    g12: ArcOfCircle CenterX=-1.5 CenterY=67.75 CenterZ=0 NormalX=0 NormalY=0 NormalZ=1 AngleXU=0 Radius=1.5 StartAngle=4.71239 EndAngle=7.85398
    g13: ArcOfCircle CenterX=-1.5 CenterY=62 CenterZ=0 NormalX=0 NormalY=0 NormalZ=1 AngleXU=0 Radius=1.5 StartAngle=4.71239 EndAngle=7.85398
    g14: ArcOfCircle CenterX=-1.5 CenterY=56.25 CenterZ=0 NormalX=0 NormalY=0 NormalZ=1 AngleXU=0 Radius=1.5 StartAngle=4.71239 EndAngle=7.85398
    g15: ArcOfCircle CenterX=-11.49 CenterY=50.5 CenterZ=0 NormalX=0 NormalY=0 NormalZ=1 AngleXU=0 Radius=1.5 StartAngle=4.71239 EndAngle=7.85398
    g16: ArcOfCircle CenterX=-16.28 CenterY=44.75 CenterZ=0 NormalX=0 NormalY=0 NormalZ=1 AngleXU=0 Radius=1.5 StartAngle=4.71239 EndAngle=7.85398
    g17: ArcOfCircle CenterX=-18.2337 CenterY=39 CenterZ=0 NormalX=0 NormalY=0 NormalZ=1 AngleXU=0 Radius=1.5 StartAngle=4.71485 EndAngle=7.85398
    g18: ArcOfCircle CenterX=-16.2837 CenterY=27.25 CenterZ=0 NormalX=0 NormalY=0 NormalZ=1 AngleXU=0 Radius=1.5 StartAngle=4.71485 EndAngle=7.85398
    g19: ArcOfCircle CenterX=-18.2337 CenterY=33 CenterZ=0 NormalX=0 NormalY=0 NormalZ=1 AngleXU=0 Radius=1.5 StartAngle=4.71485 EndAngle=7.85398
    g20: ArcOfCircle CenterX=-11.49 CenterY=21.5 CenterZ=0 NormalX=0 NormalY=0 NormalZ=1 AngleXU=0 Radius=1.5 StartAngle=4.71239 EndAngle=7.85398
    g21: ArcOfCircle CenterX=-1.5 CenterY=4.25 CenterZ=0 NormalX=0 NormalY=0 NormalZ=1 AngleXU=0 Radius=1.5 StartAngle=4.71239 EndAngle=7.85398
    g22: ArcOfCircle CenterX=-1.5 CenterY=10 CenterZ=0 NormalX=0 NormalY=0 NormalZ=1 AngleXU=0 Radius=1.5 StartAngle=4.71239 EndAngle=7.85398
    g23: ArcOfCircle CenterX=-1.5 CenterY=15.75 CenterZ=0 NormalX=0 NormalY=0 NormalZ=1 AngleXU=0 Radius=1.5 StartAngle=4.71239 EndAngle=7.85398
    g24: LineSegment StartX=-49.19 StartY=69.25 StartZ=0 EndX=-1.5 EndY=69.25 EndZ=0
    g25: LineSegment StartX=-49.19 StartY=66.25 StartZ=0 EndX=-1.5 EndY=66.25 EndZ=0
    g26: LineSegment StartX=-49.19 StartY=63.5 StartZ=0 EndX=-1.5 EndY=63.5 EndZ=0
    g27: LineSegment StartX=-49.19 StartY=60.5 StartZ=0 EndX=-1.5 EndY=60.5 EndZ=0
    g28: LineSegment StartX=-49.19 StartY=57.75 StartZ=0 EndX=-1.5 EndY=57.75 EndZ=0
    g29: LineSegment StartX=-49.19 StartY=54.75 StartZ=0 EndX=-1.5 EndY=54.75 EndZ=0
    g30: LineSegment StartX=-49.19 StartY=52 StartZ=0 EndX=-11.49 EndY=52 EndZ=0
    g31: LineSegment StartX=-49.19 StartY=49 StartZ=0 EndX=-11.49 EndY=49 EndZ=0
    g32: LineSegment StartX=-49.19 StartY=46.25 StartZ=0 EndX=-16.28 EndY=46.25 EndZ=0
    g33: LineSegment StartX=-49.19 StartY=43.25 StartZ=0 EndX=-16.28 EndY=43.25 EndZ=0
    g34: LineSegment StartX=-49.19 StartY=40.5 StartZ=0 EndX=-18.2337 EndY=40.5 EndZ=0
    g35: LineSegment StartX=-49.19 StartY=37.5 StartZ=0 EndX=-18.23 EndY=37.5 EndZ=0
    g36: LineSegment StartX=-49.19 StartY=34.5 StartZ=0 EndX=-18.2337 EndY=34.5 EndZ=0
    g37: LineSegment StartX=-49.19 StartY=31.5 StartZ=0 EndX=-18.23 EndY=31.5 EndZ=0
    g38: LineSegment StartX=-49.19 StartY=28.75 StartZ=0 EndX=-16.2837 EndY=28.75 EndZ=0
    g39: LineSegment StartX=-49.19 StartY=25.75 StartZ=0 EndX=-16.28 EndY=25.75 EndZ=0
    g40: LineSegment StartX=-49.19 StartY=23 StartZ=0 EndX=-11.49 EndY=23 EndZ=0
    g41: LineSegment StartX=-49.19 StartY=20 StartZ=0 EndX=-11.49 EndY=20 EndZ=0
    g42: LineSegment StartX=-49.19 StartY=17.25 StartZ=0 EndX=-1.5 EndY=17.25 EndZ=0
    g43: LineSegment StartX=-49.19 StartY=14.25 StartZ=0 EndX=-1.5 EndY=14.25 EndZ=0
    g44: LineSegment StartX=-49.19 StartY=11.5 StartZ=0 EndX=-1.5 EndY=11.5 EndZ=0
    g45: LineSegment StartX=-49.19 StartY=8.5 StartZ=0 EndX=-1.5 EndY=8.5 EndZ=0
    g46: LineSegment StartX=-49.19 StartY=5.75 StartZ=0 EndX=-1.5 EndY=5.75 EndZ=0
    g47: LineSegment StartX=-49.19 StartY=2.75 StartZ=0 EndX=-1.5 EndY=2.75 EndZ=0
  constraints (120):
    c: Vertical(g0)
    c: Distance(g0) = 3
    c: Block(g0)
    c: Vertical(g1)
    c: Distance(g1) = 3
    c: Vertical(g2)
    c: Equal(g0,g2) = 3
    c: Block(g2)
    c: Vertical(g3)
    c: Equal(g1,g3) = 3
    c: Vertical(g4)
    c: Equal(g0,g4) = 3
    c: Block(g4)
    c: Vertical(g5)
    c: Equal(g1,g5) = 3
    c: Vertical(g6)
    c: Equal(g0,g6) = 3
    c: Block(g6)
    c: Vertical(g7)
    c: Equal(g1,g7) = 3
    c: Vertical(g8)
    c: Equal(g0,g8) = 3
    c: Block(g8)
    c: Vertical(g9)
    c: Equal(g1,g9) = 3
    c: Vertical(g10)
    c: Equal(g0,g10) = 3
    c: Block(g10)
    c: Vertical(g11)
    c: Equal(g1,g11) = 3
    c: Block(g12)
    c: Block(g13)
    c: Block(g14)
    c: Block(g15)
    c: Block(g16)
    c: Block(g17)
    c: Block(g18)
    c: Block(g19)
    c: Block(g20)
    c: Block(g21)
    c: Block(g22)
    c: Block(g23)
    c: Block(g11)
    c: Block(g9)
    c: Block(g7)
    c: Block(g5)
    c: Block(g3)
    c: Block(g1)
    c: Coincident(g24,g0)
    c: Coincident(g24,g12)
    c: Horizontal(g24)
    c: Coincident(g25,g0)
    c: Coincident(g25,g12)
    c: Horizontal(g25)
    c: Coincident(g26,g1)
    c: Coincident(g26,g13)
    c: Horizontal(g26)
    c: Coincident(g27,g1)
    c: Coincident(g27,g13)
    c: Horizontal(g27)
    c: Coincident(g28,g2)
    c: Coincident(g28,g14)
    c: Horizontal(g28)
    c: Coincident(g29,g2)
    c: Coincident(g29,g14)
    c: Horizontal(g29)
    c: Coincident(g30,g3)
    c: Coincident(g30,g15)
    c: Horizontal(g30)
    c: Coincident(g31,g3)
    c: Coincident(g31,g15)
    c: Horizontal(g31)
    c: Coincident(g32,g4)
    c: Coincident(g32,g16)
    c: Horizontal(g32)
    c: Coincident(g33,g4)
    c: Coincident(g33,g16)
    c: Horizontal(g33)
    c: Coincident(g34,g5)
    c: Coincident(g34,g17)
    c: Horizontal(g34)
    c: Coincident(g35,g5)
    c: Coincident(g35,g17)
    c: Horizontal(g35)
    c: Coincident(g36,g6)
    c: Coincident(g36,g19)
    c: Horizontal(g36)
    c: Coincident(g37,g6)
    c: Coincident(g37,g19)
    c: Horizontal(g37)
    c: Coincident(g38,g7)
    c: Coincident(g38,g18)
    c: Horizontal(g38)
    c: Coincident(g39,g7)
    c: Coincident(g39,g18)
    c: Horizontal(g39)
    c: Coincident(g40,g8)
    c: Coincident(g40,g20)
    c: Horizontal(g40)
    c: Coincident(g41,g8)
    c: Coincident(g41,g20)
    c: Horizontal(g41)
    c: Coincident(g42,g9)
    c: Coincident(g42,g23)
    c: Horizontal(g42)
    c: Coincident(g43,g9)
    c: Coincident(g43,g23)
    c: Horizontal(g43)
    c: Coincident(g44,g10)
    c: Coincident(g44,g22)
    c: Horizontal(g44)
    c: Coincident(g45,g10)
    c: Coincident(g45,g22)
    c: Horizontal(g45)
    c: Coincident(g46,g11)
    c: Coincident(g46,g21)
    c: Horizontal(g46)
    c: Coincident(g47,g11)
    c: Coincident(g47,g21)
    c: Horizontal(g47)
FEATURE [Part::Extrusion] Extrude061
  Base = -> Sketch070
  Dir = (1,0,0)
  DirMode = 2
  FaceMakerClass = Part::FaceMakerBullseye
  LengthFwd = 23
  LengthRev = 0
  Placement = pos=(-19,0,0) rot=(0,0,1;0rad)
  Solid = true
  Symmetric = false
FEATURE [Part::Fillet] Fillet052  label="removeToCreateVentalationHoles002"
  Base = -> Extrude061
  Edges = <same value as first occurrence — deduplicated (x6 in doc)>
  Placement = pos=(7,0.02,0) rot=(0,0,1;0rad)
FEATURE [Part::MultiFuse] Fusion130  label="bottom013"
  Shapes = -> [Cut054,Cut034]
FEATURE [Part::Cut] Cut055
  Base = -> Fusion130
  Tool = -> Fillet052
FEATURE [Part::Cylinder] Cylinder054
  Angle = 360
  AttacherType = Attacher::AttachEngine3D
  Height = 20
  Placement = pos=(0,0,36.15) rot=(0,0,1;0rad)
  Radius = 4
FEATURE [Sketcher::SketchObject] Sketch071  label="bottomSketch002"
  FullyConstrained = true
  sketch-geometry (32):
    g0: LineSegment StartX=3.3 StartY=-6.03275e-07 StartZ=0 EndX=98 EndY=-6.03275e-07 EndZ=0
    g1: ArcOfCircle CenterX=98 CenterY=19 CenterZ=0 NormalX=0 NormalY=0 NormalZ=1 AngleXU=0 Radius=19 StartAngle=4.71239 EndAngle=5.71103
    g2: LineSegment StartX=6.3 StartY=8 StartZ=0 EndX=3.3 EndY=8 EndZ=0
    g3: LineSegment StartX=3.3 StartY=8 StartZ=0 EndX=3.3 EndY=-6.03275e-07 EndZ=0
    g4: ArcOfCircle CenterX=8.3 CenterY=5 CenterZ=0 NormalX=0 NormalY=0 NormalZ=1 AngleXU=0 Radius=2 StartAngle=3.14159 EndAngle=4.71239
    g5: LineSegment StartX=6.3 StartY=8 StartZ=0 EndX=6.3 EndY=5 EndZ=0
    g6: ArcOfCircle CenterX=98 CenterY=19 CenterZ=0 NormalX=0 NormalY=0 NormalZ=1 AngleXU=0 Radius=12.7 StartAngle=4.71239 EndAngle=6.28319
    g7: LineSegment StartX=94.7 StartY=3 StartZ=0 EndX=8.3 EndY=3 EndZ=0
    g8-g12: Circle x5 (B-spline internal-alignment scaffolding for g13; pole/knot coordinates omitted)
    g13: BSplineCurve PolesCount=5 KnotsCount=3 Degree=3 IsPeriodic=0
    g14: GeomPoint X=98 Y=6.3 Z=0
    g15: GeomPoint X=96.3938 Y=4.71946 Z=0
    g16: GeomPoint X=94.7 Y=3 Z=0
    g17-g23: Circle x7 (B-spline internal-alignment scaffolding for g24; pole/knot coordinates omitted)
    g24: BSplineCurve PolesCount=7 KnotsCount=5 Degree=3 IsPeriodic=0
    g25-g29: GeomPoint x5 (B-spline internal-alignment scaffolding for g24; pole/knot coordinates omitted)
    g30: ArcOfCircle CenterX=98 CenterY=19 CenterZ=0 NormalX=0 NormalY=0 NormalZ=1 AngleXU=0 Radius=15.7 StartAngle=5.81226 EndAngle=6.28319
    g31: LineSegment StartX=110.7 StartY=19 StartZ=0 EndX=113.7 EndY=19 EndZ=0
  constraints (41):
    c: Horizontal(g0)
    c: Coincident(g1,g0)
    c: Block(g1)
    c: Horizontal(g2)
    c: Distance(g2) = 3
    c: Coincident(g3,g2)
    c: Vertical(g3)
    c: Coincident(g3,g0)
    c: Block(g4)
    c: Block(g2)
    c: Coincident(g5,g2)
    c: Coincident(g5,g4)
    c: Vertical(g5)
    c: Coincident(g6,g1)
    c: Block(g6)
    c: Coincident(g7,g4)
    c: Horizontal(g7)
    c: Block(g0)
    c: Block(g7)
    c: Block(g3)
    c: Coincident(g13,g6)
    c: Weight(g8) = 1
    c: Equal(g8, g9-g12) x4
    c: Coincident(g13,g7)
    c: InternalAlignment(g8-g12 -> g13) x5
    c: InternalAlignment(g14,g13)
    c: InternalAlignment(g15,g13)
    c: InternalAlignment(g16,g13)
    c: Block(g13)
    c: Weight(g17) = 1
    c: Equal(g17, g18-g23) x6
    c: Coincident(g24,g1)
    c: InternalAlignment(g17-g23 -> g24) x7
    c: InternalAlignment(g25-g29 -> g24) x5
    c: Block(g24)
    c: Coincident(g30,g24)
    c: Coincident(g31,g6)
    c: Coincident(g31,g30)
    c: Horizontal(g31)
    c: Block(g31)
    c: Block(g30)
FEATURE [Part::Extrusion] Extrude062  label="bottom014"
  Base = -> Sketch071
  Dir = (0,0,1)
  DirMode = 2
  FaceMakerClass = Part::FaceMakerBullseye
  LengthFwd = 71.4
  LengthRev = 0
  Placement = pos=(0,0,0.3) rot=(0,0,1;0rad)
  Solid = true
  Symmetric = false
FEATURE [Part::Fillet] Fillet054
  Base = -> Extrude062
  Edges = 1 edges r=2.4: [Edge17]
FEATURE [Part::Fillet] Fillet055  label="bottom015"
  Base = -> Fillet054
  Edges = 1 edges r=2.4: [Edge36]
FEATURE [Part::Cylinder] Cylinder055
  Angle = 360
  AttacherType = Attacher::AttachEngine3D
  Height = 10
  Placement = pos=(0,0,36.15) rot=(0,0,1;0rad)
  Radius = 4
FEATURE [Part::MultiFuse] Fusion131  label="removeToCreateHoleForPlugHousing002"
  Placement = pos=(70,19,36.15) rot=(0,1,0;1.5708rad)
  Shapes = -> [Cylinder054,Cylinder055]
FEATURE [Part::Cut] Cut056  label="Bottom001"
  Base = -> Fillet055
  Placement = pos=(9,0,0) rot=(0,0,1;0rad)
  Tool = -> Fusion131
FEATURE [Part::Cut] Cut057
  Base = -> Cut055
  Tool = -> Cut056
FEATURE [Sketcher::SketchObject] Sketch072  label="topSketch021"
  FullyConstrained = true
  sketch-geometry (4):
    g0: ArcOfCircle CenterX=105 CenterY=19 CenterZ=0 NormalX=0 NormalY=0 NormalZ=1 AngleXU=0 Radius=20.6155 StartAngle=5.54125 EndAngle=6.28319
    g1: ArcOfCircle CenterX=105 CenterY=19 CenterZ=0 NormalX=0 NormalY=0 NormalZ=1 AngleXU=0 Radius=13 StartAngle=5.54125 EndAngle=6.28319
    g2: LineSegment StartX=118 StartY=19 StartZ=0 EndX=125.616 EndY=19 EndZ=0
    g3: LineSegment StartX=114.583 StartY=10.2157 StartZ=0 EndX=120.197 EndY=5.06982 EndZ=0
  constraints (7):
    c: Block(g0)
    c: Block(g1)
    c: Coincident(g2,g1)
    c: Coincident(g2,g0)
    c: Horizontal(g2)
    c: Coincident(g3,g1)
    c: Coincident(g3,g0)
FEATURE [Part::Extrusion] Extrude063  label="bottomPlugHousingBit003"
  Base = -> Sketch072
  Dir = (0,0,1)
  DirMode = 2
  FaceMakerClass = Part::FaceMakerBullseye
  LengthFwd = 72
  LengthRev = 0
  Solid = true
  Symmetric = false
FEATURE [Part::Cylinder] Cylinder056
  Angle = 360
  AttacherType = Attacher::AttachEngine3D
  Height = 20
  Placement = pos=(0,0,36.15) rot=(0,0,1;0rad)
  Radius = 14.3
FEATURE [Part::Cylinder] Cylinder057
  Angle = 360
  AttacherType = Attacher::AttachEngine3D
  Height = 10
  Placement = pos=(0,0,36.15) rot=(0,0,1;0rad)
  Radius = 4
FEATURE [Part::Box] Box034  label="removeToCreteHoleForPlugHousing047"
  AttacherType = Attacher::AttachEngine3D
  Height = 28.6
  Length = 20
  Placement = pos=(106.15,0,21.7) rot=(0,0,1;0rad)
  Width = 19
FEATURE [Part::Cylinder] Cylinder058
  Angle = 360
  AttacherType = Attacher::AttachEngine3D
  Height = 20
  Placement = pos=(0,0,36.15) rot=(0,0,1;0rad)
  Radius = 14.3
FEATURE [Part::Cylinder] Cylinder059
  Angle = 360
  AttacherType = Attacher::AttachEngine3D
  Height = 10
  Placement = pos=(0,0,36.15) rot=(0,0,1;0rad)
  Radius = 4
FEATURE [Part::MultiFuse] Fusion134  label="removeToCreteHoleForPlugHousing046"
  Placement = pos=(70,19,36) rot=(0,1,0;1.5708rad)
  Shapes = -> [Cylinder058,Cylinder059]
FEATURE [Part::Cylinder] Cylinder060
  Angle = 360
  AttacherType = Attacher::AttachEngine3D
  Height = 20
  Placement = pos=(0,0,36.15) rot=(0,0,1;0rad)
  Radius = 14
FEATURE [Part::Cylinder] Cylinder061
  Angle = 360
  AttacherType = Attacher::AttachEngine3D
  Height = 10
  Placement = pos=(0,0,36.15) rot=(0,0,1;0rad)
  Radius = 4
FEATURE [Part::MultiFuse] Fusion135  label="removeToCreteHoleForPlugHousing048"
  Placement = pos=(70,19,36) rot=(0,1,0;1.5708rad)
  Shapes = -> [Cylinder060,Cylinder061]
FEATURE [Part::Box] Box035  label="removeToCreteHoleForPlugHousing049"
  AttacherType = Attacher::AttachEngine3D
  Height = 28.6
  Length = 20
  Placement = pos=(106.15,0,21.7) rot=(0,0,1;0rad)
  Width = 19
FEATURE [Part::MultiFuse] Fusion133  label="removeToCreteHoleForPlugHousing045"
  Placement = pos=(0,0,-28.3) rot=(0,0,1;0rad)
  Shapes = -> [Box035,Fusion134]
FEATURE [Part::MultiFuse] Fusion138  label="removeToCreteHoleForPlugHousing051"
  Placement = pos=(70,19,36) rot=(0,1,0;1.5708rad)
  Shapes = -> [Cylinder056,Cylinder057]
FEATURE [Part::MultiFuse] Fusion137  label="removeToCreteHoleForPlugHousing050"
  Placement = pos=(0,0,28.3) rot=(0,0,1;0rad)
  Shapes = -> [Box034,Fusion138]
FEATURE [Part::MultiFuse] Fusion132  label="removeToCreatePlugHousingBottomBit002"
  Shapes = -> [Fusion133,Fusion137]
FEATURE [Part::MultiFuse] Fusion136  label="removeToCreatePlugHousingBottomBit003"
  Shapes = -> [Fusion135,Fusion132]
FEATURE [Part::Cut] Cut058  label="bottomPlugHousingBit002"
  Base = -> Extrude063
  Placement = pos=(-0.09,0,0) rot=(0,0,1;0rad)
  Tool = -> Fusion136
FEATURE [Sketcher::SketchObject] Sketch073  label="bottomSketch003"
  FullyConstrained = true
  sketch-geometry (45):
    g0: LineSegment StartX=6.29999 StartY=8 StartZ=0 EndX=3.29999 EndY=8 EndZ=0
    g1: LineSegment StartX=3.29999 StartY=8 StartZ=0 EndX=3.29999 EndY=-6.03275e-07 EndZ=0
    g2: ArcOfCircle CenterX=8.29999 CenterY=5 CenterZ=0 NormalX=0 NormalY=0 NormalZ=1 AngleXU=0 Radius=2 StartAngle=3.14159 EndAngle=4.71239
    g3: LineSegment StartX=6.29999 StartY=8 StartZ=0 EndX=6.29999 EndY=5 EndZ=0
    g4: ArcOfCircle CenterX=105 CenterY=19 CenterZ=0 NormalX=0 NormalY=0 NormalZ=1 AngleXU=0 Radius=12.7 StartAngle=4.71239 EndAngle=5.94289
    g5-g11: Circle x7 (B-spline internal-alignment scaffolding for g12; pole/knot coordinates omitted)
    g12: BSplineCurve PolesCount=7 KnotsCount=5 Degree=3 IsPeriodic=0
    g13-g17: GeomPoint x5 (B-spline internal-alignment scaffolding for g12; pole/knot coordinates omitted)
    g18: ArcOfCircle CenterX=105 CenterY=19 CenterZ=0 NormalX=0 NormalY=0 NormalZ=1 AngleXU=0 Radius=15.7 StartAngle=5.81226 EndAngle=6.28319
    g19: BSplineCurve PolesCount=5 KnotsCount=3 Degree=3 IsPeriodic=0
    g20: LineSegment StartX=8.29999 StartY=3 StartZ=0 EndX=101.7 EndY=3 EndZ=0
    g21: LineSegment StartX=3.29999 StartY=-6.03275e-07 StartZ=0 EndX=105 EndY=-6.03275e-07 EndZ=0
    g22: LineSegment StartX=120.974 StartY=8.71251 StartZ=0 EndX=122.332 EndY=7.83778 EndZ=0
    g23: LineSegment StartX=105 StartY=-6.03274e-07 StartZ=0 EndX=113 EndY=-6.03274e-07 EndZ=0
    g24: ArcOfCircle CenterX=105 CenterY=19 CenterZ=0 NormalX=0 NormalY=0 NormalZ=1 AngleXU=0 Radius=20.6155 StartAngle=5.11091 EndAngle=5.71103
    g25: ArcOfCircle CenterX=117.7 CenterY=19 CenterZ=0 NormalX=0 NormalY=0 NormalZ=1 AngleXU=0 Radius=3 StartAngle=1.2e-15 EndAngle=2.10468
    g26: Circle CenterX=116.345 CenterY=16.3232 CenterZ=0 NormalX=0 NormalY=0 NormalZ=1 AngleXU=0 Radius=1
    g27: Circle CenterX=117.24 CenterY=15.7584 CenterZ=0 NormalX=0 NormalY=0 NormalZ=1 AngleXU=0 Radius=1
    g28: Circle CenterX=116.972 CenterY=14.7612 CenterZ=0 NormalX=0 NormalY=0 NormalZ=1 AngleXU=0 Radius=1
    g29: BSplineCurve PolesCount=3 KnotsCount=2 Degree=2 IsPeriodic=0
    g30: GeomPoint X=116.345 Y=16.3232 Z=0
    g31: GeomPoint X=116.972 Y=14.7612 Z=0
    g32: Circle CenterX=115.828 CenterY=17.157 CenterZ=0 NormalX=0 NormalY=0 NormalZ=1 AngleXU=0 Radius=1
    g33: Circle CenterX=115.841 CenterY=16.639 CenterZ=0 NormalX=0 NormalY=0 NormalZ=1 AngleXU=0 Radius=1
    g34: Circle CenterX=116.345 CenterY=16.3232 CenterZ=0 NormalX=0 NormalY=0 NormalZ=1 AngleXU=0 Radius=1
    g35: BSplineCurve PolesCount=3 KnotsCount=2 Degree=2 IsPeriodic=0
    g36: GeomPoint X=115.828 Y=17.157 Z=0
    g37: GeomPoint X=116.345 Y=16.3232 Z=0
    g38: LineSegment StartX=115.828 StartY=17.157 StartZ=0 EndX=115.828 EndY=20.8307 EndZ=0
    g39: Circle CenterX=115.828 CenterY=20.8307 CenterZ=0 NormalX=0 NormalY=0 NormalZ=1 AngleXU=0 Radius=1
    g40: Circle CenterX=115.831 CenterY=21.3396 CenterZ=0 NormalX=0 NormalY=0 NormalZ=1 AngleXU=0 Radius=1
    g41: Circle CenterX=116.173 CenterY=21.5825 CenterZ=0 NormalX=0 NormalY=0 NormalZ=1 AngleXU=0 Radius=1
    g42: BSplineCurve PolesCount=3 KnotsCount=2 Degree=2 IsPeriodic=0
    g43: GeomPoint X=115.828 Y=20.8307 Z=0
    g44: GeomPoint X=116.173 Y=21.5825 Z=0
  constraints (70):
    c: Horizontal(g0)
    c: Distance(g0) = 3
    c: Coincident(g1,g0)
    c: Vertical(g1)
    c: Block(g2)
    c: Block(g0)
    c: Coincident(g3,g0)
    c: Coincident(g3,g2)
    c: Vertical(g3)
    c: Block(g1)
    c: Block(g4)
    c: Coincident(g19,g4)
    c: Block(g19)
    c: Equal(g5, g6-g11) x6
    c: InternalAlignment(g5-g11 -> g12) x7
    c: InternalAlignment(g13-g17 -> g12) x5
    c: Block(g12)
    c: Coincident(g18,g12)
    c: Block(g18)
    c: Coincident(g20,g2)
    c: Coincident(g20,g19)
    c: Horizontal(g20)
    c: Distance(g20) = 93.4
    c: Coincident(g21,g1)
    c: Horizontal(g21)
    c: Distance(g21) = 101.7
    c: Horizontal(g23)
    c: Distance(g23) = 8
    c: Coincident(g24,g23)
    c: Block(g23)
    c: Coincident(g22,g24)
    c: Block(g24)
    c: Block(g22)
    c: Distance(g22) = 1.61553
    c: Coincident(g25,g18)
    c: Block(g25)
    c: Weight(g26) = 1
    c: Equal(g26,g27)
    c: Equal(g26,g28)
    c: Coincident(g29,g4)
    c: InternalAlignment(g26,g29)
    c: InternalAlignment(g27,g29)
    c: InternalAlignment(g28,g29)
    c: InternalAlignment(g30,g29)
    c: InternalAlignment(g31,g29)
    c: Block(g29)
    c: Weight(g32) = 1
    c: Equal(g32,g33)
    c: Equal(g32,g34)
    c: Coincident(g35,g29)
    c: InternalAlignment(g32,g35)
    c: InternalAlignment(g33,g35)
    c: InternalAlignment(g34,g35)
    c: InternalAlignment(g36,g35)
    c: InternalAlignment(g37,g35)
    c: Block(g35)
    c: Coincident(g38,g35)
    c: Vertical(g38)
    c: Block(g38)
    c: Coincident(g42,g38)
    c: Weight(g39) = 1
    c: Equal(g39,g40)
    c: Equal(g39,g41)
    c: Coincident(g42,g25)
    c: InternalAlignment(g39,g42)
    c: InternalAlignment(g40,g42)
    c: InternalAlignment(g41,g42)
    c: InternalAlignment(g43,g42)
    c: InternalAlignment(g44,g42)
    c: Block(g42)
FEATURE [Part::Extrusion] Extrude064  label="bottom016"
  Base = -> Sketch073
  Dir = (0,0,1)
  DirMode = 2
  FaceMakerClass = Part::FaceMakerBullseye
  LengthFwd = 71.4
  LengthRev = 0
  Placement = pos=(0,0,0.3) rot=(0,0,1;0rad)
  Solid = true
  Symmetric = false
FEATURE [Part::Revolution] Revolve157  label="removeToCreateScrewAndThreadedInsertHole063"
  Angle = 360
  Axis = (0,1,0)
  Base = (0,0,0)
  FaceMakerClass = Part::FaceMakerBullseye
  Placement = pos=(12.5,0,10) rot=(0,0,1;0rad)
  Solid = false
  Source = -> Face141
  Symmetric = false
FEATURE [Sketcher::SketchObject] Sketch074
  FullyConstrained = true
  Placement = pos=(117,19,0) rot=(0.57735,0.57735,0.57735;2.0944rad)
  sketch-geometry (48):
    g0: LineSegment StartX=-49.19 StartY=69.25 StartZ=0 EndX=-49.19 EndY=66.25 EndZ=0
    g1: LineSegment StartX=-49.19 StartY=63.5 StartZ=0 EndX=-49.19 EndY=60.5 EndZ=0
    g2: LineSegment StartX=-49.19 StartY=57.75 StartZ=0 EndX=-49.19 EndY=54.75 EndZ=0
    g3: LineSegment StartX=-49.19 StartY=52 StartZ=0 EndX=-49.19 EndY=49 EndZ=0
    g4: LineSegment StartX=-49.19 StartY=46.25 StartZ=0 EndX=-49.19 EndY=43.25 EndZ=0
    g5: LineSegment StartX=-49.19 StartY=40.5 StartZ=0 EndX=-49.19 EndY=37.5 EndZ=0
    g6: LineSegment StartX=-49.19 StartY=34.5 StartZ=0 EndX=-49.19 EndY=31.5 EndZ=0
    g7: LineSegment StartX=-49.19 StartY=28.75 StartZ=0 EndX=-49.19 EndY=25.75 EndZ=0
    g8: LineSegment StartX=-49.19 StartY=23 StartZ=0 EndX=-49.19 EndY=20 EndZ=0
    g9: LineSegment StartX=-49.19 StartY=17.25 StartZ=0 EndX=-49.19 EndY=14.25 EndZ=0
    g10: LineSegment StartX=-49.19 StartY=11.5 StartZ=0 EndX=-49.19 EndY=8.5 EndZ=0
    g11: LineSegment StartX=-49.19 StartY=5.75 StartZ=0 EndX=-49.19 EndY=2.75 EndZ=0
    g12: ArcOfCircle CenterX=-1.5 CenterY=67.75 CenterZ=0 NormalX=0 NormalY=0 NormalZ=1 AngleXU=0 Radius=1.5 StartAngle=4.71239 EndAngle=7.85398
    g13: ArcOfCircle CenterX=-1.5 CenterY=62 CenterZ=0 NormalX=0 NormalY=0 NormalZ=1 AngleXU=0 Radius=1.5 StartAngle=4.71239 EndAngle=7.85398
    g14: ArcOfCircle CenterX=-1.5 CenterY=56.25 CenterZ=0 NormalX=0 NormalY=0 NormalZ=1 AngleXU=0 Radius=1.5 StartAngle=4.71239 EndAngle=7.85398
    g15: ArcOfCircle CenterX=-11.49 CenterY=50.5 CenterZ=0 NormalX=0 NormalY=0 NormalZ=1 AngleXU=0 Radius=1.5 StartAngle=4.71239 EndAngle=7.85398
    g16: ArcOfCircle CenterX=-16.28 CenterY=44.75 CenterZ=0 NormalX=0 NormalY=0 NormalZ=1 AngleXU=0 Radius=1.5 StartAngle=4.71239 EndAngle=7.85398
    g17: ArcOfCircle CenterX=-18.2337 CenterY=39 CenterZ=0 NormalX=0 NormalY=0 NormalZ=1 AngleXU=0 Radius=1.5 StartAngle=4.71485 EndAngle=7.85398
    g18: ArcOfCircle CenterX=-16.2837 CenterY=27.25 CenterZ=0 NormalX=0 NormalY=0 NormalZ=1 AngleXU=0 Radius=1.5 StartAngle=4.71485 EndAngle=7.85398
    g19: ArcOfCircle CenterX=-18.2337 CenterY=33 CenterZ=0 NormalX=0 NormalY=0 NormalZ=1 AngleXU=0 Radius=1.5 StartAngle=4.71485 EndAngle=7.85398
    g20: ArcOfCircle CenterX=-11.49 CenterY=21.5 CenterZ=0 NormalX=0 NormalY=0 NormalZ=1 AngleXU=0 Radius=1.5 StartAngle=4.71239 EndAngle=7.85398
    g21: ArcOfCircle CenterX=-1.5 CenterY=4.25 CenterZ=0 NormalX=0 NormalY=0 NormalZ=1 AngleXU=0 Radius=1.5 StartAngle=4.71239 EndAngle=7.85398
    g22: ArcOfCircle CenterX=-1.5 CenterY=10 CenterZ=0 NormalX=0 NormalY=0 NormalZ=1 AngleXU=0 Radius=1.5 StartAngle=4.71239 EndAngle=7.85398
    g23: ArcOfCircle CenterX=-1.5 CenterY=15.75 CenterZ=0 NormalX=0 NormalY=0 NormalZ=1 AngleXU=0 Radius=1.5 StartAngle=4.71239 EndAngle=7.85398
    g24: LineSegment StartX=-49.19 StartY=69.25 StartZ=0 EndX=-1.5 EndY=69.25 EndZ=0
    g25: LineSegment StartX=-49.19 StartY=66.25 StartZ=0 EndX=-1.5 EndY=66.25 EndZ=0
    g26: LineSegment StartX=-49.19 StartY=63.5 StartZ=0 EndX=-1.5 EndY=63.5 EndZ=0
    g27: LineSegment StartX=-49.19 StartY=60.5 StartZ=0 EndX=-1.5 EndY=60.5 EndZ=0
    g28: LineSegment StartX=-49.19 StartY=57.75 StartZ=0 EndX=-1.5 EndY=57.75 EndZ=0
    g29: LineSegment StartX=-49.19 StartY=54.75 StartZ=0 EndX=-1.5 EndY=54.75 EndZ=0
    g30: LineSegment StartX=-49.19 StartY=52 StartZ=0 EndX=-11.49 EndY=52 EndZ=0
    g31: LineSegment StartX=-49.19 StartY=49 StartZ=0 EndX=-11.49 EndY=49 EndZ=0
    g32: LineSegment StartX=-49.19 StartY=46.25 StartZ=0 EndX=-16.28 EndY=46.25 EndZ=0
    g33: LineSegment StartX=-49.19 StartY=43.25 StartZ=0 EndX=-16.28 EndY=43.25 EndZ=0
    g34: LineSegment StartX=-49.19 StartY=40.5 StartZ=0 EndX=-18.2337 EndY=40.5 EndZ=0
    g35: LineSegment StartX=-49.19 StartY=37.5 StartZ=0 EndX=-18.23 EndY=37.5 EndZ=0
    g36: LineSegment StartX=-49.19 StartY=34.5 StartZ=0 EndX=-18.2337 EndY=34.5 EndZ=0
    g37: LineSegment StartX=-49.19 StartY=31.5 StartZ=0 EndX=-18.23 EndY=31.5 EndZ=0
    g38: LineSegment StartX=-49.19 StartY=28.75 StartZ=0 EndX=-16.2837 EndY=28.75 EndZ=0
    g39: LineSegment StartX=-49.19 StartY=25.75 StartZ=0 EndX=-16.28 EndY=25.75 EndZ=0
    g40: LineSegment StartX=-49.19 StartY=23 StartZ=0 EndX=-11.49 EndY=23 EndZ=0
    g41: LineSegment StartX=-49.19 StartY=20 StartZ=0 EndX=-11.49 EndY=20 EndZ=0
    g42: LineSegment StartX=-49.19 StartY=17.25 StartZ=0 EndX=-1.5 EndY=17.25 EndZ=0
    g43: LineSegment StartX=-49.19 StartY=14.25 StartZ=0 EndX=-1.5 EndY=14.25 EndZ=0
    g44: LineSegment StartX=-49.19 StartY=11.5 StartZ=0 EndX=-1.5 EndY=11.5 EndZ=0
    g45: LineSegment StartX=-49.19 StartY=8.5 StartZ=0 EndX=-1.5 EndY=8.5 EndZ=0
    g46: LineSegment StartX=-49.19 StartY=5.75 StartZ=0 EndX=-1.5 EndY=5.75 EndZ=0
    g47: LineSegment StartX=-49.19 StartY=2.75 StartZ=0 EndX=-1.5 EndY=2.75 EndZ=0
  constraints (120):
    c: Vertical(g0)
    c: Distance(g0) = 3
    c: Block(g0)
    c: Vertical(g1)
    c: Distance(g1) = 3
    c: Vertical(g2)
    c: Equal(g0,g2) = 3
    c: Block(g2)
    c: Vertical(g3)
    c: Equal(g1,g3) = 3
    c: Vertical(g4)
    c: Equal(g0,g4) = 3
    c: Block(g4)
    c: Vertical(g5)
    c: Equal(g1,g5) = 3
    c: Vertical(g6)
    c: Equal(g0,g6) = 3
    c: Block(g6)
    c: Vertical(g7)
    c: Equal(g1,g7) = 3
    c: Vertical(g8)
    c: Equal(g0,g8) = 3
    c: Block(g8)
    c: Vertical(g9)
    c: Equal(g1,g9) = 3
    c: Vertical(g10)
    c: Equal(g0,g10) = 3
    c: Block(g10)
    c: Vertical(g11)
    c: Equal(g1,g11) = 3
    c: Block(g12)
    c: Block(g13)
    c: Block(g14)
    c: Block(g15)
    c: Block(g16)
    c: Block(g17)
    c: Block(g18)
    c: Block(g19)
    c: Block(g20)
    c: Block(g21)
    c: Block(g22)
    c: Block(g23)
    c: Block(g11)
    c: Block(g9)
    c: Block(g7)
    c: Block(g5)
    c: Block(g3)
    c: Block(g1)
    c: Coincident(g24,g0)
    c: Coincident(g24,g12)
    c: Horizontal(g24)
    c: Coincident(g25,g0)
    c: Coincident(g25,g12)
    c: Horizontal(g25)
    c: Coincident(g26,g1)
    c: Coincident(g26,g13)
    c: Horizontal(g26)
    c: Coincident(g27,g1)
    c: Coincident(g27,g13)
    c: Horizontal(g27)
    c: Coincident(g28,g2)
    c: Coincident(g28,g14)
    c: Horizontal(g28)
    c: Coincident(g29,g2)
    c: Coincident(g29,g14)
    c: Horizontal(g29)
    c: Coincident(g30,g3)
    c: Coincident(g30,g15)
    c: Horizontal(g30)
    c: Coincident(g31,g3)
    c: Coincident(g31,g15)
    c: Horizontal(g31)
    c: Coincident(g32,g4)
    c: Coincident(g32,g16)
    c: Horizontal(g32)
    c: Coincident(g33,g4)
    c: Coincident(g33,g16)
    c: Horizontal(g33)
    c: Coincident(g34,g5)
    c: Coincident(g34,g17)
    c: Horizontal(g34)
    c: Coincident(g35,g5)
    c: Coincident(g35,g17)
    c: Horizontal(g35)
    c: Coincident(g36,g6)
    c: Coincident(g36,g19)
    c: Horizontal(g36)
    c: Coincident(g37,g6)
    c: Coincident(g37,g19)
    c: Horizontal(g37)
    c: Coincident(g38,g7)
    c: Coincident(g38,g18)
    c: Horizontal(g38)
    c: Coincident(g39,g7)
    c: Coincident(g39,g18)
    c: Horizontal(g39)
    c: Coincident(g40,g8)
    c: Coincident(g40,g20)
    c: Horizontal(g40)
    c: Coincident(g41,g8)
    c: Coincident(g41,g20)
    c: Horizontal(g41)
    c: Coincident(g42,g9)
    c: Coincident(g42,g23)
    c: Horizontal(g42)
    c: Coincident(g43,g9)
    c: Coincident(g43,g23)
    c: Horizontal(g43)
    c: Coincident(g44,g10)
    c: Coincident(g44,g22)
    c: Horizontal(g44)
    c: Coincident(g45,g10)
    c: Coincident(g45,g22)
    c: Horizontal(g45)
    c: Coincident(g46,g11)
    c: Coincident(g46,g21)
    c: Horizontal(g46)
    c: Coincident(g47,g11)
    c: Coincident(g47,g21)
    c: Horizontal(g47)
FEATURE [Part::Extrusion] Extrude065
  Base = -> Sketch074
  Dir = (1,0,0)
  DirMode = 2
  FaceMakerClass = Part::FaceMakerBullseye
  LengthFwd = 23
  LengthRev = 0
  Placement = pos=(-19,0,0) rot=(0,0,1;0rad)
  Solid = true
  Symmetric = false
FEATURE [Part::Fillet] Fillet056  label="removeToCreateVentalationHoles003"
  Base = -> Extrude065
  Edges = <same value as first occurrence — deduplicated (x6 in doc)>
  Placement = pos=(7,0.02,0) rot=(0,0,1;0rad)
FEATURE [Part::Revolution] Revolve158  label="removeToCreateScrewAndThreadedInsertHole065"
  Angle = 360
  Axis = (0,1,0)
  Base = (0,0,0)
  FaceMakerClass = Part::FaceMakerBullseye
  Placement = pos=(12.5,0,62) rot=(0,0,1;0rad)
  Solid = false
  Source = -> Face146
  Symmetric = false
FEATURE [Part::Revolution] Revolve159  label="removeToCreateScrewAndThreadedInsertHole066"
  Angle = 360
  Axis = (0,1,0)
  Base = (0,0,0)
  FaceMakerClass = Part::FaceMakerBullseye
  Placement = pos=(89.5,0,68.5) rot=(0,0,1;0rad)
  Solid = false
  Source = -> Face143
  Symmetric = false
FEATURE [Part::Revolution] Revolve160  label="removeToCreateScrewAndThreadedInsertHole067"
  Angle = 360
  Axis = (0,1,0)
  Base = (0,0,0)
  FaceMakerClass = Part::FaceMakerBullseye
  Placement = pos=(89.5,0,3.5) rot=(0,0,1;0rad)
  Solid = false
  Source = -> Face142
  Symmetric = false
FEATURE [Part::Revolution] Revolve161  label="removeToCreateScrewAndThreadedInsertHole068"
  Angle = 360
  Axis = (0,1,0)
  Base = (0,0,0)
  FaceMakerClass = Part::FaceMakerBullseye
  Placement = pos=(109.5,4.7,3.5) rot=(0,0,1;0rad)
  Solid = false
  Source = -> Face145
  Symmetric = false
FEATURE [Part::Revolution] Revolve162  label="removeToCreateScrewAndThreadedInsertHole069"
  Angle = 360
  Axis = (0,1,0)
  Base = (0,0,0)
  FaceMakerClass = Part::FaceMakerBullseye
  Placement = pos=(109.5,4.7,68.5) rot=(0,0,1;0rad)
  Solid = false
  Source = -> Face144
  Symmetric = false
FEATURE [Part::MultiFuse] Fusion141  label="removeToCreateScrewAndThreadedInsertHole064"
  Shapes = -> [Revolve162,Revolve161,Revolve160,Revolve159,Revolve158,Revolve157]
FEATURE [Part::Cylinder] Cylinder062
  Angle = 360
  AttacherType = Attacher::AttachEngine3D
  Height = 20
  Placement = pos=(0,0,36.15) rot=(0,0,1;0rad)
  Radius = 14
FEATURE [Part::Cylinder] Cylinder063
  Angle = 360
  AttacherType = Attacher::AttachEngine3D
  Height = 10
  Placement = pos=(0,0,36.15) rot=(0,0,1;0rad)
  Radius = 4
FEATURE [Part::MultiFuse] Fusion139  label="removeToCreteHoleForPlugHousing052"
  Placement = pos=(70,19,36) rot=(0,1,0;1.5708rad)
  Shapes = -> [Cylinder062,Cylinder063]
FEATURE [Part::Cut] Cut060  label="bottom017"
  Base = -> Extrude064
  Tool = -> Fusion139
FEATURE [Part::Cut] Cut061  label="bottom019"
  Base = -> Cut060
  Tool = -> Fusion141
FEATURE [Part::MultiFuse] Fusion140  label="bottom018"
  Shapes = -> [Cut061,Cut058]
FEATURE [Part::Cut] Cut059  label="bottom020"
  Base = -> Fusion140
  Tool = -> Fillet056
FEATURE [Part::Box] Box036  label="Cube021"
  AttacherType = Attacher::AttachEngine3D
  Height = 80
  Length = 26
  Placement = pos=(0,-1,-5) rot=(0,0,1;0rad)
  Width = 11
FEATURE [Part::Cut] Cut062  label="removeFromBottom002"
  Base = -> Cut057
  Tool = -> Box036
FEATURE [Part::Cut] Cut063
  Base = -> Cut059
  Tool = -> Cut062
FEATURE [Part::Cut] Cut064  label="pcbStands"
  Base = -> Fusion095
  Tool = -> Fusion127
FEATURE [Sketcher::SketchObject] Sketch075  label="topSketch022"
  FullyConstrained = true
  sketch-geometry (6):
    g0: LineSegment StartX=19 StartY=38 StartZ=0 EndX=117 EndY=38 EndZ=0
    g1: ArcOfCircle CenterX=19 CenterY=19 CenterZ=0 NormalX=0 NormalY=0 NormalZ=1 AngleXU=0 Radius=19 StartAngle=1.5708 EndAngle=3.14159
    g2: LineSegment StartX=117 StartY=38 StartZ=0 EndX=117 EndY=19 EndZ=0
    g3: LineSegment StartX=98 StartY=1.0161e-12 StartZ=0 EndX=5.22862e-06 EndY=1.0161e-12 EndZ=0
    g4: LineSegment StartX=5.22862e-06 StartY=19 StartZ=0 EndX=5.22862e-06 EndY=1.0161e-12 EndZ=0
    g5: ArcOfCircle CenterX=98 CenterY=19 CenterZ=0 NormalX=0 NormalY=0 NormalZ=1 AngleXU=0 Radius=19 StartAngle=4.71239 EndAngle=6.28319
  constraints (16):
    c: Horizontal(g0)
    c: Distance(g0) = 98
    c: Coincident(g1,g0)
    c: Block(g1)
    c: Coincident(g2,g0)
    c: Vertical(g2)
    c: Distance(g2) = 19
    c: Horizontal(g3)
    c: Coincident(g4,g1)
    c: Vertical(g4)
    c: Coincident(g3,g4)
    c: Block(g3)
    c: Coincident(g5,g2)
    c: Coincident(g5,g3)
    c: Block(g0)
    c: Block(g5)
FEATURE [Part::Extrusion] Extrude067  label="sideB003"
  Base = -> Sketch075
  Dir = (0,0,1)
  DirMode = 2
  FaceMakerClass = Part::FaceMakerBullseye
  LengthFwd = 3
  LengthRev = 0
  Placement = pos=(0,0,71.7) rot=(0,0,1;0rad)
  Solid = true
  Symmetric = false
FEATURE [Sketcher::SketchObject] Sketch076  label="topSketch023"
  FullyConstrained = true
  sketch-geometry (6):
    g0: LineSegment StartX=19 StartY=38 StartZ=0 EndX=117 EndY=38 EndZ=0
    g1: ArcOfCircle CenterX=19 CenterY=19 CenterZ=0 NormalX=0 NormalY=0 NormalZ=1 AngleXU=0 Radius=19 StartAngle=1.5708 EndAngle=3.14159
    g2: LineSegment StartX=117 StartY=38 StartZ=0 EndX=117 EndY=19 EndZ=0
    g3: LineSegment StartX=98 StartY=1.0161e-12 StartZ=0 EndX=5.22862e-06 EndY=1.0161e-12 EndZ=0
    g4: LineSegment StartX=5.22862e-06 StartY=19 StartZ=0 EndX=5.22862e-06 EndY=1.0161e-12 EndZ=0
    g5: ArcOfCircle CenterX=98 CenterY=19 CenterZ=0 NormalX=0 NormalY=0 NormalZ=1 AngleXU=0 Radius=19 StartAngle=4.71239 EndAngle=6.28319
  constraints (16):
    c: Horizontal(g0)
    c: Distance(g0) = 98
    c: Coincident(g1,g0)
    c: Block(g1)
    c: Coincident(g2,g0)
    c: Vertical(g2)
    c: Distance(g2) = 19
    c: Horizontal(g3)
    c: Coincident(g4,g1)
    c: Vertical(g4)
    c: Coincident(g3,g4)
    c: Block(g3)
    c: Coincident(g5,g2)
    c: Coincident(g5,g3)
    c: Block(g0)
    c: Block(g5)
FEATURE [Part::Extrusion] Extrude066  label="sideA003"
  Base = -> Sketch076
  Dir = (0,0,1)
  DirMode = 2
  FaceMakerClass = Part::FaceMakerBullseye
  LengthFwd = 3
  LengthRev = 0
  Placement = pos=(0,0,-2.7) rot=(0,0,1;0rad)
  Solid = true
  Symmetric = false
FEATURE [Part::MultiFuse] Fusion142  label="removeFromBottom003"
  Placement = pos=(2,0,0) rot=(0,0,1;0rad)
  Shapes = -> [Extrude066,Extrude067]
FEATURE [Part::Cut] Cut065  label="screwRetainers002"
  Base = -> Fusion096
  Tool = -> Fusion142
FEATURE [Sketcher::SketchObject] Sketch077
  FullyConstrained = true
  Placement = pos=(117,19,0) rot=(0.57735,0.57735,0.57735;2.0944rad)
  sketch-geometry (8):
    g0: LineSegment StartX=-49.19 StartY=63.5 StartZ=0 EndX=-49.19 EndY=60.5 EndZ=0
    g1: LineSegment StartX=-49.19 StartY=11.5 StartZ=0 EndX=-49.19 EndY=8.5 EndZ=0
    g2: ArcOfCircle CenterX=-1.5 CenterY=62 CenterZ=0 NormalX=0 NormalY=0 NormalZ=1 AngleXU=0 Radius=1.5 StartAngle=4.71239 EndAngle=7.85398
    g3: ArcOfCircle CenterX=-1.5 CenterY=10 CenterZ=0 NormalX=0 NormalY=0 NormalZ=1 AngleXU=0 Radius=1.5 StartAngle=4.71239 EndAngle=7.85398
    g4: LineSegment StartX=-49.19 StartY=63.5 StartZ=0 EndX=-1.5 EndY=63.5 EndZ=0
    g5: LineSegment StartX=-49.19 StartY=60.5 StartZ=0 EndX=-1.5 EndY=60.5 EndZ=0
    g6: LineSegment StartX=-49.19 StartY=11.5 StartZ=0 EndX=-1.5 EndY=11.5 EndZ=0
    g7: LineSegment StartX=-49.19 StartY=8.5 StartZ=0 EndX=-1.5 EndY=8.5 EndZ=0
  constraints (19):
    c: Vertical(g0)
    c: Distance(g0) = 3
    c: Vertical(g1)
    c: Block(g1)
    c: Block(g2)
    c: Block(g3)
    c: Block(g0)
    c: Coincident(g4,g0)
    c: Coincident(g4,g2)
    c: Horizontal(g4)
    c: Coincident(g5,g0)
    c: Coincident(g5,g2)
    c: Horizontal(g5)
    c: Coincident(g6,g1)
    c: Coincident(g6,g3)
    c: Horizontal(g6)
    c: Coincident(g7,g1)
    c: Coincident(g7,g3)
    c: Horizontal(g7)
FEATURE [Part::Extrusion] Extrude068
  Base = -> Sketch077
  Dir = (1,0,0)
  DirMode = 2
  FaceMakerClass = Part::FaceMakerBullseye
  LengthFwd = 10
  LengthRev = 0
  Solid = true
  Symmetric = false
FEATURE [Part::Fillet] Fillet057  label="removeFromtMoreFrontCaseScrewRetainers002"
  Base = -> Extrude068
  Edges = 4 edges r=1.49: [Edge6,Edge11,Edge18,Edge23]
  Placement = pos=(-12,0,0) rot=(0,0,1;0rad)
FEATURE [Sketcher::SketchObject] Sketch078
  FullyConstrained = true
  Placement = pos=(117,19,0) rot=(0.57735,0.57735,0.57735;2.0944rad)
  sketch-geometry (8):
    g0: LineSegment StartX=-49.19 StartY=69.25 StartZ=0 EndX=-49.19 EndY=66.25 EndZ=0
    g1: LineSegment StartX=-49.19 StartY=5.75 StartZ=0 EndX=-49.19 EndY=2.75 EndZ=0
    g2: ArcOfCircle CenterX=-1.5 CenterY=67.75 CenterZ=0 NormalX=0 NormalY=0 NormalZ=1 AngleXU=0 Radius=1.5 StartAngle=4.71239 EndAngle=7.85398
    g3: ArcOfCircle CenterX=-1.5 CenterY=4.25 CenterZ=0 NormalX=0 NormalY=0 NormalZ=1 AngleXU=0 Radius=1.5 StartAngle=4.71239 EndAngle=7.85398
    g4: LineSegment StartX=-49.19 StartY=69.25 StartZ=0 EndX=-1.5 EndY=69.25 EndZ=0
    g5: LineSegment StartX=-49.19 StartY=66.25 StartZ=0 EndX=-1.5 EndY=66.25 EndZ=0
    g6: LineSegment StartX=-49.19 StartY=5.75 StartZ=0 EndX=-1.5 EndY=5.75 EndZ=0
    g7: LineSegment StartX=-49.19 StartY=2.75 StartZ=0 EndX=-1.5 EndY=2.75 EndZ=0
  constraints (19):
    c: Vertical(g0)
    c: Distance(g0) = 3
    c: Block(g0)
    c: Vertical(g1)
    c: Block(g2)
    c: Block(g3)
    c: Block(g1)
    c: Coincident(g4,g0)
    c: Coincident(g4,g2)
    c: Horizontal(g4)
    c: Coincident(g5,g0)
    c: Coincident(g5,g2)
    c: Horizontal(g5)
    c: Coincident(g6,g1)
    c: Coincident(g6,g3)
    c: Horizontal(g6)
    c: Coincident(g7,g1)
    c: Coincident(g7,g3)
    c: Horizontal(g7)
FEATURE [Part::Extrusion] Extrude069
  Base = -> Sketch078
  Dir = (1,0,0)
  DirMode = 2
  FaceMakerClass = Part::FaceMakerBullseye
  LengthFwd = 10
  LengthRev = 0
  Solid = true
  Symmetric = false
FEATURE [Part::Fillet] Fillet058  label="removeFromtMoreFrontCaseScrewRetainers003"
  Base = -> Extrude069
  Edges = 4 edges r=1.49: [Edge6,Edge11,Edge18,Edge23]
  Placement = pos=(-4,0,0) rot=(0,0,1;0rad)
FEATURE [Part::Cut] Cut066
  Base = -> Cut065
  Tool = -> Fillet058
FEATURE [Part::Cut] Cut067  label="screwPillars"
  Base = -> Cut066
  Tool = -> Fillet057
FEATURE [Part::MultiFuse] Fusion143  label="bottom021"
  Shapes = -> [Cut031,Cut063]
FEATURE [Part::Cylinder] Cylinder
  Angle = 360
  AttacherType = Attacher::AttachEngine3D
  Height = 10
  Placement = pos=(20.65,12,4.68) rot=(1,0,0;1.5708rad)
  Radius = 2
FEATURE [Part::Cylinder] Cylinder064
  Angle = 360
  AttacherType = Attacher::AttachEngine3D
  Height = 10
  Placement = pos=(20.65,12,67.38) rot=(1,0,0;1.5708rad)
  Radius = 2
FEATURE [Part::Cylinder] Cylinder065
  Angle = 360
  AttacherType = Attacher::AttachEngine3D
  Height = 10
  Placement = pos=(77.15,12,67.38) rot=(1,0,0;1.5708rad)
  Radius = 2
FEATURE [Part::Cylinder] Cylinder066
  Angle = 360
  AttacherType = Attacher::AttachEngine3D
  Height = 10
  Placement = pos=(77.15,12,4.68) rot=(1,0,0;1.5708rad)
  Radius = 2
FEATURE [Part::MultiFuse] Fusion144  label="removeFromThreadedInsertHousing"
  Shapes = -> [Cylinder065,Cylinder064,Cylinder,Cylinder066]
FEATURE [Part::Cut] Cut068  label="pcbStands001"
  Base = -> Cut064
  Tool = -> Fusion144
FEATURE [Part::MultiFuse] Fusion145
  Shapes = -> [Cut068,Fusion143]
FEATURE [Part::MultiFuse] Fusion146
  Shapes = -> [Fusion145]
FEATURE [Part::MultiFuse] Fusion147  label="bottom022"
  Shapes = -> [Cut067,Fusion146]
FEATURE [Part::MultiFuse] Fusion148  label="casePillars005"
  Shapes = -> [Cut047,Fusion092]
FEATURE [Part::MultiFuse] Fusion149  label="bottom023"
  Shapes = -> [Fusion124,Fusion113,Fusion147]
FEATURE [Part::MultiFuse] Fusion150  label="topBits"
  Shapes = -> [Cut025,Fusion148,Cut030,Fillet034]
FEATURE [Part::Feature] Face149 .. Face152  x4 (patterned run collapsed; names and placements below)
  shape: bbox 3.2 x 1.5 x 2e-07 mm, 1 faces, 0 solids (baked)
FEATURE [Part::Feature] Face153
  shape: bbox 3.6 x 3.2 x 2e-07 mm, 1 faces, 0 solids (baked)
FEATURE [Part::Feature] Face154
  shape: bbox 3.6 x 3.2 x 2e-07 mm, 1 faces, 0 solids (baked)
FEATURE [Sketcher::SketchObject] Sketch079  label="topSketch024"
  FullyConstrained = true
  sketch-geometry (6):
    g0: LineSegment StartX=19 StartY=38 StartZ=0 EndX=117 EndY=38 EndZ=0
    g1: ArcOfCircle CenterX=19 CenterY=19 CenterZ=0 NormalX=0 NormalY=0 NormalZ=1 AngleXU=0 Radius=19 StartAngle=1.5708 EndAngle=3.14159
    g2: LineSegment StartX=117 StartY=38 StartZ=0 EndX=117 EndY=19 EndZ=0
    g3: LineSegment StartX=98 StartY=1.0161e-12 StartZ=0 EndX=5.22862e-06 EndY=1.0161e-12 EndZ=0
    g4: LineSegment StartX=5.22862e-06 StartY=19 StartZ=0 EndX=5.22862e-06 EndY=1.0161e-12 EndZ=0
    g5: ArcOfCircle CenterX=98 CenterY=19 CenterZ=0 NormalX=0 NormalY=0 NormalZ=1 AngleXU=0 Radius=19 StartAngle=4.71239 EndAngle=6.28319
  constraints (16):
    c: Horizontal(g0)
    c: Distance(g0) = 98
    c: Coincident(g1,g0)
    c: Block(g1)
    c: Coincident(g2,g0)
    c: Vertical(g2)
    c: Distance(g2) = 19
    c: Horizontal(g3)
    c: Coincident(g4,g1)
    c: Vertical(g4)
    c: Coincident(g3,g4)
    c: Block(g3)
    c: Coincident(g5,g2)
    c: Coincident(g5,g3)
    c: Block(g0)
    c: Block(g5)
FEATURE [Sketcher::SketchObject] Sketch080  label="topSketch025"
  FullyConstrained = true
  sketch-geometry (6):
    g0: LineSegment StartX=19 StartY=38 StartZ=0 EndX=117 EndY=38 EndZ=0
    g1: ArcOfCircle CenterX=19 CenterY=19 CenterZ=0 NormalX=0 NormalY=0 NormalZ=1 AngleXU=0 Radius=19 StartAngle=1.5708 EndAngle=3.14159
    g2: LineSegment StartX=117 StartY=38 StartZ=0 EndX=117 EndY=19 EndZ=0
    g3: LineSegment StartX=98 StartY=1.0161e-12 StartZ=0 EndX=5.22862e-06 EndY=1.0161e-12 EndZ=0
    g4: LineSegment StartX=5.22862e-06 StartY=19 StartZ=0 EndX=5.22862e-06 EndY=1.0161e-12 EndZ=0
    g5: ArcOfCircle CenterX=98 CenterY=19 CenterZ=0 NormalX=0 NormalY=0 NormalZ=1 AngleXU=0 Radius=19 StartAngle=4.71239 EndAngle=6.28319
  constraints (16):
    c: Horizontal(g0)
    c: Distance(g0) = 98
    c: Coincident(g1,g0)
    c: Block(g1)
    c: Coincident(g2,g0)
    c: Vertical(g2)
    c: Distance(g2) = 19
    c: Horizontal(g3)
    c: Coincident(g4,g1)
    c: Vertical(g4)
    c: Coincident(g3,g4)
    c: Block(g3)
    c: Coincident(g5,g2)
    c: Coincident(g5,g3)
    c: Block(g0)
    c: Block(g5)
FEATURE [Part::Extrusion] Extrude070  label="sideA004"
  Base = -> Sketch080
  Dir = (0,0,1)
  DirMode = 2
  FaceMakerClass = Part::FaceMakerBullseye
  LengthFwd = 3
  LengthRev = 0
  Placement = pos=(0,0,-2.7) rot=(0,0,1;0rad)
  Solid = true
  Symmetric = false
FEATURE [Sketcher::SketchObject] Sketch081
  FullyConstrained = true
  Placement = pos=(117,19,0) rot=(0.57735,0.57735,0.57735;2.0944rad)
  sketch-geometry (8):
    g0: LineSegment StartX=-49.19 StartY=63.5 StartZ=0 EndX=-49.19 EndY=60.5 EndZ=0
    g1: LineSegment StartX=-49.19 StartY=11.5 StartZ=0 EndX=-49.19 EndY=8.5 EndZ=0
    g2: ArcOfCircle CenterX=-1.5 CenterY=62 CenterZ=0 NormalX=0 NormalY=0 NormalZ=1 AngleXU=0 Radius=1.5 StartAngle=4.71239 EndAngle=7.85398
    g3: ArcOfCircle CenterX=-1.5 CenterY=10 CenterZ=0 NormalX=0 NormalY=0 NormalZ=1 AngleXU=0 Radius=1.5 StartAngle=4.71239 EndAngle=7.85398
    g4: LineSegment StartX=-49.19 StartY=63.5 StartZ=0 EndX=-1.5 EndY=63.5 EndZ=0
    g5: LineSegment StartX=-49.19 StartY=60.5 StartZ=0 EndX=-1.5 EndY=60.5 EndZ=0
    g6: LineSegment StartX=-49.19 StartY=11.5 StartZ=0 EndX=-1.5 EndY=11.5 EndZ=0
    g7: LineSegment StartX=-49.19 StartY=8.5 StartZ=0 EndX=-1.5 EndY=8.5 EndZ=0
  constraints (19):
    c: Vertical(g0)
    c: Distance(g0) = 3
    c: Vertical(g1)
    c: Block(g1)
    c: Block(g2)
    c: Block(g3)
    c: Block(g0)
    c: Coincident(g4,g0)
    c: Coincident(g4,g2)
    c: Horizontal(g4)
    c: Coincident(g5,g0)
    c: Coincident(g5,g2)
    c: Horizontal(g5)
    c: Coincident(g6,g1)
    c: Coincident(g6,g3)
    c: Horizontal(g6)
    c: Coincident(g7,g1)
    c: Coincident(g7,g3)
    c: Horizontal(g7)
FEATURE [Part::Extrusion] Extrude071  label="sideB004"
  Base = -> Sketch079
  Dir = (0,0,1)
  DirMode = 2
  FaceMakerClass = Part::FaceMakerBullseye
  LengthFwd = 3
  LengthRev = 0
  Placement = pos=(0,0,71.7) rot=(0,0,1;0rad)
  Solid = true
  Symmetric = false
FEATURE [Part::MultiFuse] Fusion152  label="removeFromBottom004"
  Placement = pos=(2,0,0) rot=(0,0,1;0rad)
  Shapes = -> [Extrude070,Extrude071]
FEATURE [Part::Extrusion] Extrude072
  Base = -> Sketch081
  Dir = (1,0,0)
  DirMode = 2
  FaceMakerClass = Part::FaceMakerBullseye
  LengthFwd = 10
  LengthRev = 0
  Solid = true
  Symmetric = false
FEATURE [Part::Fillet] Fillet059  label="removeFromtMoreFrontCaseScrewRetainers004"
  Base = -> Extrude072
  Edges = 4 edges r=1.49: [Edge6,Edge11,Edge18,Edge23]
  Placement = pos=(-12,0,0) rot=(0,0,1;0rad)
FEATURE [Sketcher::SketchObject] Sketch082
  FullyConstrained = true
  Placement = pos=(117,19,0) rot=(0.57735,0.57735,0.57735;2.0944rad)
  sketch-geometry (8):
    g0: LineSegment StartX=-49.19 StartY=69.25 StartZ=0 EndX=-49.19 EndY=66.25 EndZ=0
    g1: LineSegment StartX=-49.19 StartY=5.75 StartZ=0 EndX=-49.19 EndY=2.75 EndZ=0
    g2: ArcOfCircle CenterX=-1.5 CenterY=67.75 CenterZ=0 NormalX=0 NormalY=0 NormalZ=1 AngleXU=0 Radius=1.5 StartAngle=4.71239 EndAngle=7.85398
    g3: ArcOfCircle CenterX=-1.5 CenterY=4.25 CenterZ=0 NormalX=0 NormalY=0 NormalZ=1 AngleXU=0 Radius=1.5 StartAngle=4.71239 EndAngle=7.85398
    g4: LineSegment StartX=-49.19 StartY=69.25 StartZ=0 EndX=-1.5 EndY=69.25 EndZ=0
    g5: LineSegment StartX=-49.19 StartY=66.25 StartZ=0 EndX=-1.5 EndY=66.25 EndZ=0
    g6: LineSegment StartX=-49.19 StartY=5.75 StartZ=0 EndX=-1.5 EndY=5.75 EndZ=0
    g7: LineSegment StartX=-49.19 StartY=2.75 StartZ=0 EndX=-1.5 EndY=2.75 EndZ=0
  constraints (19):
    c: Vertical(g0)
    c: Distance(g0) = 3
    c: Block(g0)
    c: Vertical(g1)
    c: Block(g2)
    c: Block(g3)
    c: Block(g1)
    c: Coincident(g4,g0)
    c: Coincident(g4,g2)
    c: Horizontal(g4)
    c: Coincident(g5,g0)
    c: Coincident(g5,g2)
    c: Horizontal(g5)
    c: Coincident(g6,g1)
    c: Coincident(g6,g3)
    c: Horizontal(g6)
    c: Coincident(g7,g1)
    c: Coincident(g7,g3)
    c: Horizontal(g7)
FEATURE [Part::Extrusion] Extrude073
  Base = -> Sketch082
  Dir = (1,0,0)
  DirMode = 2
  FaceMakerClass = Part::FaceMakerBullseye
  LengthFwd = 10
  LengthRev = 0
  Solid = true
  Symmetric = false
FEATURE [Part::Fillet] Fillet060  label="removeFromtMoreFrontCaseScrewRetainers005"
  Base = -> Extrude073
  Edges = 4 edges r=1.49: [Edge6,Edge11,Edge18,Edge23]
  Placement = pos=(-4,0,0) rot=(0,0,1;0rad)
FEATURE [Part::Revolution] Revolve163  label="backCaseScrewRetainer004"
  Angle = 360
  Axis = (0,1,0)
  Base = (0,0,0)
  FaceMakerClass = Part::FaceMakerBullseye
  Placement = pos=(12.5,3,62) rot=(0,0,1;0rad)
  Solid = false
  Source = -> Face149
  Symmetric = false
FEATURE [Part::Revolution] Revolve164  label="frontCaseScrewRetainer006"
  Angle = 360
  Axis = (0,1,0)
  Base = (0,0,0)
  FaceMakerClass = Part::FaceMakerBullseye
  Placement = pos=(89.5,3,68.5) rot=(0,0,1;0rad)
  Solid = false
  Source = -> Face151
  Symmetric = false
FEATURE [Part::Revolution] Revolve165  label="frontCaseScrewRetainer007"
  Angle = 360
  Axis = (0,1,0)
  Base = (0,0,0)
  FaceMakerClass = Part::FaceMakerBullseye
  Placement = pos=(89.5,3,3.5) rot=(0,0,1;0rad)
  Solid = false
  Source = -> Face152
  Symmetric = false
FEATURE [Part::Revolution] Revolve166  label="backCaseScrewRetainer005"
  Angle = 360
  Axis = (0,1,0)
  Base = (0,0,0)
  FaceMakerClass = Part::FaceMakerBullseye
  Placement = pos=(12.5,3,10) rot=(0,0,1;0rad)
  Solid = false
  Source = -> Face150
  Symmetric = false
FEATURE [Part::Revolution] Revolve167  label="moreFrontCaseScrewRetainer006"
  Angle = 360
  Axis = (0,1,0)
  Base = (0,0,0)
  FaceMakerClass = Part::FaceMakerBullseye
  Placement = pos=(109.5,4.5,68.5) rot=(0,0,1;0rad)
  Solid = false
  Source = -> Face153
  Symmetric = false
FEATURE [Part::Revolution] Revolve168  label="moreFrontCaseScrewRetainer007"
  Angle = 360
  Axis = (0,1,0)
  Base = (0,0,0)
  FaceMakerClass = Part::FaceMakerBullseye
  Placement = pos=(109.5,4.5,3.5) rot=(0,0,1;0rad)
  Solid = false
  Source = -> Face154
  Symmetric = false
FEATURE [Part::MultiFuse] Fusion151  label="screwRetainers003"
  Shapes = -> [Revolve168,Revolve167,Revolve166,Revolve165,Revolve164,Revolve163]
FEATURE [Part::Cut] Cut069  label="screwRetainers004"
  Base = -> Fusion151
  Tool = -> Fusion152
FEATURE [Part::Cut] Cut070
  Base = -> Cut069
  Tool = -> Fillet060
FEATURE [Part::Cut] Cut071  label="screwPillars001"
  Base = -> Cut070
  Tool = -> Fillet059
FEATURE [Part::MultiFuse] Fusion153  label="bottom024"
  Shapes = -> [Fusion149,Cut071]
FEATURE [Part::Cylinder] Cylinder067
  Angle = 360
  AttacherType = Attacher::AttachEngine3D
  Height = 10
  Placement = pos=(20.65,12,4.68) rot=(1,0,0;1.5708rad)
  Radius = 2
FEATURE [Part::Cylinder] Cylinder068
  Angle = 360
  AttacherType = Attacher::AttachEngine3D
  Height = 10
  Placement = pos=(20.65,12,67.38) rot=(1,0,0;1.5708rad)
  Radius = 2
FEATURE [Part::Cylinder] Cylinder069
  Angle = 360
  AttacherType = Attacher::AttachEngine3D
  Height = 10
  Placement = pos=(77.15,12,67.38) rot=(1,0,0;1.5708rad)
  Radius = 2
FEATURE [Part::Cylinder] Cylinder070
  Angle = 360
  AttacherType = Attacher::AttachEngine3D
  Height = 10
  Placement = pos=(77.15,12,4.68) rot=(1,0,0;1.5708rad)
  Radius = 2
FEATURE [Part::MultiFuse] Fusion154  label="removeFromThreadedInsertHousing001"
  Shapes = -> [Cylinder069,Cylinder068,Cylinder067,Cylinder070]
FEATURE [Part::Cut] Cut072  label="bottom025"
  Base = -> Fusion153
  Tool = -> Fusion154
FEATURE [Image::ImagePlane] ImagePlane
  XSize = 339
  YSize = 72
FEATURE [Sketcher::SketchObject] Sketch083
  FullyConstrained = true
  MapMode = 5
  Support = -> [XY_Plane]
  sketch-geometry (338):
    g0: LineSegment StartX=-151.619 StartY=28.8932 StartZ=0 EndX=-140.819 EndY=28.8932 EndZ=0
    g1: LineSegment StartX=-151.619 StartY=24.0313 StartZ=0 EndX=-151.619 EndY=28.8932 EndZ=0
    g2: LineSegment StartX=-140.819 StartY=17.7713 StartZ=0 EndX=-151.619 EndY=17.7713 EndZ=0
    g3: LineSegment StartX=-151.619 StartY=17.7713 StartZ=0 EndX=-151.619 EndY=22.6313 EndZ=0
    g4: LineSegment StartX=-151.619 StartY=22.6313 StartZ=0 EndX=-145.128 EndY=22.6313 EndZ=0
    g5: LineSegment StartX=-145.128 StartY=24.0313 StartZ=0 EndX=-140.819 EndY=28.8932 EndZ=0
    g6: LineSegment StartX=-145.128 StartY=22.6313 StartZ=0 EndX=-140.819 EndY=17.7713 EndZ=0
    g7: ArcOfCircle CenterX=-155.157 CenterY=23.3323 CenterZ=0 NormalX=0 NormalY=0 NormalZ=1 AngleXU=0 Radius=6.92354 StartAngle=1.03434 EndAngle=5.24885
    g8: ArcOfCircle CenterX=-155.157 CenterY=23.3323 CenterZ=0 NormalX=0 NormalY=0 NormalZ=1 AngleXU=0 Radius=12.6269 StartAngle=1.28675 EndAngle=4.99643
    g9: LineSegment StartX=-151.619 StartY=35.4532 StartZ=0 EndX=-151.619 EndY=29.2832 EndZ=0
    g10: LineSegment StartX=-151.619 StartY=17.3813 StartZ=0 EndX=-151.619 EndY=11.2113 EndZ=0
    g11-g21: Circle x11 (B-spline internal-alignment scaffolding for g22; pole/knot coordinates omitted)
    g22: BSplineCurve PolesCount=11 KnotsCount=9 Degree=3 IsPeriodic=0
    g23-g31: GeomPoint x9 (B-spline internal-alignment scaffolding for g22; pole/knot coordinates omitted)
    g32-g49: Circle x18 (B-spline internal-alignment scaffolding for g50; pole/knot coordinates omitted)
    g50: BSplineCurve PolesCount=18 KnotsCount=16 Degree=3 IsPeriodic=0
    g51-g66: GeomPoint x16 (B-spline internal-alignment scaffolding for g50; pole/knot coordinates omitted)
    g67: LineSegment StartX=-117.124 StartY=30.093 StartZ=0 EndX=-117.603 EndY=26.5272 EndZ=0
    g68: LineSegment StartX=-117.603 StartY=17.8472 StartZ=0 EndX=-117.124 EndY=14.2659 EndZ=0
    g69: Ellipse CenterX=-109.671 CenterY=20.025 CenterZ=0 NormalX=0 NormalY=0 NormalZ=1 MajorRadius=3.34798 MinorRadius=2.71052 AngleXU=-1.56793
    g70: GeomPoint X=-109.666 Y=18.0598 Z=0
    g71: GeomPoint X=-109.677 Y=21.9902 Z=0
    g72: Ellipse CenterX=-109.671 CenterY=20.0123 CenterZ=0 NormalX=0 NormalY=0 NormalZ=1 MajorRadius=6.93002 MinorRadius=6.36273 AngleXU=-3.13976
    g73: GeomPoint X=-112.417 Y=20.0073 Z=0
    g74: GeomPoint X=-106.925 Y=20.0173 Z=0
    g75: Ellipse CenterX=-51.7682 CenterY=20.1463 CenterZ=0 NormalX=0 NormalY=0 NormalZ=1 MajorRadius=3.19279 MinorRadius=2.71052 AngleXU=-1.52774
    g76: GeomPoint X=-51.6955 Y=18.4606 Z=0
    g77: GeomPoint X=-51.8408 Y=21.832 Z=0
    g78: GeomPoint X=-54.5142 Y=20.1413 Z=0
    g79: GeomPoint X=-49.0221 Y=20.1513 Z=0
    g80: Ellipse CenterX=-51.7682 CenterY=20.1463 CenterZ=0 NormalX=0 NormalY=0 NormalZ=1 MajorRadius=6.93002 MinorRadius=6.36273 AngleXU=-3.13976
    g81: Ellipse CenterX=-22.8436 CenterY=20.1783 CenterZ=0 NormalX=0 NormalY=0 NormalZ=1 MajorRadius=3.31512 MinorRadius=2.71052 AngleXU=-1.60214
    g82: GeomPoint X=-22.9034 Y=18.2706 Z=0
    g83: GeomPoint X=-22.7838 Y=22.0861 Z=0
    g84: GeomPoint X=-25.5897 Y=20.1733 Z=0
    g85: GeomPoint X=-20.0976 Y=20.1833 Z=0
    g86: Ellipse CenterX=-22.8436 CenterY=20.1783 CenterZ=0 NormalX=0 NormalY=0 NormalZ=1 MajorRadius=6.93002 MinorRadius=6.36273 AngleXU=-3.13976
    g87: LineSegment StartX=-101.889 StartY=14.1107 StartZ=0 EndX=-97.7455 EndY=14.1107 EndZ=0
    g88: LineSegment StartX=-93.8155 StartY=14.1107 StartZ=0 EndX=-89.6755 EndY=14.1107 EndZ=0
    g89: LineSegment StartX=-85.7455 StartY=14.1107 StartZ=0 EndX=-81.6055 EndY=14.1107 EndZ=0
    g90: LineSegment StartX=-101.889 StartY=14.1107 StartZ=0 EndX=-101.889 EndY=25.9907 EndZ=0
    g91: LineSegment StartX=-101.889 StartY=25.9907 StartZ=0 EndX=-97.8594 EndY=25.9907 EndZ=0
    g92: LineSegment StartX=-97.8594 StartY=25.9907 StartZ=0 EndX=-97.8594 EndY=24.0907 EndZ=0
    g93: LineSegment StartX=-97.7455 StartY=14.1107 StartZ=0 EndX=-97.7455 EndY=19.9107 EndZ=0
    g94: LineSegment StartX=-89.6755 StartY=14.1107 StartZ=0 EndX=-89.6755 EndY=19.9107 EndZ=0
    g95: LineSegment StartX=-93.8155 StartY=14.1107 StartZ=0 EndX=-93.8155 EndY=21.0107 EndZ=0
    g96-g106: Circle x11 (B-spline internal-alignment scaffolding for g107; pole/knot coordinates omitted)
    g107: BSplineCurve PolesCount=11 KnotsCount=9 Degree=3 IsPeriodic=0
    g108-g116: GeomPoint x9 (B-spline internal-alignment scaffolding for g107; pole/knot coordinates omitted)
    g117: BSplineCurve PolesCount=11 KnotsCount=9 Degree=3 IsPeriodic=0
    g118-g125: Circle x8 (B-spline internal-alignment scaffolding for g126; pole/knot coordinates omitted)
    g126: BSplineCurve PolesCount=8 KnotsCount=6 Degree=3 IsPeriodic=0
    g127-g132: GeomPoint x6 (B-spline internal-alignment scaffolding for g126; pole/knot coordinates omitted)
    g133: BSplineCurve PolesCount=8 KnotsCount=6 Degree=3 IsPeriodic=0
    g134: LineSegment StartX=-85.7455 StartY=21.0107 StartZ=0 EndX=-85.7455 EndY=14.1107 EndZ=0
    g135: LineSegment StartX=-80.0879 StartY=14.1107 StartZ=0 EndX=-75.944 EndY=14.1107 EndZ=0
    g136: LineSegment StartX=-72.014 StartY=14.1107 StartZ=0 EndX=-67.874 EndY=14.1107 EndZ=0
    g137: LineSegment StartX=-63.944 StartY=14.1107 StartZ=0 EndX=-59.804 EndY=14.1107 EndZ=0
    g138: LineSegment StartX=-80.0879 StartY=14.1107 StartZ=0 EndX=-80.0879 EndY=25.9907 EndZ=0
    g139: LineSegment StartX=-80.0879 StartY=25.9907 StartZ=0 EndX=-76.0579 EndY=25.9907 EndZ=0
    g140: LineSegment StartX=-76.0579 StartY=25.9907 StartZ=0 EndX=-76.0579 EndY=24.0907 EndZ=0
    g141: LineSegment StartX=-75.944 StartY=14.1107 StartZ=0 EndX=-75.944 EndY=19.9107 EndZ=0
    g142: LineSegment StartX=-67.874 StartY=14.1107 StartZ=0 EndX=-67.874 EndY=19.9107 EndZ=0
    g143: LineSegment StartX=-72.014 StartY=14.1107 StartZ=0 EndX=-72.014 EndY=21.0107 EndZ=0
    g144-g148: Circle x5 (B-spline internal-alignment scaffolding for g149; pole/knot coordinates omitted)
    g149: BSplineCurve PolesCount=11 KnotsCount=9 Degree=3 IsPeriodic=0
    g150-g158: GeomPoint x9 (B-spline internal-alignment scaffolding for g149; pole/knot coordinates omitted)
    g159: BSplineCurve PolesCount=11 KnotsCount=9 Degree=3 IsPeriodic=0
    g160-g167: Circle x8 (B-spline internal-alignment scaffolding for g168; pole/knot coordinates omitted)
    g168: BSplineCurve PolesCount=8 KnotsCount=6 Degree=3 IsPeriodic=0
    g169-g174: GeomPoint x6 (B-spline internal-alignment scaffolding for g168; pole/knot coordinates omitted)
    g175: BSplineCurve PolesCount=8 KnotsCount=6 Degree=3 IsPeriodic=0
    g176: LineSegment StartX=-63.944 StartY=21.0107 StartZ=0 EndX=-63.944 EndY=14.1107 EndZ=0
    g177: LineSegment StartX=-59.804 StartY=14.1107 StartZ=0 EndX=-59.804 EndY=21.5868 EndZ=0
    g178: BSplineCurve PolesCount=4 KnotsCount=2 Degree=3 IsPeriodic=0
    g179: GeomPoint X=-59.804 Y=21.5868 Z=0
    g180: GeomPoint X=-60.2379 Y=24.0907 Z=0
    g181: LineSegment StartX=-81.6055 StartY=14.1107 StartZ=0 EndX=-81.6055 EndY=21.5868 EndZ=0
    g182: LineSegment StartX=-151.619 StartY=24.0313 StartZ=0 EndX=-145.128 EndY=24.0313 EndZ=0
    g183: Circle CenterX=-82.0394 CenterY=24.0907 CenterZ=0 NormalX=0 NormalY=0 NormalZ=1 AngleXU=0 Radius=1
    g184: Circle CenterX=-81.7131 CenterY=23.2736 CenterZ=0 NormalX=0 NormalY=0 NormalZ=1 AngleXU=0 Radius=1
    g185: Circle CenterX=-81.6055 CenterY=21.5868 CenterZ=0 NormalX=0 NormalY=0 NormalZ=1 AngleXU=0 Radius=1
    g186: BSplineCurve PolesCount=3 KnotsCount=2 Degree=2 IsPeriodic=0
    g187: GeomPoint X=-82.0394 Y=24.0907 Z=0
    g188: GeomPoint X=-81.6055 Y=21.5868 Z=0
    g189: Ellipse CenterX=-37.3522 CenterY=19.9515 CenterZ=0 NormalX=0 NormalY=0 NormalZ=1 MajorRadius=2.99755 MinorRadius=2.49 AngleXU=1.5708
    g190: GeomPoint X=-37.3522 Y=21.6203 Z=0
    g191: GeomPoint X=-37.3522 Y=18.2826 Z=0
    g192: ArcOfEllipse CenterX=-38.7647 CenterY=20.06 CenterZ=0 NormalX=0 NormalY=0 NormalZ=1 MajorRadius=6.30025 MinorRadius=5.3849 AngleXU=1.57276 StartAngle=5.50632 EndAngle=10.3035
    g193: GeomPoint X=-38.7711 Y=23.3304 Z=0
    g194: GeomPoint X=-38.7583 Y=16.7895 Z=0
    g195: LineSegment StartX=-34.6109 StartY=14.1107 StartZ=0 EndX=-30.8984 EndY=14.1107 EndZ=0
    g196: LineSegment StartX=-30.8984 StartY=14.1107 StartZ=0 EndX=-30.8984 EndY=31.1784 EndZ=0
    g197: LineSegment StartX=-30.8984 StartY=31.1784 StartZ=0 EndX=-34.9984 EndY=31.1784 EndZ=0
    g198: LineSegment StartX=-34.9984 StartY=24.5602 StartZ=0 EndX=-34.9984 EndY=31.1784 EndZ=0
    g199: LineSegment StartX=-34.6109 StartY=16.0476 StartZ=0 EndX=-34.6109 EndY=14.1107 EndZ=0
    g200: LineSegment StartX=-14.8781 StartY=14.1107 StartZ=0 EndX=-10.5106 EndY=14.1107 EndZ=0
    g201: LineSegment StartX=-14.8781 StartY=14.1107 StartZ=0 EndX=-14.8781 EndY=25.8504 EndZ=0
    g202: LineSegment StartX=-14.8781 StartY=25.8504 StartZ=0 EndX=-10.8534 EndY=25.8504 EndZ=0
    g203: LineSegment StartX=-10.8534 StartY=25.8504 StartZ=0 EndX=-10.8534 EndY=24.0923 EndZ=0
    g204: LineSegment StartX=-10.5106 StartY=14.1107 StartZ=0 EndX=-10.5106 EndY=19.7752 EndZ=0
    g205: LineSegment StartX=-5.96397 StartY=25.9304 StartZ=0 EndX=-5.96397 EndY=22.574 EndZ=0
    g206-g214: Circle x9 (B-spline internal-alignment scaffolding for g215; pole/knot coordinates omitted)
    g215: BSplineCurve PolesCount=9 KnotsCount=7 Degree=3 IsPeriodic=0
    g216-g222: GeomPoint x7 (B-spline internal-alignment scaffolding for g215; pole/knot coordinates omitted)
    g223-g232: Circle x10 (B-spline internal-alignment scaffolding for g233; pole/knot coordinates omitted)
    g233: BSplineCurve PolesCount=10 KnotsCount=8 Degree=3 IsPeriodic=0
    g234-g241: GeomPoint x8 (B-spline internal-alignment scaffolding for g233; pole/knot coordinates omitted)
    g242: LineSegment StartX=-1.58923 StartY=21.0696 StartZ=0 EndX=2.62034 EndY=21.0696 EndZ=0
    g243: LineSegment StartX=-1.55856 StartY=18.7342 StartZ=0 EndX=6.45946 EndY=18.7342 EndZ=0
    g244: LineSegment StartX=5.29231 StartY=17.386 StartZ=0 EndX=5.29231 EndY=14.3674 EndZ=0
    g245-g269: Circle x25 (B-spline internal-alignment scaffolding for g270; pole/knot coordinates omitted)
    g270: BSplineCurve PolesCount=25 KnotsCount=23 Degree=3 IsPeriodic=0
    g271-g293: GeomPoint x23 (B-spline internal-alignment scaffolding for g270; pole/knot coordinates omitted)
    g294-g304: Circle x11 (B-spline internal-alignment scaffolding for g305; pole/knot coordinates omitted)
    g305: BSplineCurve PolesCount=11 KnotsCount=9 Degree=3 IsPeriodic=0
    g306-g314: GeomPoint x9 (B-spline internal-alignment scaffolding for g305; pole/knot coordinates omitted)
    g315-g326: Circle x12 (B-spline internal-alignment scaffolding for g327; pole/knot coordinates omitted)
    g327: BSplineCurve PolesCount=12 KnotsCount=10 Degree=3 IsPeriodic=0
    g328-g337: GeomPoint x10 (B-spline internal-alignment scaffolding for g327; pole/knot coordinates omitted)
  constraints (252):
    c: Coincident(g1,g0)
    c: Horizontal(g0)
    c: Vertical(g1)
    c: Coincident(g2,g3)
    c: Coincident(g3,g4)
    c: Horizontal(g4)
    c: Horizontal(g2)
    c: Vertical(g3)
    c: Block(g1)
    c: Distance(g3) = 4.86
    c: Block(g4)
    c: Distance(g0) = 10.8
    c: Distance(g2) = 10.8
    c: Coincident(g5,g0)
    c: Coincident(g6,g4)
    c: Coincident(g6,g2)
    c: Block(g8)
    c: Block(g7)
    c: Coincident(g9,g8)
    c: Coincident(g9,g7)
    c: Vertical(g9)
    c: Coincident(g10,g7)
    c: Coincident(g10,g8)
    c: Vertical(g10)
    c: Weight(g11) = 1
    c: Equal(g11, g12-g21) x10
    c: InternalAlignment(g11-g21 -> g22) x11
    c: InternalAlignment(g23-g31 -> g22) x9
    c: Block(g22)
    c: Weight(g32) = 1
    c: Equal(g32, g33-g49) x17
    c: InternalAlignment(g32-g49 -> g50) x18
    c: InternalAlignment(g51-g66 -> g50) x16
    c: Block(g50)
    c: Coincident(g67,g50)
    c: Coincident(g67,g22)
    c: Coincident(g68,g22)
    c: Coincident(g68,g50)
    c: InternalAlignment(g70,g69)
    c: InternalAlignment(g71,g69)
    c: Block(g69)
    c: InternalAlignment(g73,g72)
    c: InternalAlignment(g74,g72)
    c: Block(g72)
    c: InternalAlignment(g76,g75)
    c: InternalAlignment(g77,g75)
    c: InternalAlignment(g78,g80)
    c: InternalAlignment(g79,g80)
    c: Block(g80)
    c: Coincident(g75,g80)
    c: Block(g75)
    c: InternalAlignment(g82,g81)
    c: InternalAlignment(g83,g81)
    c: InternalAlignment(g84,g86)
    c: InternalAlignment(g85,g86)
    c: Block(g86)
    c: Coincident(g81,g86)
    c: Block(g81)
    c: Horizontal(g87)
    c: Block(g87)
    c: Horizontal(g88)
    c: Distance(g88) = 4.14
    c: Horizontal(g89)
    c: Equal(g88,g89) = 4.14
    c: Block(g89)
    c: Block(g88)
    c: Coincident(g90,g87)
    c: Vertical(g90)
    c: Distance(g90) = 11.88
    c: Coincident(g91,g90)
    c: Horizontal(g91)
    c: Coincident(g92,g91)
    c: Vertical(g92)
    c: Distance(g91) = 4.03
    c: Distance(g92) = 1.9
    c: Coincident(g93,g87)
    c: Vertical(g93)
    c: Vertical(g94)
    c: Coincident(g94,g88)
    c: Distance(g93) = 5.8
    c: Distance(g94) = 5.8
    c: Vertical(g95)
    c: Coincident(g95,g88)
    c: Distance(g95) = 6.9
    c: Coincident(g107,g92)
    c: Weight(g96) = 1
    c: Equal(g96, g97-g106) x10
    c: InternalAlignment(g96-g106 -> g107) x11
    c: InternalAlignment(g108-g116 -> g107) x9
    c: Block(g107)
    c: Block(g117)
    c: Coincident(g126,g93)
    c: Weight(g118) = 1
    c: Equal(g118, g119-g125) x7
    c: Coincident(g126,g95)
    c: InternalAlignment(g118-g125 -> g126) x8
    c: InternalAlignment(g127-g132 -> g126) x6
    c: Coincident(g133,g94)
    c: Block(g126)
    c: Block(g133)
    c: Coincident(g134,g133)
    c: Coincident(g134,g89)
    c: Vertical(g134)
    c: Horizontal(g135)
    c: Block(g135)
    c: Horizontal(g136)
    c: Equal(g88,g136) = 4.14
    c: Horizontal(g137)
    c: Equal(g136,g137) = 4.14
    c: Block(g137)
    c: Block(g136)
    c: Coincident(g138,g135)
    c: Vertical(g138)
    c: Equal(g90,g138) = 11.88
    c: Coincident(g139,g138)
    c: Horizontal(g139)
    c: Coincident(g140,g139)
    c: Vertical(g140)
    c: Equal(g91,g139) = 4.03
    c: Equal(g92,g140) = 1.9
    c: Coincident(g141,g135)
    c: Vertical(g141)
    c: Vertical(g142)
    c: Coincident(g142,g136)
    c: Equal(g93,g141) = 5.8
    c: Equal(g94,g142) = 5.8
    c: Vertical(g143)
    c: Coincident(g143,g136)
    c: Equal(g95,g143) = 6.9
    c: Coincident(g149,g140)
    c: Equal(g96,g144) = 1
    c: Equal(g144, g145-g148) x4
    c: InternalAlignment(g144-g148 -> g149) x5
    c: InternalAlignment(g150-g158 -> g149) x9
    c: Block(g149)
    c: Block(g159)
    c: Coincident(g168,g141)
    c: Equal(g118,g160) = 1
    c: Equal(g160, g161-g167) x7
    c: Coincident(g168,g143)
    c: InternalAlignment(g160-g167 -> g168) x8
    c: InternalAlignment(g169-g174 -> g168) x6
    c: Coincident(g175,g142)
    c: Block(g168)
    c: Block(g175)
    c: Coincident(g176,g175)
    c: Coincident(g176,g137)
    c: Vertical(g176)
    c: Coincident(g177,g137)
    c: Vertical(g177)
    c: Coincident(g178,g177)
    c: Coincident(g178,g159)
    c: InternalAlignment(g179,g178)
    c: InternalAlignment(g180,g178)
    c: Block(g178)
    c: Vertical(g181)
    c: Coincident(g181,g89)
    c: Block(g5)
    c: Coincident(g182,g1)
    c: Coincident(g182,g5)
    c: Horizontal(g182)
    c: Coincident(g186,g117)
    c: Weight(g183) = 1
    c: Equal(g183,g184)
    c: Equal(g183,g185)
    c: Coincident(g186,g181)
    c: InternalAlignment(g183,g186)
    c: InternalAlignment(g184,g186)
    c: InternalAlignment(g185,g186)
    c: InternalAlignment(g187,g186)
    c: InternalAlignment(g188,g186)
    c: Block(g186)
    c: InternalAlignment(g190,g189)
    c: InternalAlignment(g191,g189)
    c: Block(g189)
    c: InternalAlignment(g193,g192)
    c: InternalAlignment(g194,g192)
    c: Block(g192)
    c: Horizontal(g195)
    c: Block(g195)
    c: Coincident(g196,g195)
    c: Vertical(g196)
    c: Block(g196)
    c: Distance(g195) = 3.71244
    c: Coincident(g197,g196)
    c: Horizontal(g197)
    c: Distance(g197) = 4.1
    c: Coincident(g198,g192)
    c: Coincident(g198,g197)
    c: Vertical(g198)
    c: Block(g198)
    c: Coincident(g199,g192)
    c: Coincident(g199,g195)
    c: Vertical(g199)
    c: Block(g199)
    c: Horizontal(g200)
    c: Block(g200)
    c: Coincident(g201,g200)
    c: Vertical(g201)
    c: Block(g201)
    c: Coincident(g202,g201)
    c: Horizontal(g202)
    c: Block(g202)
    c: Coincident(g203,g202)
    c: Vertical(g203)
    c: Block(g203)
    c: Coincident(g204,g200)
    c: Vertical(g204)
    c: Block(g204)
    c: Coincident(g215,g203)
    c: Weight(g206) = 1
    c: Equal(g206, g207-g214) x8
    c: Coincident(g215,g205)
    c: InternalAlignment(g206-g214 -> g215) x9
    c: InternalAlignment(g216-g222 -> g215) x7
    c: Coincident(g233,g204)
    c: Weight(g223) = 1
    c: Equal(g223, g224-g232) x9
    c: Coincident(g233,g205)
    c: InternalAlignment(g223-g232 -> g233) x10
    c: InternalAlignment(g234-g241 -> g233) x8
    c: Vertical(g205)
    c: Block(g205)
    c: Block(g215)
    c: Block(g233)
    c: Horizontal(g242)
    c: Horizontal(g243)
    c: Block(g242)
    c: Block(g243)
    c: Vertical(g244)
    c: Block(g244)
    c: Coincident(g270,g243)
    c: Weight(g245) = 1
    c: Equal(g245, g246-g269) x24
    c: Coincident(g270,g244)
    c: InternalAlignment(g245-g269 -> g270) x25
    c: InternalAlignment(g271-g293 -> g270) x23
    c: Coincident(g305,g242)
    c: Weight(g294) = 1
    c: Equal(g294, g295-g304) x10
    c: Coincident(g305,g242)
    c: InternalAlignment(g294-g304 -> g305) x11
    c: InternalAlignment(g306-g314 -> g305) x9
    c: Block(g305)
    c: Coincident(g327,g243)
    c: Weight(g315) = 1
    c: Equal(g315, g316-g326) x11
    c: Coincident(g327,g244)
    c: InternalAlignment(g315-g326 -> g327) x12
    c: InternalAlignment(g328-g337 -> g327) x10
    c: Block(g327)
    c: Block(g270)
FEATURE [PartDesign::Body] Body  label="CommodoreLogoAndText"
  Group = -> [Sketch083]
  Origin = -> Origin
FEATURE [Part::Extrusion] Extrude074  label="CommodoreLogoAndText001"
  Base = -> Sketch083
  Dir = (0,0,1)
  DirMode = 2
  FaceMakerClass = Part::FaceMakerBullseye
  LengthFwd = 10
  LengthRev = 0
  Solid = true
  Symmetric = false
FEATURE [Part::FeaturePython] Clone  label="CommodoreLogoAndTextScale"  # Draft clone (typed FeaturePython)
  AttacherType = Attacher::AttachEngine3D
  Fuse = false
  Objects = -> [Extrude074]
  Placement = pos=(111,5.37,-11.6) rot=(0,0,1;0rad)
  Scale = (0.62,0.62,1)
FEATURE [Part::Mirroring] Part__Mirroring  label="CommodoreLogoAndTextScale (Mirror #1)"
  Base = (0,0,0)
  Normal = (1,0,0)
  Placement = pos=(123.576,0,0) rot=(0,0,1;0rad)
  Source = -> Clone
FEATURE [Sketcher::SketchObject] Sketch084
  FullyConstrained = true
  MapMode = 5
  Support = -> [XY_Plane001]
  sketch-geometry (338):
    g0: LineSegment StartX=-151.619 StartY=28.8932 StartZ=0 EndX=-140.819 EndY=28.8932 EndZ=0
    g1: LineSegment StartX=-151.619 StartY=24.0313 StartZ=0 EndX=-151.619 EndY=28.8932 EndZ=0
    g2: LineSegment StartX=-140.819 StartY=17.7713 StartZ=0 EndX=-151.619 EndY=17.7713 EndZ=0
    g3: LineSegment StartX=-151.619 StartY=17.7713 StartZ=0 EndX=-151.619 EndY=22.6313 EndZ=0
    g4: LineSegment StartX=-151.619 StartY=22.6313 StartZ=0 EndX=-145.128 EndY=22.6313 EndZ=0
    g5: LineSegment StartX=-145.128 StartY=24.0313 StartZ=0 EndX=-140.819 EndY=28.8932 EndZ=0
    g6: LineSegment StartX=-145.128 StartY=22.6313 StartZ=0 EndX=-140.819 EndY=17.7713 EndZ=0
    g7: ArcOfCircle CenterX=-155.157 CenterY=23.3323 CenterZ=0 NormalX=0 NormalY=0 NormalZ=1 AngleXU=0 Radius=6.92354 StartAngle=1.03434 EndAngle=5.24885
    g8: ArcOfCircle CenterX=-155.157 CenterY=23.3323 CenterZ=0 NormalX=0 NormalY=0 NormalZ=1 AngleXU=0 Radius=12.6269 StartAngle=1.28675 EndAngle=4.99643
    g9: LineSegment StartX=-151.619 StartY=35.4532 StartZ=0 EndX=-151.619 EndY=29.2832 EndZ=0
    g10: LineSegment StartX=-151.619 StartY=17.3813 StartZ=0 EndX=-151.619 EndY=11.2113 EndZ=0
    g11-g21: Circle x11 (B-spline internal-alignment scaffolding for g22; pole/knot coordinates omitted)
    g22: BSplineCurve PolesCount=11 KnotsCount=9 Degree=3 IsPeriodic=0
    g23-g31: GeomPoint x9 (B-spline internal-alignment scaffolding for g22; pole/knot coordinates omitted)
    g32-g49: Circle x18 (B-spline internal-alignment scaffolding for g50; pole/knot coordinates omitted)
    g50: BSplineCurve PolesCount=18 KnotsCount=16 Degree=3 IsPeriodic=0
    g51-g66: GeomPoint x16 (B-spline internal-alignment scaffolding for g50; pole/knot coordinates omitted)
    g67: LineSegment StartX=-117.124 StartY=30.093 StartZ=0 EndX=-117.603 EndY=26.5272 EndZ=0
    g68: LineSegment StartX=-117.603 StartY=17.8472 StartZ=0 EndX=-117.124 EndY=14.2659 EndZ=0
    g69: Ellipse CenterX=-109.671 CenterY=20.025 CenterZ=0 NormalX=0 NormalY=0 NormalZ=1 MajorRadius=3.34798 MinorRadius=2.71052 AngleXU=-1.56793
    g70: GeomPoint X=-109.666 Y=18.0598 Z=0
    g71: GeomPoint X=-109.677 Y=21.9902 Z=0
    g72: Ellipse CenterX=-109.671 CenterY=20.0123 CenterZ=0 NormalX=0 NormalY=0 NormalZ=1 MajorRadius=6.93002 MinorRadius=6.36273 AngleXU=-3.13976
    g73: GeomPoint X=-112.417 Y=20.0073 Z=0
    g74: GeomPoint X=-106.925 Y=20.0173 Z=0
    g75: Ellipse CenterX=-51.7682 CenterY=20.1463 CenterZ=0 NormalX=0 NormalY=0 NormalZ=1 MajorRadius=3.19279 MinorRadius=2.71052 AngleXU=-1.52774
    g76: GeomPoint X=-51.6955 Y=18.4606 Z=0
    g77: GeomPoint X=-51.8408 Y=21.832 Z=0
    g78: GeomPoint X=-54.5142 Y=20.1413 Z=0
    g79: GeomPoint X=-49.0221 Y=20.1513 Z=0
    g80: Ellipse CenterX=-51.7682 CenterY=20.1463 CenterZ=0 NormalX=0 NormalY=0 NormalZ=1 MajorRadius=6.93002 MinorRadius=6.36273 AngleXU=-3.13976
    g81: Ellipse CenterX=-22.8436 CenterY=20.1783 CenterZ=0 NormalX=0 NormalY=0 NormalZ=1 MajorRadius=3.31512 MinorRadius=2.71052 AngleXU=-1.60214
    g82: GeomPoint X=-22.9034 Y=18.2706 Z=0
    g83: GeomPoint X=-22.7838 Y=22.0861 Z=0
    g84: GeomPoint X=-25.5897 Y=20.1733 Z=0
    g85: GeomPoint X=-20.0976 Y=20.1833 Z=0
    g86: Ellipse CenterX=-22.8436 CenterY=20.1783 CenterZ=0 NormalX=0 NormalY=0 NormalZ=1 MajorRadius=6.93002 MinorRadius=6.36273 AngleXU=-3.13976
    g87: LineSegment StartX=-101.889 StartY=14.1107 StartZ=0 EndX=-97.7455 EndY=14.1107 EndZ=0
    g88: LineSegment StartX=-93.8155 StartY=14.1107 StartZ=0 EndX=-89.6755 EndY=14.1107 EndZ=0
    g89: LineSegment StartX=-85.7455 StartY=14.1107 StartZ=0 EndX=-81.6055 EndY=14.1107 EndZ=0
    g90: LineSegment StartX=-101.889 StartY=14.1107 StartZ=0 EndX=-101.889 EndY=25.9907 EndZ=0
    g91: LineSegment StartX=-101.889 StartY=25.9907 StartZ=0 EndX=-97.8594 EndY=25.9907 EndZ=0
    g92: LineSegment StartX=-97.8594 StartY=25.9907 StartZ=0 EndX=-97.8594 EndY=24.0907 EndZ=0
    g93: LineSegment StartX=-97.7455 StartY=14.1107 StartZ=0 EndX=-97.7455 EndY=19.9107 EndZ=0
    g94: LineSegment StartX=-89.6755 StartY=14.1107 StartZ=0 EndX=-89.6755 EndY=19.9107 EndZ=0
    g95: LineSegment StartX=-93.8155 StartY=14.1107 StartZ=0 EndX=-93.8155 EndY=21.0107 EndZ=0
    g96-g106: Circle x11 (B-spline internal-alignment scaffolding for g107; pole/knot coordinates omitted)
    g107: BSplineCurve PolesCount=11 KnotsCount=9 Degree=3 IsPeriodic=0
    g108-g116: GeomPoint x9 (B-spline internal-alignment scaffolding for g107; pole/knot coordinates omitted)
    g117: BSplineCurve PolesCount=11 KnotsCount=9 Degree=3 IsPeriodic=0
    g118-g125: Circle x8 (B-spline internal-alignment scaffolding for g126; pole/knot coordinates omitted)
    g126: BSplineCurve PolesCount=8 KnotsCount=6 Degree=3 IsPeriodic=0
    g127-g132: GeomPoint x6 (B-spline internal-alignment scaffolding for g126; pole/knot coordinates omitted)
    g133: BSplineCurve PolesCount=8 KnotsCount=6 Degree=3 IsPeriodic=0
    g134: LineSegment StartX=-85.7455 StartY=21.0107 StartZ=0 EndX=-85.7455 EndY=14.1107 EndZ=0
    g135: LineSegment StartX=-80.0879 StartY=14.1107 StartZ=0 EndX=-75.944 EndY=14.1107 EndZ=0
    g136: LineSegment StartX=-72.014 StartY=14.1107 StartZ=0 EndX=-67.874 EndY=14.1107 EndZ=0
    g137: LineSegment StartX=-63.944 StartY=14.1107 StartZ=0 EndX=-59.804 EndY=14.1107 EndZ=0
    g138: LineSegment StartX=-80.0879 StartY=14.1107 StartZ=0 EndX=-80.0879 EndY=25.9907 EndZ=0
    g139: LineSegment StartX=-80.0879 StartY=25.9907 StartZ=0 EndX=-76.0579 EndY=25.9907 EndZ=0
    g140: LineSegment StartX=-76.0579 StartY=25.9907 StartZ=0 EndX=-76.0579 EndY=24.0907 EndZ=0
    g141: LineSegment StartX=-75.944 StartY=14.1107 StartZ=0 EndX=-75.944 EndY=19.9107 EndZ=0
    g142: LineSegment StartX=-67.874 StartY=14.1107 StartZ=0 EndX=-67.874 EndY=19.9107 EndZ=0
    g143: LineSegment StartX=-72.014 StartY=14.1107 StartZ=0 EndX=-72.014 EndY=21.0107 EndZ=0
    g144-g148: Circle x5 (B-spline internal-alignment scaffolding for g149; pole/knot coordinates omitted)
    g149: BSplineCurve PolesCount=11 KnotsCount=9 Degree=3 IsPeriodic=0
    g150-g158: GeomPoint x9 (B-spline internal-alignment scaffolding for g149; pole/knot coordinates omitted)
    g159: BSplineCurve PolesCount=11 KnotsCount=9 Degree=3 IsPeriodic=0
    g160-g167: Circle x8 (B-spline internal-alignment scaffolding for g168; pole/knot coordinates omitted)
    g168: BSplineCurve PolesCount=8 KnotsCount=6 Degree=3 IsPeriodic=0
    g169-g174: GeomPoint x6 (B-spline internal-alignment scaffolding for g168; pole/knot coordinates omitted)
    g175: BSplineCurve PolesCount=8 KnotsCount=6 Degree=3 IsPeriodic=0
    g176: LineSegment StartX=-63.944 StartY=21.0107 StartZ=0 EndX=-63.944 EndY=14.1107 EndZ=0
    g177: LineSegment StartX=-59.804 StartY=14.1107 StartZ=0 EndX=-59.804 EndY=21.5868 EndZ=0
    g178: BSplineCurve PolesCount=4 KnotsCount=2 Degree=3 IsPeriodic=0
    g179: GeomPoint X=-59.804 Y=21.5868 Z=0
    g180: GeomPoint X=-60.2379 Y=24.0907 Z=0
    g181: LineSegment StartX=-81.6055 StartY=14.1107 StartZ=0 EndX=-81.6055 EndY=21.5868 EndZ=0
    g182: LineSegment StartX=-151.619 StartY=24.0313 StartZ=0 EndX=-145.128 EndY=24.0313 EndZ=0
    g183: Circle CenterX=-82.0394 CenterY=24.0907 CenterZ=0 NormalX=0 NormalY=0 NormalZ=1 AngleXU=0 Radius=1
    g184: Circle CenterX=-81.7131 CenterY=23.2736 CenterZ=0 NormalX=0 NormalY=0 NormalZ=1 AngleXU=0 Radius=1
    g185: Circle CenterX=-81.6055 CenterY=21.5868 CenterZ=0 NormalX=0 NormalY=0 NormalZ=1 AngleXU=0 Radius=1
    g186: BSplineCurve PolesCount=3 KnotsCount=2 Degree=2 IsPeriodic=0
    g187: GeomPoint X=-82.0394 Y=24.0907 Z=0
    g188: GeomPoint X=-81.6055 Y=21.5868 Z=0
    g189: Ellipse CenterX=-37.3522 CenterY=19.9515 CenterZ=0 NormalX=0 NormalY=0 NormalZ=1 MajorRadius=2.99755 MinorRadius=2.49 AngleXU=1.5708
    g190: GeomPoint X=-37.3522 Y=21.6203 Z=0
    g191: GeomPoint X=-37.3522 Y=18.2826 Z=0
    g192: ArcOfEllipse CenterX=-38.7647 CenterY=20.06 CenterZ=0 NormalX=0 NormalY=0 NormalZ=1 MajorRadius=6.30025 MinorRadius=5.3849 AngleXU=1.57276 StartAngle=5.50632 EndAngle=10.3035
    g193: GeomPoint X=-38.7711 Y=23.3304 Z=0
    g194: GeomPoint X=-38.7583 Y=16.7895 Z=0
    g195: LineSegment StartX=-34.6109 StartY=14.1107 StartZ=0 EndX=-30.8984 EndY=14.1107 EndZ=0
    g196: LineSegment StartX=-30.8984 StartY=14.1107 StartZ=0 EndX=-30.8984 EndY=31.1784 EndZ=0
    g197: LineSegment StartX=-30.8984 StartY=31.1784 StartZ=0 EndX=-34.9984 EndY=31.1784 EndZ=0
    g198: LineSegment StartX=-34.9984 StartY=24.5602 StartZ=0 EndX=-34.9984 EndY=31.1784 EndZ=0
    g199: LineSegment StartX=-34.6109 StartY=16.0476 StartZ=0 EndX=-34.6109 EndY=14.1107 EndZ=0
    g200: LineSegment StartX=-14.8781 StartY=14.1107 StartZ=0 EndX=-10.5106 EndY=14.1107 EndZ=0
    g201: LineSegment StartX=-14.8781 StartY=14.1107 StartZ=0 EndX=-14.8781 EndY=25.8504 EndZ=0
    g202: LineSegment StartX=-14.8781 StartY=25.8504 StartZ=0 EndX=-10.8534 EndY=25.8504 EndZ=0
    g203: LineSegment StartX=-10.8534 StartY=25.8504 StartZ=0 EndX=-10.8534 EndY=24.0923 EndZ=0
    g204: LineSegment StartX=-10.5106 StartY=14.1107 StartZ=0 EndX=-10.5106 EndY=19.7752 EndZ=0
    g205: LineSegment StartX=-5.96397 StartY=25.9304 StartZ=0 EndX=-5.96397 EndY=22.574 EndZ=0
    g206-g214: Circle x9 (B-spline internal-alignment scaffolding for g215; pole/knot coordinates omitted)
    g215: BSplineCurve PolesCount=9 KnotsCount=7 Degree=3 IsPeriodic=0
    g216-g222: GeomPoint x7 (B-spline internal-alignment scaffolding for g215; pole/knot coordinates omitted)
    g223-g232: Circle x10 (B-spline internal-alignment scaffolding for g233; pole/knot coordinates omitted)
    g233: BSplineCurve PolesCount=10 KnotsCount=8 Degree=3 IsPeriodic=0
    g234-g241: GeomPoint x8 (B-spline internal-alignment scaffolding for g233; pole/knot coordinates omitted)
    g242: LineSegment StartX=-1.58923 StartY=21.0696 StartZ=0 EndX=2.62034 EndY=21.0696 EndZ=0
    g243: LineSegment StartX=-1.55856 StartY=18.7342 StartZ=0 EndX=6.45946 EndY=18.7342 EndZ=0
    g244: LineSegment StartX=5.29231 StartY=17.386 StartZ=0 EndX=5.29231 EndY=14.3674 EndZ=0
    g245-g269: Circle x25 (B-spline internal-alignment scaffolding for g270; pole/knot coordinates omitted)
    g270: BSplineCurve PolesCount=25 KnotsCount=23 Degree=3 IsPeriodic=0
    g271-g293: GeomPoint x23 (B-spline internal-alignment scaffolding for g270; pole/knot coordinates omitted)
    g294-g304: Circle x11 (B-spline internal-alignment scaffolding for g305; pole/knot coordinates omitted)
    g305: BSplineCurve PolesCount=11 KnotsCount=9 Degree=3 IsPeriodic=0
    g306-g314: GeomPoint x9 (B-spline internal-alignment scaffolding for g305; pole/knot coordinates omitted)
    g315-g326: Circle x12 (B-spline internal-alignment scaffolding for g327; pole/knot coordinates omitted)
    g327: BSplineCurve PolesCount=12 KnotsCount=10 Degree=3 IsPeriodic=0
    g328-g337: GeomPoint x10 (B-spline internal-alignment scaffolding for g327; pole/knot coordinates omitted)
  constraints (252):
    c: Coincident(g1,g0)
    c: Horizontal(g0)
    c: Vertical(g1)
    c: Coincident(g2,g3)
    c: Coincident(g3,g4)
    c: Horizontal(g4)
    c: Horizontal(g2)
    c: Vertical(g3)
    c: Block(g1)
    c: Distance(g3) = 4.86
    c: Block(g4)
    c: Distance(g0) = 10.8
    c: Distance(g2) = 10.8
    c: Coincident(g5,g0)
    c: Coincident(g6,g4)
    c: Coincident(g6,g2)
    c: Block(g8)
    c: Block(g7)
    c: Coincident(g9,g8)
    c: Coincident(g9,g7)
    c: Vertical(g9)
    c: Coincident(g10,g7)
    c: Coincident(g10,g8)
    c: Vertical(g10)
    c: Weight(g11) = 1
    c: Equal(g11, g12-g21) x10
    c: InternalAlignment(g11-g21 -> g22) x11
    c: InternalAlignment(g23-g31 -> g22) x9
    c: Block(g22)
    c: Weight(g32) = 1
    c: Equal(g32, g33-g49) x17
    c: InternalAlignment(g32-g49 -> g50) x18
    c: InternalAlignment(g51-g66 -> g50) x16
    c: Block(g50)
    c: Coincident(g67,g50)
    c: Coincident(g67,g22)
    c: Coincident(g68,g22)
    c: Coincident(g68,g50)
    c: InternalAlignment(g70,g69)
    c: InternalAlignment(g71,g69)
    c: Block(g69)
    c: InternalAlignment(g73,g72)
    c: InternalAlignment(g74,g72)
    c: Block(g72)
    c: InternalAlignment(g76,g75)
    c: InternalAlignment(g77,g75)
    c: InternalAlignment(g78,g80)
    c: InternalAlignment(g79,g80)
    c: Block(g80)
    c: Coincident(g75,g80)
    c: Block(g75)
    c: InternalAlignment(g82,g81)
    c: InternalAlignment(g83,g81)
    c: InternalAlignment(g84,g86)
    c: InternalAlignment(g85,g86)
    c: Block(g86)
    c: Coincident(g81,g86)
    c: Block(g81)
    c: Horizontal(g87)
    c: Block(g87)
    c: Horizontal(g88)
    c: Distance(g88) = 4.14
    c: Horizontal(g89)
    c: Equal(g88,g89) = 4.14
    c: Block(g89)
    c: Block(g88)
    c: Coincident(g90,g87)
    c: Vertical(g90)
    c: Distance(g90) = 11.88
    c: Coincident(g91,g90)
    c: Horizontal(g91)
    c: Coincident(g92,g91)
    c: Vertical(g92)
    c: Distance(g91) = 4.03
    c: Distance(g92) = 1.9
    c: Coincident(g93,g87)
    c: Vertical(g93)
    c: Vertical(g94)
    c: Coincident(g94,g88)
    c: Distance(g93) = 5.8
    c: Distance(g94) = 5.8
    c: Vertical(g95)
    c: Coincident(g95,g88)
    c: Distance(g95) = 6.9
    c: Coincident(g107,g92)
    c: Weight(g96) = 1
    c: Equal(g96, g97-g106) x10
    c: InternalAlignment(g96-g106 -> g107) x11
    c: InternalAlignment(g108-g116 -> g107) x9
    c: Block(g107)
    c: Block(g117)
    c: Coincident(g126,g93)
    c: Weight(g118) = 1
    c: Equal(g118, g119-g125) x7
    c: Coincident(g126,g95)
    c: InternalAlignment(g118-g125 -> g126) x8
    c: InternalAlignment(g127-g132 -> g126) x6
    c: Coincident(g133,g94)
    c: Block(g126)
    c: Block(g133)
    c: Coincident(g134,g133)
    c: Coincident(g134,g89)
    c: Vertical(g134)
    c: Horizontal(g135)
    c: Block(g135)
    c: Horizontal(g136)
    c: Equal(g88,g136) = 4.14
    c: Horizontal(g137)
    c: Equal(g136,g137) = 4.14
    c: Block(g137)
    c: Block(g136)
    c: Coincident(g138,g135)
    c: Vertical(g138)
    c: Equal(g90,g138) = 11.88
    c: Coincident(g139,g138)
    c: Horizontal(g139)
    c: Coincident(g140,g139)
    c: Vertical(g140)
    c: Equal(g91,g139) = 4.03
    c: Equal(g92,g140) = 1.9
    c: Coincident(g141,g135)
    c: Vertical(g141)
    c: Vertical(g142)
    c: Coincident(g142,g136)
    c: Equal(g93,g141) = 5.8
    c: Equal(g94,g142) = 5.8
    c: Vertical(g143)
    c: Coincident(g143,g136)
    c: Equal(g95,g143) = 6.9
    c: Coincident(g149,g140)
    c: Equal(g96,g144) = 1
    c: Equal(g144, g145-g148) x4
    c: InternalAlignment(g144-g148 -> g149) x5
    c: InternalAlignment(g150-g158 -> g149) x9
    c: Block(g149)
    c: Block(g159)
    c: Coincident(g168,g141)
    c: Equal(g118,g160) = 1
    c: Equal(g160, g161-g167) x7
    c: Coincident(g168,g143)
    c: InternalAlignment(g160-g167 -> g168) x8
    c: InternalAlignment(g169-g174 -> g168) x6
    c: Coincident(g175,g142)
    c: Block(g168)
    c: Block(g175)
    c: Coincident(g176,g175)
    c: Coincident(g176,g137)
    c: Vertical(g176)
    c: Coincident(g177,g137)
    c: Vertical(g177)
    c: Coincident(g178,g177)
    c: Coincident(g178,g159)
    c: InternalAlignment(g179,g178)
    c: InternalAlignment(g180,g178)
    c: Block(g178)
    c: Vertical(g181)
    c: Coincident(g181,g89)
    c: Block(g5)
    c: Coincident(g182,g1)
    c: Coincident(g182,g5)
    c: Horizontal(g182)
    c: Coincident(g186,g117)
    c: Weight(g183) = 1
    c: Equal(g183,g184)
    c: Equal(g183,g185)
    c: Coincident(g186,g181)
    c: InternalAlignment(g183,g186)
    c: InternalAlignment(g184,g186)
    c: InternalAlignment(g185,g186)
    c: InternalAlignment(g187,g186)
    c: InternalAlignment(g188,g186)
    c: Block(g186)
    c: InternalAlignment(g190,g189)
    c: InternalAlignment(g191,g189)
    c: Block(g189)
    c: InternalAlignment(g193,g192)
    c: InternalAlignment(g194,g192)
    c: Block(g192)
    c: Horizontal(g195)
    c: Block(g195)
    c: Coincident(g196,g195)
    c: Vertical(g196)
    c: Block(g196)
    c: Distance(g195) = 3.71244
    c: Coincident(g197,g196)
    c: Horizontal(g197)
    c: Distance(g197) = 4.1
    c: Coincident(g198,g192)
    c: Coincident(g198,g197)
    c: Vertical(g198)
    c: Block(g198)
    c: Coincident(g199,g192)
    c: Coincident(g199,g195)
    c: Vertical(g199)
    c: Block(g199)
    c: Horizontal(g200)
    c: Block(g200)
    c: Coincident(g201,g200)
    c: Vertical(g201)
    c: Block(g201)
    c: Coincident(g202,g201)
    c: Horizontal(g202)
    c: Block(g202)
    c: Coincident(g203,g202)
    c: Vertical(g203)
    c: Block(g203)
    c: Coincident(g204,g200)
    c: Vertical(g204)
    c: Block(g204)
    c: Coincident(g215,g203)
    c: Weight(g206) = 1
    c: Equal(g206, g207-g214) x8
    c: Coincident(g215,g205)
    c: InternalAlignment(g206-g214 -> g215) x9
    c: InternalAlignment(g216-g222 -> g215) x7
    c: Coincident(g233,g204)
    c: Weight(g223) = 1
    c: Equal(g223, g224-g232) x9
    c: Coincident(g233,g205)
    c: InternalAlignment(g223-g232 -> g233) x10
    c: InternalAlignment(g234-g241 -> g233) x8
    c: Vertical(g205)
    c: Block(g205)
    c: Block(g215)
    c: Block(g233)
    c: Horizontal(g242)
    c: Horizontal(g243)
    c: Block(g242)
    c: Block(g243)
    c: Vertical(g244)
    c: Block(g244)
    c: Coincident(g270,g243)
    c: Weight(g245) = 1
    c: Equal(g245, g246-g269) x24
    c: Coincident(g270,g244)
    c: InternalAlignment(g245-g269 -> g270) x25
    c: InternalAlignment(g271-g293 -> g270) x23
    c: Coincident(g305,g242)
    c: Weight(g294) = 1
    c: Equal(g294, g295-g304) x10
    c: Coincident(g305,g242)
    c: InternalAlignment(g294-g304 -> g305) x11
    c: InternalAlignment(g306-g314 -> g305) x9
    c: Block(g305)
    c: Coincident(g327,g243)
    c: Weight(g315) = 1
    c: Equal(g315, g316-g326) x11
    c: Coincident(g327,g244)
    c: InternalAlignment(g315-g326 -> g327) x12
    c: InternalAlignment(g328-g337 -> g327) x10
    c: Block(g327)
    c: Block(g270)
FEATURE [Part::Extrusion] Extrude075  label="CommodoreLogoAndText002"
  Base = -> Sketch084
  Dir = (0,0,1)
  DirMode = 2
  FaceMakerClass = Part::FaceMakerBullseye
  LengthFwd = 10
  LengthRev = 0
  Solid = true
  Symmetric = false
FEATURE [Part::FeaturePython] Clone001  label="CommodoreLogoAndTextScale001"  # Draft clone (typed FeaturePython)
  AttacherType = Attacher::AttachEngine3D
  Fuse = false
  Objects = -> [Extrude075]
  Placement = pos=(112.566,5.37,73.6) rot=(0,0,1;0rad)
  Scale = (0.62,0.62,1)
FEATURE [Part::Cut] Cut073  label="sideA005"
  Base = -> Extrude002
  Tool = -> Part__Mirroring
FEATURE [Part::Cut] Cut074  label="sideB005"
  Base = -> Extrude028
  Tool = -> Clone001
FEATURE [Sketcher::SketchObject] Sketch085
  FullyConstrained = true
  Placement = pos=(0,0,0) rot=(-1,0,0;4.71239rad)
  sketch-geometry (10):
    g0: LineSegment StartX=0 StartY=0 StartZ=0 EndX=-7 EndY=0 EndZ=0
    g1: LineSegment StartX=-7 StartY=10 StartZ=0 EndX=-6.5 EndY=10 EndZ=0
    g2: LineSegment StartX=0 StartY=10 StartZ=0 EndX=-0.5 EndY=10 EndZ=0
    g3: ArcOfCircle CenterX=-3.5 CenterY=10 CenterZ=0 NormalX=0 NormalY=0 NormalZ=1 AngleXU=0 Radius=3 StartAngle=3.14159 EndAngle=6.28319
    g4: LineSegment StartX=-7 StartY=0 StartZ=0 EndX=-10.5 EndY=0 EndZ=0
    g5: LineSegment StartX=0 StartY=0 StartZ=0 EndX=3.5 EndY=0 EndZ=0
    g6: ArcOfCircle CenterX=-10.5 CenterY=3.5 CenterZ=0 NormalX=0 NormalY=0 NormalZ=1 AngleXU=0 Radius=3.5 StartAngle=4.71239 EndAngle=6.28319
    g7: ArcOfCircle CenterX=3.5 CenterY=3.5 CenterZ=0 NormalX=0 NormalY=0 NormalZ=1 AngleXU=0 Radius=3.5 StartAngle=3.14159 EndAngle=4.71239
    g8: LineSegment StartX=-7 StartY=3.5 StartZ=0 EndX=-7 EndY=10 EndZ=0
    g9: LineSegment StartX=0 StartY=10 StartZ=0 EndX=0 EndY=3.5 EndZ=0
  constraints (26):
    c: Coincident(g0,g-1)
    c: Horizontal(g0)
    c: Distance(g0) = 7
    c: Horizontal(g1)
    c: Distance(g1) = 0.5
    c: Horizontal(g2)
    c: Distance(g2) = 0.5
    c: Coincident(g3,g1)
    c: Coincident(g3,g2)
    c: Block(g3)
    c: Coincident(g4,g0)
    c: Horizontal(g4)
    c: Distance(g4) = 3.5
    c: Coincident(g5,g0)
    c: Distance(g5) = 3.5
    c: Horizontal(g5)
    c: Coincident(g6,g4)
    c: Block(g6)
    c: Coincident(g7,g5)
    c: Block(g7)
    c: Coincident(g8,g6)
    c: Coincident(g8,g1)
    c: Vertical(g8)
    c: Coincident(g9,g2)
    c: Coincident(g9,g7)
    c: Vertical(g9)
FEATURE [Part::Extrusion] Extrude076  label="backRightCasePillarSideBracket"
  Base = -> Sketch085
  Dir = (0,-1,3e-16)
  DirMode = 2
  FaceMakerClass = Part::FaceMakerBullseye
  LengthFwd = 6.7
  LengthRev = 0
  Placement = pos=(16,11.5,0) rot=(0,0,1;0rad)
  Solid = true
  Symmetric = false
FEATURE [Sketcher::SketchObject] Sketch086
  FullyConstrained = true
  Placement = pos=(0,0,0) rot=(1,0,0;1.5708rad)
  sketch-geometry (10):
    g0: LineSegment StartX=0 StartY=0 StartZ=0 EndX=-7 EndY=0 EndZ=0
    g1: LineSegment StartX=-7 StartY=10 StartZ=0 EndX=-6.5 EndY=10 EndZ=0
    g2: LineSegment StartX=0 StartY=10 StartZ=0 EndX=-0.5 EndY=10 EndZ=0
    g3: ArcOfCircle CenterX=-3.5 CenterY=10 CenterZ=0 NormalX=0 NormalY=0 NormalZ=1 AngleXU=0 Radius=3 StartAngle=3.14159 EndAngle=6.28319
    g4: LineSegment StartX=-7 StartY=0 StartZ=0 EndX=-10.5 EndY=0 EndZ=0
    g5: LineSegment StartX=0 StartY=0 StartZ=0 EndX=3.5 EndY=0 EndZ=0
    g6: ArcOfCircle CenterX=-10.5 CenterY=3.5 CenterZ=0 NormalX=0 NormalY=0 NormalZ=1 AngleXU=0 Radius=3.5 StartAngle=4.71239 EndAngle=6.28319
    g7: ArcOfCircle CenterX=3.5 CenterY=3.5 CenterZ=0 NormalX=0 NormalY=0 NormalZ=1 AngleXU=0 Radius=3.5 StartAngle=3.14159 EndAngle=4.71239
    g8: LineSegment StartX=-7 StartY=3.5 StartZ=0 EndX=-7 EndY=10 EndZ=0
    g9: LineSegment StartX=0 StartY=10 StartZ=0 EndX=0 EndY=3.5 EndZ=0
  constraints (26):
    c: Coincident(g0,g-1)
    c: Horizontal(g0)
    c: Distance(g0) = 7
    c: Horizontal(g1)
    c: Distance(g1) = 0.5
    c: Horizontal(g2)
    c: Distance(g2) = 0.5
    c: Coincident(g3,g1)
    c: Coincident(g3,g2)
    c: Block(g3)
    c: Coincident(g4,g0)
    c: Horizontal(g4)
    c: Distance(g4) = 3.5
    c: Coincident(g5,g0)
    c: Distance(g5) = 3.5
    c: Horizontal(g5)
    c: Coincident(g6,g4)
    c: Block(g6)
    c: Coincident(g7,g5)
    c: Block(g7)
    c: Coincident(g8,g6)
    c: Coincident(g8,g1)
    c: Vertical(g8)
    c: Coincident(g9,g2)
    c: Coincident(g9,g7)
    c: Vertical(g9)
FEATURE [Part::Extrusion] Extrude077  label="backLeftCasePillarSideBracket001"
  Base = -> Sketch086
  Dir = (0,-1,3e-16)
  DirMode = 2
  FaceMakerClass = Part::FaceMakerBullseye
  LengthFwd = 6.7
  LengthRev = 0
  Placement = pos=(9,11.5,72) rot=(0,1,0;3.14159rad)
  Solid = true
  Symmetric = false
FEATURE [Sketcher::SketchObject] Sketch087
  FullyConstrained = true
  Placement = pos=(0,0,0) rot=(1,0,0;1.5708rad)
  sketch-geometry (8):
    g0: LineSegment StartX=0 StartY=4e-16 StartZ=0 EndX=-7 EndY=4e-16 EndZ=0
    g1: LineSegment StartX=-7 StartY=4e-16 StartZ=0 EndX=-10.5 EndY=4e-16 EndZ=0
    g2: LineSegment StartX=0 StartY=4e-16 StartZ=0 EndX=3.5 EndY=4e-16 EndZ=0
    g3: ArcOfCircle CenterX=-10.5 CenterY=3.5 CenterZ=0 NormalX=0 NormalY=0 NormalZ=1 AngleXU=0 Radius=3.5 StartAngle=4.71239 EndAngle=6.28319
    g4: ArcOfCircle CenterX=3.5 CenterY=3.5 CenterZ=0 NormalX=0 NormalY=0 NormalZ=1 AngleXU=0 Radius=3.5 StartAngle=3.14159 EndAngle=4.71239
    g5: ArcOfCircle CenterX=-3.5 CenterY=3.5 CenterZ=0 NormalX=0 NormalY=0 NormalZ=1 AngleXU=0 Radius=3 StartAngle=3.14159 EndAngle=6.28319
    g6: LineSegment StartX=-7 StartY=3.5 StartZ=0 EndX=-6.5 EndY=3.5 EndZ=0
    g7: LineSegment StartX=-0.5 StartY=3.5 StartZ=0 EndX=0 EndY=3.5 EndZ=0
  constraints (20):
    c: Coincident(g0,g-1)
    c: Horizontal(g0)
    c: Distance(g0) = 7
    c: Coincident(g1,g0)
    c: Horizontal(g1)
    c: Distance(g1) = 3.5
    c: Coincident(g2,g0)
    c: Distance(g2) = 3.5
    c: Horizontal(g2)
    c: Coincident(g3,g1)
    c: Block(g3)
    c: Coincident(g4,g2)
    c: Block(g4)
    c: Horizontal(g6)
    c: Coincident(g5,g6)
    c: Block(g5)
    c: Coincident(g6,g3)
    c: Coincident(g7,g5)
    c: Coincident(g7,g4)
    c: Horizontal(g7)
FEATURE [Part::Extrusion] Extrude078  label="frontBackLeftCasePillarSideBracket001"
  Base = -> Sketch087
  Dir = (0,-1,2e-16)
  DirMode = 2
  FaceMakerClass = Part::FaceMakerBullseye
  LengthFwd = 6.7
  LengthRev = 0
  Placement = pos=(93,11.5,0) rot=(0,0,1;0rad)
  Solid = true
  Symmetric = false
FEATURE [Sketcher::SketchObject] Sketch088
  FullyConstrained = true
  Placement = pos=(0,0,0) rot=(1,0,0;1.5708rad)
  sketch-geometry (8):
    g0: LineSegment StartX=0 StartY=4e-16 StartZ=0 EndX=-7 EndY=4e-16 EndZ=0
    g1: LineSegment StartX=-7 StartY=4e-16 StartZ=0 EndX=-10.5 EndY=4e-16 EndZ=0
    g2: LineSegment StartX=0 StartY=4e-16 StartZ=0 EndX=3.5 EndY=4e-16 EndZ=0
    g3: ArcOfCircle CenterX=-10.5 CenterY=3.5 CenterZ=0 NormalX=0 NormalY=0 NormalZ=1 AngleXU=0 Radius=3.5 StartAngle=4.71239 EndAngle=6.28319
    g4: ArcOfCircle CenterX=3.5 CenterY=3.5 CenterZ=0 NormalX=0 NormalY=0 NormalZ=1 AngleXU=0 Radius=3.5 StartAngle=3.14159 EndAngle=4.71239
    g5: ArcOfCircle CenterX=-3.5 CenterY=3.5 CenterZ=0 NormalX=0 NormalY=0 NormalZ=1 AngleXU=0 Radius=3 StartAngle=3.14159 EndAngle=6.28319
    g6: LineSegment StartX=-7 StartY=3.5 StartZ=0 EndX=-6.5 EndY=3.5 EndZ=0
    g7: LineSegment StartX=-0.5 StartY=3.5 StartZ=0 EndX=0 EndY=3.5 EndZ=0
  constraints (20):
    c: Coincident(g0,g-1)
    c: Horizontal(g0)
    c: Distance(g0) = 7
    c: Coincident(g1,g0)
    c: Horizontal(g1)
    c: Distance(g1) = 3.5
    c: Coincident(g2,g0)
    c: Distance(g2) = 3.5
    c: Horizontal(g2)
    c: Coincident(g3,g1)
    c: Block(g3)
    c: Coincident(g4,g2)
    c: Block(g4)
    c: Horizontal(g6)
    c: Coincident(g5,g6)
    c: Block(g5)
    c: Coincident(g6,g3)
    c: Coincident(g7,g5)
    c: Coincident(g7,g4)
    c: Horizontal(g7)
FEATURE [Part::Extrusion] Extrude079  label="frontFrontRightCasePillarSideBracket002"
  Base = -> Sketch088
  Dir = (0,-1,2e-16)
  DirMode = 2
  FaceMakerClass = Part::FaceMakerBullseye
  LengthFwd = 2
  LengthRev = 0
  Placement = pos=(106,11.5,72) rot=(0,1,0;3.14159rad)
  Solid = true
  Symmetric = false
FEATURE [Part::Chamfer] Chamfer
  Base = -> Extrude076
  Edges = 1 edges r=3: [Edge19]
FEATURE [Part::Chamfer] Chamfer002
  Base = -> Extrude077
  Edges = 1 edges r=3: [Edge7]
FEATURE [Part::Chamfer] Chamfer003  label="backLeftCasePillarSideBracket002"
  Base = -> Chamfer002
  Edges = 1 edges r=3.8: [Edge29]
FEATURE [Part::Chamfer] Chamfer004  label="backRightCasePillarSideBracket001"
  Base = -> Chamfer
  Edges = 1 edges r=3.8: [Edge24]
FEATURE [Sketcher::SketchObject] Sketch089
  FullyConstrained = true
  Placement = pos=(0,0,0) rot=(1,0,0;1.5708rad)
  sketch-geometry (8):
    g0: LineSegment StartX=0 StartY=4e-16 StartZ=0 EndX=-7 EndY=4e-16 EndZ=0
    g1: LineSegment StartX=-7 StartY=4e-16 StartZ=0 EndX=-10.5 EndY=4e-16 EndZ=0
    g2: LineSegment StartX=0 StartY=4e-16 StartZ=0 EndX=3.5 EndY=4e-16 EndZ=0
    g3: ArcOfCircle CenterX=-10.5 CenterY=3.5 CenterZ=0 NormalX=0 NormalY=0 NormalZ=1 AngleXU=0 Radius=3.5 StartAngle=4.71239 EndAngle=6.28319
    g4: ArcOfCircle CenterX=3.5 CenterY=3.5 CenterZ=0 NormalX=0 NormalY=0 NormalZ=1 AngleXU=0 Radius=3.5 StartAngle=3.14159 EndAngle=4.71239
    g5: ArcOfCircle CenterX=-3.5 CenterY=3.5 CenterZ=0 NormalX=0 NormalY=0 NormalZ=1 AngleXU=0 Radius=3 StartAngle=3.14159 EndAngle=6.28319
    g6: LineSegment StartX=-7 StartY=3.5 StartZ=0 EndX=-6.5 EndY=3.5 EndZ=0
    g7: LineSegment StartX=-0.5 StartY=3.5 StartZ=0 EndX=0 EndY=3.5 EndZ=0
  constraints (20):
    c: Coincident(g0,g-1)
    c: Horizontal(g0)
    c: Distance(g0) = 7
    c: Coincident(g1,g0)
    c: Horizontal(g1)
    c: Distance(g1) = 3.5
    c: Coincident(g2,g0)
    c: Distance(g2) = 3.5
    c: Horizontal(g2)
    c: Coincident(g3,g1)
    c: Block(g3)
    c: Coincident(g4,g2)
    c: Block(g4)
    c: Horizontal(g6)
    c: Coincident(g5,g6)
    c: Block(g5)
    c: Coincident(g6,g3)
    c: Coincident(g7,g5)
    c: Coincident(g7,g4)
    c: Horizontal(g7)
FEATURE [Part::Extrusion] Extrude080  label="frontBackLeftCasePillarSideBracket002"
  Base = -> Sketch089
  Dir = (0,-1,2e-16)
  DirMode = 2
  FaceMakerClass = Part::FaceMakerBullseye
  LengthFwd = 6.7
  LengthRev = 0
  Placement = pos=(86,11.5,72) rot=(0,1,0;3.14159rad)
  Solid = true
  Symmetric = false
FEATURE [Part::Box] Box037  label="Cube022"
  AttacherType = Attacher::AttachEngine3D
  Height = 14
  Length = 3.4
  Placement = pos=(0,10.8,0) rot=(0,1,0;0.785398rad)
  Width = 4
FEATURE [Part::Box] Box038  label="Cube023"
  AttacherType = Attacher::AttachEngine3D
  Height = 14
  Length = 3.4
  Placement = pos=(9.9,10.8,62.1) rot=(0,1,0;-0.785398rad)
  Width = 4
